# Revit family: QMXVP_with_1X3
name_source: partatom
category: Mechanical Equipment
units: mm (PartAtom-declared; Revit-internal decimal feet)

## family parameters
Always vertical = Yes
Cut with Voids When Loaded = No
Part Type = Normal
Room Calculation Point = No
Round Connector Dimension = Use Diameter
Shared = No
Work Plane-Based = No

## types (224) — shared parameters
0 = 0' - 0"
1" = 0' - 1"
1.5 = 0' - 1 1/2"
1/4 = 0' - 0 1/4"
135 = 135.00°
2" = 0' - 2"
2' = 2' - 0"
3" = 0' - 3"
3.125" = 0' - 3 1/8"
4" = 0' - 4"
5" = 0' - 5"
6" = 0' - 6"
Manufacturer = Loren Cook Company
ONE EIGTH = 0' - 0 1/8"
URL = www.lorencook.com

## per-type parameters (varying)
- 90_QMXVP-9L-1X3_Mixing_Box: (A/2)+.25"=1' - 2 1/4"; (A/2)-2"=1' - 0"; (NOZZLE_HEIGHT-(NOZZLE_HEIGHT/8*2))/2=0' - 10 1/2"; (NOZZLE_WB_OD-NOZZLE_TOP_OD)/2=0' - 2 3/8"; -A=-2' - 4"; A=2' - 4"; A+.5=2' - 4 1/2"; A/2=1' - 2"; B=5' - 5"; B/2=2' - 8 1/2"; C=2' - 6"; C/2=1' - 3"; DUAL_F=5' - 4 1/4"; DUAL_F+1"=5' - 5 1/4"; DUAL_G=5' - 3 5/16"; E=2' - 3 3/16"; GA=0' - 0 3/32"; LONG_RO=7' - 9 1/4"; MB_A=2' - 10"; MB_HT=2' - 5 3/16"; MB_HT+.25"=2' - 5 7/16"; MB_HT-2.75"=2' - 2 7/16"; MB_HT/2=1' - 2 19/32"; Model=QMXVP-1X3_Mixing Box; NOZZLE_BOTTOM_ID=1' - 0 13/16"; NOZZLE_BOTTOM_RAD=0' - 6 13/32"; NOZZLE_HEIGHT=2' - 4"; NOZZLE_HEIGHT/7*2=0' - 7"; NOZZLE_SIZE=9' - 0"; NOZZLE_TOP_OD=1' - 1 1/2"; NOZZLE_TOP_RAD=0' - 6 3/4"; NOZZLE_WB/4=0' - 4 19/32"; NOZZLE_WB_OD=1' - 11"; NOZZLE_WB_RAD=0' - 11 1/2"; NOZZLE_WB_RAD-2"=0' - 9 1/2"; RO=1' - 9"; RO/2=0' - 10 1/2"; RO2/2=0' - 10 1/2"; TRANSITION_TOP=3' - 1 1/16"; TRIPLE_F+1"=8' - 5"; TRIP_F=8' - 4"; TRIP_G=8' - 3 1/2"; TYPE=0' - 0"; Type Comments=Vari-Plume Laboratory Exhaust Mixed-Flow Inline Belt Drive With 1X3 Mixing Box; UNIT_HEIGHT=1' - 7 7/8"; UNIT_HEIGHT*.75=1' - 2 29/32"; UNIT_OD=1' - 0 13/16"; UNIT_RAD+((A/2)+.25")=1' - 8 21/32"; UNIT_RAD+((A/2)+.25")+4"=2' - 0 21/32"; UNIT_RADIUS=0' - 6 13/32"; UNIT_RADIUS*.6=0' - 5 25/32"; UNIT_RADIUS+4"=0' - 10 13/32"
- 490_QMXVP-49H-1X3_Mixing_Box: (A/2)+.25"=3' - 4 1/4"; (A/2)-2"=3' - 2"; (NOZZLE_HEIGHT-(NOZZLE_HEIGHT/8*2))/2=3' - 5 1/4"; (NOZZLE_WB_OD-NOZZLE_TOP_OD)/2=0' - 6 1/4"; -A=-6' - 8"; A=6' - 8"; A+.5=6' - 8 1/2"; A/2=3' - 4"; B=18' - 3"; B/2=9' - 1 1/2"; C=8' - 7"; C/2=4' - 3 1/2"; DUAL_F=16' - 0 3/4"; DUAL_F+1"=16' - 1 3/4"; DUAL_G=15' - 11"; E=6' - 6 1/2"; GA=0' - 0 1/8"; LONG_RO=24' - 9 1/4"; MB_A=9' - 5"; MB_HT=7' - 2 15/16"; MB_HT+.25"=7' - 3 3/16"; MB_HT-2.75"=7' - 0 3/16"; MB_HT/2=3' - 7 15/32"; Model=QMXVP-1X3_Mixing Box; NOZZLE_BOTTOM_ID=5' - 9 3/8"; NOZZLE_BOTTOM_RAD=2' - 10 11/16"; NOZZLE_HEIGHT=9' - 2"; NOZZLE_HEIGHT/7*2=2' - 3 1/2"; NOZZLE_SIZE=49' - 0"; NOZZLE_TOP_OD=6' - 4"; NOZZLE_TOP_RAD=3' - 2"; NOZZLE_WB/4=1' - 8 3/16"; NOZZLE_WB_OD=8' - 5"; NOZZLE_WB_RAD=4' - 2 1/2"; NOZZLE_WB_RAD-2"=4' - 0 1/2"; RO=6' - 0 1/4"; RO/2=3' - 0 1/8"; RO2/2=3' - 0 1/8"; TRANSITION_TOP=8' - 0 3/4"; TRIPLE_F+1"=25' - 6"; TRIP_F=25' - 5"; TRIP_G=25' - 3 1/2"; TYPE=0' - 0"; Type Comments=Vari-Plume Laboratory Exhaust Mixed-Flow Inline Belt Drive With 1X3 Mixing Box; UNIT_HEIGHT=6' - 8 1/2"; UNIT_HEIGHT*.75=5' - 0 3/8"; UNIT_OD=5' - 9 3/8"; UNIT_RAD+((A/2)+.25")=6' - 2 15/16"; UNIT_RAD+((A/2)+.25")+4"=6' - 6 15/16"; UNIT_RADIUS=2' - 10 11/16"; UNIT_RADIUS*.6=2' - 7 7/32"; UNIT_RADIUS+4"=3' - 2 11/16"
- 90_QMXVP-9H-1X3_Mixing_Box: (A/2)+.25"=1' - 2 1/4"; (A/2)-2"=1' - 0"; (NOZZLE_HEIGHT-(NOZZLE_HEIGHT/8*2))/2=0' - 10 1/2"; (NOZZLE_WB_OD-NOZZLE_TOP_OD)/2=0' - 2 3/8"; -A=-2' - 4"; A=2' - 4"; A+.5=2' - 4 1/2"; A/2=1' - 2"; B=5' - 5"; B/2=2' - 8 1/2"; C=2' - 6"; C/2=1' - 3"; DUAL_F=5' - 4 1/4"; DUAL_F+1"=5' - 5 1/4"; DUAL_G=5' - 3 5/16"; E=2' - 3 3/16"; GA=0' - 0 3/32"; LONG_RO=7' - 9 1/4"; MB_A=2' - 10"; MB_HT=2' - 5 3/16"; MB_HT+.25"=2' - 5 7/16"; MB_HT-2.75"=2' - 2 7/16"; MB_HT/2=1' - 2 19/32"; Model=QMXVP-1X3_Mixing Box; NOZZLE_BOTTOM_ID=1' - 0 13/16"; NOZZLE_BOTTOM_RAD=0' - 6 13/32"; NOZZLE_HEIGHT=2' - 4"; NOZZLE_HEIGHT/7*2=0' - 7"; NOZZLE_SIZE=9' - 0"; NOZZLE_TOP_OD=1' - 1 1/2"; NOZZLE_TOP_RAD=0' - 6 3/4"; NOZZLE_WB/4=0' - 4 19/32"; NOZZLE_WB_OD=1' - 11"; NOZZLE_WB_RAD=0' - 11 1/2"; NOZZLE_WB_RAD-2"=0' - 9 1/2"; RO=1' - 9"; RO/2=0' - 10 1/2"; RO2/2=0' - 10 1/2"; TRANSITION_TOP=3' - 1 1/16"; TRIPLE_F+1"=8' - 5"; TRIP_F=8' - 4"; TRIP_G=8' - 3 1/2"; TYPE=0' - 0"; Type Comments=Vari-Plume Laboratory Exhaust Mixed-Flow Inline Belt Drive With 1X3 Mixing Box; UNIT_HEIGHT=1' - 7 7/8"; UNIT_HEIGHT*.75=1' - 2 29/32"; UNIT_OD=1' - 0 13/16"; UNIT_RAD+((A/2)+.25")=1' - 8 21/32"; UNIT_RAD+((A/2)+.25")+4"=2' - 0 21/32"; UNIT_RADIUS=0' - 6 13/32"; UNIT_RADIUS*.6=0' - 5 25/32"; UNIT_RADIUS+4"=0' - 10 13/32"
- 120_QMXVP-9L-1X3_Mixing_Box: (A/2)+.25"=1' - 2 1/4"; (A/2)-2"=1' - 0"; (NOZZLE_HEIGHT-(NOZZLE_HEIGHT/8*2))/2=0' - 10 1/2"; (NOZZLE_WB_OD-NOZZLE_TOP_OD)/2=0' - 2 3/8"; -A=-2' - 4"; A=2' - 4"; A+.5=2' - 4 1/2"; A/2=1' - 2"; B=5' - 11"; B/2=2' - 11 1/2"; C=3' - 1"; C/2=1' - 6 1/2"; DUAL_F=5' - 4 1/4"; DUAL_F+1"=5' - 5 1/4"; DUAL_G=5' - 3 5/16"; E=2' - 3 3/16"; GA=0' - 0 3/32"; LONG_RO=7' - 9 1/4"; MB_A=2' - 11"; MB_HT=2' - 7 7/16"; MB_HT+.25"=2' - 7 11/16"; MB_HT-2.75"=2' - 4 11/16"; MB_HT/2=1' - 3 23/32"; Model=QMXVP-1X3_Mixing Box; NOZZLE_BOTTOM_ID=1' - 0 13/16"; NOZZLE_BOTTOM_RAD=0' - 6 13/32"; NOZZLE_HEIGHT=2' - 4"; NOZZLE_HEIGHT/7*2=0' - 7"; NOZZLE_SIZE=9' - 0"; NOZZLE_TOP_OD=1' - 1 1/2"; NOZZLE_TOP_RAD=0' - 6 3/4"; NOZZLE_WB/4=0' - 4 19/32"; NOZZLE_WB_OD=1' - 11"; NOZZLE_WB_RAD=0' - 11 1/2"; NOZZLE_WB_RAD-2"=0' - 9 1/2"; RO=1' - 9"; RO/2=0' - 10 1/2"; RO2/2=0' - 10 1/2"; TRANSITION_TOP=3' - 7 3/16"; TRIPLE_F+1"=8' - 5"; TRIP_F=8' - 4"; TRIP_G=8' - 3 1/2"; TYPE=0' - 0"; Type Comments=Vari-Plume Laboratory Exhaust Mixed-Flow Inline Belt Drive With 1X3 Mixing Box; UNIT_HEIGHT=1' - 7 7/8"; UNIT_HEIGHT*.75=1' - 2 29/32"; UNIT_OD=1' - 5 1/16"; UNIT_RAD+((A/2)+.25")=1' - 10 25/32"; UNIT_RAD+((A/2)+.25")+4"=2' - 2 25/32"; UNIT_RADIUS=0' - 8 17/32"; UNIT_RADIUS*.6=0' - 7 11/16"; UNIT_RADIUS+4"=1' - 0 17/32"
- 120_QMXVP-9H-1X3_Mixing_Box: (A/2)+.25"=1' - 2 1/4"; (A/2)-2"=1' - 0"; (NOZZLE_HEIGHT-(NOZZLE_HEIGHT/8*2))/2=0' - 10 1/2"; (NOZZLE_WB_OD-NOZZLE_TOP_OD)/2=0' - 2 3/8"; -A=-2' - 4"; A=2' - 4"; A+.5=2' - 4 1/2"; A/2=1' - 2"; B=5' - 11"; B/2=2' - 11 1/2"; C=3' - 1"; C/2=1' - 6 1/2"; DUAL_F=5' - 4 1/4"; DUAL_F+1"=5' - 5 1/4"; DUAL_G=5' - 3 5/16"; E=2' - 3 3/16"; GA=0' - 0 3/32"; LONG_RO=7' - 9 1/4"; MB_A=2' - 11"; MB_HT=2' - 7 7/16"; MB_HT+.25"=2' - 7 11/16"; MB_HT-2.75"=2' - 4 11/16"; MB_HT/2=1' - 3 23/32"; Model=QMXVP-1X3_Mixing Box; NOZZLE_BOTTOM_ID=1' - 0 13/16"; NOZZLE_BOTTOM_RAD=0' - 6 13/32"; NOZZLE_HEIGHT=2' - 4"; NOZZLE_HEIGHT/7*2=0' - 7"; NOZZLE_SIZE=9' - 0"; NOZZLE_TOP_OD=1' - 1 1/2"; NOZZLE_TOP_RAD=0' - 6 3/4"; NOZZLE_WB/4=0' - 4 19/32"; NOZZLE_WB_OD=1' - 11"; NOZZLE_WB_RAD=0' - 11 1/2"; NOZZLE_WB_RAD-2"=0' - 9 1/2"; RO=1' - 9"; RO/2=0' - 10 1/2"; RO2/2=0' - 10 1/2"; TRANSITION_TOP=3' - 7 3/16"; TRIPLE_F+1"=8' - 5"; TRIP_F=8' - 4"; TRIP_G=8' - 3 1/2"; TYPE=0' - 0"; Type Comments=Vari-Plume Laboratory Exhaust Mixed-Flow Inline Belt Drive With 1X3 Mixing Box; UNIT_HEIGHT=1' - 7 7/8"; UNIT_HEIGHT*.75=1' - 2 29/32"; UNIT_OD=1' - 5 1/16"; UNIT_RAD+((A/2)+.25")=1' - 10 25/32"; UNIT_RAD+((A/2)+.25")+4"=2' - 2 25/32"; UNIT_RADIUS=0' - 8 17/32"; UNIT_RADIUS*.6=0' - 7 11/16"; UNIT_RADIUS+4"=1' - 0 17/32"
- 120_QMXVP-12L-1X3_Mixing_Box: (A/2)+.25"=1' - 2 1/4"; (A/2)-2"=1' - 0"; (NOZZLE_HEIGHT-(NOZZLE_HEIGHT/8*2))/2=1' - 0"; (NOZZLE_WB_OD-NOZZLE_TOP_OD)/2=0' - 2 1/8"; -A=-2' - 4"; A=2' - 4"; A+.5=2' - 4 1/2"; A/2=1' - 2"; B=5' - 11"; B/2=2' - 11 1/2"; C=3' - 1"; C/2=1' - 6 1/2"; DUAL_F=5' - 4 1/4"; DUAL_F+1"=5' - 5 1/4"; DUAL_G=5' - 3 5/16"; E=2' - 3 3/16"; GA=0' - 0 3/32"; LONG_RO=7' - 9 1/4"; MB_A=2' - 11"; MB_HT=2' - 7 7/16"; MB_HT+.25"=2' - 7 11/16"; MB_HT-2.75"=2' - 4 11/16"; MB_HT/2=1' - 3 23/32"; Model=QMXVP-1X3_Mixing Box; NOZZLE_BOTTOM_ID=1' - 5 1/16"; NOZZLE_BOTTOM_RAD=0' - 8 17/32"; NOZZLE_HEIGHT=2' - 8"; NOZZLE_HEIGHT/7*2=0' - 8"; NOZZLE_SIZE=12' - 0"; NOZZLE_TOP_OD=1' - 7 1/2"; NOZZLE_TOP_RAD=0' - 9 3/4"; NOZZLE_WB/4=0' - 5 19/32"; NOZZLE_WB_OD=2' - 4"; NOZZLE_WB_RAD=1' - 2"; NOZZLE_WB_RAD-2"=1' - 0"; RO=1' - 9"; RO/2=0' - 10 1/2"; RO2/2=0' - 10 1/2"; TRANSITION_TOP=3' - 3 7/16"; TRIPLE_F+1"=8' - 5"; TRIP_F=8' - 4"; TRIP_G=8' - 3 1/2"; TYPE=0' - 0"; Type Comments=Vari-Plume Laboratory Exhaust Mixed-Flow Inline Belt Drive With 1X3 Mixing Box; UNIT_HEIGHT=1' - 7 7/8"; UNIT_HEIGHT*.75=1' - 2 29/32"; UNIT_OD=1' - 5 1/16"; UNIT_RAD+((A/2)+.25")=1' - 10 25/32"; UNIT_RAD+((A/2)+.25")+4"=2' - 2 25/32"; UNIT_RADIUS=0' - 8 17/32"; UNIT_RADIUS*.6=0' - 7 11/16"; UNIT_RADIUS+4"=1' - 0 17/32"
- 120_QMXVP-12H-1X3_Mixing_Box: (A/2)+.25"=1' - 2 1/4"; (A/2)-2"=1' - 0"; (NOZZLE_HEIGHT-(NOZZLE_HEIGHT/8*2))/2=1' - 0"; (NOZZLE_WB_OD-NOZZLE_TOP_OD)/2=0' - 2 1/8"; -A=-2' - 4"; A=2' - 4"; A+.5=2' - 4 1/2"; A/2=1' - 2"; B=5' - 11"; B/2=2' - 11 1/2"; C=3' - 1"; C/2=1' - 6 1/2"; DUAL_F=5' - 4 1/4"; DUAL_F+1"=5' - 5 1/4"; DUAL_G=5' - 3 5/16"; E=2' - 3 3/16"; GA=0' - 0 3/32"; LONG_RO=7' - 9 1/4"; MB_A=2' - 11"; MB_HT=2' - 7 7/16"; MB_HT+.25"=2' - 7 11/16"; MB_HT-2.75"=2' - 4 11/16"; MB_HT/2=1' - 3 23/32"; Model=QMXVP-1X3_Mixing Box; NOZZLE_BOTTOM_ID=1' - 5 1/16"; NOZZLE_BOTTOM_RAD=0' - 8 17/32"; NOZZLE_HEIGHT=2' - 8"; NOZZLE_HEIGHT/7*2=0' - 8"; NOZZLE_SIZE=12' - 0"; NOZZLE_TOP_OD=1' - 7 1/2"; NOZZLE_TOP_RAD=0' - 9 3/4"; NOZZLE_WB/4=0' - 5 19/32"; NOZZLE_WB_OD=2' - 4"; NOZZLE_WB_RAD=1' - 2"; NOZZLE_WB_RAD-2"=1' - 0"; RO=1' - 9"; RO/2=0' - 10 1/2"; RO2/2=0' - 10 1/2"; TRANSITION_TOP=3' - 3 7/16"; TRIPLE_F+1"=8' - 5"; TRIP_F=8' - 4"; TRIP_G=8' - 3 1/2"; TYPE=0' - 0"; Type Comments=Vari-Plume Laboratory Exhaust Mixed-Flow Inline Belt Drive With 1X3 Mixing Box; UNIT_HEIGHT=1' - 7 7/8"; UNIT_HEIGHT*.75=1' - 2 29/32"; UNIT_OD=1' - 5 1/16"; UNIT_RAD+((A/2)+.25")=1' - 10 25/32"; UNIT_RAD+((A/2)+.25")+4"=2' - 2 25/32"; UNIT_RADIUS=0' - 8 17/32"; UNIT_RADIUS*.6=0' - 7 11/16"; UNIT_RADIUS+4"=1' - 0 17/32"
- 135_QMXVP-9L-1X3_Mixing_Box: (A/2)+.25"=1' - 2 1/4"; (A/2)-2"=1' - 0"; (NOZZLE_HEIGHT-(NOZZLE_HEIGHT/8*2))/2=0' - 10 1/2"; (NOZZLE_WB_OD-NOZZLE_TOP_OD)/2=0' - 2 3/8"; -A=-2' - 4"; A=2' - 4"; A+.5=2' - 4 1/2"; A/2=1' - 2"; B=6' - 5"; B/2=3' - 2 1/2"; C=3' - 3"; C/2=1' - 7 1/2"; DUAL_F=5' - 4 1/4"; DUAL_F+1"=5' - 5 1/4"; DUAL_G=5' - 3 5/16"; E=2' - 3 1/8"; GA=0' - 0 3/32"; LONG_RO=7' - 9 1/4"; MB_A=3' - 0"; MB_HT=2' - 9 7/16"; MB_HT+.25"=2' - 9 11/16"; MB_HT-2.75"=2' - 6 11/16"; MB_HT/2=1' - 4 23/32"; Model=QMXVP-1X3_Mixing Box; NOZZLE_BOTTOM_ID=1' - 0 13/16"; NOZZLE_BOTTOM_RAD=0' - 6 13/32"; NOZZLE_HEIGHT=2' - 4"; NOZZLE_HEIGHT/7*2=0' - 7"; NOZZLE_SIZE=9' - 0"; NOZZLE_TOP_OD=1' - 1 1/2"; NOZZLE_TOP_RAD=0' - 6 3/4"; NOZZLE_WB/4=0' - 4 19/32"; NOZZLE_WB_OD=1' - 11"; NOZZLE_WB_RAD=0' - 11 1/2"; NOZZLE_WB_RAD-2"=0' - 9 1/2"; RO=1' - 8 15/16"; RO/2=0' - 10 15/32"; RO2/2=0' - 10 15/32"; TRANSITION_TOP=4' - 0 11/16"; TRIPLE_F+1"=8' - 5"; TRIP_F=8' - 4"; TRIP_G=8' - 3 1/2"; TYPE=0' - 0"; Type Comments=Vari-Plume Laboratory Exhaust Mixed-Flow Inline Belt Drive With 1X3 Mixing Box; UNIT_HEIGHT=2' - 3"; UNIT_HEIGHT*.75=1' - 8 1/4"; UNIT_OD=1' - 7 1/4"; UNIT_RAD+((A/2)+.25")=1' - 11 7/8"; UNIT_RAD+((A/2)+.25")+4"=2' - 3 7/8"; UNIT_RADIUS=0' - 9 5/8"; UNIT_RADIUS*.6=0' - 8 21/32"; UNIT_RADIUS+4"=1' - 1 5/8"
- 135_QMXVP-9H-1X3_Mixing_Box: (A/2)+.25"=1' - 2 1/4"; (A/2)-2"=1' - 0"; (NOZZLE_HEIGHT-(NOZZLE_HEIGHT/8*2))/2=0' - 10 1/2"; (NOZZLE_WB_OD-NOZZLE_TOP_OD)/2=0' - 2 3/8"; -A=-2' - 4"; A=2' - 4"; A+.5=2' - 4 1/2"; A/2=1' - 2"; B=6' - 5"; B/2=3' - 2 1/2"; C=3' - 3"; C/2=1' - 7 1/2"; DUAL_F=5' - 4 1/4"; DUAL_F+1"=5' - 5 1/4"; DUAL_G=5' - 3 5/16"; E=2' - 3 1/8"; GA=0' - 0 3/32"; LONG_RO=7' - 9 1/4"; MB_A=3' - 0"; MB_HT=2' - 9 7/16"; MB_HT+.25"=2' - 9 11/16"; MB_HT-2.75"=2' - 6 11/16"; MB_HT/2=1' - 4 23/32"; Model=QMXVP-1X3_Mixing Box; NOZZLE_BOTTOM_ID=1' - 0 13/16"; NOZZLE_BOTTOM_RAD=0' - 6 13/32"; NOZZLE_HEIGHT=2' - 4"; NOZZLE_HEIGHT/7*2=0' - 7"; NOZZLE_SIZE=9' - 0"; NOZZLE_TOP_OD=1' - 1 1/2"; NOZZLE_TOP_RAD=0' - 6 3/4"; NOZZLE_WB/4=0' - 4 19/32"; NOZZLE_WB_OD=1' - 11"; NOZZLE_WB_RAD=0' - 11 1/2"; NOZZLE_WB_RAD-2"=0' - 9 1/2"; RO=1' - 8 15/16"; RO/2=0' - 10 15/32"; RO2/2=0' - 10 15/32"; TRANSITION_TOP=4' - 0 11/16"; TRIPLE_F+1"=8' - 5"; TRIP_F=8' - 4"; TRIP_G=8' - 3 1/2"; TYPE=0' - 0"; Type Comments=Vari-Plume Laboratory Exhaust Mixed-Flow Inline Belt Drive With 1X3 Mixing Box; UNIT_HEIGHT=2' - 3"; UNIT_HEIGHT*.75=1' - 8 1/4"; UNIT_OD=1' - 7 1/4"; UNIT_RAD+((A/2)+.25")=1' - 11 7/8"; UNIT_RAD+((A/2)+.25")+4"=2' - 3 7/8"; UNIT_RADIUS=0' - 9 5/8"; UNIT_RADIUS*.6=0' - 8 21/32"; UNIT_RADIUS+4"=1' - 1 5/8"
- 150_QMXVP-9L-1X3_Mixing_Box: (A/2)+.25"=1' - 3 1/4"; (A/2)-2"=1' - 1"; (NOZZLE_HEIGHT-(NOZZLE_HEIGHT/8*2))/2=0' - 10 1/2"; (NOZZLE_WB_OD-NOZZLE_TOP_OD)/2=0' - 2 3/8"; -A=-2' - 6"; A=2' - 6"; A+.5=2' - 6 1/2"; A/2=1' - 3"; B=7' - 3"; B/2=3' - 7 1/2"; C=3' - 6"; C/2=1' - 9"; DUAL_F=5' - 8 1/4"; DUAL_F+1"=5' - 9 1/4"; DUAL_G=5' - 7 5/16"; E=2' - 5 1/8"; GA=0' - 0 3/32"; LONG_RO=8' - 3 1/4"; MB_A=3' - 2"; MB_HT=2' - 11 3/16"; MB_HT+.25"=2' - 11 7/16"; MB_HT-2.75"=2' - 8 7/16"; MB_HT/2=1' - 5 19/32"; Model=QMXVP-1X3_Mixing Box; NOZZLE_BOTTOM_ID=1' - 0 13/16"; NOZZLE_BOTTOM_RAD=0' - 6 13/32"; NOZZLE_HEIGHT=2' - 4"; NOZZLE_HEIGHT/7*2=0' - 7"; NOZZLE_SIZE=9' - 0"; NOZZLE_TOP_OD=1' - 1 1/2"; NOZZLE_TOP_RAD=0' - 6 3/4"; NOZZLE_WB/4=0' - 4 19/32"; NOZZLE_WB_OD=1' - 11"; NOZZLE_WB_RAD=0' - 11 1/2"; NOZZLE_WB_RAD-2"=0' - 9 1/2"; RO=1' - 10 15/16"; RO/2=0' - 11 15/32"; RO2/2=0' - 11 15/32"; TRANSITION_TOP=4' - 6 1/4"; TRIPLE_F+1"=8' - 11"; TRIP_F=8' - 10"; TRIP_G=8' - 9 1/2"; TYPE=0' - 0"; Type Comments=Vari-Plume Laboratory Exhaust Mixed-Flow Inline Belt Drive With 1X3 Mixing Box; UNIT_HEIGHT=2' - 6"; UNIT_HEIGHT*.75=1' - 10 1/2"; UNIT_OD=1' - 9 3/8"; UNIT_RAD+((A/2)+.25")=2' - 1 15/16"; UNIT_RAD+((A/2)+.25")+4"=2' - 5 15/16"; UNIT_RADIUS=0' - 10 11/16"; UNIT_RADIUS*.6=0' - 9 5/8"; UNIT_RADIUS+4"=1' - 2 11/16"
- 135_QMXVP-12L-1X3_Mixing_Box: (A/2)+.25"=1' - 2 1/4"; (A/2)-2"=1' - 0"; (NOZZLE_HEIGHT-(NOZZLE_HEIGHT/8*2))/2=1' - 0"; (NOZZLE_WB_OD-NOZZLE_TOP_OD)/2=0' - 2 1/8"; -A=-2' - 4"; A=2' - 4"; A+.5=2' - 4 1/2"; A/2=1' - 2"; B=6' - 5"; B/2=3' - 2 1/2"; C=3' - 3"; C/2=1' - 7 1/2"; DUAL_F=5' - 4 1/4"; DUAL_F+1"=5' - 5 1/4"; DUAL_G=5' - 3 5/16"; E=2' - 3 1/8"; GA=0' - 0 3/32"; LONG_RO=7' - 9 1/4"; MB_A=3' - 0"; MB_HT=2' - 9 7/16"; MB_HT+.25"=2' - 9 11/16"; MB_HT-2.75"=2' - 6 11/16"; MB_HT/2=1' - 4 23/32"; Model=QMXVP-1X3_Mixing Box; NOZZLE_BOTTOM_ID=1' - 5 1/16"; NOZZLE_BOTTOM_RAD=0' - 8 17/32"; NOZZLE_HEIGHT=2' - 8"; NOZZLE_HEIGHT/7*2=0' - 8"; NOZZLE_SIZE=12' - 0"; NOZZLE_TOP_OD=1' - 7 1/2"; NOZZLE_TOP_RAD=0' - 9 3/4"; NOZZLE_WB/4=0' - 5 19/32"; NOZZLE_WB_OD=2' - 4"; NOZZLE_WB_RAD=1' - 2"; NOZZLE_WB_RAD-2"=1' - 0"; RO=1' - 8 15/16"; RO/2=0' - 10 15/32"; RO2/2=0' - 10 15/32"; TRANSITION_TOP=3' - 4 11/16"; TRIPLE_F+1"=8' - 5"; TRIP_F=8' - 4"; TRIP_G=8' - 3 1/2"; TYPE=0' - 0"; Type Comments=Vari-Plume Laboratory Exhaust Mixed-Flow Inline Belt Drive With 1X3 Mixing Box; UNIT_HEIGHT=2' - 3"; UNIT_HEIGHT*.75=1' - 8 1/4"; UNIT_OD=1' - 7 1/4"; UNIT_RAD+((A/2)+.25")=1' - 11 7/8"; UNIT_RAD+((A/2)+.25")+4"=2' - 3 7/8"; UNIT_RADIUS=0' - 9 5/8"; UNIT_RADIUS*.6=0' - 8 21/32"; UNIT_RADIUS+4"=1' - 1 5/8"
- 135_QMXVP-12H-1X3_Mixing_Box: (A/2)+.25"=1' - 2 1/4"; (A/2)-2"=1' - 0"; (NOZZLE_HEIGHT-(NOZZLE_HEIGHT/8*2))/2=1' - 0"; (NOZZLE_WB_OD-NOZZLE_TOP_OD)/2=0' - 2 1/8"; -A=-2' - 4"; A=2' - 4"; A+.5=2' - 4 1/2"; A/2=1' - 2"; B=6' - 5"; B/2=3' - 2 1/2"; C=3' - 3"; C/2=1' - 7 1/2"; DUAL_F=5' - 4 1/4"; DUAL_F+1"=5' - 5 1/4"; DUAL_G=5' - 3 5/16"; E=2' - 3 1/8"; GA=0' - 0 3/32"; LONG_RO=7' - 9 1/4"; MB_A=3' - 0"; MB_HT=2' - 9 7/16"; MB_HT+.25"=2' - 9 11/16"; MB_HT-2.75"=2' - 6 11/16"; MB_HT/2=1' - 4 23/32"; Model=QMXVP-1X3_Mixing Box; NOZZLE_BOTTOM_ID=1' - 5 1/16"; NOZZLE_BOTTOM_RAD=0' - 8 17/32"; NOZZLE_HEIGHT=2' - 8"; NOZZLE_HEIGHT/7*2=0' - 8"; NOZZLE_SIZE=12' - 0"; NOZZLE_TOP_OD=1' - 7 1/2"; NOZZLE_TOP_RAD=0' - 9 3/4"; NOZZLE_WB/4=0' - 5 19/32"; NOZZLE_WB_OD=2' - 4"; NOZZLE_WB_RAD=1' - 2"; NOZZLE_WB_RAD-2"=1' - 0"; RO=1' - 8 15/16"; RO/2=0' - 10 15/32"; RO2/2=0' - 10 15/32"; TRANSITION_TOP=3' - 4 11/16"; TRIPLE_F+1"=8' - 5"; TRIP_F=8' - 4"; TRIP_G=8' - 3 1/2"; TYPE=0' - 0"; Type Comments=Vari-Plume Laboratory Exhaust Mixed-Flow Inline Belt Drive With 1X3 Mixing Box; UNIT_HEIGHT=2' - 3"; UNIT_HEIGHT*.75=1' - 8 1/4"; UNIT_OD=1' - 7 1/4"; UNIT_RAD+((A/2)+.25")=1' - 11 7/8"; UNIT_RAD+((A/2)+.25")+4"=2' - 3 7/8"; UNIT_RADIUS=0' - 9 5/8"; UNIT_RADIUS*.6=0' - 8 21/32"; UNIT_RADIUS+4"=1' - 1 5/8"
- 150_QMXVP-9H-1X3_Mixing_Box: (A/2)+.25"=1' - 3 1/4"; (A/2)-2"=1' - 1"; (NOZZLE_HEIGHT-(NOZZLE_HEIGHT/8*2))/2=0' - 10 1/2"; (NOZZLE_WB_OD-NOZZLE_TOP_OD)/2=0' - 2 3/8"; -A=-2' - 6"; A=2' - 6"; A+.5=2' - 6 1/2"; A/2=1' - 3"; B=7' - 3"; B/2=3' - 7 1/2"; C=3' - 6"; C/2=1' - 9"; DUAL_F=5' - 8 1/4"; DUAL_F+1"=5' - 9 1/4"; DUAL_G=5' - 7 5/16"; E=2' - 5 1/8"; GA=0' - 0 3/32"; LONG_RO=8' - 3 1/4"; MB_A=3' - 2"; MB_HT=2' - 11 3/16"; MB_HT+.25"=2' - 11 7/16"; MB_HT-2.75"=2' - 8 7/16"; MB_HT/2=1' - 5 19/32"; Model=QMXVP-1X3_Mixing Box; NOZZLE_BOTTOM_ID=1' - 0 13/16"; NOZZLE_BOTTOM_RAD=0' - 6 13/32"; NOZZLE_HEIGHT=2' - 4"; NOZZLE_HEIGHT/7*2=0' - 7"; NOZZLE_SIZE=9' - 0"; NOZZLE_TOP_OD=1' - 1 1/2"; NOZZLE_TOP_RAD=0' - 6 3/4"; NOZZLE_WB/4=0' - 4 19/32"; NOZZLE_WB_OD=1' - 11"; NOZZLE_WB_RAD=0' - 11 1/2"; NOZZLE_WB_RAD-2"=0' - 9 1/2"; RO=1' - 10 15/16"; RO/2=0' - 11 15/32"; RO2/2=0' - 11 15/32"; TRANSITION_TOP=4' - 6 1/4"; TRIPLE_F+1"=8' - 11"; TRIP_F=8' - 10"; TRIP_G=8' - 9 1/2"; TYPE=0' - 0"; Type Comments=Vari-Plume Laboratory Exhaust Mixed-Flow Inline Belt Drive With 1X3 Mixing Box; UNIT_HEIGHT=2' - 6"; UNIT_HEIGHT*.75=1' - 10 1/2"; UNIT_OD=1' - 9 3/8"; UNIT_RAD+((A/2)+.25")=2' - 1 15/16"; UNIT_RAD+((A/2)+.25")+4"=2' - 5 15/16"; UNIT_RADIUS=0' - 10 11/16"; UNIT_RADIUS*.6=0' - 9 5/8"; UNIT_RADIUS+4"=1' - 2 11/16"
- 150_QMXVP-12L-1X3_Mixing_Box: (A/2)+.25"=1' - 3 1/4"; (A/2)-2"=1' - 1"; (NOZZLE_HEIGHT-(NOZZLE_HEIGHT/8*2))/2=1' - 0"; (NOZZLE_WB_OD-NOZZLE_TOP_OD)/2=0' - 2 1/8"; -A=-2' - 6"; A=2' - 6"; A+.5=2' - 6 1/2"; A/2=1' - 3"; B=7' - 3"; B/2=3' - 7 1/2"; C=3' - 6"; C/2=1' - 9"; DUAL_F=5' - 8 1/4"; DUAL_F+1"=5' - 9 1/4"; DUAL_G=5' - 7 5/16"; E=2' - 5 1/8"; GA=0' - 0 3/32"; LONG_RO=8' - 3 1/4"; MB_A=3' - 2"; MB_HT=2' - 11 3/16"; MB_HT+.25"=2' - 11 7/16"; MB_HT-2.75"=2' - 8 7/16"; MB_HT/2=1' - 5 19/32"; Model=QMXVP-1X3_Mixing Box; NOZZLE_BOTTOM_ID=1' - 5 1/16"; NOZZLE_BOTTOM_RAD=0' - 8 17/32"; NOZZLE_HEIGHT=2' - 8"; NOZZLE_HEIGHT/7*2=0' - 8"; NOZZLE_SIZE=12' - 0"; NOZZLE_TOP_OD=1' - 7 1/2"; NOZZLE_TOP_RAD=0' - 9 3/4"; NOZZLE_WB/4=0' - 5 19/32"; NOZZLE_WB_OD=2' - 4"; NOZZLE_WB_RAD=1' - 2"; NOZZLE_WB_RAD-2"=1' - 0"; RO=1' - 10 15/16"; RO/2=0' - 11 15/32"; RO2/2=0' - 11 15/32"; TRANSITION_TOP=3' - 10 1/4"; TRIPLE_F+1"=8' - 11"; TRIP_F=8' - 10"; TRIP_G=8' - 9 1/2"; TYPE=0' - 0"; Type Comments=Vari-Plume Laboratory Exhaust Mixed-Flow Inline Belt Drive With 1X3 Mixing Box; UNIT_HEIGHT=2' - 6"; UNIT_HEIGHT*.75=1' - 10 1/2"; UNIT_OD=1' - 9 3/8"; UNIT_RAD+((A/2)+.25")=2' - 1 15/16"; UNIT_RAD+((A/2)+.25")+4"=2' - 5 15/16"; UNIT_RADIUS=0' - 10 11/16"; UNIT_RADIUS*.6=0' - 9 5/8"; UNIT_RADIUS+4"=1' - 2 11/16"
- 150_QMXVP-12H-1X3_Mixing_Box: (A/2)+.25"=1' - 3 1/4"; (A/2)-2"=1' - 1"; (NOZZLE_HEIGHT-(NOZZLE_HEIGHT/8*2))/2=1' - 0"; (NOZZLE_WB_OD-NOZZLE_TOP_OD)/2=0' - 2 1/8"; -A=-2' - 6"; A=2' - 6"; A+.5=2' - 6 1/2"; A/2=1' - 3"; B=7' - 3"; B/2=3' - 7 1/2"; C=3' - 6"; C/2=1' - 9"; DUAL_F=5' - 8 1/4"; DUAL_F+1"=5' - 9 1/4"; DUAL_G=5' - 7 5/16"; E=2' - 5 1/8"; GA=0' - 0 3/32"; LONG_RO=8' - 3 1/4"; MB_A=3' - 2"; MB_HT=2' - 11 3/16"; MB_HT+.25"=2' - 11 7/16"; MB_HT-2.75"=2' - 8 7/16"; MB_HT/2=1' - 5 19/32"; Model=QMXVP-1X3_Mixing Box; NOZZLE_BOTTOM_ID=1' - 5 1/16"; NOZZLE_BOTTOM_RAD=0' - 8 17/32"; NOZZLE_HEIGHT=2' - 8"; NOZZLE_HEIGHT/7*2=0' - 8"; NOZZLE_SIZE=12' - 0"; NOZZLE_TOP_OD=1' - 7 1/2"; NOZZLE_TOP_RAD=0' - 9 3/4"; NOZZLE_WB/4=0' - 5 19/32"; NOZZLE_WB_OD=2' - 4"; NOZZLE_WB_RAD=1' - 2"; NOZZLE_WB_RAD-2"=1' - 0"; RO=1' - 10 15/16"; RO/2=0' - 11 15/32"; RO2/2=0' - 11 15/32"; TRANSITION_TOP=3' - 10 1/4"; TRIPLE_F+1"=8' - 11"; TRIP_F=8' - 10"; TRIP_G=8' - 9 1/2"; TYPE=0' - 0"; Type Comments=Vari-Plume Laboratory Exhaust Mixed-Flow Inline Belt Drive With 1X3 Mixing Box; UNIT_HEIGHT=2' - 6"; UNIT_HEIGHT*.75=1' - 10 1/2"; UNIT_OD=1' - 9 3/8"; UNIT_RAD+((A/2)+.25")=2' - 1 15/16"; UNIT_RAD+((A/2)+.25")+4"=2' - 5 15/16"; UNIT_RADIUS=0' - 10 11/16"; UNIT_RADIUS*.6=0' - 9 5/8"; UNIT_RADIUS+4"=1' - 2 11/16"
- 150_QMXVP-15L-1X3_Mixing_Box: (A/2)+.25"=1' - 3 1/4"; (A/2)-2"=1' - 1"; (NOZZLE_HEIGHT-(NOZZLE_HEIGHT/8*2))/2=1' - 4 1/8"; (NOZZLE_WB_OD-NOZZLE_TOP_OD)/2=0' - 3 1/4"; -A=-2' - 6"; A=2' - 6"; A+.5=2' - 6 1/2"; A/2=1' - 3"; B=7' - 3"; B/2=3' - 7 1/2"; C=3' - 6"; C/2=1' - 9"; DUAL_F=5' - 8 1/4"; DUAL_F+1"=5' - 9 1/4"; DUAL_G=5' - 7 5/16"; E=2' - 5 1/8"; GA=0' - 0 3/32"; LONG_RO=8' - 3 1/4"; MB_A=3' - 2"; MB_HT=2' - 11 3/16"; MB_HT+.25"=2' - 11 7/16"; MB_HT-2.75"=2' - 8 7/16"; MB_HT/2=1' - 5 19/32"; Model=QMXVP-1X3_Mixing Box; NOZZLE_BOTTOM_ID=1' - 9 3/8"; NOZZLE_BOTTOM_RAD=0' - 10 11/16"; NOZZLE_HEIGHT=3' - 7"; NOZZLE_HEIGHT/7*2=0' - 10 3/4"; NOZZLE_SIZE=15' - 0"; NOZZLE_TOP_OD=1' - 11"; NOZZLE_TOP_RAD=0' - 11 1/2"; NOZZLE_WB/4=0' - 7 3/16"; NOZZLE_WB_OD=3' - 0"; NOZZLE_WB_RAD=1' - 6"; NOZZLE_WB_RAD-2"=1' - 4"; RO=1' - 10 15/16"; RO/2=0' - 11 15/32"; RO2/2=0' - 11 15/32"; TRANSITION_TOP=3' - 7 5/16"; TRIPLE_F+1"=8' - 11"; TRIP_F=8' - 10"; TRIP_G=8' - 9 1/2"; TYPE=0' - 0"; Type Comments=Vari-Plume Laboratory Exhaust Mixed-Flow Inline Belt Drive With 1X3 Mixing Box; UNIT_HEIGHT=2' - 6"; UNIT_HEIGHT*.75=1' - 10 1/2"; UNIT_OD=1' - 9 3/8"; UNIT_RAD+((A/2)+.25")=2' - 1 15/16"; UNIT_RAD+((A/2)+.25")+4"=2' - 5 15/16"; UNIT_RADIUS=0' - 10 11/16"; UNIT_RADIUS*.6=0' - 9 5/8"; UNIT_RADIUS+4"=1' - 2 11/16"
- 150_QMXVP-15H-1X3_Mixing_Box: (A/2)+.25"=1' - 3 1/4"; (A/2)-2"=1' - 1"; (NOZZLE_HEIGHT-(NOZZLE_HEIGHT/8*2))/2=1' - 4 1/8"; (NOZZLE_WB_OD-NOZZLE_TOP_OD)/2=0' - 3 1/4"; -A=-2' - 6"; A=2' - 6"; A+.5=2' - 6 1/2"; A/2=1' - 3"; B=7' - 3"; B/2=3' - 7 1/2"; C=3' - 6"; C/2=1' - 9"; DUAL_F=5' - 8 1/4"; DUAL_F+1"=5' - 9 1/4"; DUAL_G=5' - 7 5/16"; E=2' - 5 1/8"; GA=0' - 0 3/32"; LONG_RO=8' - 3 1/4"; MB_A=3' - 2"; MB_HT=2' - 11 3/16"; MB_HT+.25"=2' - 11 7/16"; MB_HT-2.75"=2' - 8 7/16"; MB_HT/2=1' - 5 19/32"; Model=QMXVP-1X3_Mixing Box; NOZZLE_BOTTOM_ID=1' - 9 3/8"; NOZZLE_BOTTOM_RAD=0' - 10 11/16"; NOZZLE_HEIGHT=3' - 7"; NOZZLE_HEIGHT/7*2=0' - 10 3/4"; NOZZLE_SIZE=15' - 0"; NOZZLE_TOP_OD=1' - 11"; NOZZLE_TOP_RAD=0' - 11 1/2"; NOZZLE_WB/4=0' - 7 3/16"; NOZZLE_WB_OD=3' - 0"; NOZZLE_WB_RAD=1' - 6"; NOZZLE_WB_RAD-2"=1' - 4"; RO=1' - 10 15/16"; RO/2=0' - 11 15/32"; RO2/2=0' - 11 15/32"; TRANSITION_TOP=3' - 7 5/16"; TRIPLE_F+1"=8' - 11"; TRIP_F=8' - 10"; TRIP_G=8' - 9 1/2"; TYPE=0' - 0"; Type Comments=Vari-Plume Laboratory Exhaust Mixed-Flow Inline Belt Drive With 1X3 Mixing Box; UNIT_HEIGHT=2' - 6"; UNIT_HEIGHT*.75=1' - 10 1/2"; UNIT_OD=1' - 9 3/8"; UNIT_RAD+((A/2)+.25")=2' - 1 15/16"; UNIT_RAD+((A/2)+.25")+4"=2' - 5 15/16"; UNIT_RADIUS=0' - 10 11/16"; UNIT_RADIUS*.6=0' - 9 5/8"; UNIT_RADIUS+4"=1' - 2 11/16"
- 165_QMXVP-9L-1X3_Mixing_Box: (A/2)+.25"=1' - 4 1/4"; (A/2)-2"=1' - 2"; (NOZZLE_HEIGHT-(NOZZLE_HEIGHT/8*2))/2=0' - 10 1/2"; (NOZZLE_WB_OD-NOZZLE_TOP_OD)/2=0' - 2 3/8"; -A=-2' - 8"; A=2' - 8"; A+.5=2' - 8 1/2"; A/2=1' - 4"; B=7' - 5"; B/2=3' - 8 1/2"; C=3' - 8"; C/2=1' - 10"; DUAL_F=6' - 0 1/4"; DUAL_F+1"=6' - 1 1/4"; DUAL_G=5' - 11 5/16"; E=2' - 7 1/8"; GA=0' - 0 3/32"; LONG_RO=8' - 9 1/4"; MB_A=3' - 5"; MB_HT=3' - 0 15/16"; MB_HT+.25"=3' - 1 3/16"; MB_HT-2.75"=2' - 10 3/16"; MB_HT/2=1' - 6 15/32"; Model=QMXVP-1X3_Mixing Box; NOZZLE_BOTTOM_ID=1' - 0 13/16"; NOZZLE_BOTTOM_RAD=0' - 6 13/32"; NOZZLE_HEIGHT=2' - 4"; NOZZLE_HEIGHT/7*2=0' - 7"; NOZZLE_SIZE=9' - 0"; NOZZLE_TOP_OD=1' - 1 1/2"; NOZZLE_TOP_RAD=0' - 6 3/4"; NOZZLE_WB/4=0' - 4 19/32"; NOZZLE_WB_OD=1' - 11"; NOZZLE_WB_RAD=0' - 11 1/2"; NOZZLE_WB_RAD-2"=0' - 9 1/2"; RO=2' - 0 15/16"; RO/2=1' - 0 15/32"; RO2/2=1' - 0 15/32"; TRANSITION_TOP=5' - 1 1/4"; TRIPLE_F+1"=9' - 5"; TRIP_F=9' - 4"; TRIP_G=9' - 3 1/2"; TYPE=0' - 0"; Type Comments=Vari-Plume Laboratory Exhaust Mixed-Flow Inline Belt Drive With 1X3 Mixing Box; UNIT_HEIGHT=2' - 9"; UNIT_HEIGHT*.75=2' - 0 3/4"; UNIT_OD=1' - 11 1/2"; UNIT_RAD+((A/2)+.25")=2' - 4"; UNIT_RAD+((A/2)+.25")+4"=2' - 8"; UNIT_RADIUS=0' - 11 3/4"; UNIT_RADIUS*.6=0' - 10 9/16"; UNIT_RADIUS+4"=1' - 3 3/4"
- 165_QMXVP-9H-1X3_Mixing_Box: (A/2)+.25"=1' - 4 1/4"; (A/2)-2"=1' - 2"; (NOZZLE_HEIGHT-(NOZZLE_HEIGHT/8*2))/2=0' - 10 1/2"; (NOZZLE_WB_OD-NOZZLE_TOP_OD)/2=0' - 2 3/8"; -A=-2' - 8"; A=2' - 8"; A+.5=2' - 8 1/2"; A/2=1' - 4"; B=7' - 5"; B/2=3' - 8 1/2"; C=3' - 8"; C/2=1' - 10"; DUAL_F=6' - 0 1/4"; DUAL_F+1"=6' - 1 1/4"; DUAL_G=5' - 11 5/16"; E=2' - 7 1/8"; GA=0' - 0 3/32"; LONG_RO=8' - 9 1/4"; MB_A=3' - 5"; MB_HT=3' - 0 15/16"; MB_HT+.25"=3' - 1 3/16"; MB_HT-2.75"=2' - 10 3/16"; MB_HT/2=1' - 6 15/32"; Model=QMXVP-1X3_Mixing Box; NOZZLE_BOTTOM_ID=1' - 0 13/16"; NOZZLE_BOTTOM_RAD=0' - 6 13/32"; NOZZLE_HEIGHT=2' - 4"; NOZZLE_HEIGHT/7*2=0' - 7"; NOZZLE_SIZE=9' - 0"; NOZZLE_TOP_OD=1' - 1 1/2"; NOZZLE_TOP_RAD=0' - 6 3/4"; NOZZLE_WB/4=0' - 4 19/32"; NOZZLE_WB_OD=1' - 11"; NOZZLE_WB_RAD=0' - 11 1/2"; NOZZLE_WB_RAD-2"=0' - 9 1/2"; RO=2' - 0 15/16"; RO/2=1' - 0 15/32"; RO2/2=1' - 0 15/32"; TRANSITION_TOP=5' - 1 1/4"; TRIPLE_F+1"=9' - 5"; TRIP_F=9' - 4"; TRIP_G=9' - 3 1/2"; TYPE=0' - 0"; Type Comments=Vari-Plume Laboratory Exhaust Mixed-Flow Inline Belt Drive With 1X3 Mixing Box; UNIT_HEIGHT=2' - 9"; UNIT_HEIGHT*.75=2' - 0 3/4"; UNIT_OD=1' - 11 1/2"; UNIT_RAD+((A/2)+.25")=2' - 4"; UNIT_RAD+((A/2)+.25")+4"=2' - 8"; UNIT_RADIUS=0' - 11 3/4"; UNIT_RADIUS*.6=0' - 10 9/16"; UNIT_RADIUS+4"=1' - 3 3/4"
- 165_QMXVP-12L-1X3_Mixing_Box: (A/2)+.25"=1' - 4 1/4"; (A/2)-2"=1' - 2"; (NOZZLE_HEIGHT-(NOZZLE_HEIGHT/8*2))/2=1' - 0"; (NOZZLE_WB_OD-NOZZLE_TOP_OD)/2=0' - 2 1/8"; -A=-2' - 8"; A=2' - 8"; A+.5=2' - 8 1/2"; A/2=1' - 4"; B=7' - 5"; B/2=3' - 8 1/2"; C=3' - 8"; C/2=1' - 10"; DUAL_F=6' - 0 1/4"; DUAL_F+1"=6' - 1 1/4"; DUAL_G=5' - 11 5/16"; E=2' - 7 1/8"; GA=0' - 0 3/32"; LONG_RO=8' - 9 1/4"; MB_A=3' - 5"; MB_HT=3' - 0 15/16"; MB_HT+.25"=3' - 1 3/16"; MB_HT-2.75"=2' - 10 3/16"; MB_HT/2=1' - 6 15/32"; Model=QMXVP-1X3_Mixing Box; NOZZLE_BOTTOM_ID=1' - 5 1/16"; NOZZLE_BOTTOM_RAD=0' - 8 17/32"; NOZZLE_HEIGHT=2' - 8"; NOZZLE_HEIGHT/7*2=0' - 8"; NOZZLE_SIZE=12' - 0"; NOZZLE_TOP_OD=1' - 7 1/2"; NOZZLE_TOP_RAD=0' - 9 3/4"; NOZZLE_WB/4=0' - 5 19/32"; NOZZLE_WB_OD=2' - 4"; NOZZLE_WB_RAD=1' - 2"; NOZZLE_WB_RAD-2"=1' - 0"; RO=2' - 0 15/16"; RO/2=1' - 0 15/32"; RO2/2=1' - 0 15/32"; TRANSITION_TOP=4' - 5 1/4"; TRIPLE_F+1"=9' - 5"; TRIP_F=9' - 4"; TRIP_G=9' - 3 1/2"; TYPE=0' - 0"; Type Comments=Vari-Plume Laboratory Exhaust Mixed-Flow Inline Belt Drive With 1X3 Mixing Box; UNIT_HEIGHT=2' - 9"; UNIT_HEIGHT*.75=2' - 0 3/4"; UNIT_OD=1' - 11 1/2"; UNIT_RAD+((A/2)+.25")=2' - 4"; UNIT_RAD+((A/2)+.25")+4"=2' - 8"; UNIT_RADIUS=0' - 11 3/4"; UNIT_RADIUS*.6=0' - 10 9/16"; UNIT_RADIUS+4"=1' - 3 3/4"
- 165_QMXVP-12H-1X3_Mixing_Box: (A/2)+.25"=1' - 4 1/4"; (A/2)-2"=1' - 2"; (NOZZLE_HEIGHT-(NOZZLE_HEIGHT/8*2))/2=1' - 0"; (NOZZLE_WB_OD-NOZZLE_TOP_OD)/2=0' - 2 1/8"; -A=-2' - 8"; A=2' - 8"; A+.5=2' - 8 1/2"; A/2=1' - 4"; B=7' - 5"; B/2=3' - 8 1/2"; C=3' - 8"; C/2=1' - 10"; DUAL_F=6' - 0 1/4"; DUAL_F+1"=6' - 1 1/4"; DUAL_G=5' - 11 5/16"; E=2' - 7 1/8"; GA=0' - 0 3/32"; LONG_RO=8' - 9 1/4"; MB_A=3' - 5"; MB_HT=3' - 0 15/16"; MB_HT+.25"=3' - 1 3/16"; MB_HT-2.75"=2' - 10 3/16"; MB_HT/2=1' - 6 15/32"; Model=QMXVP-1X3_Mixing Box; NOZZLE_BOTTOM_ID=1' - 5 1/16"; NOZZLE_BOTTOM_RAD=0' - 8 17/32"; NOZZLE_HEIGHT=2' - 8"; NOZZLE_HEIGHT/7*2=0' - 8"; NOZZLE_SIZE=12' - 0"; NOZZLE_TOP_OD=1' - 7 1/2"; NOZZLE_TOP_RAD=0' - 9 3/4"; NOZZLE_WB/4=0' - 5 19/32"; NOZZLE_WB_OD=2' - 4"; NOZZLE_WB_RAD=1' - 2"; NOZZLE_WB_RAD-2"=1' - 0"; RO=2' - 0 15/16"; RO/2=1' - 0 15/32"; RO2/2=1' - 0 15/32"; TRANSITION_TOP=4' - 5 1/4"; TRIPLE_F+1"=9' - 5"; TRIP_F=9' - 4"; TRIP_G=9' - 3 1/2"; TYPE=0' - 0"; Type Comments=Vari-Plume Laboratory Exhaust Mixed-Flow Inline Belt Drive With 1X3 Mixing Box; UNIT_HEIGHT=2' - 9"; UNIT_HEIGHT*.75=2' - 0 3/4"; UNIT_OD=1' - 11 1/2"; UNIT_RAD+((A/2)+.25")=2' - 4"; UNIT_RAD+((A/2)+.25")+4"=2' - 8"; UNIT_RADIUS=0' - 11 3/4"; UNIT_RADIUS*.6=0' - 10 9/16"; UNIT_RADIUS+4"=1' - 3 3/4"
- 165_QMXVP-15L-1X3_Mixing_Box: (A/2)+.25"=1' - 4 1/4"; (A/2)-2"=1' - 2"; (NOZZLE_HEIGHT-(NOZZLE_HEIGHT/8*2))/2=1' - 4 1/8"; (NOZZLE_WB_OD-NOZZLE_TOP_OD)/2=0' - 3 1/4"; -A=-2' - 8"; A=2' - 8"; A+.5=2' - 8 1/2"; A/2=1' - 4"; B=7' - 5"; B/2=3' - 8 1/2"; C=3' - 8"; C/2=1' - 10"; DUAL_F=6' - 0 1/4"; DUAL_F+1"=6' - 1 1/4"; DUAL_G=5' - 11 5/16"; E=2' - 7 1/8"; GA=0' - 0 3/32"; LONG_RO=8' - 9 1/4"; MB_A=3' - 5"; MB_HT=3' - 0 15/16"; MB_HT+.25"=3' - 1 3/16"; MB_HT-2.75"=2' - 10 3/16"; MB_HT/2=1' - 6 15/32"; Model=QMXVP-1X3_Mixing Box; NOZZLE_BOTTOM_ID=1' - 9 3/8"; NOZZLE_BOTTOM_RAD=0' - 10 11/16"; NOZZLE_HEIGHT=3' - 7"; NOZZLE_HEIGHT/7*2=0' - 10 3/4"; NOZZLE_SIZE=15' - 0"; NOZZLE_TOP_OD=1' - 11"; NOZZLE_TOP_RAD=0' - 11 1/2"; NOZZLE_WB/4=0' - 7 3/16"; NOZZLE_WB_OD=3' - 0"; NOZZLE_WB_RAD=1' - 6"; NOZZLE_WB_RAD-2"=1' - 4"; RO=2' - 0 15/16"; RO/2=1' - 0 15/32"; RO2/2=1' - 0 15/32"; TRANSITION_TOP=3' - 9 5/16"; TRIPLE_F+1"=9' - 5"; TRIP_F=9' - 4"; TRIP_G=9' - 3 1/2"; TYPE=0' - 0"; Type Comments=Vari-Plume Laboratory Exhaust Mixed-Flow Inline Belt Drive With 1X3 Mixing Box; UNIT_HEIGHT=2' - 9"; UNIT_HEIGHT*.75=2' - 0 3/4"; UNIT_OD=1' - 11 1/2"; UNIT_RAD+((A/2)+.25")=2' - 4"; UNIT_RAD+((A/2)+.25")+4"=2' - 8"; UNIT_RADIUS=0' - 11 3/4"; UNIT_RADIUS*.6=0' - 10 9/16"; UNIT_RADIUS+4"=1' - 3 3/4"
- 165_QMXVP-15H-1X3_Mixing_Box: (A/2)+.25"=1' - 4 1/4"; (A/2)-2"=1' - 2"; (NOZZLE_HEIGHT-(NOZZLE_HEIGHT/8*2))/2=1' - 4 1/8"; (NOZZLE_WB_OD-NOZZLE_TOP_OD)/2=0' - 3 1/4"; -A=-2' - 8"; A=2' - 8"; A+.5=2' - 8 1/2"; A/2=1' - 4"; B=7' - 5"; B/2=3' - 8 1/2"; C=3' - 8"; C/2=1' - 10"; DUAL_F=6' - 0 1/4"; DUAL_F+1"=6' - 1 1/4"; DUAL_G=5' - 11 5/16"; E=2' - 7 1/8"; GA=0' - 0 3/32"; LONG_RO=8' - 9 1/4"; MB_A=3' - 5"; MB_HT=3' - 0 15/16"; MB_HT+.25"=3' - 1 3/16"; MB_HT-2.75"=2' - 10 3/16"; MB_HT/2=1' - 6 15/32"; Model=QMXVP-1X3_Mixing Box; NOZZLE_BOTTOM_ID=1' - 9 3/8"; NOZZLE_BOTTOM_RAD=0' - 10 11/16"; NOZZLE_HEIGHT=3' - 7"; NOZZLE_HEIGHT/7*2=0' - 10 3/4"; NOZZLE_SIZE=15' - 0"; NOZZLE_TOP_OD=1' - 11"; NOZZLE_TOP_RAD=0' - 11 1/2"; NOZZLE_WB/4=0' - 7 3/16"; NOZZLE_WB_OD=3' - 0"; NOZZLE_WB_RAD=1' - 6"; NOZZLE_WB_RAD-2"=1' - 4"; RO=2' - 0 15/16"; RO/2=1' - 0 15/32"; RO2/2=1' - 0 15/32"; TRANSITION_TOP=3' - 9 5/16"; TRIPLE_F+1"=9' - 5"; TRIP_F=9' - 4"; TRIP_G=9' - 3 1/2"; TYPE=0' - 0"; Type Comments=Vari-Plume Laboratory Exhaust Mixed-Flow Inline Belt Drive With 1X3 Mixing Box; UNIT_HEIGHT=2' - 9"; UNIT_HEIGHT*.75=2' - 0 3/4"; UNIT_OD=1' - 11 1/2"; UNIT_RAD+((A/2)+.25")=2' - 4"; UNIT_RAD+((A/2)+.25")+4"=2' - 8"; UNIT_RADIUS=0' - 11 3/4"; UNIT_RADIUS*.6=0' - 10 9/16"; UNIT_RADIUS+4"=1' - 3 3/4"
- 180_QMXVP-12L-1X3_Mixing_Box: (A/2)+.25"=1' - 5 1/4"; (A/2)-2"=1' - 3"; (NOZZLE_HEIGHT-(NOZZLE_HEIGHT/8*2))/2=1' - 0"; (NOZZLE_WB_OD-NOZZLE_TOP_OD)/2=0' - 2 1/8"; -A=-2' - 10"; A=2' - 10"; A+.5=2' - 10 1/2"; A/2=1' - 5"; B=8' - 2"; B/2=4' - 1"; C=3' - 10"; C/2=1' - 11"; DUAL_F=7' - 0 1/4"; DUAL_F+1"=7' - 1 1/4"; DUAL_G=6' - 11 5/16"; E=2' - 9 1/8"; GA=0' - 0 3/32"; LONG_RO=10' - 7 1/4"; MB_A=3' - 8"; MB_HT=3' - 1 11/16"; MB_HT+.25"=3' - 1 15/16"; MB_HT-2.75"=2' - 10 15/16"; MB_HT/2=1' - 6 27/32"; Model=QMXVP-1X3_Mixing Box; NOZZLE_BOTTOM_ID=1' - 5 1/16"; NOZZLE_BOTTOM_RAD=0' - 8 17/32"; NOZZLE_HEIGHT=2' - 8"; NOZZLE_HEIGHT/7*2=0' - 8"; NOZZLE_SIZE=12' - 0"; NOZZLE_TOP_OD=1' - 7 1/2"; NOZZLE_TOP_RAD=0' - 9 3/4"; NOZZLE_WB/4=0' - 5 19/32"; NOZZLE_WB_OD=2' - 4"; NOZZLE_WB_RAD=1' - 2"; NOZZLE_WB_RAD-2"=1' - 0"; RO=2' - 2 15/16"; RO/2=1' - 1 15/32"; RO2/2=1' - 1 15/32"; TRANSITION_TOP=4' - 11 1/16"; TRIPLE_F+1"=11' - 3"; TRIP_F=11' - 2"; TRIP_G=11' - 1 1/2"; TYPE=0' - 0"; Type Comments=Vari-Plume Laboratory Exhaust Mixed-Flow Inline Belt Drive With 1X3 Mixing Box; UNIT_HEIGHT=2' - 11"; UNIT_HEIGHT*.75=2' - 2 1/4"; UNIT_OD=2' - 1 5/8"; UNIT_RAD+((A/2)+.25")=2' - 6 1/16"; UNIT_RAD+((A/2)+.25")+4"=2' - 10 1/16"; UNIT_RADIUS=1' - 0 13/16"; UNIT_RADIUS*.6=0' - 11 17/32"; UNIT_RADIUS+4"=1' - 4 13/16"
- 180_QMXVP-12H-1X3_Mixing_Box: (A/2)+.25"=1' - 5 1/4"; (A/2)-2"=1' - 3"; (NOZZLE_HEIGHT-(NOZZLE_HEIGHT/8*2))/2=1' - 0"; (NOZZLE_WB_OD-NOZZLE_TOP_OD)/2=0' - 2 1/8"; -A=-2' - 10"; A=2' - 10"; A+.5=2' - 10 1/2"; A/2=1' - 5"; B=8' - 2"; B/2=4' - 1"; C=3' - 10"; C/2=1' - 11"; DUAL_F=7' - 0 1/4"; DUAL_F+1"=7' - 1 1/4"; DUAL_G=6' - 11 5/16"; E=2' - 9 1/8"; GA=0' - 0 3/32"; LONG_RO=10' - 7 1/4"; MB_A=3' - 8"; MB_HT=3' - 1 11/16"; MB_HT+.25"=3' - 1 15/16"; MB_HT-2.75"=2' - 10 15/16"; MB_HT/2=1' - 6 27/32"; Model=QMXVP-1X3_Mixing Box; NOZZLE_BOTTOM_ID=1' - 5 1/16"; NOZZLE_BOTTOM_RAD=0' - 8 17/32"; NOZZLE_HEIGHT=2' - 8"; NOZZLE_HEIGHT/7*2=0' - 8"; NOZZLE_SIZE=12' - 0"; NOZZLE_TOP_OD=1' - 7 1/2"; NOZZLE_TOP_RAD=0' - 9 3/4"; NOZZLE_WB/4=0' - 5 19/32"; NOZZLE_WB_OD=2' - 4"; NOZZLE_WB_RAD=1' - 2"; NOZZLE_WB_RAD-2"=1' - 0"; RO=2' - 2 15/16"; RO/2=1' - 1 15/32"; RO2/2=1' - 1 15/32"; TRANSITION_TOP=4' - 11 1/16"; TRIPLE_F+1"=11' - 3"; TRIP_F=11' - 2"; TRIP_G=11' - 1 1/2"; TYPE=0' - 0"; Type Comments=Vari-Plume Laboratory Exhaust Mixed-Flow Inline Belt Drive With 1X3 Mixing Box; UNIT_HEIGHT=2' - 11"; UNIT_HEIGHT*.75=2' - 2 1/4"; UNIT_OD=2' - 1 5/8"; UNIT_RAD+((A/2)+.25")=2' - 6 1/16"; UNIT_RAD+((A/2)+.25")+4"=2' - 10 1/16"; UNIT_RADIUS=1' - 0 13/16"; UNIT_RADIUS*.6=0' - 11 17/32"; UNIT_RADIUS+4"=1' - 4 13/16"
- 180_QMXVP-15L-1X3_Mixing_Box: (A/2)+.25"=1' - 5 1/4"; (A/2)-2"=1' - 3"; (NOZZLE_HEIGHT-(NOZZLE_HEIGHT/8*2))/2=1' - 4 1/8"; (NOZZLE_WB_OD-NOZZLE_TOP_OD)/2=0' - 3 1/4"; -A=-2' - 10"; A=2' - 10"; A+.5=2' - 10 1/2"; A/2=1' - 5"; B=8' - 2"; B/2=4' - 1"; C=3' - 10"; C/2=1' - 11"; DUAL_F=7' - 0 1/4"; DUAL_F+1"=7' - 1 1/4"; DUAL_G=6' - 11 5/16"; E=2' - 9 1/8"; GA=0' - 0 3/32"; LONG_RO=10' - 7 1/4"; MB_A=3' - 8"; MB_HT=3' - 1 11/16"; MB_HT+.25"=3' - 1 15/16"; MB_HT-2.75"=2' - 10 15/16"; MB_HT/2=1' - 6 27/32"; Model=QMXVP-1X3_Mixing Box; NOZZLE_BOTTOM_ID=1' - 9 3/8"; NOZZLE_BOTTOM_RAD=0' - 10 11/16"; NOZZLE_HEIGHT=3' - 7"; NOZZLE_HEIGHT/7*2=0' - 10 3/4"; NOZZLE_SIZE=15' - 0"; NOZZLE_TOP_OD=1' - 11"; NOZZLE_TOP_RAD=0' - 11 1/2"; NOZZLE_WB/4=0' - 7 3/16"; NOZZLE_WB_OD=3' - 0"; NOZZLE_WB_RAD=1' - 6"; NOZZLE_WB_RAD-2"=1' - 4"; RO=2' - 2 15/16"; RO/2=1' - 1 15/32"; RO2/2=1' - 1 15/32"; TRANSITION_TOP=4' - 3 1/8"; TRIPLE_F+1"=11' - 3"; TRIP_F=11' - 2"; TRIP_G=11' - 1 1/2"; TYPE=0' - 0"; Type Comments=Vari-Plume Laboratory Exhaust Mixed-Flow Inline Belt Drive With 1X3 Mixing Box; UNIT_HEIGHT=2' - 11"; UNIT_HEIGHT*.75=2' - 2 1/4"; UNIT_OD=2' - 1 5/8"; UNIT_RAD+((A/2)+.25")=2' - 6 1/16"; UNIT_RAD+((A/2)+.25")+4"=2' - 10 1/16"; UNIT_RADIUS=1' - 0 13/16"; UNIT_RADIUS*.6=0' - 11 17/32"; UNIT_RADIUS+4"=1' - 4 13/16"
- 180_QMXVP-15H-1X3_Mixing_Box: (A/2)+.25"=1' - 5 1/4"; (A/2)-2"=1' - 3"; (NOZZLE_HEIGHT-(NOZZLE_HEIGHT/8*2))/2=1' - 4 1/8"; (NOZZLE_WB_OD-NOZZLE_TOP_OD)/2=0' - 3 1/4"; -A=-2' - 10"; A=2' - 10"; A+.5=2' - 10 1/2"; A/2=1' - 5"; B=8' - 2"; B/2=4' - 1"; C=3' - 10"; C/2=1' - 11"; DUAL_F=7' - 0 1/4"; DUAL_F+1"=7' - 1 1/4"; DUAL_G=6' - 11 5/16"; E=2' - 9 1/8"; GA=0' - 0 3/32"; LONG_RO=10' - 7 1/4"; MB_A=3' - 8"; MB_HT=3' - 1 11/16"; MB_HT+.25"=3' - 1 15/16"; MB_HT-2.75"=2' - 10 15/16"; MB_HT/2=1' - 6 27/32"; Model=QMXVP-1X3_Mixing Box; NOZZLE_BOTTOM_ID=1' - 9 3/8"; NOZZLE_BOTTOM_RAD=0' - 10 11/16"; NOZZLE_HEIGHT=3' - 7"; NOZZLE_HEIGHT/7*2=0' - 10 3/4"; NOZZLE_SIZE=15' - 0"; NOZZLE_TOP_OD=1' - 11"; NOZZLE_TOP_RAD=0' - 11 1/2"; NOZZLE_WB/4=0' - 7 3/16"; NOZZLE_WB_OD=3' - 0"; NOZZLE_WB_RAD=1' - 6"; NOZZLE_WB_RAD-2"=1' - 4"; RO=2' - 2 15/16"; RO/2=1' - 1 15/32"; RO2/2=1' - 1 15/32"; TRANSITION_TOP=4' - 3 1/8"; TRIPLE_F+1"=11' - 3"; TRIP_F=11' - 2"; TRIP_G=11' - 1 1/2"; TYPE=0' - 0"; Type Comments=Vari-Plume Laboratory Exhaust Mixed-Flow Inline Belt Drive With 1X3 Mixing Box; UNIT_HEIGHT=2' - 11"; UNIT_HEIGHT*.75=2' - 2 1/4"; UNIT_OD=2' - 1 5/8"; UNIT_RAD+((A/2)+.25")=2' - 6 1/16"; UNIT_RAD+((A/2)+.25")+4"=2' - 10 1/16"; UNIT_RADIUS=1' - 0 13/16"; UNIT_RADIUS*.6=0' - 11 17/32"; UNIT_RADIUS+4"=1' - 4 13/16"
- 180_QMXVP-18L-1X3_Mixing_Box: (A/2)+.25"=1' - 5 1/4"; (A/2)-2"=1' - 3"; (NOZZLE_HEIGHT-(NOZZLE_HEIGHT/8*2))/2=1' - 6"; (NOZZLE_WB_OD-NOZZLE_TOP_OD)/2=0' - 3 7/8"; -A=-2' - 10"; A=2' - 10"; A+.5=2' - 10 1/2"; A/2=1' - 5"; B=8' - 2"; B/2=4' - 1"; C=3' - 10"; C/2=1' - 11"; DUAL_F=7' - 0 1/4"; DUAL_F+1"=7' - 1 1/4"; DUAL_G=6' - 11 5/16"; E=2' - 9 1/8"; GA=0' - 0 3/32"; LONG_RO=10' - 7 1/4"; MB_A=3' - 8"; MB_HT=3' - 1 11/16"; MB_HT+.25"=3' - 1 15/16"; MB_HT-2.75"=2' - 10 15/16"; MB_HT/2=1' - 6 27/32"; Model=QMXVP-1X3_Mixing Box; NOZZLE_BOTTOM_ID=2' - 1 5/8"; NOZZLE_BOTTOM_RAD=1' - 0 13/16"; NOZZLE_HEIGHT=4' - 0"; NOZZLE_HEIGHT/7*2=1' - 0"; NOZZLE_SIZE=18' - 0"; NOZZLE_TOP_OD=2' - 3 1/2"; NOZZLE_TOP_RAD=1' - 1 3/4"; NOZZLE_WB/4=0' - 8 19/32"; NOZZLE_WB_OD=3' - 7"; NOZZLE_WB_RAD=1' - 9 1/2"; NOZZLE_WB_RAD-2"=1' - 7 1/2"; RO=2' - 2 15/16"; RO/2=1' - 1 15/32"; RO2/2=1' - 1 15/32"; TRANSITION_TOP=4' - 0 1/2"; TRIPLE_F+1"=11' - 3"; TRIP_F=11' - 2"; TRIP_G=11' - 1 1/2"; TYPE=0' - 0"; Type Comments=Vari-Plume Laboratory Exhaust Mixed-Flow Inline Belt Drive With 1X3 Mixing Box; UNIT_HEIGHT=2' - 11"; UNIT_HEIGHT*.75=2' - 2 1/4"; UNIT_OD=2' - 1 5/8"; UNIT_RAD+((A/2)+.25")=2' - 6 1/16"; UNIT_RAD+((A/2)+.25")+4"=2' - 10 1/16"; UNIT_RADIUS=1' - 0 13/16"; UNIT_RADIUS*.6=0' - 11 17/32"; UNIT_RADIUS+4"=1' - 4 13/16"
- 180_QMXVP-18H-1X3_Mixing_Box: (A/2)+.25"=1' - 5 1/4"; (A/2)-2"=1' - 3"; (NOZZLE_HEIGHT-(NOZZLE_HEIGHT/8*2))/2=1' - 6"; (NOZZLE_WB_OD-NOZZLE_TOP_OD)/2=0' - 3 7/8"; -A=-2' - 10"; A=2' - 10"; A+.5=2' - 10 1/2"; A/2=1' - 5"; B=8' - 2"; B/2=4' - 1"; C=3' - 10"; C/2=1' - 11"; DUAL_F=7' - 0 1/4"; DUAL_F+1"=7' - 1 1/4"; DUAL_G=6' - 11 5/16"; E=2' - 9 1/8"; GA=0' - 0 3/32"; LONG_RO=10' - 7 1/4"; MB_A=3' - 8"; MB_HT=3' - 1 11/16"; MB_HT+.25"=3' - 1 15/16"; MB_HT-2.75"=2' - 10 15/16"; MB_HT/2=1' - 6 27/32"; Model=QMXVP-1X3_Mixing Box; NOZZLE_BOTTOM_ID=2' - 1 5/8"; NOZZLE_BOTTOM_RAD=1' - 0 13/16"; NOZZLE_HEIGHT=4' - 0"; NOZZLE_HEIGHT/7*2=1' - 0"; NOZZLE_SIZE=18' - 0"; NOZZLE_TOP_OD=2' - 3 1/2"; NOZZLE_TOP_RAD=1' - 1 3/4"; NOZZLE_WB/4=0' - 8 19/32"; NOZZLE_WB_OD=3' - 7"; NOZZLE_WB_RAD=1' - 9 1/2"; NOZZLE_WB_RAD-2"=1' - 7 1/2"; RO=2' - 2 15/16"; RO/2=1' - 1 15/32"; RO2/2=1' - 1 15/32"; TRANSITION_TOP=4' - 0 1/2"; TRIPLE_F+1"=11' - 3"; TRIP_F=11' - 2"; TRIP_G=11' - 1 1/2"; TYPE=0' - 0"; Type Comments=Vari-Plume Laboratory Exhaust Mixed-Flow Inline Belt Drive With 1X3 Mixing Box; UNIT_HEIGHT=2' - 11"; UNIT_HEIGHT*.75=2' - 2 1/4"; UNIT_OD=2' - 1 5/8"; UNIT_RAD+((A/2)+.25")=2' - 6 1/16"; UNIT_RAD+((A/2)+.25")+4"=2' - 10 1/16"; UNIT_RADIUS=1' - 0 13/16"; UNIT_RADIUS*.6=0' - 11 17/32"; UNIT_RADIUS+4"=1' - 4 13/16"
- 202_QMXVP-12L-1X3_Mixing_Box: (A/2)+.25"=1' - 7 1/4"; (A/2)-2"=1' - 5"; (NOZZLE_HEIGHT-(NOZZLE_HEIGHT/8*2))/2=1' - 0"; (NOZZLE_WB_OD-NOZZLE_TOP_OD)/2=0' - 2 1/8"; -A=-3' - 2"; A=3' - 2"; A+.5=3' - 2 1/2"; A/2=1' - 7"; B=8' - 8"; B/2=4' - 4"; C=4' - 2"; C/2=2' - 1"; DUAL_F=7' - 6 1/4"; DUAL_F+1"=7' - 7 1/4"; DUAL_G=7' - 5 1/8"; E=3' - 0 15/16"; GA=0' - 0 3/32"; LONG_RO=11' - 3"; MB_A=4' - 1"; MB_HT=3' - 5 3/16"; MB_HT+.25"=3' - 5 7/16"; MB_HT-2.75"=3' - 2 7/16"; MB_HT/2=1' - 8 19/32"; Model=QMXVP-1X3_Mixing Box; NOZZLE_BOTTOM_ID=1' - 5 1/16"; NOZZLE_BOTTOM_RAD=0' - 8 17/32"; NOZZLE_HEIGHT=2' - 8"; NOZZLE_HEIGHT/7*2=0' - 8"; NOZZLE_SIZE=12' - 0"; NOZZLE_TOP_OD=1' - 7 1/2"; NOZZLE_TOP_RAD=0' - 9 3/4"; NOZZLE_WB/4=0' - 5 19/32"; NOZZLE_WB_OD=2' - 4"; NOZZLE_WB_RAD=1' - 2"; NOZZLE_WB_RAD-2"=1' - 0"; RO=2' - 6 3/4"; RO/2=1' - 3 3/8"; RO2/2=1' - 3 3/8"; TRANSITION_TOP=5' - 7 9/16"; TRIPLE_F+1"=11' - 11"; TRIP_F=11' - 10"; TRIP_G=11' - 9 1/4"; TYPE=0' - 0"; Type Comments=Vari-Plume Laboratory Exhaust Mixed-Flow Inline Belt Drive With 1X3 Mixing Box; UNIT_HEIGHT=3' - 1 1/2"; UNIT_HEIGHT*.75=2' - 4 1/8"; UNIT_OD=2' - 4 3/4"; UNIT_RAD+((A/2)+.25")=2' - 9 5/8"; UNIT_RAD+((A/2)+.25")+4"=3' - 1 5/8"; UNIT_RADIUS=1' - 2 3/8"; UNIT_RADIUS*.6=1' - 0 15/16"; UNIT_RADIUS+4"=1' - 6 3/8"
- 202_QMXVP-12H-1X3_Mixing_Box: (A/2)+.25"=1' - 7 1/4"; (A/2)-2"=1' - 5"; (NOZZLE_HEIGHT-(NOZZLE_HEIGHT/8*2))/2=1' - 0"; (NOZZLE_WB_OD-NOZZLE_TOP_OD)/2=0' - 2 1/8"; -A=-3' - 2"; A=3' - 2"; A+.5=3' - 2 1/2"; A/2=1' - 7"; B=8' - 8"; B/2=4' - 4"; C=4' - 2"; C/2=2' - 1"; DUAL_F=7' - 6 1/4"; DUAL_F+1"=7' - 7 1/4"; DUAL_G=7' - 5 1/8"; E=3' - 0 15/16"; GA=0' - 0 3/32"; LONG_RO=11' - 3"; MB_A=4' - 1"; MB_HT=3' - 5 3/16"; MB_HT+.25"=3' - 5 7/16"; MB_HT-2.75"=3' - 2 7/16"; MB_HT/2=1' - 8 19/32"; Model=QMXVP-1X3_Mixing Box; NOZZLE_BOTTOM_ID=1' - 5 1/16"; NOZZLE_BOTTOM_RAD=0' - 8 17/32"; NOZZLE_HEIGHT=2' - 8"; NOZZLE_HEIGHT/7*2=0' - 8"; NOZZLE_SIZE=12' - 0"; NOZZLE_TOP_OD=1' - 7 1/2"; NOZZLE_TOP_RAD=0' - 9 3/4"; NOZZLE_WB/4=0' - 5 19/32"; NOZZLE_WB_OD=2' - 4"; NOZZLE_WB_RAD=1' - 2"; NOZZLE_WB_RAD-2"=1' - 0"; RO=2' - 6 3/4"; RO/2=1' - 3 3/8"; RO2/2=1' - 3 3/8"; TRANSITION_TOP=5' - 7 9/16"; TRIPLE_F+1"=11' - 11"; TRIP_F=11' - 10"; TRIP_G=11' - 9 1/4"; TYPE=0' - 0"; Type Comments=Vari-Plume Laboratory Exhaust Mixed-Flow Inline Belt Drive With 1X3 Mixing Box; UNIT_HEIGHT=3' - 1 1/2"; UNIT_HEIGHT*.75=2' - 4 1/8"; UNIT_OD=2' - 4 3/4"; UNIT_RAD+((A/2)+.25")=2' - 9 5/8"; UNIT_RAD+((A/2)+.25")+4"=3' - 1 5/8"; UNIT_RADIUS=1' - 2 3/8"; UNIT_RADIUS*.6=1' - 0 15/16"; UNIT_RADIUS+4"=1' - 6 3/8"
- 202_QMXVP-15L-1X3_Mixing_Box: (A/2)+.25"=1' - 7 1/4"; (A/2)-2"=1' - 5"; (NOZZLE_HEIGHT-(NOZZLE_HEIGHT/8*2))/2=1' - 4 1/8"; (NOZZLE_WB_OD-NOZZLE_TOP_OD)/2=0' - 3 1/4"; -A=-3' - 2"; A=3' - 2"; A+.5=3' - 2 1/2"; A/2=1' - 7"; B=8' - 8"; B/2=4' - 4"; C=4' - 2"; C/2=2' - 1"; DUAL_F=7' - 6 1/4"; DUAL_F+1"=7' - 7 1/4"; DUAL_G=7' - 5 1/8"; E=3' - 0 15/16"; GA=0' - 0 3/32"; LONG_RO=11' - 3"; MB_A=4' - 1"; MB_HT=3' - 5 3/16"; MB_HT+.25"=3' - 5 7/16"; MB_HT-2.75"=3' - 2 7/16"; MB_HT/2=1' - 8 19/32"; Model=QMXVP-1X3_Mixing Box; NOZZLE_BOTTOM_ID=1' - 9 3/8"; NOZZLE_BOTTOM_RAD=0' - 10 11/16"; NOZZLE_HEIGHT=3' - 7"; NOZZLE_HEIGHT/7*2=0' - 10 3/4"; NOZZLE_SIZE=15' - 0"; NOZZLE_TOP_OD=1' - 11"; NOZZLE_TOP_RAD=0' - 11 1/2"; NOZZLE_WB/4=0' - 7 3/16"; NOZZLE_WB_OD=3' - 0"; NOZZLE_WB_RAD=1' - 6"; NOZZLE_WB_RAD-2"=1' - 4"; RO=2' - 6 3/4"; RO/2=1' - 3 3/8"; RO2/2=1' - 3 3/8"; TRANSITION_TOP=4' - 11 5/8"; TRIPLE_F+1"=11' - 11"; TRIP_F=11' - 10"; TRIP_G=11' - 9 1/4"; TYPE=0' - 0"; Type Comments=Vari-Plume Laboratory Exhaust Mixed-Flow Inline Belt Drive With 1X3 Mixing Box; UNIT_HEIGHT=3' - 1 1/2"; UNIT_HEIGHT*.75=2' - 4 1/8"; UNIT_OD=2' - 4 3/4"; UNIT_RAD+((A/2)+.25")=2' - 9 5/8"; UNIT_RAD+((A/2)+.25")+4"=3' - 1 5/8"; UNIT_RADIUS=1' - 2 3/8"; UNIT_RADIUS*.6=1' - 0 15/16"; UNIT_RADIUS+4"=1' - 6 3/8"
- 202_QMXVP-15H-1X3_Mixing_Box: (A/2)+.25"=1' - 7 1/4"; (A/2)-2"=1' - 5"; (NOZZLE_HEIGHT-(NOZZLE_HEIGHT/8*2))/2=1' - 4 1/8"; (NOZZLE_WB_OD-NOZZLE_TOP_OD)/2=0' - 3 1/4"; -A=-3' - 2"; A=3' - 2"; A+.5=3' - 2 1/2"; A/2=1' - 7"; B=8' - 8"; B/2=4' - 4"; C=4' - 2"; C/2=2' - 1"; DUAL_F=7' - 6 1/4"; DUAL_F+1"=7' - 7 1/4"; DUAL_G=7' - 5 1/8"; E=3' - 0 15/16"; GA=0' - 0 3/32"; LONG_RO=11' - 3"; MB_A=4' - 1"; MB_HT=3' - 5 3/16"; MB_HT+.25"=3' - 5 7/16"; MB_HT-2.75"=3' - 2 7/16"; MB_HT/2=1' - 8 19/32"; Model=QMXVP-1X3_Mixing Box; NOZZLE_BOTTOM_ID=1' - 9 3/8"; NOZZLE_BOTTOM_RAD=0' - 10 11/16"; NOZZLE_HEIGHT=3' - 7"; NOZZLE_HEIGHT/7*2=0' - 10 3/4"; NOZZLE_SIZE=15' - 0"; NOZZLE_TOP_OD=1' - 11"; NOZZLE_TOP_RAD=0' - 11 1/2"; NOZZLE_WB/4=0' - 7 3/16"; NOZZLE_WB_OD=3' - 0"; NOZZLE_WB_RAD=1' - 6"; NOZZLE_WB_RAD-2"=1' - 4"; RO=2' - 6 3/4"; RO/2=1' - 3 3/8"; RO2/2=1' - 3 3/8"; TRANSITION_TOP=4' - 11 5/8"; TRIPLE_F+1"=11' - 11"; TRIP_F=11' - 10"; TRIP_G=11' - 9 1/4"; TYPE=0' - 0"; Type Comments=Vari-Plume Laboratory Exhaust Mixed-Flow Inline Belt Drive With 1X3 Mixing Box; UNIT_HEIGHT=3' - 1 1/2"; UNIT_HEIGHT*.75=2' - 4 1/8"; UNIT_OD=2' - 4 3/4"; UNIT_RAD+((A/2)+.25")=2' - 9 5/8"; UNIT_RAD+((A/2)+.25")+4"=3' - 1 5/8"; UNIT_RADIUS=1' - 2 3/8"; UNIT_RADIUS*.6=1' - 0 15/16"; UNIT_RADIUS+4"=1' - 6 3/8"
- 202_QMXVP-18L-1X3_Mixing_Box: (A/2)+.25"=1' - 7 1/4"; (A/2)-2"=1' - 5"; (NOZZLE_HEIGHT-(NOZZLE_HEIGHT/8*2))/2=1' - 6"; (NOZZLE_WB_OD-NOZZLE_TOP_OD)/2=0' - 3 7/8"; -A=-3' - 2"; A=3' - 2"; A+.5=3' - 2 1/2"; A/2=1' - 7"; B=8' - 8"; B/2=4' - 4"; C=4' - 2"; C/2=2' - 1"; DUAL_F=7' - 6 1/4"; DUAL_F+1"=7' - 7 1/4"; DUAL_G=7' - 5 1/8"; E=3' - 0 15/16"; GA=0' - 0 3/32"; LONG_RO=11' - 3"; MB_A=4' - 1"; MB_HT=3' - 5 3/16"; MB_HT+.25"=3' - 5 7/16"; MB_HT-2.75"=3' - 2 7/16"; MB_HT/2=1' - 8 19/32"; Model=QMXVP-1X3_Mixing Box; NOZZLE_BOTTOM_ID=2' - 1 5/8"; NOZZLE_BOTTOM_RAD=1' - 0 13/16"; NOZZLE_HEIGHT=4' - 0"; NOZZLE_HEIGHT/7*2=1' - 0"; NOZZLE_SIZE=18' - 0"; NOZZLE_TOP_OD=2' - 3 1/2"; NOZZLE_TOP_RAD=1' - 1 3/4"; NOZZLE_WB/4=0' - 8 19/32"; NOZZLE_WB_OD=3' - 7"; NOZZLE_WB_RAD=1' - 9 1/2"; NOZZLE_WB_RAD-2"=1' - 7 1/2"; RO=2' - 6 3/4"; RO/2=1' - 3 3/8"; RO2/2=1' - 3 3/8"; TRANSITION_TOP=4' - 3 5/8"; TRIPLE_F+1"=11' - 11"; TRIP_F=11' - 10"; TRIP_G=11' - 9 1/4"; TYPE=0' - 0"; Type Comments=Vari-Plume Laboratory Exhaust Mixed-Flow Inline Belt Drive With 1X3 Mixing Box; UNIT_HEIGHT=3' - 1 1/2"; UNIT_HEIGHT*.75=2' - 4 1/8"; UNIT_OD=2' - 4 3/4"; UNIT_RAD+((A/2)+.25")=2' - 9 5/8"; UNIT_RAD+((A/2)+.25")+4"=3' - 1 5/8"; UNIT_RADIUS=1' - 2 3/8"; UNIT_RADIUS*.6=1' - 0 15/16"; UNIT_RADIUS+4"=1' - 6 3/8"
- 202_QMXVP-18H-1X3_Mixing_Box: (A/2)+.25"=1' - 7 1/4"; (A/2)-2"=1' - 5"; (NOZZLE_HEIGHT-(NOZZLE_HEIGHT/8*2))/2=1' - 6"; (NOZZLE_WB_OD-NOZZLE_TOP_OD)/2=0' - 3 7/8"; -A=-3' - 2"; A=3' - 2"; A+.5=3' - 2 1/2"; A/2=1' - 7"; B=8' - 8"; B/2=4' - 4"; C=4' - 2"; C/2=2' - 1"; DUAL_F=7' - 6 1/4"; DUAL_F+1"=7' - 7 1/4"; DUAL_G=7' - 5 1/8"; E=3' - 0 15/16"; GA=0' - 0 3/32"; LONG_RO=11' - 3"; MB_A=4' - 1"; MB_HT=3' - 5 3/16"; MB_HT+.25"=3' - 5 7/16"; MB_HT-2.75"=3' - 2 7/16"; MB_HT/2=1' - 8 19/32"; Model=QMXVP-1X3_Mixing Box; NOZZLE_BOTTOM_ID=2' - 1 5/8"; NOZZLE_BOTTOM_RAD=1' - 0 13/16"; NOZZLE_HEIGHT=4' - 0"; NOZZLE_HEIGHT/7*2=1' - 0"; NOZZLE_SIZE=18' - 0"; NOZZLE_TOP_OD=2' - 3 1/2"; NOZZLE_TOP_RAD=1' - 1 3/4"; NOZZLE_WB/4=0' - 8 19/32"; NOZZLE_WB_OD=3' - 7"; NOZZLE_WB_RAD=1' - 9 1/2"; NOZZLE_WB_RAD-2"=1' - 7 1/2"; RO=2' - 6 3/4"; RO/2=1' - 3 3/8"; RO2/2=1' - 3 3/8"; TRANSITION_TOP=4' - 3 5/8"; TRIPLE_F+1"=11' - 11"; TRIP_F=11' - 10"; TRIP_G=11' - 9 1/4"; TYPE=0' - 0"; Type Comments=Vari-Plume Laboratory Exhaust Mixed-Flow Inline Belt Drive With 1X3 Mixing Box; UNIT_HEIGHT=3' - 1 1/2"; UNIT_HEIGHT*.75=2' - 4 1/8"; UNIT_OD=2' - 4 3/4"; UNIT_RAD+((A/2)+.25")=2' - 9 5/8"; UNIT_RAD+((A/2)+.25")+4"=3' - 1 5/8"; UNIT_RADIUS=1' - 2 3/8"; UNIT_RADIUS*.6=1' - 0 15/16"; UNIT_RADIUS+4"=1' - 6 3/8"
- 225_QMXVP-12L-1X3_Mixing_Box: (A/2)+.25"=1' - 9 1/4"; (A/2)-2"=1' - 7"; (NOZZLE_HEIGHT-(NOZZLE_HEIGHT/8*2))/2=1' - 0"; (NOZZLE_WB_OD-NOZZLE_TOP_OD)/2=0' - 2 1/8"; -A=-3' - 6"; A=3' - 6"; A+.5=3' - 6 1/2"; A/2=1' - 9"; B=9' - 5"; B/2=4' - 8 1/2"; C=4' - 8"; C/2=2' - 4"; DUAL_F=7' - 9 1/4"; DUAL_F+1"=7' - 10 1/4"; DUAL_G=7' - 8 1/8"; E=3' - 4 15/16"; GA=0' - 0 3/32"; LONG_RO=11' - 5"; MB_A=4' - 6"; MB_HT=3' - 7 3/16"; MB_HT+.25"=3' - 7 7/16"; MB_HT-2.75"=3' - 4 7/16"; MB_HT/2=1' - 9 19/32"; Model=QMXVP-1X3_Mixing Box; NOZZLE_BOTTOM_ID=1' - 5 1/16"; NOZZLE_BOTTOM_RAD=0' - 8 17/32"; NOZZLE_HEIGHT=2' - 8"; NOZZLE_HEIGHT/7*2=0' - 8"; NOZZLE_SIZE=12' - 0"; NOZZLE_TOP_OD=1' - 7 1/2"; NOZZLE_TOP_RAD=0' - 9 3/4"; NOZZLE_WB/4=0' - 5 19/32"; NOZZLE_WB_OD=2' - 4"; NOZZLE_WB_RAD=1' - 2"; NOZZLE_WB_RAD-2"=1' - 0"; RO=2' - 10 3/4"; RO/2=1' - 5 3/8"; RO2/2=1' - 5 3/8"; TRANSITION_TOP=6' - 5 1/16"; TRIPLE_F+1"=12' - 1"; TRIP_F=12' - 0"; TRIP_G=11' - 11 1/4"; TYPE=0' - 0"; Type Comments=Vari-Plume Laboratory Exhaust Mixed-Flow Inline Belt Drive With 1X3 Mixing Box; UNIT_HEIGHT=3' - 5"; UNIT_HEIGHT*.75=2' - 6 3/4"; UNIT_OD=2' - 7 15/16"; UNIT_RAD+((A/2)+.25")=3' - 1 7/32"; UNIT_RAD+((A/2)+.25")+4"=3' - 5 7/32"; UNIT_RADIUS=1' - 3 31/32"; UNIT_RADIUS*.6=1' - 2 3/8"; UNIT_RADIUS+4"=1' - 7 31/32"
- 225_QMXVP-12H-1X3_Mixing_Box: (A/2)+.25"=1' - 9 1/4"; (A/2)-2"=1' - 7"; (NOZZLE_HEIGHT-(NOZZLE_HEIGHT/8*2))/2=1' - 0"; (NOZZLE_WB_OD-NOZZLE_TOP_OD)/2=0' - 2 1/8"; -A=-3' - 6"; A=3' - 6"; A+.5=3' - 6 1/2"; A/2=1' - 9"; B=9' - 5"; B/2=4' - 8 1/2"; C=4' - 8"; C/2=2' - 4"; DUAL_F=7' - 9 1/4"; DUAL_F+1"=7' - 10 1/4"; DUAL_G=7' - 8 1/8"; E=3' - 4 15/16"; GA=0' - 0 3/32"; LONG_RO=11' - 5"; MB_A=4' - 6"; MB_HT=3' - 7 3/16"; MB_HT+.25"=3' - 7 7/16"; MB_HT-2.75"=3' - 4 7/16"; MB_HT/2=1' - 9 19/32"; Model=QMXVP-1X3_Mixing Box; NOZZLE_BOTTOM_ID=1' - 5 1/16"; NOZZLE_BOTTOM_RAD=0' - 8 17/32"; NOZZLE_HEIGHT=2' - 8"; NOZZLE_HEIGHT/7*2=0' - 8"; NOZZLE_SIZE=12' - 0"; NOZZLE_TOP_OD=1' - 7 1/2"; NOZZLE_TOP_RAD=0' - 9 3/4"; NOZZLE_WB/4=0' - 5 19/32"; NOZZLE_WB_OD=2' - 4"; NOZZLE_WB_RAD=1' - 2"; NOZZLE_WB_RAD-2"=1' - 0"; RO=2' - 10 3/4"; RO/2=1' - 5 3/8"; RO2/2=1' - 5 3/8"; TRANSITION_TOP=6' - 5 1/16"; TRIPLE_F+1"=12' - 1"; TRIP_F=12' - 0"; TRIP_G=11' - 11 1/4"; TYPE=0' - 0"; Type Comments=Vari-Plume Laboratory Exhaust Mixed-Flow Inline Belt Drive With 1X3 Mixing Box; UNIT_HEIGHT=3' - 5"; UNIT_HEIGHT*.75=2' - 6 3/4"; UNIT_OD=2' - 7 15/16"; UNIT_RAD+((A/2)+.25")=3' - 1 7/32"; UNIT_RAD+((A/2)+.25")+4"=3' - 5 7/32"; UNIT_RADIUS=1' - 3 31/32"; UNIT_RADIUS*.6=1' - 2 3/8"; UNIT_RADIUS+4"=1' - 7 31/32"
- 225_QMXVP-15L-1X3_Mixing_Box: (A/2)+.25"=1' - 9 1/4"; (A/2)-2"=1' - 7"; (NOZZLE_HEIGHT-(NOZZLE_HEIGHT/8*2))/2=1' - 4 1/8"; (NOZZLE_WB_OD-NOZZLE_TOP_OD)/2=0' - 3 1/4"; -A=-3' - 6"; A=3' - 6"; A+.5=3' - 6 1/2"; A/2=1' - 9"; B=9' - 5"; B/2=4' - 8 1/2"; C=4' - 8"; C/2=2' - 4"; DUAL_F=7' - 9 1/4"; DUAL_F+1"=7' - 10 1/4"; DUAL_G=7' - 8 1/8"; E=3' - 4 15/16"; GA=0' - 0 3/32"; LONG_RO=11' - 5"; MB_A=4' - 6"; MB_HT=3' - 7 3/16"; MB_HT+.25"=3' - 7 7/16"; MB_HT-2.75"=3' - 4 7/16"; MB_HT/2=1' - 9 19/32"; Model=QMXVP-1X3_Mixing Box; NOZZLE_BOTTOM_ID=1' - 9 3/8"; NOZZLE_BOTTOM_RAD=0' - 10 11/16"; NOZZLE_HEIGHT=3' - 7"; NOZZLE_HEIGHT/7*2=0' - 10 3/4"; NOZZLE_SIZE=15' - 0"; NOZZLE_TOP_OD=1' - 11"; NOZZLE_TOP_RAD=0' - 11 1/2"; NOZZLE_WB/4=0' - 7 3/16"; NOZZLE_WB_OD=3' - 0"; NOZZLE_WB_RAD=1' - 6"; NOZZLE_WB_RAD-2"=1' - 4"; RO=2' - 10 3/4"; RO/2=1' - 5 3/8"; RO2/2=1' - 5 3/8"; TRANSITION_TOP=5' - 9 1/8"; TRIPLE_F+1"=12' - 1"; TRIP_F=12' - 0"; TRIP_G=11' - 11 1/4"; TYPE=0' - 0"; Type Comments=Vari-Plume Laboratory Exhaust Mixed-Flow Inline Belt Drive With 1X3 Mixing Box; UNIT_HEIGHT=3' - 5"; UNIT_HEIGHT*.75=2' - 6 3/4"; UNIT_OD=2' - 7 15/16"; UNIT_RAD+((A/2)+.25")=3' - 1 7/32"; UNIT_RAD+((A/2)+.25")+4"=3' - 5 7/32"; UNIT_RADIUS=1' - 3 31/32"; UNIT_RADIUS*.6=1' - 2 3/8"; UNIT_RADIUS+4"=1' - 7 31/32"
- 225_QMXVP-15H-1X3_Mixing_Box: (A/2)+.25"=1' - 9 1/4"; (A/2)-2"=1' - 7"; (NOZZLE_HEIGHT-(NOZZLE_HEIGHT/8*2))/2=1' - 4 1/8"; (NOZZLE_WB_OD-NOZZLE_TOP_OD)/2=0' - 3 1/4"; -A=-3' - 6"; A=3' - 6"; A+.5=3' - 6 1/2"; A/2=1' - 9"; B=9' - 5"; B/2=4' - 8 1/2"; C=4' - 8"; C/2=2' - 4"; DUAL_F=7' - 9 1/4"; DUAL_F+1"=7' - 10 1/4"; DUAL_G=7' - 8 1/8"; E=3' - 4 15/16"; GA=0' - 0 3/32"; LONG_RO=11' - 5"; MB_A=4' - 6"; MB_HT=3' - 7 3/16"; MB_HT+.25"=3' - 7 7/16"; MB_HT-2.75"=3' - 4 7/16"; MB_HT/2=1' - 9 19/32"; Model=QMXVP-1X3_Mixing Box; NOZZLE_BOTTOM_ID=1' - 9 3/8"; NOZZLE_BOTTOM_RAD=0' - 10 11/16"; NOZZLE_HEIGHT=3' - 7"; NOZZLE_HEIGHT/7*2=0' - 10 3/4"; NOZZLE_SIZE=15' - 0"; NOZZLE_TOP_OD=1' - 11"; NOZZLE_TOP_RAD=0' - 11 1/2"; NOZZLE_WB/4=0' - 7 3/16"; NOZZLE_WB_OD=3' - 0"; NOZZLE_WB_RAD=1' - 6"; NOZZLE_WB_RAD-2"=1' - 4"; RO=2' - 10 3/4"; RO/2=1' - 5 3/8"; RO2/2=1' - 5 3/8"; TRANSITION_TOP=5' - 9 1/8"; TRIPLE_F+1"=12' - 1"; TRIP_F=12' - 0"; TRIP_G=11' - 11 1/4"; TYPE=0' - 0"; Type Comments=Vari-Plume Laboratory Exhaust Mixed-Flow Inline Belt Drive With 1X3 Mixing Box; UNIT_HEIGHT=3' - 5"; UNIT_HEIGHT*.75=2' - 6 3/4"; UNIT_OD=2' - 7 15/16"; UNIT_RAD+((A/2)+.25")=3' - 1 7/32"; UNIT_RAD+((A/2)+.25")+4"=3' - 5 7/32"; UNIT_RADIUS=1' - 3 31/32"; UNIT_RADIUS*.6=1' - 2 3/8"; UNIT_RADIUS+4"=1' - 7 31/32"
- 225_QMXVP-18L-1X3_Mixing_Box: (A/2)+.25"=1' - 9 1/4"; (A/2)-2"=1' - 7"; (NOZZLE_HEIGHT-(NOZZLE_HEIGHT/8*2))/2=1' - 6"; (NOZZLE_WB_OD-NOZZLE_TOP_OD)/2=0' - 3 7/8"; -A=-3' - 6"; A=3' - 6"; A+.5=3' - 6 1/2"; A/2=1' - 9"; B=9' - 5"; B/2=4' - 8 1/2"; C=4' - 8"; C/2=2' - 4"; DUAL_F=7' - 9 1/4"; DUAL_F+1"=7' - 10 1/4"; DUAL_G=7' - 8 1/8"; E=3' - 4 15/16"; GA=0' - 0 3/32"; LONG_RO=11' - 5"; MB_A=4' - 6"; MB_HT=3' - 7 3/16"; MB_HT+.25"=3' - 7 7/16"; MB_HT-2.75"=3' - 4 7/16"; MB_HT/2=1' - 9 19/32"; Model=QMXVP-1X3_Mixing Box; NOZZLE_BOTTOM_ID=2' - 1 5/8"; NOZZLE_BOTTOM_RAD=1' - 0 13/16"; NOZZLE_HEIGHT=4' - 0"; NOZZLE_HEIGHT/7*2=1' - 0"; NOZZLE_SIZE=18' - 0"; NOZZLE_TOP_OD=2' - 3 1/2"; NOZZLE_TOP_RAD=1' - 1 3/4"; NOZZLE_WB/4=0' - 8 19/32"; NOZZLE_WB_OD=3' - 7"; NOZZLE_WB_RAD=1' - 9 1/2"; NOZZLE_WB_RAD-2"=1' - 7 1/2"; RO=2' - 10 3/4"; RO/2=1' - 5 3/8"; RO2/2=1' - 5 3/8"; TRANSITION_TOP=5' - 1 1/8"; TRIPLE_F+1"=12' - 1"; TRIP_F=12' - 0"; TRIP_G=11' - 11 1/4"; TYPE=0' - 0"; Type Comments=Vari-Plume Laboratory Exhaust Mixed-Flow Inline Belt Drive With 1X3 Mixing Box; UNIT_HEIGHT=3' - 5"; UNIT_HEIGHT*.75=2' - 6 3/4"; UNIT_OD=2' - 7 15/16"; UNIT_RAD+((A/2)+.25")=3' - 1 7/32"; UNIT_RAD+((A/2)+.25")+4"=3' - 5 7/32"; UNIT_RADIUS=1' - 3 31/32"; UNIT_RADIUS*.6=1' - 2 3/8"; UNIT_RADIUS+4"=1' - 7 31/32"
- 245_QMXVP-15L-1X3_Mixing_Box: (A/2)+.25"=1' - 10 1/4"; (A/2)-2"=1' - 8"; (NOZZLE_HEIGHT-(NOZZLE_HEIGHT/8*2))/2=1' - 4 1/8"; (NOZZLE_WB_OD-NOZZLE_TOP_OD)/2=0' - 3 1/4"; -A=-3' - 8"; A=3' - 8"; A+.5=3' - 8 1/2"; A/2=1' - 10"; B=10' - 1"; B/2=5' - 0 1/2"; C=4' - 11"; C/2=2' - 5 1/2"; DUAL_F=9' - 0 1/4"; DUAL_F+1"=9' - 1 1/4"; DUAL_G=8' - 11 1/8"; E=3' - 6 15/16"; GA=0' - 0 3/32"; LONG_RO=13' - 9 1/16"; MB_A=4' - 9"; MB_HT=3' - 9 7/16"; MB_HT+.25"=3' - 9 11/16"; MB_HT-2.75"=3' - 6 11/16"; MB_HT/2=1' - 10 23/32"; Model=QMXVP-1X3_Mixing Box; NOZZLE_BOTTOM_ID=1' - 9 3/8"; NOZZLE_BOTTOM_RAD=0' - 10 11/16"; NOZZLE_HEIGHT=3' - 7"; NOZZLE_HEIGHT/7*2=0' - 10 3/4"; NOZZLE_SIZE=15' - 0"; NOZZLE_TOP_OD=1' - 11"; NOZZLE_TOP_RAD=0' - 11 1/2"; NOZZLE_WB/4=0' - 7 3/16"; NOZZLE_WB_OD=3' - 0"; NOZZLE_WB_RAD=1' - 6"; NOZZLE_WB_RAD-2"=1' - 4"; RO=3' - 0 3/4"; RO/2=1' - 6 3/8"; RO2/2=1' - 6 3/8"; TRANSITION_TOP=6' - 5 11/16"; TRIPLE_F+1"=14' - 5"; TRIP_F=14' - 4"; TRIP_G=14' - 3 5/16"; TYPE=0' - 0"; Type Comments=Vari-Plume Laboratory Exhaust Mixed-Flow Inline Belt Drive With 1X3 Mixing Box; UNIT_HEIGHT=3' - 8 1/2"; UNIT_HEIGHT*.75=2' - 9 3/8"; UNIT_OD=2' - 10 3/4"; UNIT_RAD+((A/2)+.25")=3' - 3 5/8"; UNIT_RAD+((A/2)+.25")+4"=3' - 7 5/8"; UNIT_RADIUS=1' - 5 3/8"; UNIT_RADIUS*.6=1' - 3 5/8"; UNIT_RADIUS+4"=1' - 9 3/8"
- 245_QMXVP-15H-1X3_Mixing_Box: (A/2)+.25"=1' - 10 1/4"; (A/2)-2"=1' - 8"; (NOZZLE_HEIGHT-(NOZZLE_HEIGHT/8*2))/2=1' - 4 1/8"; (NOZZLE_WB_OD-NOZZLE_TOP_OD)/2=0' - 3 1/4"; -A=-3' - 8"; A=3' - 8"; A+.5=3' - 8 1/2"; A/2=1' - 10"; B=10' - 1"; B/2=5' - 0 1/2"; C=4' - 11"; C/2=2' - 5 1/2"; DUAL_F=9' - 0 1/4"; DUAL_F+1"=9' - 1 1/4"; DUAL_G=8' - 11 1/8"; E=3' - 6 15/16"; GA=0' - 0 3/32"; LONG_RO=13' - 9 1/16"; MB_A=4' - 9"; MB_HT=3' - 9 7/16"; MB_HT+.25"=3' - 9 11/16"; MB_HT-2.75"=3' - 6 11/16"; MB_HT/2=1' - 10 23/32"; Model=QMXVP-1X3_Mixing Box; NOZZLE_BOTTOM_ID=1' - 9 3/8"; NOZZLE_BOTTOM_RAD=0' - 10 11/16"; NOZZLE_HEIGHT=3' - 7"; NOZZLE_HEIGHT/7*2=0' - 10 3/4"; NOZZLE_SIZE=15' - 0"; NOZZLE_TOP_OD=1' - 11"; NOZZLE_TOP_RAD=0' - 11 1/2"; NOZZLE_WB/4=0' - 7 3/16"; NOZZLE_WB_OD=3' - 0"; NOZZLE_WB_RAD=1' - 6"; NOZZLE_WB_RAD-2"=1' - 4"; RO=3' - 0 3/4"; RO/2=1' - 6 3/8"; RO2/2=1' - 6 3/8"; TRANSITION_TOP=6' - 5 11/16"; TRIPLE_F+1"=14' - 5"; TRIP_F=14' - 4"; TRIP_G=14' - 3 5/16"; TYPE=0' - 0"; Type Comments=Vari-Plume Laboratory Exhaust Mixed-Flow Inline Belt Drive With 1X3 Mixing Box; UNIT_HEIGHT=3' - 8 1/2"; UNIT_HEIGHT*.75=2' - 9 3/8"; UNIT_OD=2' - 10 3/4"; UNIT_RAD+((A/2)+.25")=3' - 3 5/8"; UNIT_RAD+((A/2)+.25")+4"=3' - 7 5/8"; UNIT_RADIUS=1' - 5 3/8"; UNIT_RADIUS*.6=1' - 3 5/8"; UNIT_RADIUS+4"=1' - 9 3/8"
- 245_QMXVP-18L-1X3_Mixing_Box: (A/2)+.25"=1' - 10 1/4"; (A/2)-2"=1' - 8"; (NOZZLE_HEIGHT-(NOZZLE_HEIGHT/8*2))/2=1' - 6"; (NOZZLE_WB_OD-NOZZLE_TOP_OD)/2=0' - 3 7/8"; -A=-3' - 8"; A=3' - 8"; A+.5=3' - 8 1/2"; A/2=1' - 10"; B=10' - 1"; B/2=5' - 0 1/2"; C=4' - 11"; C/2=2' - 5 1/2"; DUAL_F=9' - 0 1/4"; DUAL_F+1"=9' - 1 1/4"; DUAL_G=8' - 11 1/8"; E=3' - 6 15/16"; GA=0' - 0 3/32"; LONG_RO=13' - 9 1/16"; MB_A=4' - 9"; MB_HT=3' - 9 7/16"; MB_HT+.25"=3' - 9 11/16"; MB_HT-2.75"=3' - 6 11/16"; MB_HT/2=1' - 10 23/32"; Model=QMXVP-1X3_Mixing Box; NOZZLE_BOTTOM_ID=2' - 1 5/8"; NOZZLE_BOTTOM_RAD=1' - 0 13/16"; NOZZLE_HEIGHT=4' - 0"; NOZZLE_HEIGHT/7*2=1' - 0"; NOZZLE_SIZE=18' - 0"; NOZZLE_TOP_OD=2' - 3 1/2"; NOZZLE_TOP_RAD=1' - 1 3/4"; NOZZLE_WB/4=0' - 8 19/32"; NOZZLE_WB_OD=3' - 7"; NOZZLE_WB_RAD=1' - 9 1/2"; NOZZLE_WB_RAD-2"=1' - 7 1/2"; RO=3' - 0 3/4"; RO/2=1' - 6 3/8"; RO2/2=1' - 6 3/8"; TRANSITION_TOP=5' - 9 11/16"; TRIPLE_F+1"=14' - 5"; TRIP_F=14' - 4"; TRIP_G=14' - 3 5/16"; TYPE=0' - 0"; Type Comments=Vari-Plume Laboratory Exhaust Mixed-Flow Inline Belt Drive With 1X3 Mixing Box; UNIT_HEIGHT=3' - 8 1/2"; UNIT_HEIGHT*.75=2' - 9 3/8"; UNIT_OD=2' - 10 3/4"; UNIT_RAD+((A/2)+.25")=3' - 3 5/8"; UNIT_RAD+((A/2)+.25")+4"=3' - 7 5/8"; UNIT_RADIUS=1' - 5 3/8"; UNIT_RADIUS*.6=1' - 3 5/8"; UNIT_RADIUS+4"=1' - 9 3/8"
- 245_QMXVP-18H-1X3_Mixing_Box: (A/2)+.25"=1' - 10 1/4"; (A/2)-2"=1' - 8"; (NOZZLE_HEIGHT-(NOZZLE_HEIGHT/8*2))/2=1' - 6"; (NOZZLE_WB_OD-NOZZLE_TOP_OD)/2=0' - 3 7/8"; -A=-3' - 8"; A=3' - 8"; A+.5=3' - 8 1/2"; A/2=1' - 10"; B=10' - 1"; B/2=5' - 0 1/2"; C=4' - 11"; C/2=2' - 5 1/2"; DUAL_F=9' - 0 1/4"; DUAL_F+1"=9' - 1 1/4"; DUAL_G=8' - 11 1/8"; E=3' - 6 15/16"; GA=0' - 0 3/32"; LONG_RO=13' - 9 1/16"; MB_A=4' - 9"; MB_HT=3' - 9 7/16"; MB_HT+.25"=3' - 9 11/16"; MB_HT-2.75"=3' - 6 11/16"; MB_HT/2=1' - 10 23/32"; Model=QMXVP-1X3_Mixing Box; NOZZLE_BOTTOM_ID=2' - 1 5/8"; NOZZLE_BOTTOM_RAD=1' - 0 13/16"; NOZZLE_HEIGHT=4' - 0"; NOZZLE_HEIGHT/7*2=1' - 0"; NOZZLE_SIZE=18' - 0"; NOZZLE_TOP_OD=2' - 3 1/2"; NOZZLE_TOP_RAD=1' - 1 3/4"; NOZZLE_WB/4=0' - 8 19/32"; NOZZLE_WB_OD=3' - 7"; NOZZLE_WB_RAD=1' - 9 1/2"; NOZZLE_WB_RAD-2"=1' - 7 1/2"; RO=3' - 0 3/4"; RO/2=1' - 6 3/8"; RO2/2=1' - 6 3/8"; TRANSITION_TOP=5' - 9 11/16"; TRIPLE_F+1"=14' - 5"; TRIP_F=14' - 4"; TRIP_G=14' - 3 5/16"; TYPE=0' - 0"; Type Comments=Vari-Plume Laboratory Exhaust Mixed-Flow Inline Belt Drive With 1X3 Mixing Box; UNIT_HEIGHT=3' - 8 1/2"; UNIT_HEIGHT*.75=2' - 9 3/8"; UNIT_OD=2' - 10 3/4"; UNIT_RAD+((A/2)+.25")=3' - 3 5/8"; UNIT_RAD+((A/2)+.25")+4"=3' - 7 5/8"; UNIT_RADIUS=1' - 5 3/8"; UNIT_RADIUS*.6=1' - 3 5/8"; UNIT_RADIUS+4"=1' - 9 3/8"
- 245_QMXVP-24L-1X3_Mixing_Box: (A/2)+.25"=1' - 10 1/4"; (A/2)-2"=1' - 8"; (NOZZLE_HEIGHT-(NOZZLE_HEIGHT/8*2))/2=1' - 11 1/4"; (NOZZLE_WB_OD-NOZZLE_TOP_OD)/2=0' - 6 1/8"; -A=-3' - 8"; A=3' - 8"; A+.5=3' - 8 1/2"; A/2=1' - 10"; B=10' - 1"; B/2=5' - 0 1/2"; C=4' - 11"; C/2=2' - 5 1/2"; DUAL_F=9' - 0 1/4"; DUAL_F+1"=9' - 1 1/4"; DUAL_G=8' - 11 1/8"; E=3' - 6 15/16"; GA=0' - 0 3/32"; LONG_RO=13' - 9 1/16"; MB_A=4' - 9"; MB_HT=3' - 9 7/16"; MB_HT+.25"=3' - 9 11/16"; MB_HT-2.75"=3' - 6 11/16"; MB_HT/2=1' - 10 23/32"; Model=QMXVP-1X3_Mixing Box; NOZZLE_BOTTOM_ID=2' - 10 3/4"; NOZZLE_BOTTOM_RAD=1' - 5 3/8"; NOZZLE_HEIGHT=5' - 2"; NOZZLE_HEIGHT/7*2=1' - 3 1/2"; NOZZLE_SIZE=24' - 0"; NOZZLE_TOP_OD=3' - 0 1/2"; NOZZLE_TOP_RAD=1' - 6 1/4"; NOZZLE_WB/4=1' - 0 3/16"; NOZZLE_WB_OD=5' - 1"; NOZZLE_WB_RAD=2' - 6 1/2"; NOZZLE_WB_RAD-2"=2' - 4 1/2"; RO=3' - 0 3/4"; RO/2=1' - 6 3/8"; RO2/2=1' - 6 3/8"; TRANSITION_TOP=4' - 9 3/4"; TRIPLE_F+1"=14' - 5"; TRIP_F=14' - 4"; TRIP_G=14' - 3 5/16"; TYPE=0' - 0"; Type Comments=Vari-Plume Laboratory Exhaust Mixed-Flow Inline Belt Drive With 1X3 Mixing Box; UNIT_HEIGHT=3' - 8 1/2"; UNIT_HEIGHT*.75=2' - 9 3/8"; UNIT_OD=2' - 10 3/4"; UNIT_RAD+((A/2)+.25")=3' - 3 5/8"; UNIT_RAD+((A/2)+.25")+4"=3' - 7 5/8"; UNIT_RADIUS=1' - 5 3/8"; UNIT_RADIUS*.6=1' - 3 5/8"; UNIT_RADIUS+4"=1' - 9 3/8"
- 245_QMXVP-24H-1X3_Mixing_Box: (A/2)+.25"=1' - 10 1/4"; (A/2)-2"=1' - 8"; (NOZZLE_HEIGHT-(NOZZLE_HEIGHT/8*2))/2=1' - 11 1/4"; (NOZZLE_WB_OD-NOZZLE_TOP_OD)/2=0' - 6 1/8"; -A=-3' - 8"; A=3' - 8"; A+.5=3' - 8 1/2"; A/2=1' - 10"; B=10' - 1"; B/2=5' - 0 1/2"; C=4' - 11"; C/2=2' - 5 1/2"; DUAL_F=9' - 0 1/4"; DUAL_F+1"=9' - 1 1/4"; DUAL_G=8' - 11 1/8"; E=3' - 6 15/16"; GA=0' - 0 3/32"; LONG_RO=13' - 9 1/16"; MB_A=4' - 9"; MB_HT=3' - 9 7/16"; MB_HT+.25"=3' - 9 11/16"; MB_HT-2.75"=3' - 6 11/16"; MB_HT/2=1' - 10 23/32"; Model=QMXVP-1X3_Mixing Box; NOZZLE_BOTTOM_ID=2' - 10 3/4"; NOZZLE_BOTTOM_RAD=1' - 5 3/8"; NOZZLE_HEIGHT=5' - 2"; NOZZLE_HEIGHT/7*2=1' - 3 1/2"; NOZZLE_SIZE=24' - 0"; NOZZLE_TOP_OD=3' - 0 1/2"; NOZZLE_TOP_RAD=1' - 6 1/4"; NOZZLE_WB/4=1' - 0 3/16"; NOZZLE_WB_OD=5' - 1"; NOZZLE_WB_RAD=2' - 6 1/2"; NOZZLE_WB_RAD-2"=2' - 4 1/2"; RO=3' - 0 3/4"; RO/2=1' - 6 3/8"; RO2/2=1' - 6 3/8"; TRANSITION_TOP=4' - 9 3/4"; TRIPLE_F+1"=14' - 5"; TRIP_F=14' - 4"; TRIP_G=14' - 3 5/16"; TYPE=0' - 0"; Type Comments=Vari-Plume Laboratory Exhaust Mixed-Flow Inline Belt Drive With 1X3 Mixing Box; UNIT_HEIGHT=3' - 8 1/2"; UNIT_HEIGHT*.75=2' - 9 3/8"; UNIT_OD=2' - 10 3/4"; UNIT_RAD+((A/2)+.25")=3' - 3 5/8"; UNIT_RAD+((A/2)+.25")+4"=3' - 7 5/8"; UNIT_RADIUS=1' - 5 3/8"; UNIT_RADIUS*.6=1' - 3 5/8"; UNIT_RADIUS+4"=1' - 9 3/8"
- 270_QMXVP-15L-1X3_Mixing_Box: (A/2)+.25"=2' - 0 1/4"; (A/2)-2"=1' - 10"; (NOZZLE_HEIGHT-(NOZZLE_HEIGHT/8*2))/2=1' - 4 1/8"; (NOZZLE_WB_OD-NOZZLE_TOP_OD)/2=0' - 3 1/4"; -A=-4' - 0"; A=4' - 0"; A+.5=4' - 0 1/2"; A/2=2' - 0"; B=10' - 8"; B/2=5' - 4"; C=5' - 3"; C/2=2' - 7 1/2"; DUAL_F=9' - 4 1/4"; DUAL_F+1"=9' - 5 1/4"; DUAL_G=9' - 3 1/8"; E=3' - 10 15/16"; GA=0' - 0 3/32"; LONG_RO=14' - 1 1/16"; MB_A=5' - 2"; MB_HT=3' - 11 3/16"; MB_HT+.25"=3' - 11 7/16"; MB_HT-2.75"=3' - 8 7/16"; MB_HT/2=1' - 11 19/32"; Model=QMXVP-1X3_Mixing Box; NOZZLE_BOTTOM_ID=1' - 9 3/8"; NOZZLE_BOTTOM_RAD=0' - 10 11/16"; NOZZLE_HEIGHT=3' - 7"; NOZZLE_HEIGHT/7*2=0' - 10 3/4"; NOZZLE_SIZE=15' - 0"; NOZZLE_TOP_OD=1' - 11"; NOZZLE_TOP_RAD=0' - 11 1/2"; NOZZLE_WB/4=0' - 7 3/16"; NOZZLE_WB_OD=3' - 0"; NOZZLE_WB_RAD=1' - 6"; NOZZLE_WB_RAD-2"=1' - 4"; RO=3' - 4 3/4"; RO/2=1' - 8 3/8"; RO2/2=1' - 8 3/8"; TRANSITION_TOP=7' - 2 3/16"; TRIPLE_F+1"=14' - 9"; TRIP_F=14' - 8"; TRIP_G=14' - 7 5/16"; TYPE=0' - 0"; Type Comments=Vari-Plume Laboratory Exhaust Mixed-Flow Inline Belt Drive With 1X3 Mixing Box; UNIT_HEIGHT=3' - 11"; UNIT_HEIGHT*.75=2' - 11 1/4"; UNIT_OD=3' - 2 5/16"; UNIT_RAD+((A/2)+.25")=3' - 7 13/32"; UNIT_RAD+((A/2)+.25")+4"=3' - 11 13/32"; UNIT_RADIUS=1' - 7 5/32"; UNIT_RADIUS*.6=1' - 5 1/4"; UNIT_RADIUS+4"=1' - 11 5/32"
- 270_QMXVP-15H-1X3_Mixing_Box: (A/2)+.25"=2' - 0 1/4"; (A/2)-2"=1' - 10"; (NOZZLE_HEIGHT-(NOZZLE_HEIGHT/8*2))/2=1' - 4 1/8"; (NOZZLE_WB_OD-NOZZLE_TOP_OD)/2=0' - 3 1/4"; -A=-4' - 0"; A=4' - 0"; A+.5=4' - 0 1/2"; A/2=2' - 0"; B=10' - 8"; B/2=5' - 4"; C=5' - 3"; C/2=2' - 7 1/2"; DUAL_F=9' - 4 1/4"; DUAL_F+1"=9' - 5 1/4"; DUAL_G=9' - 3 1/8"; E=3' - 10 15/16"; GA=0' - 0 3/32"; LONG_RO=14' - 1 1/16"; MB_A=5' - 2"; MB_HT=3' - 11 3/16"; MB_HT+.25"=3' - 11 7/16"; MB_HT-2.75"=3' - 8 7/16"; MB_HT/2=1' - 11 19/32"; Model=QMXVP-1X3_Mixing Box; NOZZLE_BOTTOM_ID=1' - 9 3/8"; NOZZLE_BOTTOM_RAD=0' - 10 11/16"; NOZZLE_HEIGHT=3' - 7"; NOZZLE_HEIGHT/7*2=0' - 10 3/4"; NOZZLE_SIZE=15' - 0"; NOZZLE_TOP_OD=1' - 11"; NOZZLE_TOP_RAD=0' - 11 1/2"; NOZZLE_WB/4=0' - 7 3/16"; NOZZLE_WB_OD=3' - 0"; NOZZLE_WB_RAD=1' - 6"; NOZZLE_WB_RAD-2"=1' - 4"; RO=3' - 4 3/4"; RO/2=1' - 8 3/8"; RO2/2=1' - 8 3/8"; TRANSITION_TOP=7' - 2 3/16"; TRIPLE_F+1"=14' - 9"; TRIP_F=14' - 8"; TRIP_G=14' - 7 5/16"; TYPE=0' - 0"; Type Comments=Vari-Plume Laboratory Exhaust Mixed-Flow Inline Belt Drive With 1X3 Mixing Box; UNIT_HEIGHT=3' - 11"; UNIT_HEIGHT*.75=2' - 11 1/4"; UNIT_OD=3' - 2 5/16"; UNIT_RAD+((A/2)+.25")=3' - 7 13/32"; UNIT_RAD+((A/2)+.25")+4"=3' - 11 13/32"; UNIT_RADIUS=1' - 7 5/32"; UNIT_RADIUS*.6=1' - 5 1/4"; UNIT_RADIUS+4"=1' - 11 5/32"
- 270_QMXVP-18L-1X3_Mixing_Box: (A/2)+.25"=2' - 0 1/4"; (A/2)-2"=1' - 10"; (NOZZLE_HEIGHT-(NOZZLE_HEIGHT/8*2))/2=1' - 6"; (NOZZLE_WB_OD-NOZZLE_TOP_OD)/2=0' - 3 7/8"; -A=-4' - 0"; A=4' - 0"; A+.5=4' - 0 1/2"; A/2=2' - 0"; B=10' - 8"; B/2=5' - 4"; C=5' - 3"; C/2=2' - 7 1/2"; DUAL_F=9' - 4 1/4"; DUAL_F+1"=9' - 5 1/4"; DUAL_G=9' - 3 1/8"; E=3' - 10 15/16"; GA=0' - 0 3/32"; LONG_RO=14' - 1 1/16"; MB_A=5' - 2"; MB_HT=3' - 11 3/16"; MB_HT+.25"=3' - 11 7/16"; MB_HT-2.75"=3' - 8 7/16"; MB_HT/2=1' - 11 19/32"; Model=QMXVP-1X3_Mixing Box; NOZZLE_BOTTOM_ID=2' - 1 5/8"; NOZZLE_BOTTOM_RAD=1' - 0 13/16"; NOZZLE_HEIGHT=4' - 0"; NOZZLE_HEIGHT/7*2=1' - 0"; NOZZLE_SIZE=18' - 0"; NOZZLE_TOP_OD=2' - 3 1/2"; NOZZLE_TOP_RAD=1' - 1 3/4"; NOZZLE_WB/4=0' - 8 19/32"; NOZZLE_WB_OD=3' - 7"; NOZZLE_WB_RAD=1' - 9 1/2"; NOZZLE_WB_RAD-2"=1' - 7 1/2"; RO=3' - 4 3/4"; RO/2=1' - 8 3/8"; RO2/2=1' - 8 3/8"; TRANSITION_TOP=6' - 7 3/16"; TRIPLE_F+1"=14' - 9"; TRIP_F=14' - 8"; TRIP_G=14' - 7 5/16"; TYPE=0' - 0"; Type Comments=Vari-Plume Laboratory Exhaust Mixed-Flow Inline Belt Drive With 1X3 Mixing Box; UNIT_HEIGHT=3' - 11"; UNIT_HEIGHT*.75=2' - 11 1/4"; UNIT_OD=3' - 2 5/16"; UNIT_RAD+((A/2)+.25")=3' - 7 13/32"; UNIT_RAD+((A/2)+.25")+4"=3' - 11 13/32"; UNIT_RADIUS=1' - 7 5/32"; UNIT_RADIUS*.6=1' - 5 1/4"; UNIT_RADIUS+4"=1' - 11 5/32"
- 270_QMXVP-18H-1X3_Mixing_Box: (A/2)+.25"=2' - 0 1/4"; (A/2)-2"=1' - 10"; (NOZZLE_HEIGHT-(NOZZLE_HEIGHT/8*2))/2=1' - 6"; (NOZZLE_WB_OD-NOZZLE_TOP_OD)/2=0' - 3 7/8"; -A=-4' - 0"; A=4' - 0"; A+.5=4' - 0 1/2"; A/2=2' - 0"; B=10' - 8"; B/2=5' - 4"; C=5' - 3"; C/2=2' - 7 1/2"; DUAL_F=9' - 4 1/4"; DUAL_F+1"=9' - 5 1/4"; DUAL_G=9' - 3 1/8"; E=3' - 10 15/16"; GA=0' - 0 3/32"; LONG_RO=14' - 1 1/16"; MB_A=5' - 2"; MB_HT=3' - 11 3/16"; MB_HT+.25"=3' - 11 7/16"; MB_HT-2.75"=3' - 8 7/16"; MB_HT/2=1' - 11 19/32"; Model=QMXVP-1X3_Mixing Box; NOZZLE_BOTTOM_ID=2' - 1 5/8"; NOZZLE_BOTTOM_RAD=1' - 0 13/16"; NOZZLE_HEIGHT=4' - 0"; NOZZLE_HEIGHT/7*2=1' - 0"; NOZZLE_SIZE=18' - 0"; NOZZLE_TOP_OD=2' - 3 1/2"; NOZZLE_TOP_RAD=1' - 1 3/4"; NOZZLE_WB/4=0' - 8 19/32"; NOZZLE_WB_OD=3' - 7"; NOZZLE_WB_RAD=1' - 9 1/2"; NOZZLE_WB_RAD-2"=1' - 7 1/2"; RO=3' - 4 3/4"; RO/2=1' - 8 3/8"; RO2/2=1' - 8 3/8"; TRANSITION_TOP=6' - 7 3/16"; TRIPLE_F+1"=14' - 9"; TRIP_F=14' - 8"; TRIP_G=14' - 7 5/16"; TYPE=0' - 0"; Type Comments=Vari-Plume Laboratory Exhaust Mixed-Flow Inline Belt Drive With 1X3 Mixing Box; UNIT_HEIGHT=3' - 11"; UNIT_HEIGHT*.75=2' - 11 1/4"; UNIT_OD=3' - 2 5/16"; UNIT_RAD+((A/2)+.25")=3' - 7 13/32"; UNIT_RAD+((A/2)+.25")+4"=3' - 11 13/32"; UNIT_RADIUS=1' - 7 5/32"; UNIT_RADIUS*.6=1' - 5 1/4"; UNIT_RADIUS+4"=1' - 11 5/32"
- 270_QMXVP-24L-1X3_Mixing_Box: (A/2)+.25"=2' - 0 1/4"; (A/2)-2"=1' - 10"; (NOZZLE_HEIGHT-(NOZZLE_HEIGHT/8*2))/2=1' - 11 1/4"; (NOZZLE_WB_OD-NOZZLE_TOP_OD)/2=0' - 6 1/8"; -A=-4' - 0"; A=4' - 0"; A+.5=4' - 0 1/2"; A/2=2' - 0"; B=10' - 8"; B/2=5' - 4"; C=5' - 3"; C/2=2' - 7 1/2"; DUAL_F=9' - 4 1/4"; DUAL_F+1"=9' - 5 1/4"; DUAL_G=9' - 3 1/8"; E=3' - 10 15/16"; GA=0' - 0 3/32"; LONG_RO=14' - 1 1/16"; MB_A=5' - 2"; MB_HT=3' - 11 3/16"; MB_HT+.25"=3' - 11 7/16"; MB_HT-2.75"=3' - 8 7/16"; MB_HT/2=1' - 11 19/32"; Model=QMXVP-1X3_Mixing Box; NOZZLE_BOTTOM_ID=2' - 10 3/4"; NOZZLE_BOTTOM_RAD=1' - 5 3/8"; NOZZLE_HEIGHT=5' - 2"; NOZZLE_HEIGHT/7*2=1' - 3 1/2"; NOZZLE_SIZE=24' - 0"; NOZZLE_TOP_OD=3' - 0 1/2"; NOZZLE_TOP_RAD=1' - 6 1/4"; NOZZLE_WB/4=1' - 0 3/16"; NOZZLE_WB_OD=5' - 1"; NOZZLE_WB_RAD=2' - 6 1/2"; NOZZLE_WB_RAD-2"=2' - 4 1/2"; RO=3' - 4 3/4"; RO/2=1' - 8 3/8"; RO2/2=1' - 8 3/8"; TRANSITION_TOP=5' - 2 1/4"; TRIPLE_F+1"=14' - 9"; TRIP_F=14' - 8"; TRIP_G=14' - 7 5/16"; TYPE=0' - 0"; Type Comments=Vari-Plume Laboratory Exhaust Mixed-Flow Inline Belt Drive With 1X3 Mixing Box; UNIT_HEIGHT=3' - 11"; UNIT_HEIGHT*.75=2' - 11 1/4"; UNIT_OD=3' - 2 5/16"; UNIT_RAD+((A/2)+.25")=3' - 7 13/32"; UNIT_RAD+((A/2)+.25")+4"=3' - 11 13/32"; UNIT_RADIUS=1' - 7 5/32"; UNIT_RADIUS*.6=1' - 5 1/4"; UNIT_RADIUS+4"=1' - 11 5/32"
- 270_QMXVP-24H-1X3_Mixing_Box: (A/2)+.25"=2' - 0 1/4"; (A/2)-2"=1' - 10"; (NOZZLE_HEIGHT-(NOZZLE_HEIGHT/8*2))/2=1' - 11 1/4"; (NOZZLE_WB_OD-NOZZLE_TOP_OD)/2=0' - 6 1/8"; -A=-4' - 0"; A=4' - 0"; A+.5=4' - 0 1/2"; A/2=2' - 0"; B=10' - 8"; B/2=5' - 4"; C=5' - 3"; C/2=2' - 7 1/2"; DUAL_F=9' - 4 1/4"; DUAL_F+1"=9' - 5 1/4"; DUAL_G=9' - 3 1/8"; E=3' - 10 15/16"; GA=0' - 0 3/32"; LONG_RO=14' - 1 1/16"; MB_A=5' - 2"; MB_HT=3' - 11 3/16"; MB_HT+.25"=3' - 11 7/16"; MB_HT-2.75"=3' - 8 7/16"; MB_HT/2=1' - 11 19/32"; Model=QMXVP-1X3_Mixing Box; NOZZLE_BOTTOM_ID=2' - 10 3/4"; NOZZLE_BOTTOM_RAD=1' - 5 3/8"; NOZZLE_HEIGHT=5' - 2"; NOZZLE_HEIGHT/7*2=1' - 3 1/2"; NOZZLE_SIZE=24' - 0"; NOZZLE_TOP_OD=3' - 0 1/2"; NOZZLE_TOP_RAD=1' - 6 1/4"; NOZZLE_WB/4=1' - 0 3/16"; NOZZLE_WB_OD=5' - 1"; NOZZLE_WB_RAD=2' - 6 1/2"; NOZZLE_WB_RAD-2"=2' - 4 1/2"; RO=3' - 4 3/4"; RO/2=1' - 8 3/8"; RO2/2=1' - 8 3/8"; TRANSITION_TOP=5' - 2 1/4"; TRIPLE_F+1"=14' - 9"; TRIP_F=14' - 8"; TRIP_G=14' - 7 5/16"; TYPE=0' - 0"; Type Comments=Vari-Plume Laboratory Exhaust Mixed-Flow Inline Belt Drive With 1X3 Mixing Box; UNIT_HEIGHT=3' - 11"; UNIT_HEIGHT*.75=2' - 11 1/4"; UNIT_OD=3' - 2 5/16"; UNIT_RAD+((A/2)+.25")=3' - 7 13/32"; UNIT_RAD+((A/2)+.25")+4"=3' - 11 13/32"; UNIT_RADIUS=1' - 7 5/32"; UNIT_RADIUS*.6=1' - 5 1/4"; UNIT_RADIUS+4"=1' - 11 5/32"
- 300_QMXVP-18L-1X3_Mixing_Box: (A/2)+.25"=2' - 2 1/4"; (A/2)-2"=2' - 0"; (NOZZLE_HEIGHT-(NOZZLE_HEIGHT/8*2))/2=1' - 6"; (NOZZLE_WB_OD-NOZZLE_TOP_OD)/2=0' - 3 7/8"; -A=-4' - 4"; A=4' - 4"; A+.5=4' - 4 1/2"; A/2=2' - 2"; B=12' - 4"; B/2=6' - 2"; C=5' - 7"; C/2=2' - 9 1/2"; DUAL_F=11' - 0 1/4"; DUAL_F+1"=11' - 1 1/4"; DUAL_G=10' - 11 1/8"; E=4' - 2 15/16"; GA=0' - 0 3/32"; LONG_RO=17' - 1 1/16"; MB_A=5' - 8"; MB_HT=4' - 2 7/16"; MB_HT+.25"=4' - 2 11/16"; MB_HT-2.75"=3' - 11 11/16"; MB_HT/2=2' - 1 7/32"; Model=QMXVP-1X3_Mixing Box; NOZZLE_BOTTOM_ID=2' - 1 5/8"; NOZZLE_BOTTOM_RAD=1' - 0 13/16"; NOZZLE_HEIGHT=4' - 0"; NOZZLE_HEIGHT/7*2=1' - 0"; NOZZLE_SIZE=18' - 0"; NOZZLE_TOP_OD=2' - 3 1/2"; NOZZLE_TOP_RAD=1' - 1 3/4"; NOZZLE_WB/4=0' - 8 19/32"; NOZZLE_WB_OD=3' - 7"; NOZZLE_WB_RAD=1' - 9 1/2"; NOZZLE_WB_RAD-2"=1' - 7 1/2"; RO=3' - 8 3/4"; RO/2=1' - 10 3/8"; RO2/2=1' - 10 3/8"; TRANSITION_TOP=7' - 10 3/16"; TRIPLE_F+1"=17' - 9"; TRIP_F=17' - 8"; TRIP_G=17' - 7 5/16"; TYPE=0' - 0"; Type Comments=Vari-Plume Laboratory Exhaust Mixed-Flow Inline Belt Drive With 1X3 Mixing Box; UNIT_HEIGHT=4' - 6"; UNIT_HEIGHT*.75=3' - 4 1/2"; UNIT_OD=3' - 6 1/2"; UNIT_RAD+((A/2)+.25")=3' - 11 1/2"; UNIT_RAD+((A/2)+.25")+4"=4' - 3 1/2"; UNIT_RADIUS=1' - 9 1/4"; UNIT_RADIUS*.6=1' - 7 1/8"; UNIT_RADIUS+4"=2' - 1 1/4"
- 300_QMXVP-18H-1X3_Mixing_Box: (A/2)+.25"=2' - 2 1/4"; (A/2)-2"=2' - 0"; (NOZZLE_HEIGHT-(NOZZLE_HEIGHT/8*2))/2=1' - 6"; (NOZZLE_WB_OD-NOZZLE_TOP_OD)/2=0' - 3 7/8"; -A=-4' - 4"; A=4' - 4"; A+.5=4' - 4 1/2"; A/2=2' - 2"; B=12' - 4"; B/2=6' - 2"; C=5' - 7"; C/2=2' - 9 1/2"; DUAL_F=11' - 0 1/4"; DUAL_F+1"=11' - 1 1/4"; DUAL_G=10' - 11 1/8"; E=4' - 2 15/16"; GA=0' - 0 3/32"; LONG_RO=17' - 1 1/16"; MB_A=5' - 8"; MB_HT=4' - 2 7/16"; MB_HT+.25"=4' - 2 11/16"; MB_HT-2.75"=3' - 11 11/16"; MB_HT/2=2' - 1 7/32"; Model=QMXVP-1X3_Mixing Box; NOZZLE_BOTTOM_ID=2' - 1 5/8"; NOZZLE_BOTTOM_RAD=1' - 0 13/16"; NOZZLE_HEIGHT=4' - 0"; NOZZLE_HEIGHT/7*2=1' - 0"; NOZZLE_SIZE=18' - 0"; NOZZLE_TOP_OD=2' - 3 1/2"; NOZZLE_TOP_RAD=1' - 1 3/4"; NOZZLE_WB/4=0' - 8 19/32"; NOZZLE_WB_OD=3' - 7"; NOZZLE_WB_RAD=1' - 9 1/2"; NOZZLE_WB_RAD-2"=1' - 7 1/2"; RO=3' - 8 3/4"; RO/2=1' - 10 3/8"; RO2/2=1' - 10 3/8"; TRANSITION_TOP=7' - 10 3/16"; TRIPLE_F+1"=17' - 9"; TRIP_F=17' - 8"; TRIP_G=17' - 7 5/16"; TYPE=0' - 0"; Type Comments=Vari-Plume Laboratory Exhaust Mixed-Flow Inline Belt Drive With 1X3 Mixing Box; UNIT_HEIGHT=4' - 6"; UNIT_HEIGHT*.75=3' - 4 1/2"; UNIT_OD=3' - 6 1/2"; UNIT_RAD+((A/2)+.25")=3' - 11 1/2"; UNIT_RAD+((A/2)+.25")+4"=4' - 3 1/2"; UNIT_RADIUS=1' - 9 1/4"; UNIT_RADIUS*.6=1' - 7 1/8"; UNIT_RADIUS+4"=2' - 1 1/4"
- 300_QMXVP-24L-1X3_Mixing_Box: (A/2)+.25"=2' - 2 1/4"; (A/2)-2"=2' - 0"; (NOZZLE_HEIGHT-(NOZZLE_HEIGHT/8*2))/2=1' - 11 1/4"; (NOZZLE_WB_OD-NOZZLE_TOP_OD)/2=0' - 6 1/8"; -A=-4' - 4"; A=4' - 4"; A+.5=4' - 4 1/2"; A/2=2' - 2"; B=12' - 4"; B/2=6' - 2"; C=5' - 7"; C/2=2' - 9 1/2"; DUAL_F=11' - 0 1/4"; DUAL_F+1"=11' - 1 1/4"; DUAL_G=10' - 11 1/8"; E=4' - 2 15/16"; GA=0' - 0 3/32"; LONG_RO=17' - 1 1/16"; MB_A=5' - 8"; MB_HT=4' - 2 7/16"; MB_HT+.25"=4' - 2 11/16"; MB_HT-2.75"=3' - 11 11/16"; MB_HT/2=2' - 1 7/32"; Model=QMXVP-1X3_Mixing Box; NOZZLE_BOTTOM_ID=2' - 10 3/4"; NOZZLE_BOTTOM_RAD=1' - 5 3/8"; NOZZLE_HEIGHT=5' - 2"; NOZZLE_HEIGHT/7*2=1' - 3 1/2"; NOZZLE_SIZE=24' - 0"; NOZZLE_TOP_OD=3' - 0 1/2"; NOZZLE_TOP_RAD=1' - 6 1/4"; NOZZLE_WB/4=1' - 0 3/16"; NOZZLE_WB_OD=5' - 1"; NOZZLE_WB_RAD=2' - 6 1/2"; NOZZLE_WB_RAD-2"=2' - 4 1/2"; RO=3' - 8 3/4"; RO/2=1' - 10 3/8"; RO2/2=1' - 10 3/8"; TRANSITION_TOP=6' - 5 1/4"; TRIPLE_F+1"=17' - 9"; TRIP_F=17' - 8"; TRIP_G=17' - 7 5/16"; TYPE=0' - 0"; Type Comments=Vari-Plume Laboratory Exhaust Mixed-Flow Inline Belt Drive With 1X3 Mixing Box; UNIT_HEIGHT=4' - 6"; UNIT_HEIGHT*.75=3' - 4 1/2"; UNIT_OD=3' - 6 1/2"; UNIT_RAD+((A/2)+.25")=3' - 11 1/2"; UNIT_RAD+((A/2)+.25")+4"=4' - 3 1/2"; UNIT_RADIUS=1' - 9 1/4"; UNIT_RADIUS*.6=1' - 7 1/8"; UNIT_RADIUS+4"=2' - 1 1/4"
- 300_QMXVP-24H-1X3_Mixing_Box: (A/2)+.25"=2' - 2 1/4"; (A/2)-2"=2' - 0"; (NOZZLE_HEIGHT-(NOZZLE_HEIGHT/8*2))/2=1' - 11 1/4"; (NOZZLE_WB_OD-NOZZLE_TOP_OD)/2=0' - 6 1/8"; -A=-4' - 4"; A=4' - 4"; A+.5=4' - 4 1/2"; A/2=2' - 2"; B=12' - 4"; B/2=6' - 2"; C=5' - 7"; C/2=2' - 9 1/2"; DUAL_F=11' - 0 1/4"; DUAL_F+1"=11' - 1 1/4"; DUAL_G=10' - 11 1/8"; E=4' - 2 15/16"; GA=0' - 0 3/32"; LONG_RO=17' - 1 1/16"; MB_A=5' - 8"; MB_HT=4' - 2 7/16"; MB_HT+.25"=4' - 2 11/16"; MB_HT-2.75"=3' - 11 11/16"; MB_HT/2=2' - 1 7/32"; Model=QMXVP-1X3_Mixing Box; NOZZLE_BOTTOM_ID=2' - 10 3/4"; NOZZLE_BOTTOM_RAD=1' - 5 3/8"; NOZZLE_HEIGHT=5' - 2"; NOZZLE_HEIGHT/7*2=1' - 3 1/2"; NOZZLE_SIZE=24' - 0"; NOZZLE_TOP_OD=3' - 0 1/2"; NOZZLE_TOP_RAD=1' - 6 1/4"; NOZZLE_WB/4=1' - 0 3/16"; NOZZLE_WB_OD=5' - 1"; NOZZLE_WB_RAD=2' - 6 1/2"; NOZZLE_WB_RAD-2"=2' - 4 1/2"; RO=3' - 8 3/4"; RO/2=1' - 10 3/8"; RO2/2=1' - 10 3/8"; TRANSITION_TOP=6' - 5 1/4"; TRIPLE_F+1"=17' - 9"; TRIP_F=17' - 8"; TRIP_G=17' - 7 5/16"; TYPE=0' - 0"; Type Comments=Vari-Plume Laboratory Exhaust Mixed-Flow Inline Belt Drive With 1X3 Mixing Box; UNIT_HEIGHT=4' - 6"; UNIT_HEIGHT*.75=3' - 4 1/2"; UNIT_OD=3' - 6 1/2"; UNIT_RAD+((A/2)+.25")=3' - 11 1/2"; UNIT_RAD+((A/2)+.25")+4"=4' - 3 1/2"; UNIT_RADIUS=1' - 9 1/4"; UNIT_RADIUS*.6=1' - 7 1/8"; UNIT_RADIUS+4"=2' - 1 1/4"
- 300_QMXVP-30L-1X3_Mixing_Box: (A/2)+.25"=2' - 2 1/4"; (A/2)-2"=2' - 0"; (NOZZLE_HEIGHT-(NOZZLE_HEIGHT/8*2))/2=2' - 5 1/4"; (NOZZLE_WB_OD-NOZZLE_TOP_OD)/2=0' - 7 1/8"; -A=-4' - 4"; A=4' - 4"; A+.5=4' - 4 1/2"; A/2=2' - 2"; B=12' - 4"; B/2=6' - 2"; C=5' - 7"; C/2=2' - 9 1/2"; DUAL_F=11' - 0 1/4"; DUAL_F+1"=11' - 1 1/4"; DUAL_G=10' - 11 1/8"; E=4' - 2 15/16"; GA=0' - 0 3/32"; LONG_RO=17' - 1 1/16"; MB_A=5' - 8"; MB_HT=4' - 2 7/16"; MB_HT+.25"=4' - 2 11/16"; MB_HT-2.75"=3' - 11 11/16"; MB_HT/2=2' - 1 7/32"; Model=QMXVP-1X3_Mixing Box; NOZZLE_BOTTOM_ID=3' - 6 1/2"; NOZZLE_BOTTOM_RAD=1' - 9 1/4"; NOZZLE_HEIGHT=6' - 6"; NOZZLE_HEIGHT/7*2=1' - 7 1/2"; NOZZLE_SIZE=30' - 0"; NOZZLE_TOP_OD=3' - 9 1/2"; NOZZLE_TOP_RAD=1' - 10 3/4"; NOZZLE_WB/4=1' - 2 13/16"; NOZZLE_WB_OD=6' - 2"; NOZZLE_WB_RAD=3' - 1"; NOZZLE_WB_RAD-2"=2' - 11"; RO=3' - 8 3/4"; RO/2=1' - 10 3/8"; RO2/2=1' - 10 3/8"; TRANSITION_TOP=5' - 8 1/4"; TRIPLE_F+1"=17' - 9"; TRIP_F=17' - 8"; TRIP_G=17' - 7 5/16"; TYPE=0' - 0"; Type Comments=Vari-Plume Laboratory Exhaust Mixed-Flow Inline Belt Drive With 1X3 Mixing Box; UNIT_HEIGHT=4' - 6"; UNIT_HEIGHT*.75=3' - 4 1/2"; UNIT_OD=3' - 6 1/2"; UNIT_RAD+((A/2)+.25")=3' - 11 1/2"; UNIT_RAD+((A/2)+.25")+4"=4' - 3 1/2"; UNIT_RADIUS=1' - 9 1/4"; UNIT_RADIUS*.6=1' - 7 1/8"; UNIT_RADIUS+4"=2' - 1 1/4"
- 300_QMXVP-30H-1X3_Mixing_Box: (A/2)+.25"=2' - 2 1/4"; (A/2)-2"=2' - 0"; (NOZZLE_HEIGHT-(NOZZLE_HEIGHT/8*2))/2=2' - 5 1/4"; (NOZZLE_WB_OD-NOZZLE_TOP_OD)/2=0' - 7 1/8"; -A=-4' - 4"; A=4' - 4"; A+.5=4' - 4 1/2"; A/2=2' - 2"; B=12' - 4"; B/2=6' - 2"; C=5' - 7"; C/2=2' - 9 1/2"; DUAL_F=11' - 0 1/4"; DUAL_F+1"=11' - 1 1/4"; DUAL_G=10' - 11 1/8"; E=4' - 2 15/16"; GA=0' - 0 3/32"; LONG_RO=17' - 1 1/16"; MB_A=5' - 8"; MB_HT=4' - 2 7/16"; MB_HT+.25"=4' - 2 11/16"; MB_HT-2.75"=3' - 11 11/16"; MB_HT/2=2' - 1 7/32"; Model=QMXVP-1X3_Mixing Box; NOZZLE_BOTTOM_ID=3' - 6 1/2"; NOZZLE_BOTTOM_RAD=1' - 9 1/4"; NOZZLE_HEIGHT=6' - 6"; NOZZLE_HEIGHT/7*2=1' - 7 1/2"; NOZZLE_SIZE=30' - 0"; NOZZLE_TOP_OD=3' - 9 1/2"; NOZZLE_TOP_RAD=1' - 10 3/4"; NOZZLE_WB/4=1' - 2 13/16"; NOZZLE_WB_OD=6' - 2"; NOZZLE_WB_RAD=3' - 1"; NOZZLE_WB_RAD-2"=2' - 11"; RO=3' - 8 3/4"; RO/2=1' - 10 3/8"; RO2/2=1' - 10 3/8"; TRANSITION_TOP=5' - 8 1/4"; TRIPLE_F+1"=17' - 9"; TRIP_F=17' - 8"; TRIP_G=17' - 7 5/16"; TYPE=0' - 0"; Type Comments=Vari-Plume Laboratory Exhaust Mixed-Flow Inline Belt Drive With 1X3 Mixing Box; UNIT_HEIGHT=4' - 6"; UNIT_HEIGHT*.75=3' - 4 1/2"; UNIT_OD=3' - 6 1/2"; UNIT_RAD+((A/2)+.25")=3' - 11 1/2"; UNIT_RAD+((A/2)+.25")+4"=4' - 3 1/2"; UNIT_RADIUS=1' - 9 1/4"; UNIT_RADIUS*.6=1' - 7 1/8"; UNIT_RADIUS+4"=2' - 1 1/4"
- 330_QMXVP-24L-1X3_Mixing_Box: (A/2)+.25"=2' - 4 1/4"; (A/2)-2"=2' - 2"; (NOZZLE_HEIGHT-(NOZZLE_HEIGHT/8*2))/2=1' - 11 1/4"; (NOZZLE_WB_OD-NOZZLE_TOP_OD)/2=0' - 6 1/8"; -A=-4' - 8"; A=4' - 8"; A+.5=4' - 8 1/2"; A/2=2' - 4"; B=12' - 10"; B/2=6' - 5"; C=6' - 1"; C/2=3' - 0 1/2"; DUAL_F=11' - 4 1/4"; DUAL_F+1"=11' - 5 1/4"; DUAL_G=11' - 3 1/8"; E=4' - 6 13/16"; GA=0' - 0 3/32"; LONG_RO=17' - 5 1/16"; MB_A=6' - 1"; MB_HT=4' - 5 11/16"; MB_HT+.25"=4' - 5 15/16"; MB_HT-2.75"=4' - 2 15/16"; MB_HT/2=2' - 2 27/32"; Model=QMXVP-1X3_Mixing Box; NOZZLE_BOTTOM_ID=2' - 10 3/4"; NOZZLE_BOTTOM_RAD=1' - 5 3/8"; NOZZLE_HEIGHT=5' - 2"; NOZZLE_HEIGHT/7*2=1' - 3 1/2"; NOZZLE_SIZE=24' - 0"; NOZZLE_TOP_OD=3' - 0 1/2"; NOZZLE_TOP_RAD=1' - 6 1/4"; NOZZLE_WB/4=1' - 0 3/16"; NOZZLE_WB_OD=5' - 1"; NOZZLE_WB_RAD=2' - 6 1/2"; NOZZLE_WB_RAD-2"=2' - 4 1/2"; RO=4' - 0 5/8"; RO/2=2' - 0 5/16"; RO2/2=2' - 0 5/16"; TRANSITION_TOP=7' - 5 3/4"; TRIPLE_F+1"=18' - 1"; TRIP_F=18' - 0"; TRIP_G=17' - 11 5/16"; TYPE=0' - 0"; Type Comments=Vari-Plume Laboratory Exhaust Mixed-Flow Inline Belt Drive With 1X3 Mixing Box; UNIT_HEIGHT=4' - 10 1/2"; UNIT_HEIGHT*.75=3' - 7 7/8"; UNIT_OD=3' - 10 3/4"; UNIT_RAD+((A/2)+.25")=4' - 3 5/8"; UNIT_RAD+((A/2)+.25")+4"=4' - 7 5/8"; UNIT_RADIUS=1' - 11 3/8"; UNIT_RADIUS*.6=1' - 9 1/32"; UNIT_RADIUS+4"=2' - 3 3/8"
- 330_QMXVP-24H-1X3_Mixing_Box: (A/2)+.25"=2' - 4 1/4"; (A/2)-2"=2' - 2"; (NOZZLE_HEIGHT-(NOZZLE_HEIGHT/8*2))/2=1' - 11 1/4"; (NOZZLE_WB_OD-NOZZLE_TOP_OD)/2=0' - 6 1/8"; -A=-4' - 8"; A=4' - 8"; A+.5=4' - 8 1/2"; A/2=2' - 4"; B=12' - 10"; B/2=6' - 5"; C=6' - 1"; C/2=3' - 0 1/2"; DUAL_F=11' - 4 1/4"; DUAL_F+1"=11' - 5 1/4"; DUAL_G=11' - 3 1/8"; E=4' - 6 13/16"; GA=0' - 0 3/32"; LONG_RO=17' - 5 1/16"; MB_A=6' - 1"; MB_HT=4' - 5 11/16"; MB_HT+.25"=4' - 5 15/16"; MB_HT-2.75"=4' - 2 15/16"; MB_HT/2=2' - 2 27/32"; Model=QMXVP-1X3_Mixing Box; NOZZLE_BOTTOM_ID=2' - 10 3/4"; NOZZLE_BOTTOM_RAD=1' - 5 3/8"; NOZZLE_HEIGHT=5' - 2"; NOZZLE_HEIGHT/7*2=1' - 3 1/2"; NOZZLE_SIZE=24' - 0"; NOZZLE_TOP_OD=3' - 0 1/2"; NOZZLE_TOP_RAD=1' - 6 1/4"; NOZZLE_WB/4=1' - 0 3/16"; NOZZLE_WB_OD=5' - 1"; NOZZLE_WB_RAD=2' - 6 1/2"; NOZZLE_WB_RAD-2"=2' - 4 1/2"; RO=4' - 0 5/8"; RO/2=2' - 0 5/16"; RO2/2=2' - 0 5/16"; TRANSITION_TOP=7' - 5 3/4"; TRIPLE_F+1"=18' - 1"; TRIP_F=18' - 0"; TRIP_G=17' - 11 5/16"; TYPE=0' - 0"; Type Comments=Vari-Plume Laboratory Exhaust Mixed-Flow Inline Belt Drive With 1X3 Mixing Box; UNIT_HEIGHT=4' - 10 1/2"; UNIT_HEIGHT*.75=3' - 7 7/8"; UNIT_OD=3' - 10 3/4"; UNIT_RAD+((A/2)+.25")=4' - 3 5/8"; UNIT_RAD+((A/2)+.25")+4"=4' - 7 5/8"; UNIT_RADIUS=1' - 11 3/8"; UNIT_RADIUS*.6=1' - 9 1/32"; UNIT_RADIUS+4"=2' - 3 3/8"
- 330_QMXVP-30L-1X3_Mixing_Box: (A/2)+.25"=2' - 4 1/4"; (A/2)-2"=2' - 2"; (NOZZLE_HEIGHT-(NOZZLE_HEIGHT/8*2))/2=2' - 5 1/4"; (NOZZLE_WB_OD-NOZZLE_TOP_OD)/2=0' - 7 1/8"; -A=-4' - 8"; A=4' - 8"; A+.5=4' - 8 1/2"; A/2=2' - 4"; B=12' - 10"; B/2=6' - 5"; C=6' - 1"; C/2=3' - 0 1/2"; DUAL_F=11' - 4 1/4"; DUAL_F+1"=11' - 5 1/4"; DUAL_G=11' - 3 1/8"; E=4' - 6 13/16"; GA=0' - 0 3/32"; LONG_RO=17' - 5 1/16"; MB_A=6' - 1"; MB_HT=4' - 5 11/16"; MB_HT+.25"=4' - 5 15/16"; MB_HT-2.75"=4' - 2 15/16"; MB_HT/2=2' - 2 27/32"; Model=QMXVP-1X3_Mixing Box; NOZZLE_BOTTOM_ID=3' - 6 1/2"; NOZZLE_BOTTOM_RAD=1' - 9 1/4"; NOZZLE_HEIGHT=6' - 6"; NOZZLE_HEIGHT/7*2=1' - 7 1/2"; NOZZLE_SIZE=30' - 0"; NOZZLE_TOP_OD=3' - 9 1/2"; NOZZLE_TOP_RAD=1' - 10 3/4"; NOZZLE_WB/4=1' - 2 13/16"; NOZZLE_WB_OD=6' - 2"; NOZZLE_WB_RAD=3' - 1"; NOZZLE_WB_RAD-2"=2' - 11"; RO=4' - 0 5/8"; RO/2=2' - 0 5/16"; RO2/2=2' - 0 5/16"; TRANSITION_TOP=6' - 2 3/4"; TRIPLE_F+1"=18' - 1"; TRIP_F=18' - 0"; TRIP_G=17' - 11 5/16"; TYPE=0' - 0"; Type Comments=Vari-Plume Laboratory Exhaust Mixed-Flow Inline Belt Drive With 1X3 Mixing Box; UNIT_HEIGHT=4' - 10 1/2"; UNIT_HEIGHT*.75=3' - 7 7/8"; UNIT_OD=3' - 10 3/4"; UNIT_RAD+((A/2)+.25")=4' - 3 5/8"; UNIT_RAD+((A/2)+.25")+4"=4' - 7 5/8"; UNIT_RADIUS=1' - 11 3/8"; UNIT_RADIUS*.6=1' - 9 1/32"; UNIT_RADIUS+4"=2' - 3 3/8"
- 330_QMXVP-30H-1X3_Mixing_Box: (A/2)+.25"=2' - 4 1/4"; (A/2)-2"=2' - 2"; (NOZZLE_HEIGHT-(NOZZLE_HEIGHT/8*2))/2=2' - 5 1/4"; (NOZZLE_WB_OD-NOZZLE_TOP_OD)/2=0' - 7 1/8"; -A=-4' - 8"; A=4' - 8"; A+.5=4' - 8 1/2"; A/2=2' - 4"; B=12' - 10"; B/2=6' - 5"; C=6' - 1"; C/2=3' - 0 1/2"; DUAL_F=11' - 4 1/4"; DUAL_F+1"=11' - 5 1/4"; DUAL_G=11' - 3 1/8"; E=4' - 6 13/16"; GA=0' - 0 3/32"; LONG_RO=17' - 5 1/16"; MB_A=6' - 1"; MB_HT=4' - 5 11/16"; MB_HT+.25"=4' - 5 15/16"; MB_HT-2.75"=4' - 2 15/16"; MB_HT/2=2' - 2 27/32"; Model=QMXVP-1X3_Mixing Box; NOZZLE_BOTTOM_ID=3' - 6 1/2"; NOZZLE_BOTTOM_RAD=1' - 9 1/4"; NOZZLE_HEIGHT=6' - 6"; NOZZLE_HEIGHT/7*2=1' - 7 1/2"; NOZZLE_SIZE=30' - 0"; NOZZLE_TOP_OD=3' - 9 1/2"; NOZZLE_TOP_RAD=1' - 10 3/4"; NOZZLE_WB/4=1' - 2 13/16"; NOZZLE_WB_OD=6' - 2"; NOZZLE_WB_RAD=3' - 1"; NOZZLE_WB_RAD-2"=2' - 11"; RO=4' - 0 5/8"; RO/2=2' - 0 5/16"; RO2/2=2' - 0 5/16"; TRANSITION_TOP=6' - 2 3/4"; TRIPLE_F+1"=18' - 1"; TRIP_F=18' - 0"; TRIP_G=17' - 11 5/16"; TYPE=0' - 0"; Type Comments=Vari-Plume Laboratory Exhaust Mixed-Flow Inline Belt Drive With 1X3 Mixing Box; UNIT_HEIGHT=4' - 10 1/2"; UNIT_HEIGHT*.75=3' - 7 7/8"; UNIT_OD=3' - 10 3/4"; UNIT_RAD+((A/2)+.25")=4' - 3 5/8"; UNIT_RAD+((A/2)+.25")+4"=4' - 7 5/8"; UNIT_RADIUS=1' - 11 3/8"; UNIT_RADIUS*.6=1' - 9 1/32"; UNIT_RADIUS+4"=2' - 3 3/8"
- 365_QMXVP-24L-1X3_Mixing_Box: (A/2)+.25"=2' - 7 1/4"; (A/2)-2"=2' - 5"; (NOZZLE_HEIGHT-(NOZZLE_HEIGHT/8*2))/2=1' - 11 1/4"; (NOZZLE_WB_OD-NOZZLE_TOP_OD)/2=0' - 6 1/8"; -A=-5' - 2"; A=5' - 2"; A+.5=5' - 2 1/2"; A/2=2' - 7"; B=14' - 7"; B/2=7' - 3 1/2"; C=6' - 7"; C/2=3' - 3 1/2"; DUAL_F=13' - 3 3/4"; DUAL_F+1"=13' - 4 3/4"; DUAL_G=13' - 2"; E=5' - 0 3/4"; GA=0' - 0 3/32"; LONG_RO=20' - 9"; MB_A=6' - 10"; MB_HT=4' - 11 11/16"; MB_HT+.25"=4' - 11 15/16"; MB_HT-2.75"=4' - 8 15/16"; MB_HT/2=2' - 5 27/32"; Model=QMXVP-1X3_Mixing Box; NOZZLE_BOTTOM_ID=2' - 10 3/4"; NOZZLE_BOTTOM_RAD=1' - 5 3/8"; NOZZLE_HEIGHT=5' - 2"; NOZZLE_HEIGHT/7*2=1' - 3 1/2"; NOZZLE_SIZE=24' - 0"; NOZZLE_TOP_OD=3' - 0 1/2"; NOZZLE_TOP_RAD=1' - 6 1/4"; NOZZLE_WB/4=1' - 0 3/16"; NOZZLE_WB_OD=5' - 1"; NOZZLE_WB_RAD=2' - 6 1/2"; NOZZLE_WB_RAD-2"=2' - 4 1/2"; RO=4' - 6 1/2"; RO/2=2' - 3 1/4"; RO2/2=2' - 3 1/4"; TRANSITION_TOP=8' - 8 1/4"; TRIPLE_F+1"=21' - 6"; TRIP_F=21' - 5"; TRIP_G=21' - 3 1/4"; TYPE=0' - 0"; Type Comments=Vari-Plume Laboratory Exhaust Mixed-Flow Inline Belt Drive With 1X3 Mixing Box; UNIT_HEIGHT=5' - 4"; UNIT_HEIGHT*.75=4' - 0"; UNIT_OD=4' - 3 3/4"; UNIT_RAD+((A/2)+.25")=4' - 9 1/8"; UNIT_RAD+((A/2)+.25")+4"=5' - 1 1/8"; UNIT_RADIUS=2' - 1 7/8"; UNIT_RADIUS*.6=1' - 11 9/32"; UNIT_RADIUS+4"=2' - 5 7/8"
- 365_QMXVP-24H-1X3_Mixing_Box: (A/2)+.25"=2' - 7 1/4"; (A/2)-2"=2' - 5"; (NOZZLE_HEIGHT-(NOZZLE_HEIGHT/8*2))/2=1' - 11 1/4"; (NOZZLE_WB_OD-NOZZLE_TOP_OD)/2=0' - 6 1/8"; -A=-5' - 2"; A=5' - 2"; A+.5=5' - 2 1/2"; A/2=2' - 7"; B=14' - 7"; B/2=7' - 3 1/2"; C=6' - 7"; C/2=3' - 3 1/2"; DUAL_F=13' - 3 3/4"; DUAL_F+1"=13' - 4 3/4"; DUAL_G=13' - 2"; E=5' - 0 3/4"; GA=0' - 0 3/32"; LONG_RO=20' - 9"; MB_A=6' - 10"; MB_HT=4' - 11 11/16"; MB_HT+.25"=4' - 11 15/16"; MB_HT-2.75"=4' - 8 15/16"; MB_HT/2=2' - 5 27/32"; Model=QMXVP-1X3_Mixing Box; NOZZLE_BOTTOM_ID=2' - 10 3/4"; NOZZLE_BOTTOM_RAD=1' - 5 3/8"; NOZZLE_HEIGHT=5' - 2"; NOZZLE_HEIGHT/7*2=1' - 3 1/2"; NOZZLE_SIZE=24' - 0"; NOZZLE_TOP_OD=3' - 0 1/2"; NOZZLE_TOP_RAD=1' - 6 1/4"; NOZZLE_WB/4=1' - 0 3/16"; NOZZLE_WB_OD=5' - 1"; NOZZLE_WB_RAD=2' - 6 1/2"; NOZZLE_WB_RAD-2"=2' - 4 1/2"; RO=4' - 6 1/2"; RO/2=2' - 3 1/4"; RO2/2=2' - 3 1/4"; TRANSITION_TOP=8' - 8 1/4"; TRIPLE_F+1"=21' - 6"; TRIP_F=21' - 5"; TRIP_G=21' - 3 1/4"; TYPE=0' - 0"; Type Comments=Vari-Plume Laboratory Exhaust Mixed-Flow Inline Belt Drive With 1X3 Mixing Box; UNIT_HEIGHT=5' - 4"; UNIT_HEIGHT*.75=4' - 0"; UNIT_OD=4' - 3 3/4"; UNIT_RAD+((A/2)+.25")=4' - 9 1/8"; UNIT_RAD+((A/2)+.25")+4"=5' - 1 1/8"; UNIT_RADIUS=2' - 1 7/8"; UNIT_RADIUS*.6=1' - 11 9/32"; UNIT_RADIUS+4"=2' - 5 7/8"
- 365_QMXVP-30L-1X3_Mixing_Box: (A/2)+.25"=2' - 7 1/4"; (A/2)-2"=2' - 5"; (NOZZLE_HEIGHT-(NOZZLE_HEIGHT/8*2))/2=2' - 5 1/4"; (NOZZLE_WB_OD-NOZZLE_TOP_OD)/2=0' - 7 1/8"; -A=-5' - 2"; A=5' - 2"; A+.5=5' - 2 1/2"; A/2=2' - 7"; B=14' - 7"; B/2=7' - 3 1/2"; C=6' - 7"; C/2=3' - 3 1/2"; DUAL_F=13' - 3 3/4"; DUAL_F+1"=13' - 4 3/4"; DUAL_G=13' - 2"; E=5' - 0 3/4"; GA=0' - 0 3/32"; LONG_RO=20' - 9"; MB_A=6' - 10"; MB_HT=4' - 11 11/16"; MB_HT+.25"=4' - 11 15/16"; MB_HT-2.75"=4' - 8 15/16"; MB_HT/2=2' - 5 27/32"; Model=QMXVP-1X3_Mixing Box; NOZZLE_BOTTOM_ID=3' - 6 1/2"; NOZZLE_BOTTOM_RAD=1' - 9 1/4"; NOZZLE_HEIGHT=6' - 6"; NOZZLE_HEIGHT/7*2=1' - 7 1/2"; NOZZLE_SIZE=30' - 0"; NOZZLE_TOP_OD=3' - 9 1/2"; NOZZLE_TOP_RAD=1' - 10 3/4"; NOZZLE_WB/4=1' - 2 13/16"; NOZZLE_WB_OD=6' - 2"; NOZZLE_WB_RAD=3' - 1"; NOZZLE_WB_RAD-2"=2' - 11"; RO=4' - 6 1/2"; RO/2=2' - 3 1/4"; RO2/2=2' - 3 1/4"; TRANSITION_TOP=7' - 5 1/2"; TRIPLE_F+1"=21' - 6"; TRIP_F=21' - 5"; TRIP_G=21' - 3 1/4"; TYPE=0' - 0"; Type Comments=Vari-Plume Laboratory Exhaust Mixed-Flow Inline Belt Drive With 1X3 Mixing Box; UNIT_HEIGHT=5' - 4"; UNIT_HEIGHT*.75=4' - 0"; UNIT_OD=4' - 3 3/4"; UNIT_RAD+((A/2)+.25")=4' - 9 1/8"; UNIT_RAD+((A/2)+.25")+4"=5' - 1 1/8"; UNIT_RADIUS=2' - 1 7/8"; UNIT_RADIUS*.6=1' - 11 9/32"; UNIT_RADIUS+4"=2' - 5 7/8"
- 365_QMXVP-30H-1X3_Mixing_Box: (A/2)+.25"=2' - 7 1/4"; (A/2)-2"=2' - 5"; (NOZZLE_HEIGHT-(NOZZLE_HEIGHT/8*2))/2=2' - 5 1/4"; (NOZZLE_WB_OD-NOZZLE_TOP_OD)/2=0' - 7 1/8"; -A=-5' - 2"; A=5' - 2"; A+.5=5' - 2 1/2"; A/2=2' - 7"; B=14' - 7"; B/2=7' - 3 1/2"; C=6' - 7"; C/2=3' - 3 1/2"; DUAL_F=13' - 3 3/4"; DUAL_F+1"=13' - 4 3/4"; DUAL_G=13' - 2"; E=5' - 0 3/4"; GA=0' - 0 3/32"; LONG_RO=20' - 9"; MB_A=6' - 10"; MB_HT=4' - 11 11/16"; MB_HT+.25"=4' - 11 15/16"; MB_HT-2.75"=4' - 8 15/16"; MB_HT/2=2' - 5 27/32"; Model=QMXVP-1X3_Mixing Box; NOZZLE_BOTTOM_ID=3' - 6 1/2"; NOZZLE_BOTTOM_RAD=1' - 9 1/4"; NOZZLE_HEIGHT=6' - 6"; NOZZLE_HEIGHT/7*2=1' - 7 1/2"; NOZZLE_SIZE=30' - 0"; NOZZLE_TOP_OD=3' - 9 1/2"; NOZZLE_TOP_RAD=1' - 10 3/4"; NOZZLE_WB/4=1' - 2 13/16"; NOZZLE_WB_OD=6' - 2"; NOZZLE_WB_RAD=3' - 1"; NOZZLE_WB_RAD-2"=2' - 11"; RO=4' - 6 1/2"; RO/2=2' - 3 1/4"; RO2/2=2' - 3 1/4"; TRANSITION_TOP=7' - 5 1/2"; TRIPLE_F+1"=21' - 6"; TRIP_F=21' - 5"; TRIP_G=21' - 3 1/4"; TYPE=0' - 0"; Type Comments=Vari-Plume Laboratory Exhaust Mixed-Flow Inline Belt Drive With 1X3 Mixing Box; UNIT_HEIGHT=5' - 4"; UNIT_HEIGHT*.75=4' - 0"; UNIT_OD=4' - 3 3/4"; UNIT_RAD+((A/2)+.25")=4' - 9 1/8"; UNIT_RAD+((A/2)+.25")+4"=5' - 1 1/8"; UNIT_RADIUS=2' - 1 7/8"; UNIT_RADIUS*.6=1' - 11 9/32"; UNIT_RADIUS+4"=2' - 5 7/8"
- 365_QMXVP-36L-1X3_Mixing_Box: (A/2)+.25"=2' - 7 1/4"; (A/2)-2"=2' - 5"; (NOZZLE_HEIGHT-(NOZZLE_HEIGHT/8*2))/2=2' - 11 5/8"; (NOZZLE_WB_OD-NOZZLE_TOP_OD)/2=0' - 8"; -A=-5' - 2"; A=5' - 2"; A+.5=5' - 2 1/2"; A/2=2' - 7"; B=14' - 7"; B/2=7' - 3 1/2"; C=6' - 7"; C/2=3' - 3 1/2"; DUAL_F=13' - 3 3/4"; DUAL_F+1"=13' - 4 3/4"; DUAL_G=13' - 2"; E=5' - 0 3/4"; GA=0' - 0 3/32"; LONG_RO=20' - 9"; MB_A=6' - 10"; MB_HT=4' - 11 11/16"; MB_HT+.25"=4' - 11 15/16"; MB_HT-2.75"=4' - 8 15/16"; MB_HT/2=2' - 5 27/32"; Model=QMXVP-1X3_Mixing Box; NOZZLE_BOTTOM_ID=4' - 3 3/4"; NOZZLE_BOTTOM_RAD=2' - 1 7/8"; NOZZLE_HEIGHT=7' - 11"; NOZZLE_HEIGHT/7*2=1' - 11 3/4"; NOZZLE_SIZE=36' - 0"; NOZZLE_TOP_OD=4' - 10"; NOZZLE_TOP_RAD=2' - 5"; NOZZLE_WB/4=1' - 6"; NOZZLE_WB_OD=7' - 6"; NOZZLE_WB_RAD=3' - 9"; NOZZLE_WB_RAD-2"=3' - 7"; RO=4' - 6 1/2"; RO/2=2' - 3 1/4"; RO2/2=2' - 3 1/4"; TRANSITION_TOP=6' - 6 1/4"; TRIPLE_F+1"=21' - 6"; TRIP_F=21' - 5"; TRIP_G=21' - 3 1/4"; TYPE=0' - 0"; Type Comments=Vari-Plume Laboratory Exhaust Mixed-Flow Inline Belt Drive With 1X3 Mixing Box; UNIT_HEIGHT=5' - 4"; UNIT_HEIGHT*.75=4' - 0"; UNIT_OD=4' - 3 3/4"; UNIT_RAD+((A/2)+.25")=4' - 9 1/8"; UNIT_RAD+((A/2)+.25")+4"=5' - 1 1/8"; UNIT_RADIUS=2' - 1 7/8"; UNIT_RADIUS*.6=1' - 11 9/32"; UNIT_RADIUS+4"=2' - 5 7/8"
- 402_QMXVP-24L-1X3_Mixing_Box: (A/2)+.25"=2' - 9 3/4"; (A/2)-2"=2' - 7 1/2"; (NOZZLE_HEIGHT-(NOZZLE_HEIGHT/8*2))/2=1' - 11 1/4"; (NOZZLE_WB_OD-NOZZLE_TOP_OD)/2=0' - 6 1/8"; -A=-5' - 7"; A=5' - 7"; A+.5=5' - 7 1/2"; A/2=2' - 9 1/2"; B=15' - 3"; B/2=7' - 7 1/2"; C=7' - 4"; C/2=3' - 8"; DUAL_F=13' - 8 3/4"; DUAL_F+1"=13' - 9 3/4"; DUAL_G=13' - 7"; E=5' - 5 3/4"; GA=0' - 0 3/32"; LONG_RO=21' - 2 1/8"; MB_A=7' - 6"; MB_HT=5' - 5 15/16"; MB_HT+.25"=5' - 6 3/16"; MB_HT-2.75"=5' - 3 3/16"; MB_HT/2=2' - 8 31/32"; Model=QMXVP-1X3_Mixing Box; NOZZLE_BOTTOM_ID=2' - 10 3/4"; NOZZLE_BOTTOM_RAD=1' - 5 3/8"; NOZZLE_HEIGHT=5' - 2"; NOZZLE_HEIGHT/7*2=1' - 3 1/2"; NOZZLE_SIZE=24' - 0"; NOZZLE_TOP_OD=3' - 0 1/2"; NOZZLE_TOP_RAD=1' - 6 1/4"; NOZZLE_WB/4=1' - 0 3/16"; NOZZLE_WB_OD=5' - 1"; NOZZLE_WB_RAD=2' - 6 1/2"; NOZZLE_WB_RAD-2"=2' - 4 1/2"; RO=4' - 11 7/16"; RO/2=2' - 5 23/32"; RO2/2=2' - 5 23/32"; TRANSITION_TOP=9' - 10 3/4"; TRIPLE_F+1"=21' - 11"; TRIP_F=21' - 10"; TRIP_G=21' - 8 3/8"; TYPE=0' - 0"; Type Comments=Vari-Plume Laboratory Exhaust Mixed-Flow Inline Belt Drive With 1X3 Mixing Box; UNIT_HEIGHT=5' - 8 1/2"; UNIT_HEIGHT*.75=4' - 3 3/8"; UNIT_OD=4' - 8 15/16"; UNIT_RAD+((A/2)+.25")=5' - 2 7/32"; UNIT_RAD+((A/2)+.25")+4"=5' - 6 7/32"; UNIT_RADIUS=2' - 4 15/32"; UNIT_RADIUS*.6=2' - 1 5/8"; UNIT_RADIUS+4"=2' - 8 15/32"
- 402_QMXVP-24H-1X3_Mixing_Box: (A/2)+.25"=2' - 9 3/4"; (A/2)-2"=2' - 7 1/2"; (NOZZLE_HEIGHT-(NOZZLE_HEIGHT/8*2))/2=1' - 11 1/4"; (NOZZLE_WB_OD-NOZZLE_TOP_OD)/2=0' - 6 1/8"; -A=-5' - 7"; A=5' - 7"; A+.5=5' - 7 1/2"; A/2=2' - 9 1/2"; B=15' - 3"; B/2=7' - 7 1/2"; C=7' - 4"; C/2=3' - 8"; DUAL_F=13' - 8 3/4"; DUAL_F+1"=13' - 9 3/4"; DUAL_G=13' - 7"; E=5' - 5 3/4"; GA=0' - 0 3/32"; LONG_RO=21' - 2 1/8"; MB_A=7' - 6"; MB_HT=5' - 5 15/16"; MB_HT+.25"=5' - 6 3/16"; MB_HT-2.75"=5' - 3 3/16"; MB_HT/2=2' - 8 31/32"; Model=QMXVP-1X3_Mixing Box; NOZZLE_BOTTOM_ID=2' - 10 3/4"; NOZZLE_BOTTOM_RAD=1' - 5 3/8"; NOZZLE_HEIGHT=5' - 2"; NOZZLE_HEIGHT/7*2=1' - 3 1/2"; NOZZLE_SIZE=24' - 0"; NOZZLE_TOP_OD=3' - 0 1/2"; NOZZLE_TOP_RAD=1' - 6 1/4"; NOZZLE_WB/4=1' - 0 3/16"; NOZZLE_WB_OD=5' - 1"; NOZZLE_WB_RAD=2' - 6 1/2"; NOZZLE_WB_RAD-2"=2' - 4 1/2"; RO=4' - 11 7/16"; RO/2=2' - 5 23/32"; RO2/2=2' - 5 23/32"; TRANSITION_TOP=9' - 10 3/4"; TRIPLE_F+1"=21' - 11"; TRIP_F=21' - 10"; TRIP_G=21' - 8 3/8"; TYPE=0' - 0"; Type Comments=Vari-Plume Laboratory Exhaust Mixed-Flow Inline Belt Drive With 1X3 Mixing Box; UNIT_HEIGHT=5' - 8 1/2"; UNIT_HEIGHT*.75=4' - 3 3/8"; UNIT_OD=4' - 8 15/16"; UNIT_RAD+((A/2)+.25")=5' - 2 7/32"; UNIT_RAD+((A/2)+.25")+4"=5' - 6 7/32"; UNIT_RADIUS=2' - 4 15/32"; UNIT_RADIUS*.6=2' - 1 5/8"; UNIT_RADIUS+4"=2' - 8 15/32"
- 402_QMXVP-30L-1X3_Mixing_Box: (A/2)+.25"=2' - 9 3/4"; (A/2)-2"=2' - 7 1/2"; (NOZZLE_HEIGHT-(NOZZLE_HEIGHT/8*2))/2=2' - 5 1/4"; (NOZZLE_WB_OD-NOZZLE_TOP_OD)/2=0' - 7 1/8"; -A=-5' - 7"; A=5' - 7"; A+.5=5' - 7 1/2"; A/2=2' - 9 1/2"; B=15' - 3"; B/2=7' - 7 1/2"; C=7' - 4"; C/2=3' - 8"; DUAL_F=13' - 8 3/4"; DUAL_F+1"=13' - 9 3/4"; DUAL_G=13' - 7"; E=5' - 5 3/4"; GA=0' - 0 3/32"; LONG_RO=21' - 2 1/8"; MB_A=7' - 6"; MB_HT=5' - 5 15/16"; MB_HT+.25"=5' - 6 3/16"; MB_HT-2.75"=5' - 3 3/16"; MB_HT/2=2' - 8 31/32"; Model=QMXVP-1X3_Mixing Box; NOZZLE_BOTTOM_ID=3' - 6 1/2"; NOZZLE_BOTTOM_RAD=1' - 9 1/4"; NOZZLE_HEIGHT=6' - 6"; NOZZLE_HEIGHT/7*2=1' - 7 1/2"; NOZZLE_SIZE=30' - 0"; NOZZLE_TOP_OD=3' - 9 1/2"; NOZZLE_TOP_RAD=1' - 10 3/4"; NOZZLE_WB/4=1' - 2 13/16"; NOZZLE_WB_OD=6' - 2"; NOZZLE_WB_RAD=3' - 1"; NOZZLE_WB_RAD-2"=2' - 11"; RO=4' - 11 7/16"; RO/2=2' - 5 23/32"; RO2/2=2' - 5 23/32"; TRANSITION_TOP=8' - 7 3/4"; TRIPLE_F+1"=21' - 11"; TRIP_F=21' - 10"; TRIP_G=21' - 8 3/8"; TYPE=0' - 0"; Type Comments=Vari-Plume Laboratory Exhaust Mixed-Flow Inline Belt Drive With 1X3 Mixing Box; UNIT_HEIGHT=5' - 8 1/2"; UNIT_HEIGHT*.75=4' - 3 3/8"; UNIT_OD=4' - 8 15/16"; UNIT_RAD+((A/2)+.25")=5' - 2 7/32"; UNIT_RAD+((A/2)+.25")+4"=5' - 6 7/32"; UNIT_RADIUS=2' - 4 15/32"; UNIT_RADIUS*.6=2' - 1 5/8"; UNIT_RADIUS+4"=2' - 8 15/32"
- 402_QMXVP-30H-1X3_Mixing_Box: (A/2)+.25"=2' - 9 3/4"; (A/2)-2"=2' - 7 1/2"; (NOZZLE_HEIGHT-(NOZZLE_HEIGHT/8*2))/2=2' - 5 1/4"; (NOZZLE_WB_OD-NOZZLE_TOP_OD)/2=0' - 7 1/8"; -A=-5' - 7"; A=5' - 7"; A+.5=5' - 7 1/2"; A/2=2' - 9 1/2"; B=15' - 3"; B/2=7' - 7 1/2"; C=7' - 4"; C/2=3' - 8"; DUAL_F=13' - 8 3/4"; DUAL_F+1"=13' - 9 3/4"; DUAL_G=13' - 7"; E=5' - 5 3/4"; GA=0' - 0 3/32"; LONG_RO=21' - 2 1/8"; MB_A=7' - 6"; MB_HT=5' - 5 15/16"; MB_HT+.25"=5' - 6 3/16"; MB_HT-2.75"=5' - 3 3/16"; MB_HT/2=2' - 8 31/32"; Model=QMXVP-1X3_Mixing Box; NOZZLE_BOTTOM_ID=3' - 6 1/2"; NOZZLE_BOTTOM_RAD=1' - 9 1/4"; NOZZLE_HEIGHT=6' - 6"; NOZZLE_HEIGHT/7*2=1' - 7 1/2"; NOZZLE_SIZE=30' - 0"; NOZZLE_TOP_OD=3' - 9 1/2"; NOZZLE_TOP_RAD=1' - 10 3/4"; NOZZLE_WB/4=1' - 2 13/16"; NOZZLE_WB_OD=6' - 2"; NOZZLE_WB_RAD=3' - 1"; NOZZLE_WB_RAD-2"=2' - 11"; RO=4' - 11 7/16"; RO/2=2' - 5 23/32"; RO2/2=2' - 5 23/32"; TRANSITION_TOP=8' - 7 3/4"; TRIPLE_F+1"=21' - 11"; TRIP_F=21' - 10"; TRIP_G=21' - 8 3/8"; TYPE=0' - 0"; Type Comments=Vari-Plume Laboratory Exhaust Mixed-Flow Inline Belt Drive With 1X3 Mixing Box; UNIT_HEIGHT=5' - 8 1/2"; UNIT_HEIGHT*.75=4' - 3 3/8"; UNIT_OD=4' - 8 15/16"; UNIT_RAD+((A/2)+.25")=5' - 2 7/32"; UNIT_RAD+((A/2)+.25")+4"=5' - 6 7/32"; UNIT_RADIUS=2' - 4 15/32"; UNIT_RADIUS*.6=2' - 1 5/8"; UNIT_RADIUS+4"=2' - 8 15/32"
- 402_QMXVP-36L-1X3_Mixing_Box: (A/2)+.25"=2' - 9 3/4"; (A/2)-2"=2' - 7 1/2"; (NOZZLE_HEIGHT-(NOZZLE_HEIGHT/8*2))/2=2' - 11 5/8"; (NOZZLE_WB_OD-NOZZLE_TOP_OD)/2=0' - 8"; -A=-5' - 7"; A=5' - 7"; A+.5=5' - 7 1/2"; A/2=2' - 9 1/2"; B=15' - 3"; B/2=7' - 7 1/2"; C=7' - 4"; C/2=3' - 8"; DUAL_F=13' - 8 3/4"; DUAL_F+1"=13' - 9 3/4"; DUAL_G=13' - 7"; E=5' - 5 3/4"; GA=0' - 0 3/32"; LONG_RO=21' - 2 1/8"; MB_A=7' - 6"; MB_HT=5' - 5 15/16"; MB_HT+.25"=5' - 6 3/16"; MB_HT-2.75"=5' - 3 3/16"; MB_HT/2=2' - 8 31/32"; Model=QMXVP-1X3_Mixing Box; NOZZLE_BOTTOM_ID=4' - 3 3/4"; NOZZLE_BOTTOM_RAD=2' - 1 7/8"; NOZZLE_HEIGHT=7' - 11"; NOZZLE_HEIGHT/7*2=1' - 11 3/4"; NOZZLE_SIZE=36' - 0"; NOZZLE_TOP_OD=4' - 10"; NOZZLE_TOP_RAD=2' - 5"; NOZZLE_WB/4=1' - 6"; NOZZLE_WB_OD=7' - 6"; NOZZLE_WB_RAD=3' - 9"; NOZZLE_WB_RAD-2"=3' - 7"; RO=4' - 11 7/16"; RO/2=2' - 5 23/32"; RO2/2=2' - 5 23/32"; TRANSITION_TOP=7' - 2 3/4"; TRIPLE_F+1"=21' - 11"; TRIP_F=21' - 10"; TRIP_G=21' - 8 3/8"; TYPE=0' - 0"; Type Comments=Vari-Plume Laboratory Exhaust Mixed-Flow Inline Belt Drive With 1X3 Mixing Box; UNIT_HEIGHT=5' - 8 1/2"; UNIT_HEIGHT*.75=4' - 3 3/8"; UNIT_OD=4' - 8 15/16"; UNIT_RAD+((A/2)+.25")=5' - 2 7/32"; UNIT_RAD+((A/2)+.25")+4"=5' - 6 7/32"; UNIT_RADIUS=2' - 4 15/32"; UNIT_RADIUS*.6=2' - 1 5/8"; UNIT_RADIUS+4"=2' - 8 15/32"
- 402_QMXVP-36H-1X3_Mixing_Box: (A/2)+.25"=2' - 9 3/4"; (A/2)-2"=2' - 7 1/2"; (NOZZLE_HEIGHT-(NOZZLE_HEIGHT/8*2))/2=2' - 11 5/8"; (NOZZLE_WB_OD-NOZZLE_TOP_OD)/2=0' - 8"; -A=-5' - 7"; A=5' - 7"; A+.5=5' - 7 1/2"; A/2=2' - 9 1/2"; B=15' - 3"; B/2=7' - 7 1/2"; C=7' - 4"; C/2=3' - 8"; DUAL_F=13' - 8 3/4"; DUAL_F+1"=13' - 9 3/4"; DUAL_G=13' - 7"; E=5' - 5 3/4"; GA=0' - 0 3/32"; LONG_RO=21' - 2 1/8"; MB_A=7' - 6"; MB_HT=5' - 5 15/16"; MB_HT+.25"=5' - 6 3/16"; MB_HT-2.75"=5' - 3 3/16"; MB_HT/2=2' - 8 31/32"; Model=QMXVP-1X3_Mixing Box; NOZZLE_BOTTOM_ID=4' - 3 3/4"; NOZZLE_BOTTOM_RAD=2' - 1 7/8"; NOZZLE_HEIGHT=7' - 11"; NOZZLE_HEIGHT/7*2=1' - 11 3/4"; NOZZLE_SIZE=36' - 0"; NOZZLE_TOP_OD=4' - 10"; NOZZLE_TOP_RAD=2' - 5"; NOZZLE_WB/4=1' - 6"; NOZZLE_WB_OD=7' - 6"; NOZZLE_WB_RAD=3' - 9"; NOZZLE_WB_RAD-2"=3' - 7"; RO=4' - 11 7/16"; RO/2=2' - 5 23/32"; RO2/2=2' - 5 23/32"; TRANSITION_TOP=7' - 2 3/4"; TRIPLE_F+1"=21' - 11"; TRIP_F=21' - 10"; TRIP_G=21' - 8 3/8"; TYPE=0' - 0"; Type Comments=Vari-Plume Laboratory Exhaust Mixed-Flow Inline Belt Drive With 1X3 Mixing Box; UNIT_HEIGHT=5' - 8 1/2"; UNIT_HEIGHT*.75=4' - 3 3/8"; UNIT_OD=4' - 8 15/16"; UNIT_RAD+((A/2)+.25")=5' - 2 7/32"; UNIT_RAD+((A/2)+.25")+4"=5' - 6 7/32"; UNIT_RADIUS=2' - 4 15/32"; UNIT_RADIUS*.6=2' - 1 5/8"; UNIT_RADIUS+4"=2' - 8 15/32"
- 445_QMXVP-30L-1X3_Mixing_Box: (A/2)+.25"=3' - 1 1/4"; (A/2)-2"=2' - 11"; (NOZZLE_HEIGHT-(NOZZLE_HEIGHT/8*2))/2=2' - 5 1/4"; (NOZZLE_WB_OD-NOZZLE_TOP_OD)/2=0' - 7 1/8"; -A=-6' - 2"; A=6' - 2"; A+.5=6' - 2 1/2"; A/2=3' - 1"; B=16' - 9"; B/2=8' - 4 1/2"; C=7' - 11"; C/2=3' - 11 1/2"; DUAL_F=14' - 3 3/4"; DUAL_F+1"=14' - 4 3/4"; DUAL_G=14' - 2"; E=6' - 0 5/8"; GA=0' - 0 3/32"; LONG_RO=21' - 9 1/8"; MB_A=8' - 6"; MB_HT=6' - 3 11/16"; MB_HT+.25"=6' - 3 15/16"; MB_HT-2.75"=6' - 0 15/16"; MB_HT/2=3' - 1 27/32"; Model=QMXVP-1X3_Mixing Box; NOZZLE_BOTTOM_ID=3' - 6 1/2"; NOZZLE_BOTTOM_RAD=1' - 9 1/4"; NOZZLE_HEIGHT=6' - 6"; NOZZLE_HEIGHT/7*2=1' - 7 1/2"; NOZZLE_SIZE=30' - 0"; NOZZLE_TOP_OD=3' - 9 1/2"; NOZZLE_TOP_RAD=1' - 10 3/4"; NOZZLE_WB/4=1' - 2 13/16"; NOZZLE_WB_OD=6' - 2"; NOZZLE_WB_RAD=3' - 1"; NOZZLE_WB_RAD-2"=2' - 11"; RO=5' - 6 7/16"; RO/2=2' - 9 7/32"; RO2/2=2' - 9 7/32"; TRANSITION_TOP=10' - 1 1/4"; TRIPLE_F+1"=22' - 6"; TRIP_F=22' - 5"; TRIP_G=22' - 3 3/8"; TYPE=0' - 0"; Type Comments=Vari-Plume Laboratory Exhaust Mixed-Flow Inline Belt Drive With 1X3 Mixing Box; UNIT_HEIGHT=6' - 2"; UNIT_HEIGHT*.75=4' - 7 1/2"; UNIT_OD=5' - 3 1/16"; UNIT_RAD+((A/2)+.25")=5' - 8 25/32"; UNIT_RAD+((A/2)+.25")+4"=6' - 0 25/32"; UNIT_RADIUS=2' - 7 17/32"; UNIT_RADIUS*.6=2' - 4 3/8"; UNIT_RADIUS+4"=2' - 11 17/32"
- 445_QMXVP-30H-1X3_Mixing_Box: (A/2)+.25"=3' - 1 1/4"; (A/2)-2"=2' - 11"; (NOZZLE_HEIGHT-(NOZZLE_HEIGHT/8*2))/2=2' - 5 1/4"; (NOZZLE_WB_OD-NOZZLE_TOP_OD)/2=0' - 7 1/8"; -A=-6' - 2"; A=6' - 2"; A+.5=6' - 2 1/2"; A/2=3' - 1"; B=16' - 9"; B/2=8' - 4 1/2"; C=7' - 11"; C/2=3' - 11 1/2"; DUAL_F=14' - 3 3/4"; DUAL_F+1"=14' - 4 3/4"; DUAL_G=14' - 2"; E=6' - 0 5/8"; GA=0' - 0 3/32"; LONG_RO=21' - 9 1/8"; MB_A=8' - 6"; MB_HT=6' - 3 11/16"; MB_HT+.25"=6' - 3 15/16"; MB_HT-2.75"=6' - 0 15/16"; MB_HT/2=3' - 1 27/32"; Model=QMXVP-1X3_Mixing Box; NOZZLE_BOTTOM_ID=3' - 6 1/2"; NOZZLE_BOTTOM_RAD=1' - 9 1/4"; NOZZLE_HEIGHT=6' - 6"; NOZZLE_HEIGHT/7*2=1' - 7 1/2"; NOZZLE_SIZE=30' - 0"; NOZZLE_TOP_OD=3' - 9 1/2"; NOZZLE_TOP_RAD=1' - 10 3/4"; NOZZLE_WB/4=1' - 2 13/16"; NOZZLE_WB_OD=6' - 2"; NOZZLE_WB_RAD=3' - 1"; NOZZLE_WB_RAD-2"=2' - 11"; RO=5' - 6 7/16"; RO/2=2' - 9 7/32"; RO2/2=2' - 9 7/32"; TRANSITION_TOP=10' - 1 1/4"; TRIPLE_F+1"=22' - 6"; TRIP_F=22' - 5"; TRIP_G=22' - 3 3/8"; TYPE=0' - 0"; Type Comments=Vari-Plume Laboratory Exhaust Mixed-Flow Inline Belt Drive With 1X3 Mixing Box; UNIT_HEIGHT=6' - 2"; UNIT_HEIGHT*.75=4' - 7 1/2"; UNIT_OD=5' - 3 1/16"; UNIT_RAD+((A/2)+.25")=5' - 8 25/32"; UNIT_RAD+((A/2)+.25")+4"=6' - 0 25/32"; UNIT_RADIUS=2' - 7 17/32"; UNIT_RADIUS*.6=2' - 4 3/8"; UNIT_RADIUS+4"=2' - 11 17/32"
- 445_QMXVP-36L-1X3_Mixing_Box: (A/2)+.25"=3' - 1 1/4"; (A/2)-2"=2' - 11"; (NOZZLE_HEIGHT-(NOZZLE_HEIGHT/8*2))/2=2' - 11 5/8"; (NOZZLE_WB_OD-NOZZLE_TOP_OD)/2=0' - 8"; -A=-6' - 2"; A=6' - 2"; A+.5=6' - 2 1/2"; A/2=3' - 1"; B=16' - 9"; B/2=8' - 4 1/2"; C=7' - 11"; C/2=3' - 11 1/2"; DUAL_F=14' - 3 3/4"; DUAL_F+1"=14' - 4 3/4"; DUAL_G=14' - 2"; E=6' - 0 5/8"; GA=0' - 0 3/32"; LONG_RO=21' - 9 1/8"; MB_A=8' - 6"; MB_HT=6' - 3 11/16"; MB_HT+.25"=6' - 3 15/16"; MB_HT-2.75"=6' - 0 15/16"; MB_HT/2=3' - 1 27/32"; Model=QMXVP-1X3_Mixing Box; NOZZLE_BOTTOM_ID=4' - 3 3/4"; NOZZLE_BOTTOM_RAD=2' - 1 7/8"; NOZZLE_HEIGHT=7' - 11"; NOZZLE_HEIGHT/7*2=1' - 11 3/4"; NOZZLE_SIZE=36' - 0"; NOZZLE_TOP_OD=4' - 10"; NOZZLE_TOP_RAD=2' - 5"; NOZZLE_WB/4=1' - 6"; NOZZLE_WB_OD=7' - 6"; NOZZLE_WB_RAD=3' - 9"; NOZZLE_WB_RAD-2"=3' - 7"; RO=5' - 6 7/16"; RO/2=2' - 9 7/32"; RO2/2=2' - 9 7/32"; TRANSITION_TOP=8' - 7 1/4"; TRIPLE_F+1"=22' - 6"; TRIP_F=22' - 5"; TRIP_G=22' - 3 3/8"; TYPE=0' - 0"; Type Comments=Vari-Plume Laboratory Exhaust Mixed-Flow Inline Belt Drive With 1X3 Mixing Box; UNIT_HEIGHT=6' - 2"; UNIT_HEIGHT*.75=4' - 7 1/2"; UNIT_OD=5' - 3 1/16"; UNIT_RAD+((A/2)+.25")=5' - 8 25/32"; UNIT_RAD+((A/2)+.25")+4"=6' - 0 25/32"; UNIT_RADIUS=2' - 7 17/32"; UNIT_RADIUS*.6=2' - 4 3/8"; UNIT_RADIUS+4"=2' - 11 17/32"
- 445_QMXVP-36H-1X3_Mixing_Box: (A/2)+.25"=3' - 1 1/4"; (A/2)-2"=2' - 11"; (NOZZLE_HEIGHT-(NOZZLE_HEIGHT/8*2))/2=2' - 11 5/8"; (NOZZLE_WB_OD-NOZZLE_TOP_OD)/2=0' - 8"; -A=-6' - 2"; A=6' - 2"; A+.5=6' - 2 1/2"; A/2=3' - 1"; B=16' - 9"; B/2=8' - 4 1/2"; C=7' - 11"; C/2=3' - 11 1/2"; DUAL_F=14' - 3 3/4"; DUAL_F+1"=14' - 4 3/4"; DUAL_G=14' - 2"; E=6' - 0 5/8"; GA=0' - 0 3/32"; LONG_RO=21' - 9 1/8"; MB_A=8' - 6"; MB_HT=6' - 3 11/16"; MB_HT+.25"=6' - 3 15/16"; MB_HT-2.75"=6' - 0 15/16"; MB_HT/2=3' - 1 27/32"; Model=QMXVP-1X3_Mixing Box; NOZZLE_BOTTOM_ID=4' - 3 3/4"; NOZZLE_BOTTOM_RAD=2' - 1 7/8"; NOZZLE_HEIGHT=7' - 11"; NOZZLE_HEIGHT/7*2=1' - 11 3/4"; NOZZLE_SIZE=36' - 0"; NOZZLE_TOP_OD=4' - 10"; NOZZLE_TOP_RAD=2' - 5"; NOZZLE_WB/4=1' - 6"; NOZZLE_WB_OD=7' - 6"; NOZZLE_WB_RAD=3' - 9"; NOZZLE_WB_RAD-2"=3' - 7"; RO=5' - 6 7/16"; RO/2=2' - 9 7/32"; RO2/2=2' - 9 7/32"; TRANSITION_TOP=8' - 7 1/4"; TRIPLE_F+1"=22' - 6"; TRIP_F=22' - 5"; TRIP_G=22' - 3 3/8"; TYPE=0' - 0"; Type Comments=Vari-Plume Laboratory Exhaust Mixed-Flow Inline Belt Drive With 1X3 Mixing Box; UNIT_HEIGHT=6' - 2"; UNIT_HEIGHT*.75=4' - 7 1/2"; UNIT_OD=5' - 3 1/16"; UNIT_RAD+((A/2)+.25")=5' - 8 25/32"; UNIT_RAD+((A/2)+.25")+4"=6' - 0 25/32"; UNIT_RADIUS=2' - 7 17/32"; UNIT_RADIUS*.6=2' - 4 3/8"; UNIT_RADIUS+4"=2' - 11 17/32"
- 490_QMXVP-30L-1X3_Mixing_Box: (A/2)+.25"=3' - 4 1/4"; (A/2)-2"=3' - 2"; (NOZZLE_HEIGHT-(NOZZLE_HEIGHT/8*2))/2=2' - 5 1/4"; (NOZZLE_WB_OD-NOZZLE_TOP_OD)/2=0' - 7 1/8"; -A=-6' - 8"; A=6' - 8"; A+.5=6' - 8 1/2"; A/2=3' - 4"; B=18' - 3"; B/2=9' - 1 1/2"; C=8' - 7"; C/2=4' - 3 1/2"; DUAL_F=16' - 0 3/4"; DUAL_F+1"=16' - 1 3/4"; DUAL_G=15' - 11"; E=6' - 6 1/2"; GA=0' - 0 1/8"; LONG_RO=24' - 9 1/4"; MB_A=9' - 5"; MB_HT=7' - 2 15/16"; MB_HT+.25"=7' - 3 3/16"; MB_HT-2.75"=7' - 0 3/16"; MB_HT/2=3' - 7 15/32"; Model=QMXVP-1X3_Mixing Box; NOZZLE_BOTTOM_ID=3' - 6 1/2"; NOZZLE_BOTTOM_RAD=1' - 9 1/4"; NOZZLE_HEIGHT=6' - 6"; NOZZLE_HEIGHT/7*2=1' - 7 1/2"; NOZZLE_SIZE=30' - 0"; NOZZLE_TOP_OD=3' - 9 1/2"; NOZZLE_TOP_RAD=1' - 10 3/4"; NOZZLE_WB/4=1' - 2 13/16"; NOZZLE_WB_OD=6' - 2"; NOZZLE_WB_RAD=3' - 1"; NOZZLE_WB_RAD-2"=2' - 11"; RO=6' - 0 1/4"; RO/2=3' - 0 1/8"; RO2/2=3' - 0 1/8"; TRANSITION_TOP=11' - 7 3/4"; TRIPLE_F+1"=25' - 6"; TRIP_F=25' - 5"; TRIP_G=25' - 3 1/2"; TYPE=0' - 0"; Type Comments=Vari-Plume Laboratory Exhaust Mixed-Flow Inline Belt Drive With 1X3 Mixing Box; UNIT_HEIGHT=6' - 8 1/2"; UNIT_HEIGHT*.75=5' - 0 3/8"; UNIT_OD=5' - 9 3/8"; UNIT_RAD+((A/2)+.25")=6' - 2 15/16"; UNIT_RAD+((A/2)+.25")+4"=6' - 6 15/16"; UNIT_RADIUS=2' - 10 11/16"; UNIT_RADIUS*.6=2' - 7 7/32"; UNIT_RADIUS+4"=3' - 2 11/16"
- 490_QMXVP-30H-1X3_Mixing_Box: (A/2)+.25"=3' - 4 1/4"; (A/2)-2"=3' - 2"; (NOZZLE_HEIGHT-(NOZZLE_HEIGHT/8*2))/2=2' - 5 1/4"; (NOZZLE_WB_OD-NOZZLE_TOP_OD)/2=0' - 7 1/8"; -A=-6' - 8"; A=6' - 8"; A+.5=6' - 8 1/2"; A/2=3' - 4"; B=18' - 3"; B/2=9' - 1 1/2"; C=8' - 7"; C/2=4' - 3 1/2"; DUAL_F=16' - 0 3/4"; DUAL_F+1"=16' - 1 3/4"; DUAL_G=15' - 11"; E=6' - 6 1/2"; GA=0' - 0 1/8"; LONG_RO=24' - 9 1/4"; MB_A=9' - 5"; MB_HT=7' - 2 15/16"; MB_HT+.25"=7' - 3 3/16"; MB_HT-2.75"=7' - 0 3/16"; MB_HT/2=3' - 7 15/32"; Model=QMXVP-1X3_Mixing Box; NOZZLE_BOTTOM_ID=3' - 6 1/2"; NOZZLE_BOTTOM_RAD=1' - 9 1/4"; NOZZLE_HEIGHT=6' - 6"; NOZZLE_HEIGHT/7*2=1' - 7 1/2"; NOZZLE_SIZE=30' - 0"; NOZZLE_TOP_OD=3' - 9 1/2"; NOZZLE_TOP_RAD=1' - 10 3/4"; NOZZLE_WB/4=1' - 2 13/16"; NOZZLE_WB_OD=6' - 2"; NOZZLE_WB_RAD=3' - 1"; NOZZLE_WB_RAD-2"=2' - 11"; RO=6' - 0 1/4"; RO/2=3' - 0 1/8"; RO2/2=3' - 0 1/8"; TRANSITION_TOP=11' - 7 3/4"; TRIPLE_F+1"=25' - 6"; TRIP_F=25' - 5"; TRIP_G=25' - 3 1/2"; TYPE=0' - 0"; Type Comments=Vari-Plume Laboratory Exhaust Mixed-Flow Inline Belt Drive With 1X3 Mixing Box; UNIT_HEIGHT=6' - 8 1/2"; UNIT_HEIGHT*.75=5' - 0 3/8"; UNIT_OD=5' - 9 3/8"; UNIT_RAD+((A/2)+.25")=6' - 2 15/16"; UNIT_RAD+((A/2)+.25")+4"=6' - 6 15/16"; UNIT_RADIUS=2' - 10 11/16"; UNIT_RADIUS*.6=2' - 7 7/32"; UNIT_RADIUS+4"=3' - 2 11/16"
- 490_QMXVP-36L-1X3_Mixing_Box: (A/2)+.25"=3' - 4 1/4"; (A/2)-2"=3' - 2"; (NOZZLE_HEIGHT-(NOZZLE_HEIGHT/8*2))/2=2' - 11 5/8"; (NOZZLE_WB_OD-NOZZLE_TOP_OD)/2=0' - 8"; -A=-6' - 8"; A=6' - 8"; A+.5=6' - 8 1/2"; A/2=3' - 4"; B=18' - 3"; B/2=9' - 1 1/2"; C=8' - 7"; C/2=4' - 3 1/2"; DUAL_F=16' - 0 3/4"; DUAL_F+1"=16' - 1 3/4"; DUAL_G=15' - 11"; E=6' - 6 1/2"; GA=0' - 0 1/8"; LONG_RO=24' - 9 1/4"; MB_A=9' - 5"; MB_HT=7' - 2 15/16"; MB_HT+.25"=7' - 3 3/16"; MB_HT-2.75"=7' - 0 3/16"; MB_HT/2=3' - 7 15/32"; Model=QMXVP-1X3_Mixing Box; NOZZLE_BOTTOM_ID=4' - 3 3/4"; NOZZLE_BOTTOM_RAD=2' - 1 7/8"; NOZZLE_HEIGHT=7' - 11"; NOZZLE_HEIGHT/7*2=1' - 11 3/4"; NOZZLE_SIZE=36' - 0"; NOZZLE_TOP_OD=4' - 10"; NOZZLE_TOP_RAD=2' - 5"; NOZZLE_WB/4=1' - 6"; NOZZLE_WB_OD=7' - 6"; NOZZLE_WB_RAD=3' - 9"; NOZZLE_WB_RAD-2"=3' - 7"; RO=6' - 0 1/4"; RO/2=3' - 0 1/8"; RO2/2=3' - 0 1/8"; TRANSITION_TOP=10' - 2 3/4"; TRIPLE_F+1"=25' - 6"; TRIP_F=25' - 5"; TRIP_G=25' - 3 1/2"; TYPE=0' - 0"; Type Comments=Vari-Plume Laboratory Exhaust Mixed-Flow Inline Belt Drive With 1X3 Mixing Box; UNIT_HEIGHT=6' - 8 1/2"; UNIT_HEIGHT*.75=5' - 0 3/8"; UNIT_OD=5' - 9 3/8"; UNIT_RAD+((A/2)+.25")=6' - 2 15/16"; UNIT_RAD+((A/2)+.25")+4"=6' - 6 15/16"; UNIT_RADIUS=2' - 10 11/16"; UNIT_RADIUS*.6=2' - 7 7/32"; UNIT_RADIUS+4"=3' - 2 11/16"
- 490_QMXVP-36H-1X3_Mixing_Box: (A/2)+.25"=3' - 4 1/4"; (A/2)-2"=3' - 2"; (NOZZLE_HEIGHT-(NOZZLE_HEIGHT/8*2))/2=2' - 11 5/8"; (NOZZLE_WB_OD-NOZZLE_TOP_OD)/2=0' - 8"; -A=-6' - 8"; A=6' - 8"; A+.5=6' - 8 1/2"; A/2=3' - 4"; B=18' - 3"; B/2=9' - 1 1/2"; C=8' - 7"; C/2=4' - 3 1/2"; DUAL_F=16' - 0 3/4"; DUAL_F+1"=16' - 1 3/4"; DUAL_G=15' - 11"; E=6' - 6 1/2"; GA=0' - 0 1/8"; LONG_RO=24' - 9 1/4"; MB_A=9' - 5"; MB_HT=7' - 2 15/16"; MB_HT+.25"=7' - 3 3/16"; MB_HT-2.75"=7' - 0 3/16"; MB_HT/2=3' - 7 15/32"; Model=QMXVP-1X3_Mixing Box; NOZZLE_BOTTOM_ID=4' - 3 3/4"; NOZZLE_BOTTOM_RAD=2' - 1 7/8"; NOZZLE_HEIGHT=7' - 11"; NOZZLE_HEIGHT/7*2=1' - 11 3/4"; NOZZLE_SIZE=36' - 0"; NOZZLE_TOP_OD=4' - 10"; NOZZLE_TOP_RAD=2' - 5"; NOZZLE_WB/4=1' - 6"; NOZZLE_WB_OD=7' - 6"; NOZZLE_WB_RAD=3' - 9"; NOZZLE_WB_RAD-2"=3' - 7"; RO=6' - 0 1/4"; RO/2=3' - 0 1/8"; RO2/2=3' - 0 1/8"; TRANSITION_TOP=10' - 2 3/4"; TRIPLE_F+1"=25' - 6"; TRIP_F=25' - 5"; TRIP_G=25' - 3 1/2"; TYPE=0' - 0"; Type Comments=Vari-Plume Laboratory Exhaust Mixed-Flow Inline Belt Drive With 1X3 Mixing Box; UNIT_HEIGHT=6' - 8 1/2"; UNIT_HEIGHT*.75=5' - 0 3/8"; UNIT_OD=5' - 9 3/8"; UNIT_RAD+((A/2)+.25")=6' - 2 15/16"; UNIT_RAD+((A/2)+.25")+4"=6' - 6 15/16"; UNIT_RADIUS=2' - 10 11/16"; UNIT_RADIUS*.6=2' - 7 7/32"; UNIT_RADIUS+4"=3' - 2 11/16"
- 540_QMXVP-36L-1X3_Mixing_Box: (A/2)+.25"=3' - 9 1/4"; (A/2)-2"=3' - 7"; (NOZZLE_HEIGHT-(NOZZLE_HEIGHT/8*2))/2=2' - 11 5/8"; (NOZZLE_WB_OD-NOZZLE_TOP_OD)/2=0' - 8"; -A=-7' - 6"; A=7' - 6"; A+.5=7' - 6 1/2"; A/2=3' - 9"; B=19' - 11"; B/2=9' - 11 1/2"; C=9' - 3"; C/2=4' - 7 1/2"; DUAL_F=17' - 0 1/4"; DUAL_F+1"=17' - 1 1/4"; DUAL_G=16' - 8 7/8"; E=7' - 1 3/8"; GA=0' - 0 1/8"; LONG_RO=25' - 10 1/8"; MB_A=10' - 6"; MB_HT=8' - 3 11/16"; MB_HT+.25"=8' - 3 15/16"; MB_HT-2.75"=8' - 0 15/16"; MB_HT/2=4' - 1 27/32"; Model=QMXVP-1X3_Mixing Box; NOZZLE_BOTTOM_ID=4' - 3 3/4"; NOZZLE_BOTTOM_RAD=2' - 1 7/8"; NOZZLE_HEIGHT=7' - 11"; NOZZLE_HEIGHT/7*2=1' - 11 3/4"; NOZZLE_SIZE=36' - 0"; NOZZLE_TOP_OD=4' - 10"; NOZZLE_TOP_RAD=2' - 5"; NOZZLE_WB/4=1' - 6"; NOZZLE_WB_OD=7' - 6"; NOZZLE_WB_RAD=3' - 9"; NOZZLE_WB_RAD-2"=3' - 7"; RO=6' - 7 1/8"; RO/2=3' - 3 9/16"; RO2/2=3' - 4 9/16"; TRANSITION_TOP=11' - 10 1/4"; TRIPLE_F+1"=26' - 7"; TRIP_F=26' - 6"; TRIP_G=26' - 4 3/8"; TYPE=0' - 0"; Type Comments=Vari-Plume Laboratory Exhaust Mixed-Flow Inline Belt Drive With 1X3 Mixing Box; UNIT_HEIGHT=7' - 3"; UNIT_HEIGHT*.75=5' - 5 1/4"; UNIT_OD=6' - 4 7/16"; UNIT_RAD+((A/2)+.25")=6' - 11 15/32"; UNIT_RAD+((A/2)+.25")+4"=7' - 3 15/32"; UNIT_RADIUS=3' - 2 7/32"; UNIT_RADIUS*.6=2' - 10 13/32"; UNIT_RADIUS+4"=3' - 6 7/32"
- 540_QMXVP-36H-1X3_Mixing_Box: (A/2)+.25"=3' - 9 1/4"; (A/2)-2"=3' - 7"; (NOZZLE_HEIGHT-(NOZZLE_HEIGHT/8*2))/2=2' - 11 5/8"; (NOZZLE_WB_OD-NOZZLE_TOP_OD)/2=0' - 8"; -A=-7' - 6"; A=7' - 6"; A+.5=7' - 6 1/2"; A/2=3' - 9"; B=19' - 11"; B/2=9' - 11 1/2"; C=9' - 3"; C/2=4' - 7 1/2"; DUAL_F=17' - 0 1/4"; DUAL_F+1"=17' - 1 1/4"; DUAL_G=16' - 8 7/8"; E=7' - 1 3/8"; GA=0' - 0 1/8"; LONG_RO=25' - 10 1/8"; MB_A=10' - 6"; MB_HT=8' - 3 11/16"; MB_HT+.25"=8' - 3 15/16"; MB_HT-2.75"=8' - 0 15/16"; MB_HT/2=4' - 1 27/32"; Model=QMXVP-1X3_Mixing Box; NOZZLE_BOTTOM_ID=4' - 3 3/4"; NOZZLE_BOTTOM_RAD=2' - 1 7/8"; NOZZLE_HEIGHT=7' - 11"; NOZZLE_HEIGHT/7*2=1' - 11 3/4"; NOZZLE_SIZE=36' - 0"; NOZZLE_TOP_OD=4' - 10"; NOZZLE_TOP_RAD=2' - 5"; NOZZLE_WB/4=1' - 6"; NOZZLE_WB_OD=7' - 6"; NOZZLE_WB_RAD=3' - 9"; NOZZLE_WB_RAD-2"=3' - 7"; RO=6' - 7 1/8"; RO/2=3' - 3 9/16"; RO2/2=3' - 4 9/16"; TRANSITION_TOP=11' - 10 1/4"; TRIPLE_F+1"=26' - 7"; TRIP_F=26' - 6"; TRIP_G=26' - 4 3/8"; TYPE=0' - 0"; Type Comments=Vari-Plume Laboratory Exhaust Mixed-Flow Inline Belt Drive With 1X3 Mixing Box; UNIT_HEIGHT=7' - 3"; UNIT_HEIGHT*.75=5' - 5 1/4"; UNIT_OD=6' - 4 7/16"; UNIT_RAD+((A/2)+.25")=6' - 11 15/32"; UNIT_RAD+((A/2)+.25")+4"=7' - 3 15/32"; UNIT_RADIUS=3' - 2 7/32"; UNIT_RADIUS*.6=2' - 10 13/32"; UNIT_RADIUS+4"=3' - 6 7/32"
- 540_QMXVP-49L-1X3_Mixing_Box: (A/2)+.25"=3' - 9 1/4"; (A/2)-2"=3' - 7"; (NOZZLE_HEIGHT-(NOZZLE_HEIGHT/8*2))/2=3' - 5 1/4"; (NOZZLE_WB_OD-NOZZLE_TOP_OD)/2=0' - 6 1/4"; -A=-7' - 6"; A=7' - 6"; A+.5=7' - 6 1/2"; A/2=3' - 9"; B=19' - 11"; B/2=9' - 11 1/2"; C=9' - 3"; C/2=4' - 7 1/2"; DUAL_F=17' - 0 1/4"; DUAL_F+1"=17' - 1 1/4"; DUAL_G=16' - 8 7/8"; E=7' - 1 3/8"; GA=0' - 0 1/8"; LONG_RO=25' - 10 1/8"; MB_A=10' - 6"; MB_HT=8' - 3 11/16"; MB_HT+.25"=8' - 3 15/16"; MB_HT-2.75"=8' - 0 15/16"; MB_HT/2=4' - 1 27/32"; Model=QMXVP-1X3_Mixing Box; NOZZLE_BOTTOM_ID=5' - 9 3/8"; NOZZLE_BOTTOM_RAD=2' - 10 11/16"; NOZZLE_HEIGHT=9' - 2"; NOZZLE_HEIGHT/7*2=2' - 3 1/2"; NOZZLE_SIZE=49' - 0"; NOZZLE_TOP_OD=6' - 4"; NOZZLE_TOP_RAD=3' - 2"; NOZZLE_WB/4=1' - 8 3/16"; NOZZLE_WB_OD=8' - 5"; NOZZLE_WB_RAD=4' - 2 1/2"; NOZZLE_WB_RAD-2"=4' - 0 1/2"; RO=6' - 7 1/8"; RO/2=3' - 3 9/16"; RO2/2=3' - 4 9/16"; TRANSITION_TOP=10' - 1 1/4"; TRIPLE_F+1"=26' - 7"; TRIP_F=26' - 6"; TRIP_G=26' - 4 3/8"; TYPE=0' - 0"; Type Comments=Vari-Plume Laboratory Exhaust Mixed-Flow Inline Belt Drive With 1X3 Mixing Box; UNIT_HEIGHT=7' - 3"; UNIT_HEIGHT*.75=5' - 5 1/4"; UNIT_OD=6' - 4 7/16"; UNIT_RAD+((A/2)+.25")=6' - 11 15/32"; UNIT_RAD+((A/2)+.25")+4"=7' - 3 15/32"; UNIT_RADIUS=3' - 2 7/32"; UNIT_RADIUS*.6=2' - 10 13/32"; UNIT_RADIUS+4"=3' - 6 7/32"
- 540_QMXVP-49H-1X3_Mixing_Box: (A/2)+.25"=3' - 9 1/4"; (A/2)-2"=3' - 7"; (NOZZLE_HEIGHT-(NOZZLE_HEIGHT/8*2))/2=3' - 5 1/4"; (NOZZLE_WB_OD-NOZZLE_TOP_OD)/2=0' - 6 1/4"; -A=-7' - 6"; A=7' - 6"; A+.5=7' - 6 1/2"; A/2=3' - 9"; B=19' - 11"; B/2=9' - 11 1/2"; C=9' - 3"; C/2=4' - 7 1/2"; DUAL_F=17' - 0 1/4"; DUAL_F+1"=17' - 1 1/4"; DUAL_G=16' - 8 7/8"; E=7' - 1 3/8"; GA=0' - 0 1/8"; LONG_RO=25' - 10 1/8"; MB_A=10' - 6"; MB_HT=8' - 3 11/16"; MB_HT+.25"=8' - 3 15/16"; MB_HT-2.75"=8' - 0 15/16"; MB_HT/2=4' - 1 27/32"; Model=QMXVP-1X3_Mixing Box; NOZZLE_BOTTOM_ID=5' - 9 3/8"; NOZZLE_BOTTOM_RAD=2' - 10 11/16"; NOZZLE_HEIGHT=9' - 2"; NOZZLE_HEIGHT/7*2=2' - 3 1/2"; NOZZLE_SIZE=49' - 0"; NOZZLE_TOP_OD=6' - 4"; NOZZLE_TOP_RAD=3' - 2"; NOZZLE_WB/4=1' - 8 3/16"; NOZZLE_WB_OD=8' - 5"; NOZZLE_WB_RAD=4' - 2 1/2"; NOZZLE_WB_RAD-2"=4' - 0 1/2"; RO=6' - 7 1/8"; RO/2=3' - 3 9/16"; RO2/2=3' - 4 9/16"; TRANSITION_TOP=10' - 1 1/4"; TRIPLE_F+1"=26' - 7"; TRIP_F=26' - 6"; TRIP_G=26' - 4 3/8"; TYPE=0' - 0"; Type Comments=Vari-Plume Laboratory Exhaust Mixed-Flow Inline Belt Drive With 1X3 Mixing Box; UNIT_HEIGHT=7' - 3"; UNIT_HEIGHT*.75=5' - 5 1/4"; UNIT_OD=6' - 4 7/16"; UNIT_RAD+((A/2)+.25")=6' - 11 15/32"; UNIT_RAD+((A/2)+.25")+4"=7' - 3 15/32"; UNIT_RADIUS=3' - 2 7/32"; UNIT_RADIUS*.6=2' - 10 13/32"; UNIT_RADIUS+4"=3' - 6 7/32"
- 600_QMXVP-36L-1X3_Mixing_Box: (A/2)+.25"=4' - 2 3/4"; (A/2)-2"=4' - 0 1/2"; (NOZZLE_HEIGHT-(NOZZLE_HEIGHT/8*2))/2=2' - 11 5/8"; (NOZZLE_WB_OD-NOZZLE_TOP_OD)/2=0' - 8"; -A=-8' - 5"; A=8' - 5"; A+.5=8' - 5 1/2"; A/2=4' - 2 1/2"; B=21' - 11"; B/2=10' - 11 1/2"; C=10' - 2"; C/2=5' - 1"; DUAL_F=18' - 0 1/4"; DUAL_F+1"=18' - 1 1/4"; DUAL_G=17' - 7 7/8"; E=7' - 10 3/8"; GA=0' - 0 3/16"; LONG_RO=26' - 11 1/8"; MB_A=12' - 0"; MB_HT=9' - 9 3/16"; MB_HT+.25"=9' - 9 7/16"; MB_HT-2.75"=9' - 6 7/16"; MB_HT/2=4' - 10 19/32"; Model=QMXVP-1X3_Mixing Box; NOZZLE_BOTTOM_ID=4' - 3 3/4"; NOZZLE_BOTTOM_RAD=2' - 1 7/8"; NOZZLE_HEIGHT=7' - 11"; NOZZLE_HEIGHT/7*2=1' - 11 3/4"; NOZZLE_SIZE=36' - 0"; NOZZLE_TOP_OD=4' - 10"; NOZZLE_TOP_RAD=2' - 5"; NOZZLE_WB/4=1' - 6"; NOZZLE_WB_OD=7' - 6"; NOZZLE_WB_RAD=3' - 9"; NOZZLE_WB_RAD-2"=3' - 7"; RO=7' - 4 1/16"; RO/2=3' - 8 1/32"; RO2/2=3' - 10 1/2"; TRANSITION_TOP=14' - 2 3/4"; TRIPLE_F+1"=27' - 8"; TRIP_F=27' - 7"; TRIP_G=27' - 5 3/8"; TYPE=0' - 0"; Type Comments=Vari-Plume Laboratory Exhaust Mixed-Flow Inline Belt Drive With 1X3 Mixing Box; UNIT_HEIGHT=7' - 11 1/2"; UNIT_HEIGHT*.75=5' - 11 5/8"; UNIT_OD=7' - 0 7/8"; UNIT_RAD+((A/2)+.25")=7' - 9 3/16"; UNIT_RAD+((A/2)+.25")+4"=8' - 1 3/16"; UNIT_RADIUS=3' - 6 7/16"; UNIT_RADIUS*.6=3' - 2 3/16"; UNIT_RADIUS+4"=3' - 10 7/16"
- 600_QMXVP-36H-1X3_Mixing_Box: (A/2)+.25"=4' - 2 3/4"; (A/2)-2"=4' - 0 1/2"; (NOZZLE_HEIGHT-(NOZZLE_HEIGHT/8*2))/2=2' - 11 5/8"; (NOZZLE_WB_OD-NOZZLE_TOP_OD)/2=0' - 8"; -A=-8' - 5"; A=8' - 5"; A+.5=8' - 5 1/2"; A/2=4' - 2 1/2"; B=21' - 11"; B/2=10' - 11 1/2"; C=10' - 2"; C/2=5' - 1"; DUAL_F=18' - 0 1/4"; DUAL_F+1"=18' - 1 1/4"; DUAL_G=17' - 7 7/8"; E=7' - 10 3/8"; GA=0' - 0 3/16"; LONG_RO=26' - 11 1/8"; MB_A=12' - 0"; MB_HT=9' - 9 3/16"; MB_HT+.25"=9' - 9 7/16"; MB_HT-2.75"=9' - 6 7/16"; MB_HT/2=4' - 10 19/32"; Model=QMXVP-1X3_Mixing Box; NOZZLE_BOTTOM_ID=4' - 3 3/4"; NOZZLE_BOTTOM_RAD=2' - 1 7/8"; NOZZLE_HEIGHT=7' - 11"; NOZZLE_HEIGHT/7*2=1' - 11 3/4"; NOZZLE_SIZE=36' - 0"; NOZZLE_TOP_OD=4' - 10"; NOZZLE_TOP_RAD=2' - 5"; NOZZLE_WB/4=1' - 6"; NOZZLE_WB_OD=7' - 6"; NOZZLE_WB_RAD=3' - 9"; NOZZLE_WB_RAD-2"=3' - 7"; RO=7' - 4 1/16"; RO/2=3' - 8 1/32"; RO2/2=3' - 10 1/2"; TRANSITION_TOP=14' - 2 3/4"; TRIPLE_F+1"=27' - 8"; TRIP_F=27' - 7"; TRIP_G=27' - 5 3/8"; TYPE=0' - 0"; Type Comments=Vari-Plume Laboratory Exhaust Mixed-Flow Inline Belt Drive With 1X3 Mixing Box; UNIT_HEIGHT=7' - 11 1/2"; UNIT_HEIGHT*.75=5' - 11 5/8"; UNIT_OD=7' - 0 7/8"; UNIT_RAD+((A/2)+.25")=7' - 9 3/16"; UNIT_RAD+((A/2)+.25")+4"=8' - 1 3/16"; UNIT_RADIUS=3' - 6 7/16"; UNIT_RADIUS*.6=3' - 2 3/16"; UNIT_RADIUS+4"=3' - 10 7/16"
- 600_QMXVP-49L-1X3_Mixing_Box: (A/2)+.25"=4' - 2 3/4"; (A/2)-2"=4' - 0 1/2"; (NOZZLE_HEIGHT-(NOZZLE_HEIGHT/8*2))/2=3' - 5 1/4"; (NOZZLE_WB_OD-NOZZLE_TOP_OD)/2=0' - 6 1/4"; -A=-8' - 5"; A=8' - 5"; A+.5=8' - 5 1/2"; A/2=4' - 2 1/2"; B=21' - 11"; B/2=10' - 11 1/2"; C=10' - 2"; C/2=5' - 1"; DUAL_F=18' - 0 1/4"; DUAL_F+1"=18' - 1 1/4"; DUAL_G=17' - 7 7/8"; E=7' - 10 3/8"; GA=0' - 0 3/16"; LONG_RO=26' - 11 1/8"; MB_A=12' - 0"; MB_HT=9' - 9 3/16"; MB_HT+.25"=9' - 9 7/16"; MB_HT-2.75"=9' - 6 7/16"; MB_HT/2=4' - 10 19/32"; Model=QMXVP-1X3_Mixing Box; NOZZLE_BOTTOM_ID=5' - 9 3/8"; NOZZLE_BOTTOM_RAD=2' - 10 11/16"; NOZZLE_HEIGHT=9' - 2"; NOZZLE_HEIGHT/7*2=2' - 3 1/2"; NOZZLE_SIZE=49' - 0"; NOZZLE_TOP_OD=6' - 4"; NOZZLE_TOP_RAD=3' - 2"; NOZZLE_WB/4=1' - 8 3/16"; NOZZLE_WB_OD=8' - 5"; NOZZLE_WB_RAD=4' - 2 1/2"; NOZZLE_WB_RAD-2"=4' - 0 1/2"; RO=7' - 4 1/16"; RO/2=3' - 8 1/32"; RO2/2=3' - 10 1/2"; TRANSITION_TOP=12' - 4 3/4"; TRIPLE_F+1"=27' - 8"; TRIP_F=27' - 7"; TRIP_G=27' - 5 3/8"; TYPE=0' - 0"; Type Comments=Vari-Plume Laboratory Exhaust Mixed-Flow Inline Belt Drive With 1X3 Mixing Box; UNIT_HEIGHT=7' - 11 1/2"; UNIT_HEIGHT*.75=5' - 11 5/8"; UNIT_OD=7' - 0 7/8"; UNIT_RAD+((A/2)+.25")=7' - 9 3/16"; UNIT_RAD+((A/2)+.25")+4"=8' - 1 3/16"; UNIT_RADIUS=3' - 6 7/16"; UNIT_RADIUS*.6=3' - 2 3/16"; UNIT_RADIUS+4"=3' - 10 7/16"
- 600_QMXVP-49H-1X3_Mixing_Box: (A/2)+.25"=4' - 2 3/4"; (A/2)-2"=4' - 0 1/2"; (NOZZLE_HEIGHT-(NOZZLE_HEIGHT/8*2))/2=3' - 5 1/4"; (NOZZLE_WB_OD-NOZZLE_TOP_OD)/2=0' - 6 1/4"; -A=-8' - 5"; A=8' - 5"; A+.5=8' - 5 1/2"; A/2=4' - 2 1/2"; B=21' - 11"; B/2=10' - 11 1/2"; C=10' - 2"; C/2=5' - 1"; DUAL_F=18' - 0 1/4"; DUAL_F+1"=18' - 1 1/4"; DUAL_G=17' - 7 7/8"; E=7' - 10 3/8"; GA=0' - 0 3/16"; LONG_RO=26' - 11 1/8"; MB_A=12' - 0"; MB_HT=9' - 9 3/16"; MB_HT+.25"=9' - 9 7/16"; MB_HT-2.75"=9' - 6 7/16"; MB_HT/2=4' - 10 19/32"; Model=QMXVP-1X3_Mixing Box; NOZZLE_BOTTOM_ID=5' - 9 3/8"; NOZZLE_BOTTOM_RAD=2' - 10 11/16"; NOZZLE_HEIGHT=9' - 2"; NOZZLE_HEIGHT/7*2=2' - 3 1/2"; NOZZLE_SIZE=49' - 0"; NOZZLE_TOP_OD=6' - 4"; NOZZLE_TOP_RAD=3' - 2"; NOZZLE_WB/4=1' - 8 3/16"; NOZZLE_WB_OD=8' - 5"; NOZZLE_WB_RAD=4' - 2 1/2"; NOZZLE_WB_RAD-2"=4' - 0 1/2"; RO=7' - 4 1/16"; RO/2=3' - 8 1/32"; RO2/2=3' - 10 1/2"; TRANSITION_TOP=12' - 4 3/4"; TRIPLE_F+1"=27' - 8"; TRIP_F=27' - 7"; TRIP_G=27' - 5 3/8"; TYPE=0' - 0"; Type Comments=Vari-Plume Laboratory Exhaust Mixed-Flow Inline Belt Drive With 1X3 Mixing Box; UNIT_HEIGHT=7' - 11 1/2"; UNIT_HEIGHT*.75=5' - 11 5/8"; UNIT_OD=7' - 0 7/8"; UNIT_RAD+((A/2)+.25")=7' - 9 3/16"; UNIT_RAD+((A/2)+.25")+4"=8' - 1 3/16"; UNIT_RADIUS=3' - 6 7/16"; UNIT_RADIUS*.6=3' - 2 3/16"; UNIT_RADIUS+4"=3' - 10 7/16"
- 120_QMXHPVP-12H-1X3_Mixing_Box: (A/2)+.25"=1' - 2 1/4"; (A/2)-2"=1' - 0"; (NOZZLE_HEIGHT-(NOZZLE_HEIGHT/8*2))/2=1' - 0"; (NOZZLE_WB_OD-NOZZLE_TOP_OD)/2=0' - 2 1/8"; -A=-2' - 4"; A=2' - 4"; A+.5=2' - 4 1/2"; A/2=1' - 2"; B=5' - 11"; B/2=2' - 11 1/2"; C=3' - 1"; C/2=1' - 6 1/2"; DUAL_F=5' - 4 1/4"; DUAL_F+1"=5' - 5 1/4"; DUAL_G=5' - 3 5/16"; E=2' - 3 3/16"; GA=0' - 0 3/32"; LONG_RO=7' - 9 1/4"; MB_A=2' - 11"; MB_HT=2' - 7 7/16"; MB_HT+.25"=2' - 7 11/16"; MB_HT-2.75"=2' - 4 11/16"; MB_HT/2=1' - 3 23/32"; Model=QMXHPVP-1X3_Mixing Box; NOZZLE_BOTTOM_ID=1' - 5 1/16"; NOZZLE_BOTTOM_RAD=0' - 8 17/32"; NOZZLE_HEIGHT=2' - 8"; NOZZLE_HEIGHT/7*2=0' - 8"; NOZZLE_SIZE=12' - 0"; NOZZLE_TOP_OD=1' - 7 1/2"; NOZZLE_TOP_RAD=0' - 9 3/4"; NOZZLE_WB/4=0' - 5 19/32"; NOZZLE_WB_OD=2' - 4"; NOZZLE_WB_RAD=1' - 2"; NOZZLE_WB_RAD-2"=1' - 0"; RO=1' - 9"; RO/2=0' - 10 1/2"; RO2/2=0' - 10 1/2"; TRANSITION_TOP=3' - 3 7/16"; TRIPLE_F+1"=8' - 5"; TRIP_F=8' - 4"; TRIP_G=8' - 3 1/2"; TYPE=1' - 0"; Type Comments=Vari-Plume Laboratory Exhaust Mixed-Flow High Pressure Inline Belt Drive With 1X3 Mixing Box; UNIT_HEIGHT=1' - 7 7/8"; UNIT_HEIGHT*.75=1' - 2 29/32"; UNIT_OD=1' - 5 1/16"; UNIT_RAD+((A/2)+.25")=1' - 10 25/32"; UNIT_RAD+((A/2)+.25")+4"=2' - 2 25/32"; UNIT_RADIUS=0' - 8 17/32"; UNIT_RADIUS*.6=0' - 7 11/16"; UNIT_RADIUS+4"=1' - 0 17/32"
- 120_QMXHPVP-12L-1X3_Mixing_Box: (A/2)+.25"=1' - 2 1/4"; (A/2)-2"=1' - 0"; (NOZZLE_HEIGHT-(NOZZLE_HEIGHT/8*2))/2=1' - 0"; (NOZZLE_WB_OD-NOZZLE_TOP_OD)/2=0' - 2 1/8"; -A=-2' - 4"; A=2' - 4"; A+.5=2' - 4 1/2"; A/2=1' - 2"; B=5' - 11"; B/2=2' - 11 1/2"; C=3' - 1"; C/2=1' - 6 1/2"; DUAL_F=5' - 4 1/4"; DUAL_F+1"=5' - 5 1/4"; DUAL_G=5' - 3 5/16"; E=2' - 3 3/16"; GA=0' - 0 3/32"; LONG_RO=7' - 9 1/4"; MB_A=2' - 11"; MB_HT=2' - 7 7/16"; MB_HT+.25"=2' - 7 11/16"; MB_HT-2.75"=2' - 4 11/16"; MB_HT/2=1' - 3 23/32"; Model=QMXHPVP-1X3_Mixing Box; NOZZLE_BOTTOM_ID=1' - 5 1/16"; NOZZLE_BOTTOM_RAD=0' - 8 17/32"; NOZZLE_HEIGHT=2' - 8"; NOZZLE_HEIGHT/7*2=0' - 8"; NOZZLE_SIZE=12' - 0"; NOZZLE_TOP_OD=1' - 7 1/2"; NOZZLE_TOP_RAD=0' - 9 3/4"; NOZZLE_WB/4=0' - 5 19/32"; NOZZLE_WB_OD=2' - 4"; NOZZLE_WB_RAD=1' - 2"; NOZZLE_WB_RAD-2"=1' - 0"; RO=1' - 9"; RO/2=0' - 10 1/2"; RO2/2=0' - 10 1/2"; TRANSITION_TOP=3' - 3 7/16"; TRIPLE_F+1"=8' - 5"; TRIP_F=8' - 4"; TRIP_G=8' - 3 1/2"; TYPE=1' - 0"; Type Comments=Vari-Plume Laboratory Exhaust Mixed-Flow High Pressure Inline Belt Drive With 1X3 Mixing Box; UNIT_HEIGHT=1' - 7 7/8"; UNIT_HEIGHT*.75=1' - 2 29/32"; UNIT_OD=1' - 5 1/16"; UNIT_RAD+((A/2)+.25")=1' - 10 25/32"; UNIT_RAD+((A/2)+.25")+4"=2' - 2 25/32"; UNIT_RADIUS=0' - 8 17/32"; UNIT_RADIUS*.6=0' - 7 11/16"; UNIT_RADIUS+4"=1' - 0 17/32"
- 120_QMXHPVP-9H-1X3_Mixing_Box: (A/2)+.25"=1' - 2 1/4"; (A/2)-2"=1' - 0"; (NOZZLE_HEIGHT-(NOZZLE_HEIGHT/8*2))/2=0' - 10 1/2"; (NOZZLE_WB_OD-NOZZLE_TOP_OD)/2=0' - 2 3/8"; -A=-2' - 4"; A=2' - 4"; A+.5=2' - 4 1/2"; A/2=1' - 2"; B=5' - 11"; B/2=2' - 11 1/2"; C=3' - 1"; C/2=1' - 6 1/2"; DUAL_F=5' - 4 1/4"; DUAL_F+1"=5' - 5 1/4"; DUAL_G=5' - 3 5/16"; E=2' - 3 3/16"; GA=0' - 0 3/32"; LONG_RO=7' - 9 1/4"; MB_A=2' - 11"; MB_HT=2' - 7 7/16"; MB_HT+.25"=2' - 7 11/16"; MB_HT-2.75"=2' - 4 11/16"; MB_HT/2=1' - 3 23/32"; Model=QMXHPVP-1X3_Mixing Box; NOZZLE_BOTTOM_ID=1' - 0 13/16"; NOZZLE_BOTTOM_RAD=0' - 6 13/32"; NOZZLE_HEIGHT=2' - 4"; NOZZLE_HEIGHT/7*2=0' - 7"; NOZZLE_SIZE=9' - 0"; NOZZLE_TOP_OD=1' - 1 1/2"; NOZZLE_TOP_RAD=0' - 6 3/4"; NOZZLE_WB/4=0' - 4 19/32"; NOZZLE_WB_OD=1' - 11"; NOZZLE_WB_RAD=0' - 11 1/2"; NOZZLE_WB_RAD-2"=0' - 9 1/2"; RO=1' - 9"; RO/2=0' - 10 1/2"; RO2/2=0' - 10 1/2"; TRANSITION_TOP=3' - 7 3/16"; TRIPLE_F+1"=8' - 5"; TRIP_F=8' - 4"; TRIP_G=8' - 3 1/2"; TYPE=1' - 0"; Type Comments=Vari-Plume Laboratory Exhaust Mixed-Flow High Pressure Inline Belt Drive With 1X3 Mixing Box; UNIT_HEIGHT=1' - 7 7/8"; UNIT_HEIGHT*.75=1' - 2 29/32"; UNIT_OD=1' - 5 1/16"; UNIT_RAD+((A/2)+.25")=1' - 10 25/32"; UNIT_RAD+((A/2)+.25")+4"=2' - 2 25/32"; UNIT_RADIUS=0' - 8 17/32"; UNIT_RADIUS*.6=0' - 7 11/16"; UNIT_RADIUS+4"=1' - 0 17/32"
- 120_QMXHPVP-9L-1X3_Mixing_Box: (A/2)+.25"=1' - 2 1/4"; (A/2)-2"=1' - 0"; (NOZZLE_HEIGHT-(NOZZLE_HEIGHT/8*2))/2=0' - 10 1/2"; (NOZZLE_WB_OD-NOZZLE_TOP_OD)/2=0' - 2 3/8"; -A=-2' - 4"; A=2' - 4"; A+.5=2' - 4 1/2"; A/2=1' - 2"; B=5' - 11"; B/2=2' - 11 1/2"; C=3' - 1"; C/2=1' - 6 1/2"; DUAL_F=5' - 4 1/4"; DUAL_F+1"=5' - 5 1/4"; DUAL_G=5' - 3 5/16"; E=2' - 3 3/16"; GA=0' - 0 3/32"; LONG_RO=7' - 9 1/4"; MB_A=2' - 11"; MB_HT=2' - 7 7/16"; MB_HT+.25"=2' - 7 11/16"; MB_HT-2.75"=2' - 4 11/16"; MB_HT/2=1' - 3 23/32"; Model=QMXHPVP-1X3_Mixing Box; NOZZLE_BOTTOM_ID=1' - 0 13/16"; NOZZLE_BOTTOM_RAD=0' - 6 13/32"; NOZZLE_HEIGHT=2' - 4"; NOZZLE_HEIGHT/7*2=0' - 7"; NOZZLE_SIZE=9' - 0"; NOZZLE_TOP_OD=1' - 1 1/2"; NOZZLE_TOP_RAD=0' - 6 3/4"; NOZZLE_WB/4=0' - 4 19/32"; NOZZLE_WB_OD=1' - 11"; NOZZLE_WB_RAD=0' - 11 1/2"; NOZZLE_WB_RAD-2"=0' - 9 1/2"; RO=1' - 9"; RO/2=0' - 10 1/2"; RO2/2=0' - 10 1/2"; TRANSITION_TOP=3' - 7 3/16"; TRIPLE_F+1"=8' - 5"; TRIP_F=8' - 4"; TRIP_G=8' - 3 1/2"; TYPE=1' - 0"; Type Comments=Vari-Plume Laboratory Exhaust Mixed-Flow High Pressure Inline Belt Drive With 1X3 Mixing Box; UNIT_HEIGHT=1' - 7 7/8"; UNIT_HEIGHT*.75=1' - 2 29/32"; UNIT_OD=1' - 5 1/16"; UNIT_RAD+((A/2)+.25")=1' - 10 25/32"; UNIT_RAD+((A/2)+.25")+4"=2' - 2 25/32"; UNIT_RADIUS=0' - 8 17/32"; UNIT_RADIUS*.6=0' - 7 11/16"; UNIT_RADIUS+4"=1' - 0 17/32"
- 135_QMXHPVP-12H-1X3_Mixing_Box: (A/2)+.25"=1' - 2 1/4"; (A/2)-2"=1' - 0"; (NOZZLE_HEIGHT-(NOZZLE_HEIGHT/8*2))/2=1' - 0"; (NOZZLE_WB_OD-NOZZLE_TOP_OD)/2=0' - 2 1/8"; -A=-2' - 4"; A=2' - 4"; A+.5=2' - 4 1/2"; A/2=1' - 2"; B=6' - 5"; B/2=3' - 2 1/2"; C=3' - 3"; C/2=1' - 7 1/2"; DUAL_F=5' - 4 1/4"; DUAL_F+1"=5' - 5 1/4"; DUAL_G=5' - 3 5/16"; E=2' - 3 1/8"; GA=0' - 0 3/32"; LONG_RO=7' - 9 1/4"; MB_A=3' - 0"; MB_HT=2' - 9 7/16"; MB_HT+.25"=2' - 9 11/16"; MB_HT-2.75"=2' - 6 11/16"; MB_HT/2=1' - 4 23/32"; Model=QMXHPVP-1X3_Mixing Box; NOZZLE_BOTTOM_ID=1' - 5 1/16"; NOZZLE_BOTTOM_RAD=0' - 8 17/32"; NOZZLE_HEIGHT=2' - 8"; NOZZLE_HEIGHT/7*2=0' - 8"; NOZZLE_SIZE=12' - 0"; NOZZLE_TOP_OD=1' - 7 1/2"; NOZZLE_TOP_RAD=0' - 9 3/4"; NOZZLE_WB/4=0' - 5 19/32"; NOZZLE_WB_OD=2' - 4"; NOZZLE_WB_RAD=1' - 2"; NOZZLE_WB_RAD-2"=1' - 0"; RO=1' - 8 15/16"; RO/2=0' - 10 15/32"; RO2/2=0' - 10 15/32"; TRANSITION_TOP=3' - 4 11/16"; TRIPLE_F+1"=8' - 5"; TRIP_F=8' - 4"; TRIP_G=8' - 3 1/2"; TYPE=1' - 0"; Type Comments=Vari-Plume Laboratory Exhaust Mixed-Flow High Pressure Inline Belt Drive With 1X3 Mixing Box; UNIT_HEIGHT=2' - 3"; UNIT_HEIGHT*.75=1' - 8 1/4"; UNIT_OD=1' - 7 1/4"; UNIT_RAD+((A/2)+.25")=1' - 11 7/8"; UNIT_RAD+((A/2)+.25")+4"=2' - 3 7/8"; UNIT_RADIUS=0' - 9 5/8"; UNIT_RADIUS*.6=0' - 8 21/32"; UNIT_RADIUS+4"=1' - 1 5/8"
- 135_QMXHPVP-12L-1X3_Mixing_Box: (A/2)+.25"=1' - 2 1/4"; (A/2)-2"=1' - 0"; (NOZZLE_HEIGHT-(NOZZLE_HEIGHT/8*2))/2=1' - 0"; (NOZZLE_WB_OD-NOZZLE_TOP_OD)/2=0' - 2 1/8"; -A=-2' - 4"; A=2' - 4"; A+.5=2' - 4 1/2"; A/2=1' - 2"; B=6' - 5"; B/2=3' - 2 1/2"; C=3' - 3"; C/2=1' - 7 1/2"; DUAL_F=5' - 4 1/4"; DUAL_F+1"=5' - 5 1/4"; DUAL_G=5' - 3 5/16"; E=2' - 3 1/8"; GA=0' - 0 3/32"; LONG_RO=7' - 9 1/4"; MB_A=3' - 0"; MB_HT=2' - 9 7/16"; MB_HT+.25"=2' - 9 11/16"; MB_HT-2.75"=2' - 6 11/16"; MB_HT/2=1' - 4 23/32"; Model=QMXHPVP-1X3_Mixing Box; NOZZLE_BOTTOM_ID=1' - 5 1/16"; NOZZLE_BOTTOM_RAD=0' - 8 17/32"; NOZZLE_HEIGHT=2' - 8"; NOZZLE_HEIGHT/7*2=0' - 8"; NOZZLE_SIZE=12' - 0"; NOZZLE_TOP_OD=1' - 7 1/2"; NOZZLE_TOP_RAD=0' - 9 3/4"; NOZZLE_WB/4=0' - 5 19/32"; NOZZLE_WB_OD=2' - 4"; NOZZLE_WB_RAD=1' - 2"; NOZZLE_WB_RAD-2"=1' - 0"; RO=1' - 8 15/16"; RO/2=0' - 10 15/32"; RO2/2=0' - 10 15/32"; TRANSITION_TOP=3' - 4 11/16"; TRIPLE_F+1"=8' - 5"; TRIP_F=8' - 4"; TRIP_G=8' - 3 1/2"; TYPE=1' - 0"; Type Comments=Vari-Plume Laboratory Exhaust Mixed-Flow High Pressure Inline Belt Drive With 1X3 Mixing Box; UNIT_HEIGHT=2' - 3"; UNIT_HEIGHT*.75=1' - 8 1/4"; UNIT_OD=1' - 7 1/4"; UNIT_RAD+((A/2)+.25")=1' - 11 7/8"; UNIT_RAD+((A/2)+.25")+4"=2' - 3 7/8"; UNIT_RADIUS=0' - 9 5/8"; UNIT_RADIUS*.6=0' - 8 21/32"; UNIT_RADIUS+4"=1' - 1 5/8"
- 135_QMXHPVP-9H-1X3_Mixing_Box: (A/2)+.25"=1' - 2 1/4"; (A/2)-2"=1' - 0"; (NOZZLE_HEIGHT-(NOZZLE_HEIGHT/8*2))/2=0' - 10 1/2"; (NOZZLE_WB_OD-NOZZLE_TOP_OD)/2=0' - 2 3/8"; -A=-2' - 4"; A=2' - 4"; A+.5=2' - 4 1/2"; A/2=1' - 2"; B=6' - 5"; B/2=3' - 2 1/2"; C=3' - 3"; C/2=1' - 7 1/2"; DUAL_F=5' - 4 1/4"; DUAL_F+1"=5' - 5 1/4"; DUAL_G=5' - 3 5/16"; E=2' - 3 1/8"; GA=0' - 0 3/32"; LONG_RO=7' - 9 1/4"; MB_A=3' - 0"; MB_HT=2' - 9 7/16"; MB_HT+.25"=2' - 9 11/16"; MB_HT-2.75"=2' - 6 11/16"; MB_HT/2=1' - 4 23/32"; Model=QMXHPVP-1X3_Mixing Box; NOZZLE_BOTTOM_ID=1' - 0 13/16"; NOZZLE_BOTTOM_RAD=0' - 6 13/32"; NOZZLE_HEIGHT=2' - 4"; NOZZLE_HEIGHT/7*2=0' - 7"; NOZZLE_SIZE=9' - 0"; NOZZLE_TOP_OD=1' - 1 1/2"; NOZZLE_TOP_RAD=0' - 6 3/4"; NOZZLE_WB/4=0' - 4 19/32"; NOZZLE_WB_OD=1' - 11"; NOZZLE_WB_RAD=0' - 11 1/2"; NOZZLE_WB_RAD-2"=0' - 9 1/2"; RO=1' - 8 15/16"; RO/2=0' - 10 15/32"; RO2/2=0' - 10 15/32"; TRANSITION_TOP=4' - 0 11/16"; TRIPLE_F+1"=8' - 5"; TRIP_F=8' - 4"; TRIP_G=8' - 3 1/2"; TYPE=1' - 0"; Type Comments=Vari-Plume Laboratory Exhaust Mixed-Flow High Pressure Inline Belt Drive With 1X3 Mixing Box; UNIT_HEIGHT=2' - 3"; UNIT_HEIGHT*.75=1' - 8 1/4"; UNIT_OD=1' - 7 1/4"; UNIT_RAD+((A/2)+.25")=1' - 11 7/8"; UNIT_RAD+((A/2)+.25")+4"=2' - 3 7/8"; UNIT_RADIUS=0' - 9 5/8"; UNIT_RADIUS*.6=0' - 8 21/32"; UNIT_RADIUS+4"=1' - 1 5/8"
- 135_QMXHPVP-9L-1X3_Mixing_Box: (A/2)+.25"=1' - 2 1/4"; (A/2)-2"=1' - 0"; (NOZZLE_HEIGHT-(NOZZLE_HEIGHT/8*2))/2=0' - 10 1/2"; (NOZZLE_WB_OD-NOZZLE_TOP_OD)/2=0' - 2 3/8"; -A=-2' - 4"; A=2' - 4"; A+.5=2' - 4 1/2"; A/2=1' - 2"; B=6' - 5"; B/2=3' - 2 1/2"; C=3' - 3"; C/2=1' - 7 1/2"; DUAL_F=5' - 4 1/4"; DUAL_F+1"=5' - 5 1/4"; DUAL_G=5' - 3 5/16"; E=2' - 3 1/8"; GA=0' - 0 3/32"; LONG_RO=7' - 9 1/4"; MB_A=3' - 0"; MB_HT=2' - 9 7/16"; MB_HT+.25"=2' - 9 11/16"; MB_HT-2.75"=2' - 6 11/16"; MB_HT/2=1' - 4 23/32"; Model=QMXHPVP-1X3_Mixing Box; NOZZLE_BOTTOM_ID=1' - 0 13/16"; NOZZLE_BOTTOM_RAD=0' - 6 13/32"; NOZZLE_HEIGHT=2' - 4"; NOZZLE_HEIGHT/7*2=0' - 7"; NOZZLE_SIZE=9' - 0"; NOZZLE_TOP_OD=1' - 1 1/2"; NOZZLE_TOP_RAD=0' - 6 3/4"; NOZZLE_WB/4=0' - 4 19/32"; NOZZLE_WB_OD=1' - 11"; NOZZLE_WB_RAD=0' - 11 1/2"; NOZZLE_WB_RAD-2"=0' - 9 1/2"; RO=1' - 8 15/16"; RO/2=0' - 10 15/32"; RO2/2=0' - 10 15/32"; TRANSITION_TOP=4' - 0 11/16"; TRIPLE_F+1"=8' - 5"; TRIP_F=8' - 4"; TRIP_G=8' - 3 1/2"; TYPE=1' - 0"; Type Comments=Vari-Plume Laboratory Exhaust Mixed-Flow High Pressure Inline Belt Drive With 1X3 Mixing Box; UNIT_HEIGHT=2' - 3"; UNIT_HEIGHT*.75=1' - 8 1/4"; UNIT_OD=1' - 7 1/4"; UNIT_RAD+((A/2)+.25")=1' - 11 7/8"; UNIT_RAD+((A/2)+.25")+4"=2' - 3 7/8"; UNIT_RADIUS=0' - 9 5/8"; UNIT_RADIUS*.6=0' - 8 21/32"; UNIT_RADIUS+4"=1' - 1 5/8"
- 150_QMXHPVP-12H-1X3_Mixing_Box: (A/2)+.25"=1' - 3 1/4"; (A/2)-2"=1' - 1"; (NOZZLE_HEIGHT-(NOZZLE_HEIGHT/8*2))/2=1' - 0"; (NOZZLE_WB_OD-NOZZLE_TOP_OD)/2=0' - 2 1/8"; -A=-2' - 6"; A=2' - 6"; A+.5=2' - 6 1/2"; A/2=1' - 3"; B=7' - 3"; B/2=3' - 7 1/2"; C=3' - 6"; C/2=1' - 9"; DUAL_F=5' - 8 1/4"; DUAL_F+1"=5' - 9 1/4"; DUAL_G=5' - 7 5/16"; E=2' - 5 1/8"; GA=0' - 0 3/32"; LONG_RO=8' - 3 1/4"; MB_A=3' - 2"; MB_HT=2' - 11 3/16"; MB_HT+.25"=2' - 11 7/16"; MB_HT-2.75"=2' - 8 7/16"; MB_HT/2=1' - 5 19/32"; Model=QMXHPVP-1X3_Mixing Box; NOZZLE_BOTTOM_ID=1' - 5 1/16"; NOZZLE_BOTTOM_RAD=0' - 8 17/32"; NOZZLE_HEIGHT=2' - 8"; NOZZLE_HEIGHT/7*2=0' - 8"; NOZZLE_SIZE=12' - 0"; NOZZLE_TOP_OD=1' - 7 1/2"; NOZZLE_TOP_RAD=0' - 9 3/4"; NOZZLE_WB/4=0' - 5 19/32"; NOZZLE_WB_OD=2' - 4"; NOZZLE_WB_RAD=1' - 2"; NOZZLE_WB_RAD-2"=1' - 0"; RO=1' - 10 15/16"; RO/2=0' - 11 15/32"; RO2/2=0' - 11 15/32"; TRANSITION_TOP=3' - 10 1/4"; TRIPLE_F+1"=8' - 11"; TRIP_F=8' - 10"; TRIP_G=8' - 9 1/2"; TYPE=1' - 0"; Type Comments=Vari-Plume Laboratory Exhaust Mixed-Flow High Pressure Inline Belt Drive With 1X3 Mixing Box; UNIT_HEIGHT=2' - 6"; UNIT_HEIGHT*.75=1' - 10 1/2"; UNIT_OD=1' - 9 3/8"; UNIT_RAD+((A/2)+.25")=2' - 1 15/16"; UNIT_RAD+((A/2)+.25")+4"=2' - 5 15/16"; UNIT_RADIUS=0' - 10 11/16"; UNIT_RADIUS*.6=0' - 9 5/8"; UNIT_RADIUS+4"=1' - 2 11/16"
- 150_QMXHPVP-12L-1X3_Mixing_Box: (A/2)+.25"=1' - 3 1/4"; (A/2)-2"=1' - 1"; (NOZZLE_HEIGHT-(NOZZLE_HEIGHT/8*2))/2=1' - 0"; (NOZZLE_WB_OD-NOZZLE_TOP_OD)/2=0' - 2 1/8"; -A=-2' - 6"; A=2' - 6"; A+.5=2' - 6 1/2"; A/2=1' - 3"; B=7' - 3"; B/2=3' - 7 1/2"; C=3' - 6"; C/2=1' - 9"; DUAL_F=5' - 8 1/4"; DUAL_F+1"=5' - 9 1/4"; DUAL_G=5' - 7 5/16"; E=2' - 5 1/8"; GA=0' - 0 3/32"; LONG_RO=8' - 3 1/4"; MB_A=3' - 2"; MB_HT=2' - 11 3/16"; MB_HT+.25"=2' - 11 7/16"; MB_HT-2.75"=2' - 8 7/16"; MB_HT/2=1' - 5 19/32"; Model=QMXHPVP-1X3_Mixing Box; NOZZLE_BOTTOM_ID=1' - 5 1/16"; NOZZLE_BOTTOM_RAD=0' - 8 17/32"; NOZZLE_HEIGHT=2' - 8"; NOZZLE_HEIGHT/7*2=0' - 8"; NOZZLE_SIZE=12' - 0"; NOZZLE_TOP_OD=1' - 7 1/2"; NOZZLE_TOP_RAD=0' - 9 3/4"; NOZZLE_WB/4=0' - 5 19/32"; NOZZLE_WB_OD=2' - 4"; NOZZLE_WB_RAD=1' - 2"; NOZZLE_WB_RAD-2"=1' - 0"; RO=1' - 10 15/16"; RO/2=0' - 11 15/32"; RO2/2=0' - 11 15/32"; TRANSITION_TOP=3' - 10 1/4"; TRIPLE_F+1"=8' - 11"; TRIP_F=8' - 10"; TRIP_G=8' - 9 1/2"; TYPE=1' - 0"; Type Comments=Vari-Plume Laboratory Exhaust Mixed-Flow High Pressure Inline Belt Drive With 1X3 Mixing Box; UNIT_HEIGHT=2' - 6"; UNIT_HEIGHT*.75=1' - 10 1/2"; UNIT_OD=1' - 9 3/8"; UNIT_RAD+((A/2)+.25")=2' - 1 15/16"; UNIT_RAD+((A/2)+.25")+4"=2' - 5 15/16"; UNIT_RADIUS=0' - 10 11/16"; UNIT_RADIUS*.6=0' - 9 5/8"; UNIT_RADIUS+4"=1' - 2 11/16"
- 150_QMXHPVP-15H-1X3_Mixing_Box: (A/2)+.25"=1' - 3 1/4"; (A/2)-2"=1' - 1"; (NOZZLE_HEIGHT-(NOZZLE_HEIGHT/8*2))/2=1' - 4 1/8"; (NOZZLE_WB_OD-NOZZLE_TOP_OD)/2=0' - 3 1/4"; -A=-2' - 6"; A=2' - 6"; A+.5=2' - 6 1/2"; A/2=1' - 3"; B=7' - 3"; B/2=3' - 7 1/2"; C=3' - 6"; C/2=1' - 9"; DUAL_F=5' - 8 1/4"; DUAL_F+1"=5' - 9 1/4"; DUAL_G=5' - 7 5/16"; E=2' - 5 1/8"; GA=0' - 0 3/32"; LONG_RO=8' - 3 1/4"; MB_A=3' - 2"; MB_HT=2' - 11 3/16"; MB_HT+.25"=2' - 11 7/16"; MB_HT-2.75"=2' - 8 7/16"; MB_HT/2=1' - 5 19/32"; Model=QMXHPVP-1X3_Mixing Box; NOZZLE_BOTTOM_ID=1' - 9 3/8"; NOZZLE_BOTTOM_RAD=0' - 10 11/16"; NOZZLE_HEIGHT=3' - 7"; NOZZLE_HEIGHT/7*2=0' - 10 3/4"; NOZZLE_SIZE=15' - 0"; NOZZLE_TOP_OD=1' - 11"; NOZZLE_TOP_RAD=0' - 11 1/2"; NOZZLE_WB/4=0' - 7 3/16"; NOZZLE_WB_OD=3' - 0"; NOZZLE_WB_RAD=1' - 6"; NOZZLE_WB_RAD-2"=1' - 4"; RO=1' - 10 15/16"; RO/2=0' - 11 15/32"; RO2/2=0' - 11 15/32"; TRANSITION_TOP=3' - 7 5/16"; TRIPLE_F+1"=8' - 11"; TRIP_F=8' - 10"; TRIP_G=8' - 9 1/2"; TYPE=1' - 0"; Type Comments=Vari-Plume Laboratory Exhaust Mixed-Flow High Pressure Inline Belt Drive With 1X3 Mixing Box; UNIT_HEIGHT=2' - 6"; UNIT_HEIGHT*.75=1' - 10 1/2"; UNIT_OD=1' - 9 3/8"; UNIT_RAD+((A/2)+.25")=2' - 1 15/16"; UNIT_RAD+((A/2)+.25")+4"=2' - 5 15/16"; UNIT_RADIUS=0' - 10 11/16"; UNIT_RADIUS*.6=0' - 9 5/8"; UNIT_RADIUS+4"=1' - 2 11/16"
- 150_QMXHPVP-15L-1X3_Mixing_Box: (A/2)+.25"=1' - 3 1/4"; (A/2)-2"=1' - 1"; (NOZZLE_HEIGHT-(NOZZLE_HEIGHT/8*2))/2=1' - 4 1/8"; (NOZZLE_WB_OD-NOZZLE_TOP_OD)/2=0' - 3 1/4"; -A=-2' - 6"; A=2' - 6"; A+.5=2' - 6 1/2"; A/2=1' - 3"; B=7' - 3"; B/2=3' - 7 1/2"; C=3' - 6"; C/2=1' - 9"; DUAL_F=5' - 8 1/4"; DUAL_F+1"=5' - 9 1/4"; DUAL_G=5' - 7 5/16"; E=2' - 5 1/8"; GA=0' - 0 3/32"; LONG_RO=99' - 3"; MB_A=3' - 2"; MB_HT=2' - 11 3/16"; MB_HT+.25"=2' - 11 7/16"; MB_HT-2.75"=2' - 8 7/16"; MB_HT/2=1' - 5 19/32"; Model=QMXHPVP-1X3_Mixing Box; NOZZLE_BOTTOM_ID=1' - 9 3/8"; NOZZLE_BOTTOM_RAD=0' - 10 11/16"; NOZZLE_HEIGHT=3' - 7"; NOZZLE_HEIGHT/7*2=0' - 10 3/4"; NOZZLE_SIZE=15' - 0"; NOZZLE_TOP_OD=1' - 11"; NOZZLE_TOP_RAD=0' - 11 1/2"; NOZZLE_WB/4=0' - 7 3/16"; NOZZLE_WB_OD=3' - 0"; NOZZLE_WB_RAD=1' - 6"; NOZZLE_WB_RAD-2"=1' - 4"; RO=1' - 10 15/16"; RO/2=0' - 11 15/32"; RO2/2=0' - 11 15/32"; TRANSITION_TOP=3' - 7 5/16"; TRIPLE_F+1"=8' - 11"; TRIP_F=8' - 10"; TRIP_G=8' - 9 1/2"; TYPE=1' - 0"; Type Comments=Vari-Plume Laboratory Exhaust Mixed-Flow High Pressure Inline Belt Drive With 1X3 Mixing Box; UNIT_HEIGHT=2' - 6"; UNIT_HEIGHT*.75=1' - 10 1/2"; UNIT_OD=1' - 9 3/8"; UNIT_RAD+((A/2)+.25")=2' - 1 15/16"; UNIT_RAD+((A/2)+.25")+4"=2' - 5 15/16"; UNIT_RADIUS=0' - 10 11/16"; UNIT_RADIUS*.6=0' - 9 5/8"; UNIT_RADIUS+4"=1' - 2 11/16"
- 150_QMXHPVP-9H-1X3_Mixing_Box: (A/2)+.25"=1' - 3 1/4"; (A/2)-2"=1' - 1"; (NOZZLE_HEIGHT-(NOZZLE_HEIGHT/8*2))/2=0' - 10 1/2"; (NOZZLE_WB_OD-NOZZLE_TOP_OD)/2=0' - 2 3/8"; -A=-2' - 6"; A=2' - 6"; A+.5=2' - 6 1/2"; A/2=1' - 3"; B=7' - 3"; B/2=3' - 7 1/2"; C=3' - 6"; C/2=1' - 9"; DUAL_F=5' - 8 1/4"; DUAL_F+1"=5' - 9 1/4"; DUAL_G=5' - 7 5/16"; E=2' - 5 1/8"; GA=0' - 0 3/32"; LONG_RO=8' - 3 1/4"; MB_A=3' - 2"; MB_HT=2' - 11 3/16"; MB_HT+.25"=2' - 11 7/16"; MB_HT-2.75"=2' - 8 7/16"; MB_HT/2=1' - 5 19/32"; Model=QMXHPVP-1X3_Mixing Box; NOZZLE_BOTTOM_ID=1' - 0 13/16"; NOZZLE_BOTTOM_RAD=0' - 6 13/32"; NOZZLE_HEIGHT=2' - 4"; NOZZLE_HEIGHT/7*2=0' - 7"; NOZZLE_SIZE=9' - 0"; NOZZLE_TOP_OD=1' - 1 1/2"; NOZZLE_TOP_RAD=0' - 6 3/4"; NOZZLE_WB/4=0' - 4 19/32"; NOZZLE_WB_OD=1' - 11"; NOZZLE_WB_RAD=0' - 11 1/2"; NOZZLE_WB_RAD-2"=0' - 9 1/2"; RO=1' - 10 15/16"; RO/2=0' - 11 15/32"; RO2/2=0' - 11 15/32"; TRANSITION_TOP=4' - 6 1/4"; TRIPLE_F+1"=8' - 11"; TRIP_F=8' - 10"; TRIP_G=8' - 9 1/2"; TYPE=1' - 0"; Type Comments=Vari-Plume Laboratory Exhaust Mixed-Flow High Pressure Inline Belt Drive With 1X3 Mixing Box; UNIT_HEIGHT=2' - 6"; UNIT_HEIGHT*.75=1' - 10 1/2"; UNIT_OD=1' - 9 3/8"; UNIT_RAD+((A/2)+.25")=2' - 1 15/16"; UNIT_RAD+((A/2)+.25")+4"=2' - 5 15/16"; UNIT_RADIUS=0' - 10 11/16"; UNIT_RADIUS*.6=0' - 9 5/8"; UNIT_RADIUS+4"=1' - 2 11/16"
- 150_QMXHPVP-9L-1X3_Mixing_Box: (A/2)+.25"=1' - 3 1/4"; (A/2)-2"=1' - 1"; (NOZZLE_HEIGHT-(NOZZLE_HEIGHT/8*2))/2=0' - 10 1/2"; (NOZZLE_WB_OD-NOZZLE_TOP_OD)/2=0' - 2 3/8"; -A=-2' - 6"; A=2' - 6"; A+.5=2' - 6 1/2"; A/2=1' - 3"; B=7' - 3"; B/2=3' - 7 1/2"; C=3' - 6"; C/2=1' - 9"; DUAL_F=5' - 8 1/4"; DUAL_F+1"=5' - 9 1/4"; DUAL_G=5' - 7 5/16"; E=2' - 5 1/8"; GA=0' - 0 3/32"; LONG_RO=8' - 3 1/4"; MB_A=3' - 2"; MB_HT=2' - 11 3/16"; MB_HT+.25"=2' - 11 7/16"; MB_HT-2.75"=2' - 8 7/16"; MB_HT/2=1' - 5 19/32"; Model=QMXHPVP-1X3_Mixing Box; NOZZLE_BOTTOM_ID=1' - 0 13/16"; NOZZLE_BOTTOM_RAD=0' - 6 13/32"; NOZZLE_HEIGHT=2' - 4"; NOZZLE_HEIGHT/7*2=0' - 7"; NOZZLE_SIZE=9' - 0"; NOZZLE_TOP_OD=1' - 1 1/2"; NOZZLE_TOP_RAD=0' - 6 3/4"; NOZZLE_WB/4=0' - 4 19/32"; NOZZLE_WB_OD=1' - 11"; NOZZLE_WB_RAD=0' - 11 1/2"; NOZZLE_WB_RAD-2"=0' - 9 1/2"; RO=1' - 10 15/16"; RO/2=0' - 11 15/32"; RO2/2=0' - 11 15/32"; TRANSITION_TOP=4' - 6 1/4"; TRIPLE_F+1"=8' - 11"; TRIP_F=8' - 10"; TRIP_G=8' - 9 1/2"; TYPE=1' - 0"; Type Comments=Vari-Plume Laboratory Exhaust Mixed-Flow High Pressure Inline Belt Drive With 1X3 Mixing Box; UNIT_HEIGHT=2' - 6"; UNIT_HEIGHT*.75=1' - 10 1/2"; UNIT_OD=1' - 9 3/8"; UNIT_RAD+((A/2)+.25")=2' - 1 15/16"; UNIT_RAD+((A/2)+.25")+4"=2' - 5 15/16"; UNIT_RADIUS=0' - 10 11/16"; UNIT_RADIUS*.6=0' - 9 5/8"; UNIT_RADIUS+4"=1' - 2 11/16"
- 165_QMXHPVP-12H-1X3_Mixing_Box: (A/2)+.25"=1' - 4 1/4"; (A/2)-2"=1' - 2"; (NOZZLE_HEIGHT-(NOZZLE_HEIGHT/8*2))/2=1' - 0"; (NOZZLE_WB_OD-NOZZLE_TOP_OD)/2=0' - 2 1/8"; -A=-2' - 8"; A=2' - 8"; A+.5=2' - 8 1/2"; A/2=1' - 4"; B=7' - 5"; B/2=3' - 8 1/2"; C=3' - 8"; C/2=1' - 10"; DUAL_F=6' - 0 1/4"; DUAL_F+1"=6' - 1 1/4"; DUAL_G=5' - 11 5/16"; E=2' - 7 1/8"; GA=0' - 0 3/32"; LONG_RO=8' - 9 1/4"; MB_A=3' - 5"; MB_HT=3' - 0 15/16"; MB_HT+.25"=3' - 1 3/16"; MB_HT-2.75"=2' - 10 3/16"; MB_HT/2=1' - 6 15/32"; Model=QMXHPVP-1X3_Mixing Box; NOZZLE_BOTTOM_ID=1' - 5 1/16"; NOZZLE_BOTTOM_RAD=0' - 8 17/32"; NOZZLE_HEIGHT=2' - 8"; NOZZLE_HEIGHT/7*2=0' - 8"; NOZZLE_SIZE=12' - 0"; NOZZLE_TOP_OD=1' - 7 1/2"; NOZZLE_TOP_RAD=0' - 9 3/4"; NOZZLE_WB/4=0' - 5 19/32"; NOZZLE_WB_OD=2' - 4"; NOZZLE_WB_RAD=1' - 2"; NOZZLE_WB_RAD-2"=1' - 0"; RO=2' - 0 15/16"; RO/2=1' - 0 15/32"; RO2/2=1' - 0 15/32"; TRANSITION_TOP=4' - 5 1/4"; TRIPLE_F+1"=9' - 5"; TRIP_F=9' - 4"; TRIP_G=9' - 3 1/2"; TYPE=1' - 0"; Type Comments=Vari-Plume Laboratory Exhaust Mixed-Flow High Pressure Inline Belt Drive With 1X3 Mixing Box; UNIT_HEIGHT=2' - 9"; UNIT_HEIGHT*.75=2' - 0 3/4"; UNIT_OD=1' - 11 1/2"; UNIT_RAD+((A/2)+.25")=2' - 4"; UNIT_RAD+((A/2)+.25")+4"=2' - 8"; UNIT_RADIUS=0' - 11 3/4"; UNIT_RADIUS*.6=0' - 10 9/16"; UNIT_RADIUS+4"=1' - 3 3/4"
- 165_QMXHPVP-12L-1X3_Mixing_Box: (A/2)+.25"=1' - 4 1/4"; (A/2)-2"=1' - 2"; (NOZZLE_HEIGHT-(NOZZLE_HEIGHT/8*2))/2=1' - 0"; (NOZZLE_WB_OD-NOZZLE_TOP_OD)/2=0' - 2 1/8"; -A=-2' - 8"; A=2' - 8"; A+.5=2' - 8 1/2"; A/2=1' - 4"; B=7' - 5"; B/2=3' - 8 1/2"; C=3' - 8"; C/2=1' - 10"; DUAL_F=6' - 0 1/4"; DUAL_F+1"=6' - 1 1/4"; DUAL_G=5' - 11 5/16"; E=2' - 7 1/8"; GA=0' - 0 3/32"; LONG_RO=8' - 9 1/4"; MB_A=3' - 5"; MB_HT=3' - 0 15/16"; MB_HT+.25"=3' - 1 3/16"; MB_HT-2.75"=2' - 10 3/16"; MB_HT/2=1' - 6 15/32"; Model=QMXHPVP-1X3_Mixing Box; NOZZLE_BOTTOM_ID=1' - 5 1/16"; NOZZLE_BOTTOM_RAD=0' - 8 17/32"; NOZZLE_HEIGHT=2' - 8"; NOZZLE_HEIGHT/7*2=0' - 8"; NOZZLE_SIZE=12' - 0"; NOZZLE_TOP_OD=1' - 7 1/2"; NOZZLE_TOP_RAD=0' - 9 3/4"; NOZZLE_WB/4=0' - 5 19/32"; NOZZLE_WB_OD=2' - 4"; NOZZLE_WB_RAD=1' - 2"; NOZZLE_WB_RAD-2"=1' - 0"; RO=2' - 0 15/16"; RO/2=1' - 0 15/32"; RO2/2=1' - 0 15/32"; TRANSITION_TOP=4' - 5 1/4"; TRIPLE_F+1"=9' - 5"; TRIP_F=9' - 4"; TRIP_G=9' - 3 1/2"; TYPE=1' - 0"; Type Comments=Vari-Plume Laboratory Exhaust Mixed-Flow High Pressure Inline Belt Drive With 1X3 Mixing Box; UNIT_HEIGHT=2' - 9"; UNIT_HEIGHT*.75=2' - 0 3/4"; UNIT_OD=1' - 11 1/2"; UNIT_RAD+((A/2)+.25")=2' - 4"; UNIT_RAD+((A/2)+.25")+4"=2' - 8"; UNIT_RADIUS=0' - 11 3/4"; UNIT_RADIUS*.6=0' - 10 9/16"; UNIT_RADIUS+4"=1' - 3 3/4"
- 165_QMXHPVP-15H-1X3_Mixing_Box: (A/2)+.25"=1' - 4 1/4"; (A/2)-2"=1' - 2"; (NOZZLE_HEIGHT-(NOZZLE_HEIGHT/8*2))/2=1' - 4 1/8"; (NOZZLE_WB_OD-NOZZLE_TOP_OD)/2=0' - 3 1/4"; -A=-2' - 8"; A=2' - 8"; A+.5=2' - 8 1/2"; A/2=1' - 4"; B=7' - 5"; B/2=3' - 8 1/2"; C=3' - 8"; C/2=1' - 10"; DUAL_F=6' - 0 1/4"; DUAL_F+1"=6' - 1 1/4"; DUAL_G=5' - 11 5/16"; E=2' - 7 1/8"; GA=0' - 0 3/32"; LONG_RO=8' - 9 1/4"; MB_A=3' - 5"; MB_HT=3' - 0 15/16"; MB_HT+.25"=3' - 1 3/16"; MB_HT-2.75"=2' - 10 3/16"; MB_HT/2=1' - 6 15/32"; Model=QMXHPVP-1X3_Mixing Box; NOZZLE_BOTTOM_ID=1' - 9 3/8"; NOZZLE_BOTTOM_RAD=0' - 10 11/16"; NOZZLE_HEIGHT=3' - 7"; NOZZLE_HEIGHT/7*2=0' - 10 3/4"; NOZZLE_SIZE=15' - 0"; NOZZLE_TOP_OD=1' - 11"; NOZZLE_TOP_RAD=0' - 11 1/2"; NOZZLE_WB/4=0' - 7 3/16"; NOZZLE_WB_OD=3' - 0"; NOZZLE_WB_RAD=1' - 6"; NOZZLE_WB_RAD-2"=1' - 4"; RO=2' - 0 15/16"; RO/2=1' - 0 15/32"; RO2/2=1' - 0 15/32"; TRANSITION_TOP=3' - 9 5/16"; TRIPLE_F+1"=9' - 5"; TRIP_F=9' - 4"; TRIP_G=9' - 3 1/2"; TYPE=1' - 0"; Type Comments=Vari-Plume Laboratory Exhaust Mixed-Flow High Pressure Inline Belt Drive With 1X3 Mixing Box; UNIT_HEIGHT=2' - 9"; UNIT_HEIGHT*.75=2' - 0 3/4"; UNIT_OD=1' - 11 1/2"; UNIT_RAD+((A/2)+.25")=2' - 4"; UNIT_RAD+((A/2)+.25")+4"=2' - 8"; UNIT_RADIUS=0' - 11 3/4"; UNIT_RADIUS*.6=0' - 10 9/16"; UNIT_RADIUS+4"=1' - 3 3/4"
- 165_QMXHPVP-15L-1X3_Mixing_Box: (A/2)+.25"=1' - 4 1/4"; (A/2)-2"=1' - 2"; (NOZZLE_HEIGHT-(NOZZLE_HEIGHT/8*2))/2=1' - 4 1/8"; (NOZZLE_WB_OD-NOZZLE_TOP_OD)/2=0' - 3 1/4"; -A=-2' - 8"; A=2' - 8"; A+.5=2' - 8 1/2"; A/2=1' - 4"; B=7' - 5"; B/2=3' - 8 1/2"; C=3' - 8"; C/2=1' - 10"; DUAL_F=6' - 0 1/4"; DUAL_F+1"=6' - 1 1/4"; DUAL_G=5' - 11 5/16"; E=2' - 7 1/8"; GA=0' - 0 3/32"; LONG_RO=8' - 9 1/4"; MB_A=3' - 5"; MB_HT=3' - 0 15/16"; MB_HT+.25"=3' - 1 3/16"; MB_HT-2.75"=2' - 10 3/16"; MB_HT/2=1' - 6 15/32"; Model=QMXHPVP-1X3_Mixing Box; NOZZLE_BOTTOM_ID=1' - 9 3/8"; NOZZLE_BOTTOM_RAD=0' - 10 11/16"; NOZZLE_HEIGHT=3' - 7"; NOZZLE_HEIGHT/7*2=0' - 10 3/4"; NOZZLE_SIZE=15' - 0"; NOZZLE_TOP_OD=1' - 11"; NOZZLE_TOP_RAD=0' - 11 1/2"; NOZZLE_WB/4=0' - 7 3/16"; NOZZLE_WB_OD=3' - 0"; NOZZLE_WB_RAD=1' - 6"; NOZZLE_WB_RAD-2"=1' - 4"; RO=2' - 0 15/16"; RO/2=1' - 0 15/32"; RO2/2=1' - 0 15/32"; TRANSITION_TOP=3' - 9 5/16"; TRIPLE_F+1"=9' - 5"; TRIP_F=9' - 4"; TRIP_G=9' - 3 1/2"; TYPE=1' - 0"; Type Comments=Vari-Plume Laboratory Exhaust Mixed-Flow High Pressure Inline Belt Drive With 1X3 Mixing Box; UNIT_HEIGHT=2' - 9"; UNIT_HEIGHT*.75=2' - 0 3/4"; UNIT_OD=1' - 11 1/2"; UNIT_RAD+((A/2)+.25")=2' - 4"; UNIT_RAD+((A/2)+.25")+4"=2' - 8"; UNIT_RADIUS=0' - 11 3/4"; UNIT_RADIUS*.6=0' - 10 9/16"; UNIT_RADIUS+4"=1' - 3 3/4"
- 165_QMXHPVP-9H-1X3_Mixing_Box: (A/2)+.25"=1' - 4 1/4"; (A/2)-2"=1' - 2"; (NOZZLE_HEIGHT-(NOZZLE_HEIGHT/8*2))/2=0' - 10 1/2"; (NOZZLE_WB_OD-NOZZLE_TOP_OD)/2=0' - 2 3/8"; -A=-2' - 8"; A=2' - 8"; A+.5=2' - 8 1/2"; A/2=1' - 4"; B=7' - 5"; B/2=3' - 8 1/2"; C=3' - 8"; C/2=1' - 10"; DUAL_F=6' - 0 1/4"; DUAL_F+1"=6' - 1 1/4"; DUAL_G=5' - 11 5/16"; E=2' - 7 1/8"; GA=0' - 0 3/32"; LONG_RO=8' - 9 1/4"; MB_A=3' - 5"; MB_HT=3' - 0 15/16"; MB_HT+.25"=3' - 1 3/16"; MB_HT-2.75"=2' - 10 3/16"; MB_HT/2=1' - 6 15/32"; Model=QMXHPVP-1X3_Mixing Box; NOZZLE_BOTTOM_ID=1' - 0 13/16"; NOZZLE_BOTTOM_RAD=0' - 6 13/32"; NOZZLE_HEIGHT=2' - 4"; NOZZLE_HEIGHT/7*2=0' - 7"; NOZZLE_SIZE=9' - 0"; NOZZLE_TOP_OD=1' - 1 1/2"; NOZZLE_TOP_RAD=0' - 6 3/4"; NOZZLE_WB/4=0' - 4 19/32"; NOZZLE_WB_OD=1' - 11"; NOZZLE_WB_RAD=0' - 11 1/2"; NOZZLE_WB_RAD-2"=0' - 9 1/2"; RO=2' - 0 15/16"; RO/2=1' - 0 15/32"; RO2/2=1' - 0 15/32"; TRANSITION_TOP=5' - 1 1/4"; TRIPLE_F+1"=9' - 5"; TRIP_F=9' - 4"; TRIP_G=9' - 3 1/2"; TYPE=1' - 0"; Type Comments=Vari-Plume Laboratory Exhaust Mixed-Flow High Pressure Inline Belt Drive With 1X3 Mixing Box; UNIT_HEIGHT=2' - 9"; UNIT_HEIGHT*.75=2' - 0 3/4"; UNIT_OD=1' - 11 1/2"; UNIT_RAD+((A/2)+.25")=2' - 4"; UNIT_RAD+((A/2)+.25")+4"=2' - 8"; UNIT_RADIUS=0' - 11 3/4"; UNIT_RADIUS*.6=0' - 10 9/16"; UNIT_RADIUS+4"=1' - 3 3/4"
- 165_QMXHPVP-9L-1X3_Mixing_Box: (A/2)+.25"=1' - 4 1/4"; (A/2)-2"=1' - 2"; (NOZZLE_HEIGHT-(NOZZLE_HEIGHT/8*2))/2=0' - 10 1/2"; (NOZZLE_WB_OD-NOZZLE_TOP_OD)/2=0' - 2 3/8"; -A=-2' - 8"; A=2' - 8"; A+.5=2' - 8 1/2"; A/2=1' - 4"; B=7' - 5"; B/2=3' - 8 1/2"; C=3' - 8"; C/2=1' - 10"; DUAL_F=6' - 0 1/4"; DUAL_F+1"=6' - 1 1/4"; DUAL_G=5' - 11 5/16"; E=2' - 7 1/8"; GA=0' - 0 3/32"; LONG_RO=8' - 9 1/4"; MB_A=3' - 5"; MB_HT=3' - 0 15/16"; MB_HT+.25"=3' - 1 3/16"; MB_HT-2.75"=2' - 10 3/16"; MB_HT/2=1' - 6 15/32"; Model=QMXHPVP-1X3_Mixing Box; NOZZLE_BOTTOM_ID=1' - 0 13/16"; NOZZLE_BOTTOM_RAD=0' - 6 13/32"; NOZZLE_HEIGHT=2' - 4"; NOZZLE_HEIGHT/7*2=0' - 7"; NOZZLE_SIZE=9' - 0"; NOZZLE_TOP_OD=1' - 1 1/2"; NOZZLE_TOP_RAD=0' - 6 3/4"; NOZZLE_WB/4=0' - 4 19/32"; NOZZLE_WB_OD=1' - 11"; NOZZLE_WB_RAD=0' - 11 1/2"; NOZZLE_WB_RAD-2"=0' - 9 1/2"; RO=2' - 0 15/16"; RO/2=1' - 0 15/32"; RO2/2=1' - 0 15/32"; TRANSITION_TOP=5' - 1 1/4"; TRIPLE_F+1"=9' - 5"; TRIP_F=9' - 4"; TRIP_G=9' - 3 1/2"; TYPE=1' - 0"; Type Comments=Vari-Plume Laboratory Exhaust Mixed-Flow High Pressure Inline Belt Drive With 1X3 Mixing Box; UNIT_HEIGHT=2' - 9"; UNIT_HEIGHT*.75=2' - 0 3/4"; UNIT_OD=1' - 11 1/2"; UNIT_RAD+((A/2)+.25")=2' - 4"; UNIT_RAD+((A/2)+.25")+4"=2' - 8"; UNIT_RADIUS=0' - 11 3/4"; UNIT_RADIUS*.6=0' - 10 9/16"; UNIT_RADIUS+4"=1' - 3 3/4"
- 180_QMXHPVP-12H-1X3_Mixing_Box: (A/2)+.25"=1' - 5 1/4"; (A/2)-2"=1' - 3"; (NOZZLE_HEIGHT-(NOZZLE_HEIGHT/8*2))/2=1' - 0"; (NOZZLE_WB_OD-NOZZLE_TOP_OD)/2=0' - 2 1/8"; -A=-2' - 10"; A=2' - 10"; A+.5=2' - 10 1/2"; A/2=1' - 5"; B=8' - 2"; B/2=4' - 1"; C=3' - 10"; C/2=1' - 11"; DUAL_F=7' - 0 1/4"; DUAL_F+1"=7' - 1 1/4"; DUAL_G=6' - 11 5/16"; E=2' - 9 1/8"; GA=0' - 0 3/32"; LONG_RO=10' - 7 1/4"; MB_A=3' - 8"; MB_HT=3' - 1 11/16"; MB_HT+.25"=3' - 1 15/16"; MB_HT-2.75"=2' - 10 15/16"; MB_HT/2=1' - 6 27/32"; Model=QMXHPVP-1X3_Mixing Box; NOZZLE_BOTTOM_ID=1' - 5 1/16"; NOZZLE_BOTTOM_RAD=0' - 8 17/32"; NOZZLE_HEIGHT=2' - 8"; NOZZLE_HEIGHT/7*2=0' - 8"; NOZZLE_SIZE=12' - 0"; NOZZLE_TOP_OD=1' - 7 1/2"; NOZZLE_TOP_RAD=0' - 9 3/4"; NOZZLE_WB/4=0' - 5 19/32"; NOZZLE_WB_OD=2' - 4"; NOZZLE_WB_RAD=1' - 2"; NOZZLE_WB_RAD-2"=1' - 0"; RO=2' - 2 15/16"; RO/2=1' - 1 15/32"; RO2/2=1' - 1 15/32"; TRANSITION_TOP=4' - 11 1/16"; TRIPLE_F+1"=11' - 3"; TRIP_F=11' - 2"; TRIP_G=11' - 1 1/2"; TYPE=1' - 0"; Type Comments=Vari-Plume Laboratory Exhaust Mixed-Flow High Pressure Inline Belt Drive With 1X3 Mixing Box; UNIT_HEIGHT=2' - 11"; UNIT_HEIGHT*.75=2' - 2 1/4"; UNIT_OD=2' - 1 5/8"; UNIT_RAD+((A/2)+.25")=2' - 6 1/16"; UNIT_RAD+((A/2)+.25")+4"=2' - 10 1/16"; UNIT_RADIUS=1' - 0 13/16"; UNIT_RADIUS*.6=0' - 11 17/32"; UNIT_RADIUS+4"=1' - 4 13/16"
- 180_QMXHPVP-12L-1X3_Mixing_Box: (A/2)+.25"=1' - 5 1/4"; (A/2)-2"=1' - 3"; (NOZZLE_HEIGHT-(NOZZLE_HEIGHT/8*2))/2=1' - 0"; (NOZZLE_WB_OD-NOZZLE_TOP_OD)/2=0' - 2 1/8"; -A=-2' - 10"; A=2' - 10"; A+.5=2' - 10 1/2"; A/2=1' - 5"; B=8' - 2"; B/2=4' - 1"; C=3' - 10"; C/2=1' - 11"; DUAL_F=7' - 0 1/4"; DUAL_F+1"=7' - 1 1/4"; DUAL_G=6' - 11 5/16"; E=2' - 9 1/8"; GA=0' - 0 3/32"; LONG_RO=10' - 7 1/4"; MB_A=3' - 8"; MB_HT=3' - 1 11/16"; MB_HT+.25"=3' - 1 15/16"; MB_HT-2.75"=2' - 10 15/16"; MB_HT/2=1' - 6 27/32"; Model=QMXHPVP-1X3_Mixing Box; NOZZLE_BOTTOM_ID=1' - 5 1/16"; NOZZLE_BOTTOM_RAD=0' - 8 17/32"; NOZZLE_HEIGHT=2' - 8"; NOZZLE_HEIGHT/7*2=0' - 8"; NOZZLE_SIZE=12' - 0"; NOZZLE_TOP_OD=1' - 7 1/2"; NOZZLE_TOP_RAD=0' - 9 3/4"; NOZZLE_WB/4=0' - 5 19/32"; NOZZLE_WB_OD=2' - 4"; NOZZLE_WB_RAD=1' - 2"; NOZZLE_WB_RAD-2"=1' - 0"; RO=2' - 2 15/16"; RO/2=1' - 1 15/32"; RO2/2=1' - 1 15/32"; TRANSITION_TOP=4' - 11 1/16"; TRIPLE_F+1"=11' - 3"; TRIP_F=11' - 2"; TRIP_G=11' - 1 1/2"; TYPE=1' - 0"; Type Comments=Vari-Plume Laboratory Exhaust Mixed-Flow High Pressure Inline Belt Drive With 1X3 Mixing Box; UNIT_HEIGHT=2' - 11"; UNIT_HEIGHT*.75=2' - 2 1/4"; UNIT_OD=2' - 1 5/8"; UNIT_RAD+((A/2)+.25")=2' - 6 1/16"; UNIT_RAD+((A/2)+.25")+4"=2' - 10 1/16"; UNIT_RADIUS=1' - 0 13/16"; UNIT_RADIUS*.6=0' - 11 17/32"; UNIT_RADIUS+4"=1' - 4 13/16"
- 180_QMXHPVP-15H-1X3_Mixing_Box: (A/2)+.25"=1' - 5 1/4"; (A/2)-2"=1' - 3"; (NOZZLE_HEIGHT-(NOZZLE_HEIGHT/8*2))/2=1' - 4 1/8"; (NOZZLE_WB_OD-NOZZLE_TOP_OD)/2=0' - 3 1/4"; -A=-2' - 10"; A=2' - 10"; A+.5=2' - 10 1/2"; A/2=1' - 5"; B=8' - 2"; B/2=4' - 1"; C=3' - 10"; C/2=1' - 11"; DUAL_F=7' - 0 1/4"; DUAL_F+1"=7' - 1 1/4"; DUAL_G=6' - 11 5/16"; E=2' - 9 1/8"; GA=0' - 0 3/32"; LONG_RO=10' - 7 1/4"; MB_A=3' - 8"; MB_HT=3' - 1 11/16"; MB_HT+.25"=3' - 1 15/16"; MB_HT-2.75"=2' - 10 15/16"; MB_HT/2=1' - 6 27/32"; Model=QMXHPVP-1X3_Mixing Box; NOZZLE_BOTTOM_ID=1' - 9 3/8"; NOZZLE_BOTTOM_RAD=0' - 10 11/16"; NOZZLE_HEIGHT=3' - 7"; NOZZLE_HEIGHT/7*2=0' - 10 3/4"; NOZZLE_SIZE=15' - 0"; NOZZLE_TOP_OD=1' - 11"; NOZZLE_TOP_RAD=0' - 11 1/2"; NOZZLE_WB/4=0' - 7 3/16"; NOZZLE_WB_OD=3' - 0"; NOZZLE_WB_RAD=1' - 6"; NOZZLE_WB_RAD-2"=1' - 4"; RO=2' - 2 15/16"; RO/2=1' - 1 15/32"; RO2/2=1' - 1 15/32"; TRANSITION_TOP=4' - 3 1/8"; TRIPLE_F+1"=11' - 3"; TRIP_F=11' - 2"; TRIP_G=11' - 1 1/2"; TYPE=1' - 0"; Type Comments=Vari-Plume Laboratory Exhaust Mixed-Flow High Pressure Inline Belt Drive With 1X3 Mixing Box; UNIT_HEIGHT=2' - 11"; UNIT_HEIGHT*.75=2' - 2 1/4"; UNIT_OD=2' - 1 5/8"; UNIT_RAD+((A/2)+.25")=2' - 6 1/16"; UNIT_RAD+((A/2)+.25")+4"=2' - 10 1/16"; UNIT_RADIUS=1' - 0 13/16"; UNIT_RADIUS*.6=0' - 11 17/32"; UNIT_RADIUS+4"=1' - 4 13/16"
- 180_QMXHPVP-15L-1X3_Mixing_Box: (A/2)+.25"=1' - 5 1/4"; (A/2)-2"=1' - 3"; (NOZZLE_HEIGHT-(NOZZLE_HEIGHT/8*2))/2=1' - 4 1/8"; (NOZZLE_WB_OD-NOZZLE_TOP_OD)/2=0' - 3 1/4"; -A=-2' - 10"; A=2' - 10"; A+.5=2' - 10 1/2"; A/2=1' - 5"; B=8' - 2"; B/2=4' - 1"; C=3' - 10"; C/2=1' - 11"; DUAL_F=7' - 0 1/4"; DUAL_F+1"=7' - 1 1/4"; DUAL_G=6' - 11 5/16"; E=2' - 9 1/8"; GA=0' - 0 3/32"; LONG_RO=10' - 7 1/4"; MB_A=3' - 8"; MB_HT=3' - 1 11/16"; MB_HT+.25"=3' - 1 15/16"; MB_HT-2.75"=2' - 10 15/16"; MB_HT/2=1' - 6 27/32"; Model=QMXHPVP-1X3_Mixing Box; NOZZLE_BOTTOM_ID=1' - 9 3/8"; NOZZLE_BOTTOM_RAD=0' - 10 11/16"; NOZZLE_HEIGHT=3' - 7"; NOZZLE_HEIGHT/7*2=0' - 10 3/4"; NOZZLE_SIZE=15' - 0"; NOZZLE_TOP_OD=1' - 11"; NOZZLE_TOP_RAD=0' - 11 1/2"; NOZZLE_WB/4=0' - 7 3/16"; NOZZLE_WB_OD=3' - 0"; NOZZLE_WB_RAD=1' - 6"; NOZZLE_WB_RAD-2"=1' - 4"; RO=2' - 2 15/16"; RO/2=1' - 1 15/32"; RO2/2=1' - 1 15/32"; TRANSITION_TOP=4' - 3 1/8"; TRIPLE_F+1"=11' - 3"; TRIP_F=11' - 2"; TRIP_G=11' - 1 1/2"; TYPE=1' - 0"; Type Comments=Vari-Plume Laboratory Exhaust Mixed-Flow High Pressure Inline Belt Drive With 1X3 Mixing Box; UNIT_HEIGHT=2' - 11"; UNIT_HEIGHT*.75=2' - 2 1/4"; UNIT_OD=2' - 1 5/8"; UNIT_RAD+((A/2)+.25")=2' - 6 1/16"; UNIT_RAD+((A/2)+.25")+4"=2' - 10 1/16"; UNIT_RADIUS=1' - 0 13/16"; UNIT_RADIUS*.6=0' - 11 17/32"; UNIT_RADIUS+4"=1' - 4 13/16"
- 180_QMXHPVP-18H-1X3_Mixing_Box: (A/2)+.25"=1' - 5 1/4"; (A/2)-2"=1' - 3"; (NOZZLE_HEIGHT-(NOZZLE_HEIGHT/8*2))/2=1' - 6"; (NOZZLE_WB_OD-NOZZLE_TOP_OD)/2=0' - 3 7/8"; -A=-2' - 10"; A=2' - 10"; A+.5=2' - 10 1/2"; A/2=1' - 5"; B=8' - 2"; B/2=4' - 1"; C=3' - 10"; C/2=1' - 11"; DUAL_F=7' - 0 1/4"; DUAL_F+1"=7' - 1 1/4"; DUAL_G=6' - 11 5/16"; E=2' - 9 1/8"; GA=0' - 0 3/32"; LONG_RO=10' - 7 1/4"; MB_A=3' - 8"; MB_HT=3' - 1 11/16"; MB_HT+.25"=3' - 1 15/16"; MB_HT-2.75"=2' - 10 15/16"; MB_HT/2=1' - 6 27/32"; Model=QMXHPVP-1X3_Mixing Box; NOZZLE_BOTTOM_ID=2' - 1 5/8"; NOZZLE_BOTTOM_RAD=1' - 0 13/16"; NOZZLE_HEIGHT=4' - 0"; NOZZLE_HEIGHT/7*2=1' - 0"; NOZZLE_SIZE=18' - 0"; NOZZLE_TOP_OD=2' - 3 1/2"; NOZZLE_TOP_RAD=1' - 1 3/4"; NOZZLE_WB/4=0' - 8 19/32"; NOZZLE_WB_OD=3' - 7"; NOZZLE_WB_RAD=1' - 9 1/2"; NOZZLE_WB_RAD-2"=1' - 7 1/2"; RO=2' - 2 15/16"; RO/2=1' - 1 15/32"; RO2/2=1' - 1 15/32"; TRANSITION_TOP=4' - 0 1/2"; TRIPLE_F+1"=11' - 3"; TRIP_F=11' - 2"; TRIP_G=11' - 1 1/2"; TYPE=1' - 0"; Type Comments=Vari-Plume Laboratory Exhaust Mixed-Flow High Pressure Inline Belt Drive With 1X3 Mixing Box; UNIT_HEIGHT=2' - 11"; UNIT_HEIGHT*.75=2' - 2 1/4"; UNIT_OD=2' - 1 5/8"; UNIT_RAD+((A/2)+.25")=2' - 6 1/16"; UNIT_RAD+((A/2)+.25")+4"=2' - 10 1/16"; UNIT_RADIUS=1' - 0 13/16"; UNIT_RADIUS*.6=0' - 11 17/32"; UNIT_RADIUS+4"=1' - 4 13/16"
- 180_QMXHPVP-18L-1X3_Mixing_Box: (A/2)+.25"=1' - 5 1/4"; (A/2)-2"=1' - 3"; (NOZZLE_HEIGHT-(NOZZLE_HEIGHT/8*2))/2=1' - 6"; (NOZZLE_WB_OD-NOZZLE_TOP_OD)/2=0' - 3 7/8"; -A=-2' - 10"; A=2' - 10"; A+.5=2' - 10 1/2"; A/2=1' - 5"; B=8' - 2"; B/2=4' - 1"; C=3' - 10"; C/2=1' - 11"; DUAL_F=7' - 0 1/4"; DUAL_F+1"=7' - 1 1/4"; DUAL_G=6' - 11 5/16"; E=2' - 9 1/8"; GA=0' - 0 3/32"; LONG_RO=10' - 7 1/4"; MB_A=3' - 8"; MB_HT=3' - 1 11/16"; MB_HT+.25"=3' - 1 15/16"; MB_HT-2.75"=2' - 10 15/16"; MB_HT/2=1' - 6 27/32"; Model=QMXHPVP-1X3_Mixing Box; NOZZLE_BOTTOM_ID=2' - 1 5/8"; NOZZLE_BOTTOM_RAD=1' - 0 13/16"; NOZZLE_HEIGHT=4' - 0"; NOZZLE_HEIGHT/7*2=1' - 0"; NOZZLE_SIZE=18' - 0"; NOZZLE_TOP_OD=2' - 3 1/2"; NOZZLE_TOP_RAD=1' - 1 3/4"; NOZZLE_WB/4=0' - 8 19/32"; NOZZLE_WB_OD=3' - 7"; NOZZLE_WB_RAD=1' - 9 1/2"; NOZZLE_WB_RAD-2"=1' - 7 1/2"; RO=2' - 2 15/16"; RO/2=1' - 1 15/32"; RO2/2=1' - 1 15/32"; TRANSITION_TOP=4' - 0 1/2"; TRIPLE_F+1"=11' - 3"; TRIP_F=11' - 2"; TRIP_G=11' - 1 1/2"; TYPE=1' - 0"; Type Comments=Vari-Plume Laboratory Exhaust Mixed-Flow High Pressure Inline Belt Drive With 1X3 Mixing Box; UNIT_HEIGHT=2' - 11"; UNIT_HEIGHT*.75=2' - 2 1/4"; UNIT_OD=2' - 1 5/8"; UNIT_RAD+((A/2)+.25")=2' - 6 1/16"; UNIT_RAD+((A/2)+.25")+4"=2' - 10 1/16"; UNIT_RADIUS=1' - 0 13/16"; UNIT_RADIUS*.6=0' - 11 17/32"; UNIT_RADIUS+4"=1' - 4 13/16"
- 202_QMXHPVP-12H-1X3_Mixing_Box: (A/2)+.25"=1' - 7 1/4"; (A/2)-2"=1' - 5"; (NOZZLE_HEIGHT-(NOZZLE_HEIGHT/8*2))/2=1' - 0"; (NOZZLE_WB_OD-NOZZLE_TOP_OD)/2=0' - 2 1/8"; -A=-3' - 2"; A=3' - 2"; A+.5=3' - 2 1/2"; A/2=1' - 7"; B=8' - 8"; B/2=4' - 4"; C=4' - 2"; C/2=2' - 1"; DUAL_F=7' - 6 1/4"; DUAL_F+1"=7' - 7 1/4"; DUAL_G=7' - 5 1/8"; E=3' - 0 15/16"; GA=0' - 0 3/32"; LONG_RO=11' - 3"; MB_A=4' - 1"; MB_HT=3' - 5 3/16"; MB_HT+.25"=3' - 5 7/16"; MB_HT-2.75"=3' - 2 7/16"; MB_HT/2=1' - 8 19/32"; Model=QMXHPVP-1X3_Mixing Box; NOZZLE_BOTTOM_ID=1' - 5 1/16"; NOZZLE_BOTTOM_RAD=0' - 8 17/32"; NOZZLE_HEIGHT=2' - 8"; NOZZLE_HEIGHT/7*2=0' - 8"; NOZZLE_SIZE=12' - 0"; NOZZLE_TOP_OD=1' - 7 1/2"; NOZZLE_TOP_RAD=0' - 9 3/4"; NOZZLE_WB/4=0' - 5 19/32"; NOZZLE_WB_OD=2' - 4"; NOZZLE_WB_RAD=1' - 2"; NOZZLE_WB_RAD-2"=1' - 0"; RO=2' - 6 3/4"; RO/2=1' - 3 3/8"; RO2/2=1' - 3 3/8"; TRANSITION_TOP=5' - 7 9/16"; TRIPLE_F+1"=11' - 11"; TRIP_F=11' - 10"; TRIP_G=11' - 9 1/4"; TYPE=1' - 0"; Type Comments=Vari-Plume Laboratory Exhaust Mixed-Flow High Pressure Inline Belt Drive With 1X3 Mixing Box; UNIT_HEIGHT=3' - 1 1/2"; UNIT_HEIGHT*.75=2' - 4 1/8"; UNIT_OD=2' - 4 3/4"; UNIT_RAD+((A/2)+.25")=2' - 9 5/8"; UNIT_RAD+((A/2)+.25")+4"=3' - 1 5/8"; UNIT_RADIUS=1' - 2 3/8"; UNIT_RADIUS*.6=1' - 0 15/16"; UNIT_RADIUS+4"=1' - 6 3/8"
- 202_QMXHPVP-12L-1X3_Mixing_Box: (A/2)+.25"=1' - 7 1/4"; (A/2)-2"=1' - 5"; (NOZZLE_HEIGHT-(NOZZLE_HEIGHT/8*2))/2=1' - 0"; (NOZZLE_WB_OD-NOZZLE_TOP_OD)/2=0' - 2 1/8"; -A=-3' - 2"; A=3' - 2"; A+.5=3' - 2 1/2"; A/2=1' - 7"; B=8' - 8"; B/2=4' - 4"; C=4' - 2"; C/2=2' - 1"; DUAL_F=7' - 6 1/4"; DUAL_F+1"=7' - 7 1/4"; DUAL_G=7' - 5 1/8"; E=3' - 0 15/16"; GA=0' - 0 3/32"; LONG_RO=11' - 3"; MB_A=4' - 1"; MB_HT=3' - 5 3/16"; MB_HT+.25"=3' - 5 7/16"; MB_HT-2.75"=3' - 2 7/16"; MB_HT/2=1' - 8 19/32"; Model=QMXHPVP-1X3_Mixing Box; NOZZLE_BOTTOM_ID=1' - 5 1/16"; NOZZLE_BOTTOM_RAD=0' - 8 17/32"; NOZZLE_HEIGHT=2' - 8"; NOZZLE_HEIGHT/7*2=0' - 8"; NOZZLE_SIZE=12' - 0"; NOZZLE_TOP_OD=1' - 7 1/2"; NOZZLE_TOP_RAD=0' - 9 3/4"; NOZZLE_WB/4=0' - 5 19/32"; NOZZLE_WB_OD=2' - 4"; NOZZLE_WB_RAD=1' - 2"; NOZZLE_WB_RAD-2"=1' - 0"; RO=2' - 6 3/4"; RO/2=1' - 3 3/8"; RO2/2=1' - 3 3/8"; TRANSITION_TOP=5' - 7 9/16"; TRIPLE_F+1"=11' - 11"; TRIP_F=11' - 10"; TRIP_G=11' - 9 1/4"; TYPE=1' - 0"; Type Comments=Vari-Plume Laboratory Exhaust Mixed-Flow High Pressure Inline Belt Drive With 1X3 Mixing Box; UNIT_HEIGHT=3' - 1 1/2"; UNIT_HEIGHT*.75=2' - 4 1/8"; UNIT_OD=2' - 4 3/4"; UNIT_RAD+((A/2)+.25")=2' - 9 5/8"; UNIT_RAD+((A/2)+.25")+4"=3' - 1 5/8"; UNIT_RADIUS=1' - 2 3/8"; UNIT_RADIUS*.6=1' - 0 15/16"; UNIT_RADIUS+4"=1' - 6 3/8"
- 202_QMXHPVP-15H-1X3_Mixing_Box: (A/2)+.25"=1' - 7 1/4"; (A/2)-2"=1' - 5"; (NOZZLE_HEIGHT-(NOZZLE_HEIGHT/8*2))/2=1' - 4 1/8"; (NOZZLE_WB_OD-NOZZLE_TOP_OD)/2=0' - 3 1/4"; -A=-3' - 2"; A=3' - 2"; A+.5=3' - 2 1/2"; A/2=1' - 7"; B=8' - 8"; B/2=4' - 4"; C=4' - 2"; C/2=2' - 1"; DUAL_F=7' - 6 1/4"; DUAL_F+1"=7' - 7 1/4"; DUAL_G=7' - 5 1/8"; E=3' - 0 15/16"; GA=0' - 0 3/32"; LONG_RO=11' - 3"; MB_A=4' - 1"; MB_HT=3' - 5 3/16"; MB_HT+.25"=3' - 5 7/16"; MB_HT-2.75"=3' - 2 7/16"; MB_HT/2=1' - 8 19/32"; Model=QMXHPVP-1X3_Mixing Box; NOZZLE_BOTTOM_ID=1' - 9 3/8"; NOZZLE_BOTTOM_RAD=0' - 10 11/16"; NOZZLE_HEIGHT=3' - 7"; NOZZLE_HEIGHT/7*2=0' - 10 3/4"; NOZZLE_SIZE=15' - 0"; NOZZLE_TOP_OD=1' - 11"; NOZZLE_TOP_RAD=0' - 11 1/2"; NOZZLE_WB/4=0' - 7 3/16"; NOZZLE_WB_OD=3' - 0"; NOZZLE_WB_RAD=1' - 6"; NOZZLE_WB_RAD-2"=1' - 4"; RO=2' - 6 3/4"; RO/2=1' - 3 3/8"; RO2/2=1' - 3 3/8"; TRANSITION_TOP=4' - 11 5/8"; TRIPLE_F+1"=11' - 11"; TRIP_F=11' - 10"; TRIP_G=11' - 9 1/4"; TYPE=1' - 0"; Type Comments=Vari-Plume Laboratory Exhaust Mixed-Flow High Pressure Inline Belt Drive With 1X3 Mixing Box; UNIT_HEIGHT=3' - 1 1/2"; UNIT_HEIGHT*.75=2' - 4 1/8"; UNIT_OD=2' - 4 3/4"; UNIT_RAD+((A/2)+.25")=2' - 9 5/8"; UNIT_RAD+((A/2)+.25")+4"=3' - 1 5/8"; UNIT_RADIUS=1' - 2 3/8"; UNIT_RADIUS*.6=1' - 0 15/16"; UNIT_RADIUS+4"=1' - 6 3/8"
- 202_QMXHPVP-15L-1X3_Mixing_Box: (A/2)+.25"=1' - 7 1/4"; (A/2)-2"=1' - 5"; (NOZZLE_HEIGHT-(NOZZLE_HEIGHT/8*2))/2=1' - 4 1/8"; (NOZZLE_WB_OD-NOZZLE_TOP_OD)/2=0' - 3 1/4"; -A=-3' - 2"; A=3' - 2"; A+.5=3' - 2 1/2"; A/2=1' - 7"; B=8' - 8"; B/2=4' - 4"; C=4' - 2"; C/2=2' - 1"; DUAL_F=7' - 6 1/4"; DUAL_F+1"=7' - 7 1/4"; DUAL_G=7' - 5 1/8"; E=3' - 0 15/16"; GA=0' - 0 3/32"; LONG_RO=11' - 3"; MB_A=4' - 1"; MB_HT=3' - 5 3/16"; MB_HT+.25"=3' - 5 7/16"; MB_HT-2.75"=3' - 2 7/16"; MB_HT/2=1' - 8 19/32"; Model=QMXHPVP-1X3_Mixing Box; NOZZLE_BOTTOM_ID=1' - 9 3/8"; NOZZLE_BOTTOM_RAD=0' - 10 11/16"; NOZZLE_HEIGHT=3' - 7"; NOZZLE_HEIGHT/7*2=0' - 10 3/4"; NOZZLE_SIZE=15' - 0"; NOZZLE_TOP_OD=1' - 11"; NOZZLE_TOP_RAD=0' - 11 1/2"; NOZZLE_WB/4=0' - 7 3/16"; NOZZLE_WB_OD=3' - 0"; NOZZLE_WB_RAD=1' - 6"; NOZZLE_WB_RAD-2"=1' - 4"; RO=2' - 6 3/4"; RO/2=1' - 3 3/8"; RO2/2=1' - 3 3/8"; TRANSITION_TOP=4' - 11 5/8"; TRIPLE_F+1"=11' - 11"; TRIP_F=11' - 10"; TRIP_G=11' - 9 1/4"; TYPE=1' - 0"; Type Comments=Vari-Plume Laboratory Exhaust Mixed-Flow High Pressure Inline Belt Drive With 1X3 Mixing Box; UNIT_HEIGHT=3' - 1 1/2"; UNIT_HEIGHT*.75=2' - 4 1/8"; UNIT_OD=2' - 4 3/4"; UNIT_RAD+((A/2)+.25")=2' - 9 5/8"; UNIT_RAD+((A/2)+.25")+4"=3' - 1 5/8"; UNIT_RADIUS=1' - 2 3/8"; UNIT_RADIUS*.6=1' - 0 15/16"; UNIT_RADIUS+4"=1' - 6 3/8"
- 202_QMXHPVP-18H-1X3_Mixing_Box: (A/2)+.25"=1' - 7 1/4"; (A/2)-2"=1' - 5"; (NOZZLE_HEIGHT-(NOZZLE_HEIGHT/8*2))/2=1' - 6"; (NOZZLE_WB_OD-NOZZLE_TOP_OD)/2=0' - 3 7/8"; -A=-3' - 2"; A=3' - 2"; A+.5=3' - 2 1/2"; A/2=1' - 7"; B=8' - 8"; B/2=4' - 4"; C=4' - 2"; C/2=2' - 1"; DUAL_F=7' - 6 1/4"; DUAL_F+1"=7' - 7 1/4"; DUAL_G=7' - 5 1/8"; E=3' - 0 15/16"; GA=0' - 0 3/32"; LONG_RO=11' - 3"; MB_A=4' - 1"; MB_HT=3' - 5 3/16"; MB_HT+.25"=3' - 5 7/16"; MB_HT-2.75"=3' - 2 7/16"; MB_HT/2=1' - 8 19/32"; Model=QMXHPVP-1X3_Mixing Box; NOZZLE_BOTTOM_ID=2' - 1 5/8"; NOZZLE_BOTTOM_RAD=1' - 0 13/16"; NOZZLE_HEIGHT=4' - 0"; NOZZLE_HEIGHT/7*2=1' - 0"; NOZZLE_SIZE=18' - 0"; NOZZLE_TOP_OD=2' - 3 1/2"; NOZZLE_TOP_RAD=1' - 1 3/4"; NOZZLE_WB/4=0' - 8 19/32"; NOZZLE_WB_OD=3' - 7"; NOZZLE_WB_RAD=1' - 9 1/2"; NOZZLE_WB_RAD-2"=1' - 7 1/2"; RO=2' - 6 3/4"; RO/2=1' - 3 3/8"; RO2/2=1' - 3 3/8"; TRANSITION_TOP=4' - 3 5/8"; TRIPLE_F+1"=11' - 11"; TRIP_F=11' - 10"; TRIP_G=11' - 9 1/4"; TYPE=1' - 0"; Type Comments=Vari-Plume Laboratory Exhaust Mixed-Flow High Pressure Inline Belt Drive With 1X3 Mixing Box; UNIT_HEIGHT=3' - 1 1/2"; UNIT_HEIGHT*.75=2' - 4 1/8"; UNIT_OD=2' - 4 3/4"; UNIT_RAD+((A/2)+.25")=2' - 9 5/8"; UNIT_RAD+((A/2)+.25")+4"=3' - 1 5/8"; UNIT_RADIUS=1' - 2 3/8"; UNIT_RADIUS*.6=1' - 0 15/16"; UNIT_RADIUS+4"=1' - 6 3/8"
- 202_QMXHPVP-18L-1X3_Mixing_Box: (A/2)+.25"=1' - 7 1/4"; (A/2)-2"=1' - 5"; (NOZZLE_HEIGHT-(NOZZLE_HEIGHT/8*2))/2=1' - 6"; (NOZZLE_WB_OD-NOZZLE_TOP_OD)/2=0' - 3 7/8"; -A=-3' - 2"; A=3' - 2"; A+.5=3' - 2 1/2"; A/2=1' - 7"; B=8' - 8"; B/2=4' - 4"; C=4' - 2"; C/2=2' - 1"; DUAL_F=7' - 6 1/4"; DUAL_F+1"=7' - 7 1/4"; DUAL_G=7' - 5 1/8"; E=3' - 0 15/16"; GA=0' - 0 3/32"; LONG_RO=11' - 3"; MB_A=4' - 1"; MB_HT=3' - 5 3/16"; MB_HT+.25"=3' - 5 7/16"; MB_HT-2.75"=3' - 2 7/16"; MB_HT/2=1' - 8 19/32"; Model=QMXHPVP-1X3_Mixing Box; NOZZLE_BOTTOM_ID=2' - 1 5/8"; NOZZLE_BOTTOM_RAD=1' - 0 13/16"; NOZZLE_HEIGHT=4' - 0"; NOZZLE_HEIGHT/7*2=1' - 0"; NOZZLE_SIZE=18' - 0"; NOZZLE_TOP_OD=2' - 3 1/2"; NOZZLE_TOP_RAD=1' - 1 3/4"; NOZZLE_WB/4=0' - 8 19/32"; NOZZLE_WB_OD=3' - 7"; NOZZLE_WB_RAD=1' - 9 1/2"; NOZZLE_WB_RAD-2"=1' - 7 1/2"; RO=2' - 6 3/4"; RO/2=1' - 3 3/8"; RO2/2=1' - 3 3/8"; TRANSITION_TOP=4' - 3 5/8"; TRIPLE_F+1"=11' - 11"; TRIP_F=11' - 10"; TRIP_G=11' - 9 1/4"; TYPE=1' - 0"; Type Comments=Vari-Plume Laboratory Exhaust Mixed-Flow High Pressure Inline Belt Drive With 1X3 Mixing Box; UNIT_HEIGHT=3' - 1 1/2"; UNIT_HEIGHT*.75=2' - 4 1/8"; UNIT_OD=2' - 4 3/4"; UNIT_RAD+((A/2)+.25")=2' - 9 5/8"; UNIT_RAD+((A/2)+.25")+4"=3' - 1 5/8"; UNIT_RADIUS=1' - 2 3/8"; UNIT_RADIUS*.6=1' - 0 15/16"; UNIT_RADIUS+4"=1' - 6 3/8"
- 225_QMXHPVP-12H-1X3_Mixing_Box: (A/2)+.25"=1' - 9 1/4"; (A/2)-2"=1' - 7"; (NOZZLE_HEIGHT-(NOZZLE_HEIGHT/8*2))/2=1' - 0"; (NOZZLE_WB_OD-NOZZLE_TOP_OD)/2=0' - 2 1/8"; -A=-3' - 6"; A=3' - 6"; A+.5=3' - 6 1/2"; A/2=1' - 9"; B=9' - 5"; B/2=4' - 8 1/2"; C=4' - 8"; C/2=2' - 4"; DUAL_F=7' - 9 1/4"; DUAL_F+1"=7' - 10 1/4"; DUAL_G=7' - 8 1/8"; E=3' - 4 15/16"; GA=0' - 0 3/32"; LONG_RO=11' - 5"; MB_A=4' - 6"; MB_HT=3' - 7 3/16"; MB_HT+.25"=3' - 7 7/16"; MB_HT-2.75"=3' - 4 7/16"; MB_HT/2=1' - 9 19/32"; Model=QMXHPVP-1X3_Mixing Box; NOZZLE_BOTTOM_ID=1' - 5 1/16"; NOZZLE_BOTTOM_RAD=0' - 8 17/32"; NOZZLE_HEIGHT=2' - 8"; NOZZLE_HEIGHT/7*2=0' - 8"; NOZZLE_SIZE=12' - 0"; NOZZLE_TOP_OD=1' - 7 1/2"; NOZZLE_TOP_RAD=0' - 9 3/4"; NOZZLE_WB/4=0' - 5 19/32"; NOZZLE_WB_OD=2' - 4"; NOZZLE_WB_RAD=1' - 2"; NOZZLE_WB_RAD-2"=1' - 0"; RO=2' - 10 3/4"; RO/2=1' - 5 3/8"; RO2/2=1' - 5 3/8"; TRANSITION_TOP=6' - 5 1/16"; TRIPLE_F+1"=12' - 1"; TRIP_F=12' - 0"; TRIP_G=11' - 11 1/4"; TYPE=1' - 0"; Type Comments=Vari-Plume Laboratory Exhaust Mixed-Flow High Pressure Inline Belt Drive With 1X3 Mixing Box; UNIT_HEIGHT=3' - 5"; UNIT_HEIGHT*.75=2' - 6 3/4"; UNIT_OD=2' - 7 15/16"; UNIT_RAD+((A/2)+.25")=3' - 1 7/32"; UNIT_RAD+((A/2)+.25")+4"=3' - 5 7/32"; UNIT_RADIUS=1' - 3 31/32"; UNIT_RADIUS*.6=1' - 2 3/8"; UNIT_RADIUS+4"=1' - 7 31/32"
- 225_QMXHPVP-12L-1X3_Mixing_Box: (A/2)+.25"=1' - 9 1/4"; (A/2)-2"=1' - 7"; (NOZZLE_HEIGHT-(NOZZLE_HEIGHT/8*2))/2=1' - 0"; (NOZZLE_WB_OD-NOZZLE_TOP_OD)/2=0' - 2 1/8"; -A=-3' - 6"; A=3' - 6"; A+.5=3' - 6 1/2"; A/2=1' - 9"; B=9' - 5"; B/2=4' - 8 1/2"; C=4' - 8"; C/2=2' - 4"; DUAL_F=7' - 9 1/4"; DUAL_F+1"=7' - 10 1/4"; DUAL_G=7' - 8 1/8"; E=3' - 4 15/16"; GA=0' - 0 3/32"; LONG_RO=11' - 5"; MB_A=4' - 6"; MB_HT=3' - 7 3/16"; MB_HT+.25"=3' - 7 7/16"; MB_HT-2.75"=3' - 4 7/16"; MB_HT/2=1' - 9 19/32"; Model=QMXHPVP-1X3_Mixing Box; NOZZLE_BOTTOM_ID=1' - 5 1/16"; NOZZLE_BOTTOM_RAD=0' - 8 17/32"; NOZZLE_HEIGHT=2' - 8"; NOZZLE_HEIGHT/7*2=0' - 8"; NOZZLE_SIZE=12' - 0"; NOZZLE_TOP_OD=1' - 7 1/2"; NOZZLE_TOP_RAD=0' - 9 3/4"; NOZZLE_WB/4=0' - 5 19/32"; NOZZLE_WB_OD=2' - 4"; NOZZLE_WB_RAD=1' - 2"; NOZZLE_WB_RAD-2"=1' - 0"; RO=2' - 10 3/4"; RO/2=1' - 5 3/8"; RO2/2=1' - 5 3/8"; TRANSITION_TOP=6' - 5 1/16"; TRIPLE_F+1"=12' - 1"; TRIP_F=12' - 0"; TRIP_G=11' - 11 1/4"; TYPE=1' - 0"; Type Comments=Vari-Plume Laboratory Exhaust Mixed-Flow High Pressure Inline Belt Drive With 1X3 Mixing Box; UNIT_HEIGHT=3' - 5"; UNIT_HEIGHT*.75=2' - 6 3/4"; UNIT_OD=2' - 7 15/16"; UNIT_RAD+((A/2)+.25")=3' - 1 7/32"; UNIT_RAD+((A/2)+.25")+4"=3' - 5 7/32"; UNIT_RADIUS=1' - 3 31/32"; UNIT_RADIUS*.6=1' - 2 3/8"; UNIT_RADIUS+4"=1' - 7 31/32"
- 225_QMXHPVP-15H-1X3_Mixing_Box: (A/2)+.25"=1' - 9 1/4"; (A/2)-2"=1' - 7"; (NOZZLE_HEIGHT-(NOZZLE_HEIGHT/8*2))/2=1' - 4 1/8"; (NOZZLE_WB_OD-NOZZLE_TOP_OD)/2=0' - 3 1/4"; -A=-3' - 6"; A=3' - 6"; A+.5=3' - 6 1/2"; A/2=1' - 9"; B=9' - 5"; B/2=4' - 8 1/2"; C=4' - 8"; C/2=2' - 4"; DUAL_F=7' - 9 1/4"; DUAL_F+1"=7' - 10 1/4"; DUAL_G=7' - 8 1/8"; E=3' - 4 15/16"; GA=0' - 0 3/32"; LONG_RO=11' - 5"; MB_A=4' - 6"; MB_HT=3' - 7 3/16"; MB_HT+.25"=3' - 7 7/16"; MB_HT-2.75"=3' - 4 7/16"; MB_HT/2=1' - 9 19/32"; Model=QMXHPVP-1X3_Mixing Box; NOZZLE_BOTTOM_ID=1' - 9 3/8"; NOZZLE_BOTTOM_RAD=0' - 10 11/16"; NOZZLE_HEIGHT=3' - 7"; NOZZLE_HEIGHT/7*2=0' - 10 3/4"; NOZZLE_SIZE=15' - 0"; NOZZLE_TOP_OD=1' - 11"; NOZZLE_TOP_RAD=0' - 11 1/2"; NOZZLE_WB/4=0' - 7 3/16"; NOZZLE_WB_OD=3' - 0"; NOZZLE_WB_RAD=1' - 6"; NOZZLE_WB_RAD-2"=1' - 4"; RO=2' - 10 3/4"; RO/2=1' - 5 3/8"; RO2/2=1' - 5 3/8"; TRANSITION_TOP=5' - 9 1/8"; TRIPLE_F+1"=12' - 1"; TRIP_F=12' - 0"; TRIP_G=11' - 11 1/4"; TYPE=1' - 0"; Type Comments=Vari-Plume Laboratory Exhaust Mixed-Flow High Pressure Inline Belt Drive With 1X3 Mixing Box; UNIT_HEIGHT=3' - 5"; UNIT_HEIGHT*.75=2' - 6 3/4"; UNIT_OD=2' - 7 15/16"; UNIT_RAD+((A/2)+.25")=3' - 1 7/32"; UNIT_RAD+((A/2)+.25")+4"=3' - 5 7/32"; UNIT_RADIUS=1' - 3 31/32"; UNIT_RADIUS*.6=1' - 2 3/8"; UNIT_RADIUS+4"=1' - 7 31/32"
- 225_QMXHPVP-15L-1X3_Mixing_Box: (A/2)+.25"=1' - 9 1/4"; (A/2)-2"=1' - 7"; (NOZZLE_HEIGHT-(NOZZLE_HEIGHT/8*2))/2=1' - 4 1/8"; (NOZZLE_WB_OD-NOZZLE_TOP_OD)/2=0' - 3 1/4"; -A=-3' - 6"; A=3' - 6"; A+.5=3' - 6 1/2"; A/2=1' - 9"; B=9' - 5"; B/2=4' - 8 1/2"; C=4' - 8"; C/2=2' - 4"; DUAL_F=7' - 9 1/4"; DUAL_F+1"=7' - 10 1/4"; DUAL_G=7' - 8 1/8"; E=3' - 4 15/16"; GA=0' - 0 3/32"; LONG_RO=11' - 5"; MB_A=4' - 6"; MB_HT=3' - 7 3/16"; MB_HT+.25"=3' - 7 7/16"; MB_HT-2.75"=3' - 4 7/16"; MB_HT/2=1' - 9 19/32"; Model=QMXHPVP-1X3_Mixing Box; NOZZLE_BOTTOM_ID=1' - 9 3/8"; NOZZLE_BOTTOM_RAD=0' - 10 11/16"; NOZZLE_HEIGHT=3' - 7"; NOZZLE_HEIGHT/7*2=0' - 10 3/4"; NOZZLE_SIZE=15' - 0"; NOZZLE_TOP_OD=1' - 11"; NOZZLE_TOP_RAD=0' - 11 1/2"; NOZZLE_WB/4=0' - 7 3/16"; NOZZLE_WB_OD=3' - 0"; NOZZLE_WB_RAD=1' - 6"; NOZZLE_WB_RAD-2"=1' - 4"; RO=2' - 10 3/4"; RO/2=1' - 5 3/8"; RO2/2=1' - 5 3/8"; TRANSITION_TOP=5' - 9 1/8"; TRIPLE_F+1"=12' - 1"; TRIP_F=12' - 0"; TRIP_G=11' - 11 1/4"; TYPE=1' - 0"; Type Comments=Vari-Plume Laboratory Exhaust Mixed-Flow High Pressure Inline Belt Drive With 1X3 Mixing Box; UNIT_HEIGHT=3' - 5"; UNIT_HEIGHT*.75=2' - 6 3/4"; UNIT_OD=2' - 7 15/16"; UNIT_RAD+((A/2)+.25")=3' - 1 7/32"; UNIT_RAD+((A/2)+.25")+4"=3' - 5 7/32"; UNIT_RADIUS=1' - 3 31/32"; UNIT_RADIUS*.6=1' - 2 3/8"; UNIT_RADIUS+4"=1' - 7 31/32"
- 225_QMXVP-18H-1X3_Mixing_Box: (A/2)+.25"=1' - 9 1/4"; (A/2)-2"=1' - 7"; (NOZZLE_HEIGHT-(NOZZLE_HEIGHT/8*2))/2=1' - 6"; (NOZZLE_WB_OD-NOZZLE_TOP_OD)/2=0' - 3 7/8"; -A=-3' - 6"; A=3' - 6"; A+.5=3' - 6 1/2"; A/2=1' - 9"; B=9' - 5"; B/2=4' - 8 1/2"; C=4' - 8"; C/2=2' - 4"; DUAL_F=7' - 9 1/4"; DUAL_F+1"=7' - 10 1/4"; DUAL_G=7' - 8 1/8"; E=3' - 4 15/16"; GA=0' - 0 3/32"; LONG_RO=11' - 5"; MB_A=4' - 6"; MB_HT=3' - 7 3/16"; MB_HT+.25"=3' - 7 7/16"; MB_HT-2.75"=3' - 4 7/16"; MB_HT/2=1' - 9 19/32"; Model=QMXVP-1X3_Mixing Box; NOZZLE_BOTTOM_ID=2' - 1 5/8"; NOZZLE_BOTTOM_RAD=1' - 0 13/16"; NOZZLE_HEIGHT=4' - 0"; NOZZLE_HEIGHT/7*2=1' - 0"; NOZZLE_SIZE=18' - 0"; NOZZLE_TOP_OD=2' - 3 1/2"; NOZZLE_TOP_RAD=1' - 1 3/4"; NOZZLE_WB/4=0' - 8 19/32"; NOZZLE_WB_OD=3' - 7"; NOZZLE_WB_RAD=1' - 9 1/2"; NOZZLE_WB_RAD-2"=1' - 7 1/2"; RO=2' - 10 3/4"; RO/2=1' - 5 3/8"; RO2/2=1' - 5 3/8"; TRANSITION_TOP=5' - 1 1/8"; TRIPLE_F+1"=12' - 1"; TRIP_F=12' - 0"; TRIP_G=11' - 11 1/4"; TYPE=0' - 0"; Type Comments=Vari-Plume Laboratory Exhaust Mixed-Flow Inline Belt Drive With 1X3 Mixing Box; UNIT_HEIGHT=3' - 5"; UNIT_HEIGHT*.75=2' - 6 3/4"; UNIT_OD=2' - 7 15/16"; UNIT_RAD+((A/2)+.25")=3' - 1 7/32"; UNIT_RAD+((A/2)+.25")+4"=3' - 5 7/32"; UNIT_RADIUS=1' - 3 31/32"; UNIT_RADIUS*.6=1' - 2 3/8"; UNIT_RADIUS+4"=1' - 7 31/32"
- 225_QMXHPVP-18L-1X3_Mixing_Box: (A/2)+.25"=1' - 9 1/4"; (A/2)-2"=1' - 7"; (NOZZLE_HEIGHT-(NOZZLE_HEIGHT/8*2))/2=1' - 6"; (NOZZLE_WB_OD-NOZZLE_TOP_OD)/2=0' - 3 7/8"; -A=-3' - 6"; A=3' - 6"; A+.5=3' - 6 1/2"; A/2=1' - 9"; B=9' - 5"; B/2=4' - 8 1/2"; C=4' - 8"; C/2=2' - 4"; DUAL_F=7' - 9 1/4"; DUAL_F+1"=7' - 10 1/4"; DUAL_G=7' - 8 1/8"; E=3' - 4 15/16"; GA=0' - 0 3/32"; LONG_RO=11' - 5"; MB_A=4' - 6"; MB_HT=3' - 7 3/16"; MB_HT+.25"=3' - 7 7/16"; MB_HT-2.75"=3' - 4 7/16"; MB_HT/2=1' - 9 19/32"; Model=QMXHPVP-1X3_Mixing Box; NOZZLE_BOTTOM_ID=2' - 1 5/8"; NOZZLE_BOTTOM_RAD=1' - 0 13/16"; NOZZLE_HEIGHT=4' - 0"; NOZZLE_HEIGHT/7*2=1' - 0"; NOZZLE_SIZE=18' - 0"; NOZZLE_TOP_OD=2' - 3 1/2"; NOZZLE_TOP_RAD=1' - 1 3/4"; NOZZLE_WB/4=0' - 8 19/32"; NOZZLE_WB_OD=3' - 7"; NOZZLE_WB_RAD=1' - 9 1/2"; NOZZLE_WB_RAD-2"=1' - 7 1/2"; RO=2' - 10 3/4"; RO/2=1' - 5 3/8"; RO2/2=1' - 5 3/8"; TRANSITION_TOP=5' - 1 1/8"; TRIPLE_F+1"=12' - 1"; TRIP_F=12' - 0"; TRIP_G=11' - 11 1/4"; TYPE=1' - 0"; Type Comments=Vari-Plume Laboratory Exhaust Mixed-Flow High Pressure Inline Belt Drive With 1X3 Mixing Box; UNIT_HEIGHT=3' - 5"; UNIT_HEIGHT*.75=2' - 6 3/4"; UNIT_OD=2' - 7 15/16"; UNIT_RAD+((A/2)+.25")=3' - 1 7/32"; UNIT_RAD+((A/2)+.25")+4"=3' - 5 7/32"; UNIT_RADIUS=1' - 3 31/32"; UNIT_RADIUS*.6=1' - 2 3/8"; UNIT_RADIUS+4"=1' - 7 31/32"
- 225_QMXHPVP-18H-1X3_Mixing_Box: (A/2)+.25"=1' - 9 1/4"; (A/2)-2"=1' - 7"; (NOZZLE_HEIGHT-(NOZZLE_HEIGHT/8*2))/2=1' - 6"; (NOZZLE_WB_OD-NOZZLE_TOP_OD)/2=0' - 3 7/8"; -A=-3' - 6"; A=3' - 6"; A+.5=3' - 6 1/2"; A/2=1' - 9"; B=9' - 5"; B/2=4' - 8 1/2"; C=4' - 8"; C/2=2' - 4"; DUAL_F=7' - 9 1/4"; DUAL_F+1"=7' - 10 1/4"; DUAL_G=7' - 8 1/8"; E=3' - 4 15/16"; GA=0' - 0 3/32"; LONG_RO=11' - 5"; MB_A=4' - 6"; MB_HT=3' - 7 3/16"; MB_HT+.25"=3' - 7 7/16"; MB_HT-2.75"=3' - 4 7/16"; MB_HT/2=1' - 9 19/32"; Model=QMXHPVP-1X3_Mixing Box; NOZZLE_BOTTOM_ID=2' - 1 5/8"; NOZZLE_BOTTOM_RAD=1' - 0 13/16"; NOZZLE_HEIGHT=4' - 0"; NOZZLE_HEIGHT/7*2=1' - 0"; NOZZLE_SIZE=18' - 0"; NOZZLE_TOP_OD=2' - 3 1/2"; NOZZLE_TOP_RAD=1' - 1 3/4"; NOZZLE_WB/4=0' - 8 19/32"; NOZZLE_WB_OD=3' - 7"; NOZZLE_WB_RAD=1' - 9 1/2"; NOZZLE_WB_RAD-2"=1' - 7 1/2"; RO=2' - 10 3/4"; RO/2=1' - 5 3/8"; RO2/2=1' - 5 3/8"; TRANSITION_TOP=5' - 1 1/8"; TRIPLE_F+1"=12' - 1"; TRIP_F=12' - 0"; TRIP_G=11' - 11 1/4"; TYPE=1' - 0"; Type Comments=Vari-Plume Laboratory Exhaust Mixed-Flow High Pressure Inline Belt Drive With 1X3 Mixing Box; UNIT_HEIGHT=3' - 5"; UNIT_HEIGHT*.75=2' - 6 3/4"; UNIT_OD=2' - 7 15/16"; UNIT_RAD+((A/2)+.25")=3' - 1 7/32"; UNIT_RAD+((A/2)+.25")+4"=3' - 5 7/32"; UNIT_RADIUS=1' - 3 31/32"; UNIT_RADIUS*.6=1' - 2 3/8"; UNIT_RADIUS+4"=1' - 7 31/32"
- 245_QMXHPVP-15H-1X3_Mixing_Box: (A/2)+.25"=1' - 10 1/4"; (A/2)-2"=1' - 8"; (NOZZLE_HEIGHT-(NOZZLE_HEIGHT/8*2))/2=1' - 4 1/8"; (NOZZLE_WB_OD-NOZZLE_TOP_OD)/2=0' - 3 1/4"; -A=-3' - 8"; A=3' - 8"; A+.5=3' - 8 1/2"; A/2=1' - 10"; B=10' - 1"; B/2=5' - 0 1/2"; C=4' - 11"; C/2=2' - 5 1/2"; DUAL_F=9' - 0 1/4"; DUAL_F+1"=9' - 1 1/4"; DUAL_G=8' - 11 1/8"; E=3' - 6 15/16"; GA=0' - 0 3/32"; LONG_RO=13' - 9 1/16"; MB_A=4' - 9"; MB_HT=3' - 9 7/16"; MB_HT+.25"=3' - 9 11/16"; MB_HT-2.75"=3' - 6 11/16"; MB_HT/2=1' - 10 23/32"; Model=QMXHPVP-1X3_Mixing Box; NOZZLE_BOTTOM_ID=1' - 9 3/8"; NOZZLE_BOTTOM_RAD=0' - 10 11/16"; NOZZLE_HEIGHT=3' - 7"; NOZZLE_HEIGHT/7*2=0' - 10 3/4"; NOZZLE_SIZE=15' - 0"; NOZZLE_TOP_OD=1' - 11"; NOZZLE_TOP_RAD=0' - 11 1/2"; NOZZLE_WB/4=0' - 7 3/16"; NOZZLE_WB_OD=3' - 0"; NOZZLE_WB_RAD=1' - 6"; NOZZLE_WB_RAD-2"=1' - 4"; RO=3' - 0 3/4"; RO/2=1' - 6 3/8"; RO2/2=1' - 6 3/8"; TRANSITION_TOP=6' - 5 11/16"; TRIPLE_F+1"=14' - 5"; TRIP_F=14' - 4"; TRIP_G=14' - 3 5/16"; TYPE=1' - 0"; Type Comments=Vari-Plume Laboratory Exhaust Mixed-Flow High Pressure Inline Belt Drive With 1X3 Mixing Box; UNIT_HEIGHT=3' - 8 1/2"; UNIT_HEIGHT*.75=2' - 9 3/8"; UNIT_OD=2' - 10 3/4"; UNIT_RAD+((A/2)+.25")=3' - 3 5/8"; UNIT_RAD+((A/2)+.25")+4"=3' - 7 5/8"; UNIT_RADIUS=1' - 5 3/8"; UNIT_RADIUS*.6=1' - 3 5/8"; UNIT_RADIUS+4"=1' - 9 3/8"
- 245_QMXHPVP-15L-1X3_Mixing_Box: (A/2)+.25"=1' - 10 1/4"; (A/2)-2"=1' - 8"; (NOZZLE_HEIGHT-(NOZZLE_HEIGHT/8*2))/2=1' - 4 1/8"; (NOZZLE_WB_OD-NOZZLE_TOP_OD)/2=0' - 3 1/4"; -A=-3' - 8"; A=3' - 8"; A+.5=3' - 8 1/2"; A/2=1' - 10"; B=10' - 1"; B/2=5' - 0 1/2"; C=4' - 11"; C/2=2' - 5 1/2"; DUAL_F=9' - 0 1/4"; DUAL_F+1"=9' - 1 1/4"; DUAL_G=8' - 11 1/8"; E=3' - 6 15/16"; GA=0' - 0 3/32"; LONG_RO=13' - 9 1/16"; MB_A=4' - 9"; MB_HT=3' - 9 7/16"; MB_HT+.25"=3' - 9 11/16"; MB_HT-2.75"=3' - 6 11/16"; MB_HT/2=1' - 10 23/32"; Model=QMXHPVP-1X3_Mixing Box; NOZZLE_BOTTOM_ID=1' - 9 3/8"; NOZZLE_BOTTOM_RAD=0' - 10 11/16"; NOZZLE_HEIGHT=3' - 7"; NOZZLE_HEIGHT/7*2=0' - 10 3/4"; NOZZLE_SIZE=15' - 0"; NOZZLE_TOP_OD=1' - 11"; NOZZLE_TOP_RAD=0' - 11 1/2"; NOZZLE_WB/4=0' - 7 3/16"; NOZZLE_WB_OD=3' - 0"; NOZZLE_WB_RAD=1' - 6"; NOZZLE_WB_RAD-2"=1' - 4"; RO=3' - 0 3/4"; RO/2=1' - 6 3/8"; RO2/2=1' - 6 3/8"; TRANSITION_TOP=6' - 5 11/16"; TRIPLE_F+1"=14' - 5"; TRIP_F=14' - 4"; TRIP_G=14' - 3 5/16"; TYPE=1' - 0"; Type Comments=Vari-Plume Laboratory Exhaust Mixed-Flow High Pressure Inline Belt Drive With 1X3 Mixing Box; UNIT_HEIGHT=3' - 8 1/2"; UNIT_HEIGHT*.75=2' - 9 3/8"; UNIT_OD=2' - 10 3/4"; UNIT_RAD+((A/2)+.25")=3' - 3 5/8"; UNIT_RAD+((A/2)+.25")+4"=3' - 7 5/8"; UNIT_RADIUS=1' - 5 3/8"; UNIT_RADIUS*.6=1' - 3 5/8"; UNIT_RADIUS+4"=1' - 9 3/8"
- 245_QMXHPVP-18H-1X3_Mixing_Box: (A/2)+.25"=1' - 10 1/4"; (A/2)-2"=1' - 8"; (NOZZLE_HEIGHT-(NOZZLE_HEIGHT/8*2))/2=1' - 6"; (NOZZLE_WB_OD-NOZZLE_TOP_OD)/2=0' - 3 7/8"; -A=-3' - 8"; A=3' - 8"; A+.5=3' - 8 1/2"; A/2=1' - 10"; B=10' - 1"; B/2=5' - 0 1/2"; C=4' - 11"; C/2=2' - 5 1/2"; DUAL_F=9' - 0 1/4"; DUAL_F+1"=9' - 1 1/4"; DUAL_G=8' - 11 1/8"; E=3' - 6 15/16"; GA=0' - 0 3/32"; LONG_RO=13' - 9 1/16"; MB_A=4' - 9"; MB_HT=3' - 9 7/16"; MB_HT+.25"=3' - 9 11/16"; MB_HT-2.75"=3' - 6 11/16"; MB_HT/2=1' - 10 23/32"; Model=QMXHPVP-1X3_Mixing Box; NOZZLE_BOTTOM_ID=2' - 1 5/8"; NOZZLE_BOTTOM_RAD=1' - 0 13/16"; NOZZLE_HEIGHT=4' - 0"; NOZZLE_HEIGHT/7*2=1' - 0"; NOZZLE_SIZE=18' - 0"; NOZZLE_TOP_OD=2' - 3 1/2"; NOZZLE_TOP_RAD=1' - 1 3/4"; NOZZLE_WB/4=0' - 8 19/32"; NOZZLE_WB_OD=3' - 7"; NOZZLE_WB_RAD=1' - 9 1/2"; NOZZLE_WB_RAD-2"=1' - 7 1/2"; RO=3' - 0 3/4"; RO/2=1' - 6 3/8"; RO2/2=1' - 6 3/8"; TRANSITION_TOP=5' - 9 11/16"; TRIPLE_F+1"=14' - 5"; TRIP_F=14' - 4"; TRIP_G=14' - 3 5/16"; TYPE=1' - 0"; Type Comments=Vari-Plume Laboratory Exhaust Mixed-Flow High Pressure Inline Belt Drive With 1X3 Mixing Box; UNIT_HEIGHT=3' - 8 1/2"; UNIT_HEIGHT*.75=2' - 9 3/8"; UNIT_OD=2' - 10 3/4"; UNIT_RAD+((A/2)+.25")=3' - 3 5/8"; UNIT_RAD+((A/2)+.25")+4"=3' - 7 5/8"; UNIT_RADIUS=1' - 5 3/8"; UNIT_RADIUS*.6=1' - 3 5/8"; UNIT_RADIUS+4"=1' - 9 3/8"
- 245_QMXHPVP-18L-1X3_Mixing_Box: (A/2)+.25"=1' - 10 1/4"; (A/2)-2"=1' - 8"; (NOZZLE_HEIGHT-(NOZZLE_HEIGHT/8*2))/2=1' - 6"; (NOZZLE_WB_OD-NOZZLE_TOP_OD)/2=0' - 3 7/8"; -A=-3' - 8"; A=3' - 8"; A+.5=3' - 8 1/2"; A/2=1' - 10"; B=10' - 1"; B/2=5' - 0 1/2"; C=4' - 11"; C/2=2' - 5 1/2"; DUAL_F=9' - 0 1/4"; DUAL_F+1"=9' - 1 1/4"; DUAL_G=8' - 11 1/8"; E=3' - 6 15/16"; GA=0' - 0 3/32"; LONG_RO=13' - 9 1/16"; MB_A=4' - 9"; MB_HT=3' - 9 7/16"; MB_HT+.25"=3' - 9 11/16"; MB_HT-2.75"=3' - 6 11/16"; MB_HT/2=1' - 10 23/32"; Model=QMXHPVP-1X3_Mixing Box; NOZZLE_BOTTOM_ID=2' - 1 5/8"; NOZZLE_BOTTOM_RAD=1' - 0 13/16"; NOZZLE_HEIGHT=4' - 0"; NOZZLE_HEIGHT/7*2=1' - 0"; NOZZLE_SIZE=18' - 0"; NOZZLE_TOP_OD=2' - 3 1/2"; NOZZLE_TOP_RAD=1' - 1 3/4"; NOZZLE_WB/4=0' - 8 19/32"; NOZZLE_WB_OD=3' - 7"; NOZZLE_WB_RAD=1' - 9 1/2"; NOZZLE_WB_RAD-2"=1' - 7 1/2"; RO=3' - 0 3/4"; RO/2=1' - 6 3/8"; RO2/2=1' - 6 3/8"; TRANSITION_TOP=5' - 9 11/16"; TRIPLE_F+1"=14' - 5"; TRIP_F=14' - 4"; TRIP_G=14' - 3 5/16"; TYPE=1' - 0"; Type Comments=Vari-Plume Laboratory Exhaust Mixed-Flow High Pressure Inline Belt Drive With 1X3 Mixing Box; UNIT_HEIGHT=3' - 8 1/2"; UNIT_HEIGHT*.75=2' - 9 3/8"; UNIT_OD=2' - 10 3/4"; UNIT_RAD+((A/2)+.25")=3' - 3 5/8"; UNIT_RAD+((A/2)+.25")+4"=3' - 7 5/8"; UNIT_RADIUS=1' - 5 3/8"; UNIT_RADIUS*.6=1' - 3 5/8"; UNIT_RADIUS+4"=1' - 9 3/8"
- 245_QMXHPVP-24H-1X3_Mixing_Box: (A/2)+.25"=1' - 10 1/4"; (A/2)-2"=1' - 8"; (NOZZLE_HEIGHT-(NOZZLE_HEIGHT/8*2))/2=1' - 11 1/4"; (NOZZLE_WB_OD-NOZZLE_TOP_OD)/2=0' - 6 1/8"; -A=-3' - 8"; A=3' - 8"; A+.5=3' - 8 1/2"; A/2=1' - 10"; B=10' - 1"; B/2=5' - 0 1/2"; C=4' - 11"; C/2=2' - 5 1/2"; DUAL_F=9' - 0 1/4"; DUAL_F+1"=9' - 1 1/4"; DUAL_G=8' - 11 1/8"; E=3' - 6 15/16"; GA=0' - 0 3/32"; LONG_RO=13' - 9 1/16"; MB_A=4' - 9"; MB_HT=3' - 9 7/16"; MB_HT+.25"=3' - 9 11/16"; MB_HT-2.75"=3' - 6 11/16"; MB_HT/2=1' - 10 23/32"; Model=QMXHPVP-1X3_Mixing Box; NOZZLE_BOTTOM_ID=2' - 10 3/4"; NOZZLE_BOTTOM_RAD=1' - 5 3/8"; NOZZLE_HEIGHT=5' - 2"; NOZZLE_HEIGHT/7*2=1' - 3 1/2"; NOZZLE_SIZE=24' - 0"; NOZZLE_TOP_OD=3' - 0 1/2"; NOZZLE_TOP_RAD=1' - 6 1/4"; NOZZLE_WB/4=1' - 0 3/16"; NOZZLE_WB_OD=5' - 1"; NOZZLE_WB_RAD=2' - 6 1/2"; NOZZLE_WB_RAD-2"=2' - 4 1/2"; RO=3' - 0 3/4"; RO/2=1' - 6 3/8"; RO2/2=1' - 6 3/8"; TRANSITION_TOP=4' - 9 3/4"; TRIPLE_F+1"=14' - 5"; TRIP_F=14' - 4"; TRIP_G=14' - 3 5/16"; TYPE=1' - 0"; Type Comments=Vari-Plume Laboratory Exhaust Mixed-Flow High Pressure Inline Belt Drive With 1X3 Mixing Box; UNIT_HEIGHT=3' - 8 1/2"; UNIT_HEIGHT*.75=2' - 9 3/8"; UNIT_OD=2' - 10 3/4"; UNIT_RAD+((A/2)+.25")=3' - 3 5/8"; UNIT_RAD+((A/2)+.25")+4"=3' - 7 5/8"; UNIT_RADIUS=1' - 5 3/8"; UNIT_RADIUS*.6=1' - 3 5/8"; UNIT_RADIUS+4"=1' - 9 3/8"
- 245_QMXHPVP-24L-1X3_Mixing_Box: (A/2)+.25"=1' - 10 1/4"; (A/2)-2"=1' - 8"; (NOZZLE_HEIGHT-(NOZZLE_HEIGHT/8*2))/2=1' - 11 1/4"; (NOZZLE_WB_OD-NOZZLE_TOP_OD)/2=0' - 6 1/8"; -A=-3' - 8"; A=3' - 8"; A+.5=3' - 8 1/2"; A/2=1' - 10"; B=10' - 1"; B/2=5' - 0 1/2"; C=4' - 11"; C/2=2' - 5 1/2"; DUAL_F=9' - 0 1/4"; DUAL_F+1"=9' - 1 1/4"; DUAL_G=8' - 11 1/8"; E=3' - 6 15/16"; GA=0' - 0 3/32"; LONG_RO=13' - 9 1/16"; MB_A=4' - 9"; MB_HT=3' - 9 7/16"; MB_HT+.25"=3' - 9 11/16"; MB_HT-2.75"=3' - 6 11/16"; MB_HT/2=1' - 10 23/32"; Model=QMXHPVP-1X3_Mixing Box; NOZZLE_BOTTOM_ID=2' - 10 3/4"; NOZZLE_BOTTOM_RAD=1' - 5 3/8"; NOZZLE_HEIGHT=5' - 2"; NOZZLE_HEIGHT/7*2=1' - 3 1/2"; NOZZLE_SIZE=24' - 0"; NOZZLE_TOP_OD=3' - 0 1/2"; NOZZLE_TOP_RAD=1' - 6 1/4"; NOZZLE_WB/4=1' - 0 3/16"; NOZZLE_WB_OD=5' - 1"; NOZZLE_WB_RAD=2' - 6 1/2"; NOZZLE_WB_RAD-2"=2' - 4 1/2"; RO=3' - 0 3/4"; RO/2=1' - 6 3/8"; RO2/2=1' - 6 3/8"; TRANSITION_TOP=4' - 9 3/4"; TRIPLE_F+1"=14' - 5"; TRIP_F=14' - 4"; TRIP_G=14' - 3 5/16"; TYPE=1' - 0"; Type Comments=Vari-Plume Laboratory Exhaust Mixed-Flow High Pressure Inline Belt Drive With 1X3 Mixing Box; UNIT_HEIGHT=3' - 8 1/2"; UNIT_HEIGHT*.75=2' - 9 3/8"; UNIT_OD=2' - 10 3/4"; UNIT_RAD+((A/2)+.25")=3' - 3 5/8"; UNIT_RAD+((A/2)+.25")+4"=3' - 7 5/8"; UNIT_RADIUS=1' - 5 3/8"; UNIT_RADIUS*.6=1' - 3 5/8"; UNIT_RADIUS+4"=1' - 9 3/8"
- 270_QMXHPVP-15H-1X3_Mixing_Box: (A/2)+.25"=2' - 0 1/4"; (A/2)-2"=1' - 10"; (NOZZLE_HEIGHT-(NOZZLE_HEIGHT/8*2))/2=1' - 4 1/8"; (NOZZLE_WB_OD-NOZZLE_TOP_OD)/2=0' - 3 1/4"; -A=-4' - 0"; A=4' - 0"; A+.5=4' - 0 1/2"; A/2=2' - 0"; B=10' - 8"; B/2=5' - 4"; C=5' - 3"; C/2=2' - 7 1/2"; DUAL_F=9' - 4 1/4"; DUAL_F+1"=9' - 5 1/4"; DUAL_G=9' - 3 1/8"; E=3' - 10 15/16"; GA=0' - 0 3/32"; LONG_RO=14' - 1 1/16"; MB_A=5' - 2"; MB_HT=3' - 11 3/16"; MB_HT+.25"=3' - 11 7/16"; MB_HT-2.75"=3' - 8 7/16"; MB_HT/2=1' - 11 19/32"; Model=QMXHPVP-1X3_Mixing Box; NOZZLE_BOTTOM_ID=1' - 9 3/8"; NOZZLE_BOTTOM_RAD=0' - 10 11/16"; NOZZLE_HEIGHT=3' - 7"; NOZZLE_HEIGHT/7*2=0' - 10 3/4"; NOZZLE_SIZE=15' - 0"; NOZZLE_TOP_OD=1' - 11"; NOZZLE_TOP_RAD=0' - 11 1/2"; NOZZLE_WB/4=0' - 7 3/16"; NOZZLE_WB_OD=3' - 0"; NOZZLE_WB_RAD=1' - 6"; NOZZLE_WB_RAD-2"=1' - 4"; RO=3' - 4 3/4"; RO/2=1' - 8 3/8"; RO2/2=1' - 8 3/8"; TRANSITION_TOP=7' - 2 3/16"; TRIPLE_F+1"=14' - 9"; TRIP_F=14' - 8"; TRIP_G=14' - 7 5/16"; TYPE=1' - 0"; Type Comments=Vari-Plume Laboratory Exhaust Mixed-Flow High Pressure Inline Belt Drive With 1X3 Mixing Box; UNIT_HEIGHT=3' - 11"; UNIT_HEIGHT*.75=2' - 11 1/4"; UNIT_OD=3' - 2 5/16"; UNIT_RAD+((A/2)+.25")=3' - 7 13/32"; UNIT_RAD+((A/2)+.25")+4"=3' - 11 13/32"; UNIT_RADIUS=1' - 7 5/32"; UNIT_RADIUS*.6=1' - 5 1/4"; UNIT_RADIUS+4"=1' - 11 5/32"
- 270_QMXHPVP-15L-1X3_Mixing_Box: (A/2)+.25"=2' - 0 1/4"; (A/2)-2"=1' - 10"; (NOZZLE_HEIGHT-(NOZZLE_HEIGHT/8*2))/2=1' - 4 1/8"; (NOZZLE_WB_OD-NOZZLE_TOP_OD)/2=0' - 3 1/4"; -A=-4' - 0"; A=4' - 0"; A+.5=4' - 0 1/2"; A/2=2' - 0"; B=10' - 8"; B/2=5' - 4"; C=5' - 3"; C/2=2' - 7 1/2"; DUAL_F=9' - 4 1/4"; DUAL_F+1"=9' - 5 1/4"; DUAL_G=9' - 3 1/8"; E=3' - 10 15/16"; GA=0' - 0 3/32"; LONG_RO=14' - 1 1/16"; MB_A=5' - 2"; MB_HT=3' - 11 3/16"; MB_HT+.25"=3' - 11 7/16"; MB_HT-2.75"=3' - 8 7/16"; MB_HT/2=1' - 11 19/32"; Model=QMXHPVP-1X3_Mixing Box; NOZZLE_BOTTOM_ID=1' - 9 3/8"; NOZZLE_BOTTOM_RAD=0' - 10 11/16"; NOZZLE_HEIGHT=3' - 7"; NOZZLE_HEIGHT/7*2=0' - 10 3/4"; NOZZLE_SIZE=15' - 0"; NOZZLE_TOP_OD=1' - 11"; NOZZLE_TOP_RAD=0' - 11 1/2"; NOZZLE_WB/4=0' - 7 3/16"; NOZZLE_WB_OD=3' - 0"; NOZZLE_WB_RAD=1' - 6"; NOZZLE_WB_RAD-2"=1' - 4"; RO=3' - 4 3/4"; RO/2=1' - 8 3/8"; RO2/2=1' - 8 3/8"; TRANSITION_TOP=7' - 2 3/16"; TRIPLE_F+1"=14' - 9"; TRIP_F=14' - 8"; TRIP_G=14' - 7 5/16"; TYPE=1' - 0"; Type Comments=Vari-Plume Laboratory Exhaust Mixed-Flow High Pressure Inline Belt Drive With 1X3 Mixing Box; UNIT_HEIGHT=3' - 11"; UNIT_HEIGHT*.75=2' - 11 1/4"; UNIT_OD=3' - 2 5/16"; UNIT_RAD+((A/2)+.25")=3' - 7 13/32"; UNIT_RAD+((A/2)+.25")+4"=3' - 11 13/32"; UNIT_RADIUS=1' - 7 5/32"; UNIT_RADIUS*.6=1' - 5 1/4"; UNIT_RADIUS+4"=1' - 11 5/32"
- 270_QMXHPVP-18H-1X3_Mixing_Box: (A/2)+.25"=2' - 0 1/4"; (A/2)-2"=1' - 10"; (NOZZLE_HEIGHT-(NOZZLE_HEIGHT/8*2))/2=1' - 6"; (NOZZLE_WB_OD-NOZZLE_TOP_OD)/2=0' - 3 7/8"; -A=-4' - 0"; A=4' - 0"; A+.5=4' - 0 1/2"; A/2=2' - 0"; B=10' - 8"; B/2=5' - 4"; C=5' - 3"; C/2=2' - 7 1/2"; DUAL_F=9' - 4 1/4"; DUAL_F+1"=9' - 5 1/4"; DUAL_G=9' - 3 1/8"; E=3' - 10 15/16"; GA=0' - 0 3/32"; LONG_RO=14' - 1 1/16"; MB_A=5' - 2"; MB_HT=3' - 11 3/16"; MB_HT+.25"=3' - 11 7/16"; MB_HT-2.75"=3' - 8 7/16"; MB_HT/2=1' - 11 19/32"; Model=QMXHPVP-1X3_Mixing Box; NOZZLE_BOTTOM_ID=2' - 1 5/8"; NOZZLE_BOTTOM_RAD=1' - 0 13/16"; NOZZLE_HEIGHT=4' - 0"; NOZZLE_HEIGHT/7*2=1' - 0"; NOZZLE_SIZE=18' - 0"; NOZZLE_TOP_OD=2' - 3 1/2"; NOZZLE_TOP_RAD=1' - 1 3/4"; NOZZLE_WB/4=0' - 8 19/32"; NOZZLE_WB_OD=3' - 7"; NOZZLE_WB_RAD=1' - 9 1/2"; NOZZLE_WB_RAD-2"=1' - 7 1/2"; RO=3' - 4 3/4"; RO/2=1' - 8 3/8"; RO2/2=1' - 8 3/8"; TRANSITION_TOP=6' - 7 3/16"; TRIPLE_F+1"=14' - 9"; TRIP_F=14' - 8"; TRIP_G=14' - 7 5/16"; TYPE=1' - 0"; Type Comments=Vari-Plume Laboratory Exhaust Mixed-Flow High Pressure Inline Belt Drive With 1X3 Mixing Box; UNIT_HEIGHT=3' - 11"; UNIT_HEIGHT*.75=2' - 11 1/4"; UNIT_OD=3' - 2 5/16"; UNIT_RAD+((A/2)+.25")=3' - 7 13/32"; UNIT_RAD+((A/2)+.25")+4"=3' - 11 13/32"; UNIT_RADIUS=1' - 7 5/32"; UNIT_RADIUS*.6=1' - 5 1/4"; UNIT_RADIUS+4"=1' - 11 5/32"
- 270_QMXHPVP-18L-1X3_Mixing_Box: (A/2)+.25"=2' - 0 1/4"; (A/2)-2"=1' - 10"; (NOZZLE_HEIGHT-(NOZZLE_HEIGHT/8*2))/2=1' - 6"; (NOZZLE_WB_OD-NOZZLE_TOP_OD)/2=0' - 3 7/8"; -A=-4' - 0"; A=4' - 0"; A+.5=4' - 0 1/2"; A/2=2' - 0"; B=10' - 8"; B/2=5' - 4"; C=5' - 3"; C/2=2' - 7 1/2"; DUAL_F=9' - 4 1/4"; DUAL_F+1"=9' - 5 1/4"; DUAL_G=9' - 3 1/8"; E=3' - 10 15/16"; GA=0' - 0 3/32"; LONG_RO=14' - 1 1/16"; MB_A=5' - 2"; MB_HT=3' - 11 3/16"; MB_HT+.25"=3' - 11 7/16"; MB_HT-2.75"=3' - 8 7/16"; MB_HT/2=1' - 11 19/32"; Model=QMXHPVP-1X3_Mixing Box; NOZZLE_BOTTOM_ID=2' - 1 5/8"; NOZZLE_BOTTOM_RAD=1' - 0 13/16"; NOZZLE_HEIGHT=4' - 0"; NOZZLE_HEIGHT/7*2=1' - 0"; NOZZLE_SIZE=18' - 0"; NOZZLE_TOP_OD=2' - 3 1/2"; NOZZLE_TOP_RAD=1' - 1 3/4"; NOZZLE_WB/4=0' - 8 19/32"; NOZZLE_WB_OD=3' - 7"; NOZZLE_WB_RAD=1' - 9 1/2"; NOZZLE_WB_RAD-2"=1' - 7 1/2"; RO=3' - 4 3/4"; RO/2=1' - 8 3/8"; RO2/2=1' - 8 3/8"; TRANSITION_TOP=6' - 7 3/16"; TRIPLE_F+1"=14' - 9"; TRIP_F=14' - 8"; TRIP_G=14' - 7 5/16"; TYPE=1' - 0"; Type Comments=Vari-Plume Laboratory Exhaust Mixed-Flow High Pressure Inline Belt Drive With 1X3 Mixing Box; UNIT_HEIGHT=3' - 11"; UNIT_HEIGHT*.75=2' - 11 1/4"; UNIT_OD=3' - 2 5/16"; UNIT_RAD+((A/2)+.25")=3' - 7 13/32"; UNIT_RAD+((A/2)+.25")+4"=3' - 11 13/32"; UNIT_RADIUS=1' - 7 5/32"; UNIT_RADIUS*.6=1' - 5 1/4"; UNIT_RADIUS+4"=1' - 11 5/32"
- 270_QMXHPVP-24H-1X3_Mixing_Box: (A/2)+.25"=2' - 0 1/4"; (A/2)-2"=1' - 10"; (NOZZLE_HEIGHT-(NOZZLE_HEIGHT/8*2))/2=1' - 11 1/4"; (NOZZLE_WB_OD-NOZZLE_TOP_OD)/2=0' - 6 1/8"; -A=-4' - 0"; A=4' - 0"; A+.5=4' - 0 1/2"; A/2=2' - 0"; B=10' - 8"; B/2=5' - 4"; C=5' - 3"; C/2=2' - 7 1/2"; DUAL_F=9' - 4 1/4"; DUAL_F+1"=9' - 5 1/4"; DUAL_G=9' - 3 1/8"; E=3' - 10 15/16"; GA=0' - 0 3/32"; LONG_RO=14' - 1 1/16"; MB_A=5' - 2"; MB_HT=3' - 11 3/16"; MB_HT+.25"=3' - 11 7/16"; MB_HT-2.75"=3' - 8 7/16"; MB_HT/2=1' - 11 19/32"; Model=QMXHPVP-1X3_Mixing Box; NOZZLE_BOTTOM_ID=2' - 10 3/4"; NOZZLE_BOTTOM_RAD=1' - 5 3/8"; NOZZLE_HEIGHT=5' - 2"; NOZZLE_HEIGHT/7*2=1' - 3 1/2"; NOZZLE_SIZE=24' - 0"; NOZZLE_TOP_OD=3' - 0 1/2"; NOZZLE_TOP_RAD=1' - 6 1/4"; NOZZLE_WB/4=1' - 0 3/16"; NOZZLE_WB_OD=5' - 1"; NOZZLE_WB_RAD=2' - 6 1/2"; NOZZLE_WB_RAD-2"=2' - 4 1/2"; RO=3' - 4 3/4"; RO/2=1' - 8 3/8"; RO2/2=1' - 8 3/8"; TRANSITION_TOP=5' - 2 1/4"; TRIPLE_F+1"=14' - 9"; TRIP_F=14' - 8"; TRIP_G=14' - 7 5/16"; TYPE=1' - 0"; Type Comments=Vari-Plume Laboratory Exhaust Mixed-Flow High Pressure Inline Belt Drive With 1X3 Mixing Box; UNIT_HEIGHT=3' - 11"; UNIT_HEIGHT*.75=2' - 11 1/4"; UNIT_OD=3' - 2 5/16"; UNIT_RAD+((A/2)+.25")=3' - 7 13/32"; UNIT_RAD+((A/2)+.25")+4"=3' - 11 13/32"; UNIT_RADIUS=1' - 7 5/32"; UNIT_RADIUS*.6=1' - 5 1/4"; UNIT_RADIUS+4"=1' - 11 5/32"
- 270_QMXHPVP-24L-1X3_Mixing_Box: (A/2)+.25"=2' - 0 1/4"; (A/2)-2"=1' - 10"; (NOZZLE_HEIGHT-(NOZZLE_HEIGHT/8*2))/2=1' - 11 1/4"; (NOZZLE_WB_OD-NOZZLE_TOP_OD)/2=0' - 6 1/8"; -A=-4' - 0"; A=4' - 0"; A+.5=4' - 0 1/2"; A/2=2' - 0"; B=10' - 8"; B/2=5' - 4"; C=5' - 3"; C/2=2' - 7 1/2"; DUAL_F=9' - 4 1/4"; DUAL_F+1"=9' - 5 1/4"; DUAL_G=9' - 3 1/8"; E=3' - 10 15/16"; GA=0' - 0 3/32"; LONG_RO=14' - 1 1/16"; MB_A=5' - 2"; MB_HT=3' - 11 3/16"; MB_HT+.25"=3' - 11 7/16"; MB_HT-2.75"=3' - 8 7/16"; MB_HT/2=1' - 11 19/32"; Model=QMXHPVP-1X3_Mixing Box; NOZZLE_BOTTOM_ID=2' - 10 3/4"; NOZZLE_BOTTOM_RAD=1' - 5 3/8"; NOZZLE_HEIGHT=5' - 2"; NOZZLE_HEIGHT/7*2=1' - 3 1/2"; NOZZLE_SIZE=24' - 0"; NOZZLE_TOP_OD=3' - 0 1/2"; NOZZLE_TOP_RAD=1' - 6 1/4"; NOZZLE_WB/4=1' - 0 3/16"; NOZZLE_WB_OD=5' - 1"; NOZZLE_WB_RAD=2' - 6 1/2"; NOZZLE_WB_RAD-2"=2' - 4 1/2"; RO=3' - 4 3/4"; RO/2=1' - 8 3/8"; RO2/2=1' - 8 3/8"; TRANSITION_TOP=5' - 2 1/4"; TRIPLE_F+1"=14' - 9"; TRIP_F=14' - 8"; TRIP_G=14' - 7 5/16"; TYPE=1' - 0"; Type Comments=Vari-Plume Laboratory Exhaust Mixed-Flow High Pressure Inline Belt Drive With 1X3 Mixing Box; UNIT_HEIGHT=3' - 11"; UNIT_HEIGHT*.75=2' - 11 1/4"; UNIT_OD=3' - 2 5/16"; UNIT_RAD+((A/2)+.25")=3' - 7 13/32"; UNIT_RAD+((A/2)+.25")+4"=3' - 11 13/32"; UNIT_RADIUS=1' - 7 5/32"; UNIT_RADIUS*.6=1' - 5 1/4"; UNIT_RADIUS+4"=1' - 11 5/32"
- 300_QMXHPVP-18H-1X3_Mixing_Box: (A/2)+.25"=2' - 2 1/4"; (A/2)-2"=2' - 0"; (NOZZLE_HEIGHT-(NOZZLE_HEIGHT/8*2))/2=1' - 6"; (NOZZLE_WB_OD-NOZZLE_TOP_OD)/2=0' - 3 7/8"; -A=-4' - 4"; A=4' - 4"; A+.5=4' - 4 1/2"; A/2=2' - 2"; B=12' - 4"; B/2=6' - 2"; C=5' - 7"; C/2=2' - 9 1/2"; DUAL_F=11' - 0 1/4"; DUAL_F+1"=11' - 1 1/4"; DUAL_G=10' - 11 1/8"; E=4' - 2 15/16"; GA=0' - 0 3/32"; LONG_RO=17' - 1 1/16"; MB_A=5' - 8"; MB_HT=4' - 2 7/16"; MB_HT+.25"=4' - 2 11/16"; MB_HT-2.75"=3' - 11 11/16"; MB_HT/2=2' - 1 7/32"; Model=QMXHPVP-1X3_Mixing Box; NOZZLE_BOTTOM_ID=2' - 1 5/8"; NOZZLE_BOTTOM_RAD=1' - 0 13/16"; NOZZLE_HEIGHT=4' - 0"; NOZZLE_HEIGHT/7*2=1' - 0"; NOZZLE_SIZE=18' - 0"; NOZZLE_TOP_OD=2' - 3 1/2"; NOZZLE_TOP_RAD=1' - 1 3/4"; NOZZLE_WB/4=0' - 8 19/32"; NOZZLE_WB_OD=3' - 7"; NOZZLE_WB_RAD=1' - 9 1/2"; NOZZLE_WB_RAD-2"=1' - 7 1/2"; RO=3' - 8 3/4"; RO/2=1' - 10 3/8"; RO2/2=1' - 10 3/8"; TRANSITION_TOP=7' - 10 3/16"; TRIPLE_F+1"=17' - 9"; TRIP_F=17' - 8"; TRIP_G=17' - 7 5/16"; TYPE=1' - 0"; Type Comments=Vari-Plume Laboratory Exhaust Mixed-Flow High Pressure Inline Belt Drive With 1X3 Mixing Box; UNIT_HEIGHT=4' - 6"; UNIT_HEIGHT*.75=3' - 4 1/2"; UNIT_OD=3' - 6 1/2"; UNIT_RAD+((A/2)+.25")=3' - 11 1/2"; UNIT_RAD+((A/2)+.25")+4"=4' - 3 1/2"; UNIT_RADIUS=1' - 9 1/4"; UNIT_RADIUS*.6=1' - 7 1/8"; UNIT_RADIUS+4"=2' - 1 1/4"
- 300_QMXHPVP-18L-1X3_Mixing_Box: (A/2)+.25"=2' - 2 1/4"; (A/2)-2"=2' - 0"; (NOZZLE_HEIGHT-(NOZZLE_HEIGHT/8*2))/2=1' - 6"; (NOZZLE_WB_OD-NOZZLE_TOP_OD)/2=0' - 3 7/8"; -A=-4' - 4"; A=4' - 4"; A+.5=4' - 4 1/2"; A/2=2' - 2"; B=12' - 4"; B/2=6' - 2"; C=5' - 7"; C/2=2' - 9 1/2"; DUAL_F=11' - 0 1/4"; DUAL_F+1"=11' - 1 1/4"; DUAL_G=10' - 11 1/8"; E=4' - 2 15/16"; GA=0' - 0 3/32"; LONG_RO=17' - 1 1/16"; MB_A=5' - 8"; MB_HT=4' - 2 7/16"; MB_HT+.25"=4' - 2 11/16"; MB_HT-2.75"=3' - 11 11/16"; MB_HT/2=2' - 1 7/32"; Model=QMXHPVP-1X3_Mixing Box; NOZZLE_BOTTOM_ID=2' - 1 5/8"; NOZZLE_BOTTOM_RAD=1' - 0 13/16"; NOZZLE_HEIGHT=4' - 0"; NOZZLE_HEIGHT/7*2=1' - 0"; NOZZLE_SIZE=18' - 0"; NOZZLE_TOP_OD=2' - 3 1/2"; NOZZLE_TOP_RAD=1' - 1 3/4"; NOZZLE_WB/4=0' - 8 19/32"; NOZZLE_WB_OD=3' - 7"; NOZZLE_WB_RAD=1' - 9 1/2"; NOZZLE_WB_RAD-2"=1' - 7 1/2"; RO=3' - 8 3/4"; RO/2=1' - 10 3/8"; RO2/2=1' - 10 3/8"; TRANSITION_TOP=7' - 10 3/16"; TRIPLE_F+1"=17' - 9"; TRIP_F=17' - 8"; TRIP_G=17' - 7 5/16"; TYPE=1' - 0"; Type Comments=Vari-Plume Laboratory Exhaust Mixed-Flow High Pressure Inline Belt Drive With 1X3 Mixing Box; UNIT_HEIGHT=4' - 6"; UNIT_HEIGHT*.75=3' - 4 1/2"; UNIT_OD=3' - 6 1/2"; UNIT_RAD+((A/2)+.25")=3' - 11 1/2"; UNIT_RAD+((A/2)+.25")+4"=4' - 3 1/2"; UNIT_RADIUS=1' - 9 1/4"; UNIT_RADIUS*.6=1' - 7 1/8"; UNIT_RADIUS+4"=2' - 1 1/4"
- 300_QMXHPVP-24H-1X3_Mixing_Box: (A/2)+.25"=2' - 2 1/4"; (A/2)-2"=2' - 0"; (NOZZLE_HEIGHT-(NOZZLE_HEIGHT/8*2))/2=1' - 11 1/4"; (NOZZLE_WB_OD-NOZZLE_TOP_OD)/2=0' - 6 1/8"; -A=-4' - 4"; A=4' - 4"; A+.5=4' - 4 1/2"; A/2=2' - 2"; B=12' - 4"; B/2=6' - 2"; C=5' - 7"; C/2=2' - 9 1/2"; DUAL_F=11' - 0 1/4"; DUAL_F+1"=11' - 1 1/4"; DUAL_G=10' - 11 1/8"; E=4' - 2 15/16"; GA=0' - 0 3/32"; LONG_RO=17' - 1 1/16"; MB_A=5' - 8"; MB_HT=4' - 2 7/16"; MB_HT+.25"=4' - 2 11/16"; MB_HT-2.75"=3' - 11 11/16"; MB_HT/2=2' - 1 7/32"; Model=QMXHPVP-1X3_Mixing Box; NOZZLE_BOTTOM_ID=2' - 10 3/4"; NOZZLE_BOTTOM_RAD=1' - 5 3/8"; NOZZLE_HEIGHT=5' - 2"; NOZZLE_HEIGHT/7*2=1' - 3 1/2"; NOZZLE_SIZE=24' - 0"; NOZZLE_TOP_OD=3' - 0 1/2"; NOZZLE_TOP_RAD=1' - 6 1/4"; NOZZLE_WB/4=1' - 0 3/16"; NOZZLE_WB_OD=5' - 1"; NOZZLE_WB_RAD=2' - 6 1/2"; NOZZLE_WB_RAD-2"=2' - 4 1/2"; RO=3' - 8 3/4"; RO/2=1' - 10 3/8"; RO2/2=1' - 10 3/8"; TRANSITION_TOP=6' - 5 1/4"; TRIPLE_F+1"=17' - 9"; TRIP_F=17' - 8"; TRIP_G=17' - 7 5/16"; TYPE=1' - 0"; Type Comments=Vari-Plume Laboratory Exhaust Mixed-Flow High Pressure Inline Belt Drive With 1X3 Mixing Box; UNIT_HEIGHT=4' - 6"; UNIT_HEIGHT*.75=3' - 4 1/2"; UNIT_OD=3' - 6 1/2"; UNIT_RAD+((A/2)+.25")=3' - 11 1/2"; UNIT_RAD+((A/2)+.25")+4"=4' - 3 1/2"; UNIT_RADIUS=1' - 9 1/4"; UNIT_RADIUS*.6=1' - 7 1/8"; UNIT_RADIUS+4"=2' - 1 1/4"
- 300_QMXHPVP-24L-1X3_Mixing_Box: (A/2)+.25"=2' - 2 1/4"; (A/2)-2"=2' - 0"; (NOZZLE_HEIGHT-(NOZZLE_HEIGHT/8*2))/2=1' - 11 1/4"; (NOZZLE_WB_OD-NOZZLE_TOP_OD)/2=0' - 6 1/8"; -A=-4' - 4"; A=4' - 4"; A+.5=4' - 4 1/2"; A/2=2' - 2"; B=12' - 4"; B/2=6' - 2"; C=5' - 7"; C/2=2' - 9 1/2"; DUAL_F=11' - 0 1/4"; DUAL_F+1"=11' - 1 1/4"; DUAL_G=10' - 11 1/8"; E=4' - 2 15/16"; GA=0' - 0 3/32"; LONG_RO=17' - 1 1/16"; MB_A=5' - 8"; MB_HT=4' - 2 7/16"; MB_HT+.25"=4' - 2 11/16"; MB_HT-2.75"=3' - 11 11/16"; MB_HT/2=2' - 1 7/32"; Model=QMXHPVP-1X3_Mixing Box; NOZZLE_BOTTOM_ID=2' - 10 3/4"; NOZZLE_BOTTOM_RAD=1' - 5 3/8"; NOZZLE_HEIGHT=5' - 2"; NOZZLE_HEIGHT/7*2=1' - 3 1/2"; NOZZLE_SIZE=24' - 0"; NOZZLE_TOP_OD=3' - 0 1/2"; NOZZLE_TOP_RAD=1' - 6 1/4"; NOZZLE_WB/4=1' - 0 3/16"; NOZZLE_WB_OD=5' - 1"; NOZZLE_WB_RAD=2' - 6 1/2"; NOZZLE_WB_RAD-2"=2' - 4 1/2"; RO=3' - 8 3/4"; RO/2=1' - 10 3/8"; RO2/2=1' - 10 3/8"; TRANSITION_TOP=6' - 5 1/4"; TRIPLE_F+1"=17' - 9"; TRIP_F=17' - 8"; TRIP_G=17' - 7 5/16"; TYPE=1' - 0"; Type Comments=Vari-Plume Laboratory Exhaust Mixed-Flow High Pressure Inline Belt Drive With 1X3 Mixing Box; UNIT_HEIGHT=4' - 6"; UNIT_HEIGHT*.75=3' - 4 1/2"; UNIT_OD=3' - 6 1/2"; UNIT_RAD+((A/2)+.25")=3' - 11 1/2"; UNIT_RAD+((A/2)+.25")+4"=4' - 3 1/2"; UNIT_RADIUS=1' - 9 1/4"; UNIT_RADIUS*.6=1' - 7 1/8"; UNIT_RADIUS+4"=2' - 1 1/4"
- 300_QMXHPVP-30H-1X3_Mixing_Box: (A/2)+.25"=2' - 2 1/4"; (A/2)-2"=2' - 0"; (NOZZLE_HEIGHT-(NOZZLE_HEIGHT/8*2))/2=2' - 5 1/4"; (NOZZLE_WB_OD-NOZZLE_TOP_OD)/2=0' - 7 1/8"; -A=-4' - 4"; A=4' - 4"; A+.5=4' - 4 1/2"; A/2=2' - 2"; B=12' - 4"; B/2=6' - 2"; C=5' - 7"; C/2=2' - 9 1/2"; DUAL_F=11' - 0 1/4"; DUAL_F+1"=11' - 1 1/4"; DUAL_G=10' - 11 1/8"; E=4' - 2 15/16"; GA=0' - 0 3/32"; LONG_RO=17' - 1 1/16"; MB_A=5' - 8"; MB_HT=4' - 2 7/16"; MB_HT+.25"=4' - 2 11/16"; MB_HT-2.75"=3' - 11 11/16"; MB_HT/2=2' - 1 7/32"; Model=QMXHPVP-1X3_Mixing Box; NOZZLE_BOTTOM_ID=3' - 6 1/2"; NOZZLE_BOTTOM_RAD=1' - 9 1/4"; NOZZLE_HEIGHT=6' - 6"; NOZZLE_HEIGHT/7*2=1' - 7 1/2"; NOZZLE_SIZE=30' - 0"; NOZZLE_TOP_OD=3' - 9 1/2"; NOZZLE_TOP_RAD=1' - 10 3/4"; NOZZLE_WB/4=1' - 2 13/16"; NOZZLE_WB_OD=6' - 2"; NOZZLE_WB_RAD=3' - 1"; NOZZLE_WB_RAD-2"=2' - 11"; RO=3' - 8 3/4"; RO/2=1' - 10 3/8"; RO2/2=1' - 10 3/8"; TRANSITION_TOP=5' - 8 1/4"; TRIPLE_F+1"=17' - 9"; TRIP_F=17' - 8"; TRIP_G=17' - 7 5/16"; TYPE=1' - 0"; Type Comments=Vari-Plume Laboratory Exhaust Mixed-Flow High Pressure Inline Belt Drive With 1X3 Mixing Box; UNIT_HEIGHT=4' - 6"; UNIT_HEIGHT*.75=3' - 4 1/2"; UNIT_OD=3' - 6 1/2"; UNIT_RAD+((A/2)+.25")=3' - 11 1/2"; UNIT_RAD+((A/2)+.25")+4"=4' - 3 1/2"; UNIT_RADIUS=1' - 9 1/4"; UNIT_RADIUS*.6=1' - 7 1/8"; UNIT_RADIUS+4"=2' - 1 1/4"
- 300_QMXHPVP-30L-1X3_Mixing_Box: (A/2)+.25"=2' - 2 1/4"; (A/2)-2"=2' - 0"; (NOZZLE_HEIGHT-(NOZZLE_HEIGHT/8*2))/2=2' - 5 1/4"; (NOZZLE_WB_OD-NOZZLE_TOP_OD)/2=0' - 7 1/8"; -A=-4' - 4"; A=4' - 4"; A+.5=4' - 4 1/2"; A/2=2' - 2"; B=12' - 4"; B/2=6' - 2"; C=5' - 7"; C/2=2' - 9 1/2"; DUAL_F=11' - 0 1/4"; DUAL_F+1"=11' - 1 1/4"; DUAL_G=10' - 11 1/8"; E=4' - 2 15/16"; GA=0' - 0 3/32"; LONG_RO=17' - 1 1/16"; MB_A=5' - 8"; MB_HT=4' - 2 7/16"; MB_HT+.25"=4' - 2 11/16"; MB_HT-2.75"=3' - 11 11/16"; MB_HT/2=2' - 1 7/32"; Model=QMXHPVP-1X3_Mixing Box; NOZZLE_BOTTOM_ID=3' - 6 1/2"; NOZZLE_BOTTOM_RAD=1' - 9 1/4"; NOZZLE_HEIGHT=6' - 6"; NOZZLE_HEIGHT/7*2=1' - 7 1/2"; NOZZLE_SIZE=30' - 0"; NOZZLE_TOP_OD=3' - 9 1/2"; NOZZLE_TOP_RAD=1' - 10 3/4"; NOZZLE_WB/4=1' - 2 13/16"; NOZZLE_WB_OD=6' - 2"; NOZZLE_WB_RAD=3' - 1"; NOZZLE_WB_RAD-2"=2' - 11"; RO=3' - 8 3/4"; RO/2=1' - 10 3/8"; RO2/2=1' - 10 3/8"; TRANSITION_TOP=5' - 8 1/4"; TRIPLE_F+1"=17' - 9"; TRIP_F=17' - 8"; TRIP_G=17' - 7 5/16"; TYPE=1' - 0"; Type Comments=Vari-Plume Laboratory Exhaust Mixed-Flow High Pressure Inline Belt Drive With 1X3 Mixing Box; UNIT_HEIGHT=4' - 6"; UNIT_HEIGHT*.75=3' - 4 1/2"; UNIT_OD=3' - 6 1/2"; UNIT_RAD+((A/2)+.25")=3' - 11 1/2"; UNIT_RAD+((A/2)+.25")+4"=4' - 3 1/2"; UNIT_RADIUS=1' - 9 1/4"; UNIT_RADIUS*.6=1' - 7 1/8"; UNIT_RADIUS+4"=2' - 1 1/4"
- 330_QMXHPVP-24H-1X3_Mixing_Box: (A/2)+.25"=2' - 4 1/4"; (A/2)-2"=2' - 2"; (NOZZLE_HEIGHT-(NOZZLE_HEIGHT/8*2))/2=1' - 11 1/4"; (NOZZLE_WB_OD-NOZZLE_TOP_OD)/2=0' - 6 1/8"; -A=-4' - 8"; A=4' - 8"; A+.5=4' - 8 1/2"; A/2=2' - 4"; B=12' - 10"; B/2=6' - 5"; C=6' - 1"; C/2=3' - 0 1/2"; DUAL_F=11' - 4 1/4"; DUAL_F+1"=11' - 5 1/4"; DUAL_G=11' - 3 1/8"; E=4' - 6 13/16"; GA=0' - 0 3/32"; LONG_RO=17' - 5 1/16"; MB_A=6' - 1"; MB_HT=4' - 5 11/16"; MB_HT+.25"=4' - 5 15/16"; MB_HT-2.75"=4' - 2 15/16"; MB_HT/2=2' - 2 27/32"; Model=QMXHPVP-1X3_Mixing Box; NOZZLE_BOTTOM_ID=2' - 10 3/4"; NOZZLE_BOTTOM_RAD=1' - 5 3/8"; NOZZLE_HEIGHT=5' - 2"; NOZZLE_HEIGHT/7*2=1' - 3 1/2"; NOZZLE_SIZE=24' - 0"; NOZZLE_TOP_OD=3' - 0 1/2"; NOZZLE_TOP_RAD=1' - 6 1/4"; NOZZLE_WB/4=1' - 0 3/16"; NOZZLE_WB_OD=5' - 1"; NOZZLE_WB_RAD=2' - 6 1/2"; NOZZLE_WB_RAD-2"=2' - 4 1/2"; RO=4' - 0 5/8"; RO/2=2' - 0 5/16"; RO2/2=2' - 0 5/16"; TRANSITION_TOP=7' - 5 3/4"; TRIPLE_F+1"=18' - 1"; TRIP_F=18' - 0"; TRIP_G=17' - 11 5/16"; TYPE=1' - 0"; Type Comments=Vari-Plume Laboratory Exhaust Mixed-Flow High Pressure Inline Belt Drive With 1X3 Mixing Box; UNIT_HEIGHT=4' - 10 1/2"; UNIT_HEIGHT*.75=3' - 7 7/8"; UNIT_OD=3' - 10 3/4"; UNIT_RAD+((A/2)+.25")=4' - 3 5/8"; UNIT_RAD+((A/2)+.25")+4"=4' - 7 5/8"; UNIT_RADIUS=1' - 11 3/8"; UNIT_RADIUS*.6=1' - 9 1/32"; UNIT_RADIUS+4"=2' - 3 3/8"
- 330_QMXHPVP-24L-1X3_Mixing_Box: (A/2)+.25"=2' - 4 1/4"; (A/2)-2"=2' - 2"; (NOZZLE_HEIGHT-(NOZZLE_HEIGHT/8*2))/2=1' - 11 1/4"; (NOZZLE_WB_OD-NOZZLE_TOP_OD)/2=0' - 6 1/8"; -A=-4' - 8"; A=4' - 8"; A+.5=4' - 8 1/2"; A/2=2' - 4"; B=12' - 10"; B/2=6' - 5"; C=6' - 1"; C/2=3' - 0 1/2"; DUAL_F=11' - 4 1/4"; DUAL_F+1"=11' - 5 1/4"; DUAL_G=11' - 3 1/8"; E=4' - 6 13/16"; GA=0' - 0 3/32"; LONG_RO=17' - 5 1/16"; MB_A=6' - 1"; MB_HT=4' - 5 11/16"; MB_HT+.25"=4' - 5 15/16"; MB_HT-2.75"=4' - 2 15/16"; MB_HT/2=2' - 2 27/32"; Model=QMXHPVP-1X3_Mixing Box; NOZZLE_BOTTOM_ID=2' - 10 3/4"; NOZZLE_BOTTOM_RAD=1' - 5 3/8"; NOZZLE_HEIGHT=5' - 2"; NOZZLE_HEIGHT/7*2=1' - 3 1/2"; NOZZLE_SIZE=24' - 0"; NOZZLE_TOP_OD=3' - 0 1/2"; NOZZLE_TOP_RAD=1' - 6 1/4"; NOZZLE_WB/4=1' - 0 3/16"; NOZZLE_WB_OD=5' - 1"; NOZZLE_WB_RAD=2' - 6 1/2"; NOZZLE_WB_RAD-2"=2' - 4 1/2"; RO=4' - 0 5/8"; RO/2=2' - 0 5/16"; RO2/2=2' - 0 5/16"; TRANSITION_TOP=7' - 5 3/4"; TRIPLE_F+1"=18' - 1"; TRIP_F=18' - 0"; TRIP_G=17' - 11 5/16"; TYPE=1' - 0"; Type Comments=Vari-Plume Laboratory Exhaust Mixed-Flow High Pressure Inline Belt Drive With 1X3 Mixing Box; UNIT_HEIGHT=4' - 10 1/2"; UNIT_HEIGHT*.75=3' - 7 7/8"; UNIT_OD=3' - 10 3/4"; UNIT_RAD+((A/2)+.25")=4' - 3 5/8"; UNIT_RAD+((A/2)+.25")+4"=4' - 7 5/8"; UNIT_RADIUS=1' - 11 3/8"; UNIT_RADIUS*.6=1' - 9 1/32"; UNIT_RADIUS+4"=2' - 3 3/8"
- 330_QMXHPVP-30H-1X3_Mixing_Box: (A/2)+.25"=2' - 4 1/4"; (A/2)-2"=2' - 2"; (NOZZLE_HEIGHT-(NOZZLE_HEIGHT/8*2))/2=2' - 5 1/4"; (NOZZLE_WB_OD-NOZZLE_TOP_OD)/2=0' - 7 1/8"; -A=-4' - 8"; A=4' - 8"; A+.5=4' - 8 1/2"; A/2=2' - 4"; B=12' - 10"; B/2=6' - 5"; C=6' - 1"; C/2=3' - 0 1/2"; DUAL_F=11' - 4 1/4"; DUAL_F+1"=11' - 5 1/4"; DUAL_G=11' - 3 1/8"; E=4' - 6 13/16"; GA=0' - 0 3/32"; LONG_RO=17' - 5 1/16"; MB_A=6' - 1"; MB_HT=4' - 5 11/16"; MB_HT+.25"=4' - 5 15/16"; MB_HT-2.75"=4' - 2 15/16"; MB_HT/2=2' - 2 27/32"; Model=QMXHPVP-1X3_Mixing Box; NOZZLE_BOTTOM_ID=3' - 6 1/2"; NOZZLE_BOTTOM_RAD=1' - 9 1/4"; NOZZLE_HEIGHT=6' - 6"; NOZZLE_HEIGHT/7*2=1' - 7 1/2"; NOZZLE_SIZE=30' - 0"; NOZZLE_TOP_OD=3' - 9 1/2"; NOZZLE_TOP_RAD=1' - 10 3/4"; NOZZLE_WB/4=1' - 2 13/16"; NOZZLE_WB_OD=6' - 2"; NOZZLE_WB_RAD=3' - 1"; NOZZLE_WB_RAD-2"=2' - 11"; RO=4' - 0 5/8"; RO/2=2' - 0 5/16"; RO2/2=2' - 0 5/16"; TRANSITION_TOP=6' - 2 3/4"; TRIPLE_F+1"=18' - 1"; TRIP_F=18' - 0"; TRIP_G=17' - 11 5/16"; TYPE=1' - 0"; Type Comments=Vari-Plume Laboratory Exhaust Mixed-Flow High Pressure Inline Belt Drive With 1X3 Mixing Box; UNIT_HEIGHT=4' - 10 1/2"; UNIT_HEIGHT*.75=3' - 7 7/8"; UNIT_OD=3' - 10 3/4"; UNIT_RAD+((A/2)+.25")=4' - 3 5/8"; UNIT_RAD+((A/2)+.25")+4"=4' - 7 5/8"; UNIT_RADIUS=1' - 11 3/8"; UNIT_RADIUS*.6=1' - 9 1/32"; UNIT_RADIUS+4"=2' - 3 3/8"
- 330_QMXHPVP-30L-1X3_Mixing_Box: (A/2)+.25"=2' - 4 1/4"; (A/2)-2"=2' - 2"; (NOZZLE_HEIGHT-(NOZZLE_HEIGHT/8*2))/2=2' - 5 1/4"; (NOZZLE_WB_OD-NOZZLE_TOP_OD)/2=0' - 7 1/8"; -A=-4' - 8"; A=4' - 8"; A+.5=4' - 8 1/2"; A/2=2' - 4"; B=12' - 10"; B/2=6' - 5"; C=6' - 1"; C/2=3' - 0 1/2"; DUAL_F=11' - 4 1/4"; DUAL_F+1"=11' - 5 1/4"; DUAL_G=11' - 3 1/8"; E=4' - 6 13/16"; GA=0' - 0 3/32"; LONG_RO=17' - 5 1/16"; MB_A=6' - 1"; MB_HT=4' - 5 11/16"; MB_HT+.25"=4' - 5 15/16"; MB_HT-2.75"=4' - 2 15/16"; MB_HT/2=2' - 2 27/32"; Model=QMXHPVP-1X3_Mixing Box; NOZZLE_BOTTOM_ID=3' - 6 1/2"; NOZZLE_BOTTOM_RAD=1' - 9 1/4"; NOZZLE_HEIGHT=6' - 6"; NOZZLE_HEIGHT/7*2=1' - 7 1/2"; NOZZLE_SIZE=30' - 0"; NOZZLE_TOP_OD=3' - 9 1/2"; NOZZLE_TOP_RAD=1' - 10 3/4"; NOZZLE_WB/4=1' - 2 13/16"; NOZZLE_WB_OD=6' - 2"; NOZZLE_WB_RAD=3' - 1"; NOZZLE_WB_RAD-2"=2' - 11"; RO=4' - 0 5/8"; RO/2=2' - 0 5/16"; RO2/2=2' - 0 5/16"; TRANSITION_TOP=6' - 2 3/4"; TRIPLE_F+1"=18' - 1"; TRIP_F=18' - 0"; TRIP_G=17' - 11 5/16"; TYPE=1' - 0"; Type Comments=Vari-Plume Laboratory Exhaust Mixed-Flow High Pressure Inline Belt Drive With 1X3 Mixing Box; UNIT_HEIGHT=4' - 10 1/2"; UNIT_HEIGHT*.75=3' - 7 7/8"; UNIT_OD=3' - 10 3/4"; UNIT_RAD+((A/2)+.25")=4' - 3 5/8"; UNIT_RAD+((A/2)+.25")+4"=4' - 7 5/8"; UNIT_RADIUS=1' - 11 3/8"; UNIT_RADIUS*.6=1' - 9 1/32"; UNIT_RADIUS+4"=2' - 3 3/8"
- 365_QMXHPVP-24H-1X3_Mixing_Box: (A/2)+.25"=2' - 7 1/4"; (A/2)-2"=2' - 5"; (NOZZLE_HEIGHT-(NOZZLE_HEIGHT/8*2))/2=1' - 11 1/4"; (NOZZLE_WB_OD-NOZZLE_TOP_OD)/2=0' - 6 1/8"; -A=-5' - 2"; A=5' - 2"; A+.5=5' - 2 1/2"; A/2=2' - 7"; B=14' - 7"; B/2=7' - 3 1/2"; C=6' - 7"; C/2=3' - 3 1/2"; DUAL_F=13' - 3 3/4"; DUAL_F+1"=13' - 4 3/4"; DUAL_G=13' - 2"; E=5' - 0 3/4"; GA=0' - 0 3/32"; LONG_RO=20' - 9"; MB_A=6' - 10"; MB_HT=4' - 11 11/16"; MB_HT+.25"=4' - 11 15/16"; MB_HT-2.75"=4' - 8 15/16"; MB_HT/2=2' - 5 27/32"; Model=QMXHPVP-1X3_Mixing Box; NOZZLE_BOTTOM_ID=2' - 10 3/4"; NOZZLE_BOTTOM_RAD=1' - 5 3/8"; NOZZLE_HEIGHT=5' - 2"; NOZZLE_HEIGHT/7*2=1' - 3 1/2"; NOZZLE_SIZE=24' - 0"; NOZZLE_TOP_OD=3' - 0 1/2"; NOZZLE_TOP_RAD=1' - 6 1/4"; NOZZLE_WB/4=1' - 0 3/16"; NOZZLE_WB_OD=5' - 1"; NOZZLE_WB_RAD=2' - 6 1/2"; NOZZLE_WB_RAD-2"=2' - 4 1/2"; RO=4' - 6 1/2"; RO/2=2' - 3 1/4"; RO2/2=2' - 3 1/4"; TRANSITION_TOP=8' - 8 1/4"; TRIPLE_F+1"=21' - 6"; TRIP_F=21' - 5"; TRIP_G=21' - 3 1/4"; TYPE=1' - 0"; Type Comments=Vari-Plume Laboratory Exhaust Mixed-Flow High Pressure Inline Belt Drive With 1X3 Mixing Box; UNIT_HEIGHT=5' - 4"; UNIT_HEIGHT*.75=4' - 0"; UNIT_OD=4' - 3 3/4"; UNIT_RAD+((A/2)+.25")=4' - 9 1/8"; UNIT_RAD+((A/2)+.25")+4"=5' - 1 1/8"; UNIT_RADIUS=2' - 1 7/8"; UNIT_RADIUS*.6=1' - 11 9/32"; UNIT_RADIUS+4"=2' - 5 7/8"
- 365_QMXHPVP-24L-1X3_Mixing_Box: (A/2)+.25"=2' - 7 1/4"; (A/2)-2"=2' - 5"; (NOZZLE_HEIGHT-(NOZZLE_HEIGHT/8*2))/2=1' - 11 1/4"; (NOZZLE_WB_OD-NOZZLE_TOP_OD)/2=0' - 6 1/8"; -A=-5' - 2"; A=5' - 2"; A+.5=5' - 2 1/2"; A/2=2' - 7"; B=14' - 7"; B/2=7' - 3 1/2"; C=6' - 7"; C/2=3' - 3 1/2"; DUAL_F=13' - 3 3/4"; DUAL_F+1"=13' - 4 3/4"; DUAL_G=13' - 2"; E=5' - 0 3/4"; GA=0' - 0 3/32"; LONG_RO=20' - 9"; MB_A=6' - 10"; MB_HT=4' - 11 11/16"; MB_HT+.25"=4' - 11 15/16"; MB_HT-2.75"=4' - 8 15/16"; MB_HT/2=2' - 5 27/32"; Model=QMXHPVP-1X3_Mixing Box; NOZZLE_BOTTOM_ID=2' - 10 3/4"; NOZZLE_BOTTOM_RAD=1' - 5 3/8"; NOZZLE_HEIGHT=5' - 2"; NOZZLE_HEIGHT/7*2=1' - 3 1/2"; NOZZLE_SIZE=24' - 0"; NOZZLE_TOP_OD=3' - 0 1/2"; NOZZLE_TOP_RAD=1' - 6 1/4"; NOZZLE_WB/4=1' - 0 3/16"; NOZZLE_WB_OD=5' - 1"; NOZZLE_WB_RAD=2' - 6 1/2"; NOZZLE_WB_RAD-2"=2' - 4 1/2"; RO=4' - 6 1/2"; RO/2=2' - 3 1/4"; RO2/2=2' - 3 1/4"; TRANSITION_TOP=8' - 8 1/4"; TRIPLE_F+1"=21' - 6"; TRIP_F=21' - 5"; TRIP_G=21' - 3 1/4"; TYPE=1' - 0"; Type Comments=Vari-Plume Laboratory Exhaust Mixed-Flow High Pressure Inline Belt Drive With 1X3 Mixing Box; UNIT_HEIGHT=5' - 4"; UNIT_HEIGHT*.75=4' - 0"; UNIT_OD=4' - 3 3/4"; UNIT_RAD+((A/2)+.25")=4' - 9 1/8"; UNIT_RAD+((A/2)+.25")+4"=5' - 1 1/8"; UNIT_RADIUS=2' - 1 7/8"; UNIT_RADIUS*.6=1' - 11 9/32"; UNIT_RADIUS+4"=2' - 5 7/8"
- 365_QMXHPVP-30H-1X3_Mixing_Box: (A/2)+.25"=2' - 7 1/4"; (A/2)-2"=2' - 5"; (NOZZLE_HEIGHT-(NOZZLE_HEIGHT/8*2))/2=2' - 5 1/4"; (NOZZLE_WB_OD-NOZZLE_TOP_OD)/2=0' - 7 1/8"; -A=-5' - 2"; A=5' - 2"; A+.5=5' - 2 1/2"; A/2=2' - 7"; B=14' - 7"; B/2=7' - 3 1/2"; C=6' - 7"; C/2=3' - 3 1/2"; DUAL_F=13' - 3 3/4"; DUAL_F+1"=13' - 4 3/4"; DUAL_G=13' - 2"; E=5' - 0 3/4"; GA=0' - 0 3/32"; LONG_RO=20' - 9"; MB_A=6' - 10"; MB_HT=4' - 11 11/16"; MB_HT+.25"=4' - 11 15/16"; MB_HT-2.75"=4' - 8 15/16"; MB_HT/2=2' - 5 27/32"; Model=QMXHPVP-1X3_Mixing Box; NOZZLE_BOTTOM_ID=3' - 6 1/2"; NOZZLE_BOTTOM_RAD=1' - 9 1/4"; NOZZLE_HEIGHT=6' - 6"; NOZZLE_HEIGHT/7*2=1' - 7 1/2"; NOZZLE_SIZE=30' - 0"; NOZZLE_TOP_OD=3' - 9 1/2"; NOZZLE_TOP_RAD=1' - 10 3/4"; NOZZLE_WB/4=1' - 2 13/16"; NOZZLE_WB_OD=6' - 2"; NOZZLE_WB_RAD=3' - 1"; NOZZLE_WB_RAD-2"=2' - 11"; RO=4' - 6 1/2"; RO/2=2' - 3 1/4"; RO2/2=2' - 3 1/4"; TRANSITION_TOP=7' - 5 1/2"; TRIPLE_F+1"=21' - 6"; TRIP_F=21' - 5"; TRIP_G=21' - 3 1/4"; TYPE=1' - 0"; Type Comments=Vari-Plume Laboratory Exhaust Mixed-Flow High Pressure Inline Belt Drive With 1X3 Mixing Box; UNIT_HEIGHT=5' - 4"; UNIT_HEIGHT*.75=4' - 0"; UNIT_OD=4' - 3 3/4"; UNIT_RAD+((A/2)+.25")=4' - 9 1/8"; UNIT_RAD+((A/2)+.25")+4"=5' - 1 1/8"; UNIT_RADIUS=2' - 1 7/8"; UNIT_RADIUS*.6=1' - 11 9/32"; UNIT_RADIUS+4"=2' - 5 7/8"
- 365_QMXHPVP-30L-1X3_Mixing_Box: (A/2)+.25"=2' - 7 1/4"; (A/2)-2"=2' - 5"; (NOZZLE_HEIGHT-(NOZZLE_HEIGHT/8*2))/2=2' - 5 1/4"; (NOZZLE_WB_OD-NOZZLE_TOP_OD)/2=0' - 7 1/8"; -A=-5' - 2"; A=5' - 2"; A+.5=5' - 2 1/2"; A/2=2' - 7"; B=14' - 7"; B/2=7' - 3 1/2"; C=6' - 7"; C/2=3' - 3 1/2"; DUAL_F=13' - 3 3/4"; DUAL_F+1"=13' - 4 3/4"; DUAL_G=13' - 2"; E=5' - 0 3/4"; GA=0' - 0 3/32"; LONG_RO=20' - 9"; MB_A=6' - 10"; MB_HT=4' - 11 11/16"; MB_HT+.25"=4' - 11 15/16"; MB_HT-2.75"=4' - 8 15/16"; MB_HT/2=2' - 5 27/32"; Model=QMXHPVP-1X3_Mixing Box; NOZZLE_BOTTOM_ID=3' - 6 1/2"; NOZZLE_BOTTOM_RAD=1' - 9 1/4"; NOZZLE_HEIGHT=6' - 6"; NOZZLE_HEIGHT/7*2=1' - 7 1/2"; NOZZLE_SIZE=30' - 0"; NOZZLE_TOP_OD=3' - 9 1/2"; NOZZLE_TOP_RAD=1' - 10 3/4"; NOZZLE_WB/4=1' - 2 13/16"; NOZZLE_WB_OD=6' - 2"; NOZZLE_WB_RAD=3' - 1"; NOZZLE_WB_RAD-2"=2' - 11"; RO=4' - 6 1/2"; RO/2=2' - 3 1/4"; RO2/2=2' - 3 1/4"; TRANSITION_TOP=7' - 5 1/2"; TRIPLE_F+1"=21' - 6"; TRIP_F=21' - 5"; TRIP_G=21' - 3 1/4"; TYPE=1' - 0"; Type Comments=Vari-Plume Laboratory Exhaust Mixed-Flow High Pressure Inline Belt Drive With 1X3 Mixing Box; UNIT_HEIGHT=5' - 4"; UNIT_HEIGHT*.75=4' - 0"; UNIT_OD=4' - 3 3/4"; UNIT_RAD+((A/2)+.25")=4' - 9 1/8"; UNIT_RAD+((A/2)+.25")+4"=5' - 1 1/8"; UNIT_RADIUS=2' - 1 7/8"; UNIT_RADIUS*.6=1' - 11 9/32"; UNIT_RADIUS+4"=2' - 5 7/8"
- 365_QMXVP-36H-1X3_Mixing_Box: (A/2)+.25"=2' - 7 1/4"; (A/2)-2"=2' - 5"; (NOZZLE_HEIGHT-(NOZZLE_HEIGHT/8*2))/2=2' - 11 5/8"; (NOZZLE_WB_OD-NOZZLE_TOP_OD)/2=0' - 8"; -A=-5' - 2"; A=5' - 2"; A+.5=5' - 2 1/2"; A/2=2' - 7"; B=14' - 7"; B/2=7' - 3 1/2"; C=6' - 7"; C/2=3' - 3 1/2"; DUAL_F=13' - 3 3/4"; DUAL_F+1"=13' - 4 3/4"; DUAL_G=13' - 2"; E=5' - 0 3/4"; GA=0' - 0 3/32"; LONG_RO=20' - 9"; MB_A=6' - 10"; MB_HT=4' - 11 11/16"; MB_HT+.25"=4' - 11 15/16"; MB_HT-2.75"=4' - 8 15/16"; MB_HT/2=2' - 5 27/32"; Model=QMXVP-1X3_Mixing Box; NOZZLE_BOTTOM_ID=4' - 3 3/4"; NOZZLE_BOTTOM_RAD=2' - 1 7/8"; NOZZLE_HEIGHT=7' - 11"; NOZZLE_HEIGHT/7*2=1' - 11 3/4"; NOZZLE_SIZE=36' - 0"; NOZZLE_TOP_OD=4' - 10"; NOZZLE_TOP_RAD=2' - 5"; NOZZLE_WB/4=1' - 6"; NOZZLE_WB_OD=7' - 6"; NOZZLE_WB_RAD=3' - 9"; NOZZLE_WB_RAD-2"=3' - 7"; RO=4' - 6 1/2"; RO/2=2' - 3 1/4"; RO2/2=2' - 3 1/4"; TRANSITION_TOP=6' - 6 1/4"; TRIPLE_F+1"=21' - 6"; TRIP_F=21' - 5"; TRIP_G=21' - 3 1/4"; TYPE=0' - 0"; Type Comments=Vari-Plume Laboratory Exhaust Mixed-Flow Inline Belt Drive With 1X3 Mixing Box; UNIT_HEIGHT=5' - 4"; UNIT_HEIGHT*.75=4' - 0"; UNIT_OD=4' - 3 3/4"; UNIT_RAD+((A/2)+.25")=4' - 9 1/8"; UNIT_RAD+((A/2)+.25")+4"=5' - 1 1/8"; UNIT_RADIUS=2' - 1 7/8"; UNIT_RADIUS*.6=1' - 11 9/32"; UNIT_RADIUS+4"=2' - 5 7/8"
- 365_QMXHPVP-36L-1X3_Mixing_Box: (A/2)+.25"=2' - 7 1/4"; (A/2)-2"=2' - 5"; (NOZZLE_HEIGHT-(NOZZLE_HEIGHT/8*2))/2=2' - 11 5/8"; (NOZZLE_WB_OD-NOZZLE_TOP_OD)/2=0' - 8"; -A=-5' - 2"; A=5' - 2"; A+.5=5' - 2 1/2"; A/2=2' - 7"; B=14' - 7"; B/2=7' - 3 1/2"; C=6' - 7"; C/2=3' - 3 1/2"; DUAL_F=13' - 3 3/4"; DUAL_F+1"=13' - 4 3/4"; DUAL_G=13' - 2"; E=5' - 0 3/4"; GA=0' - 0 3/32"; LONG_RO=20' - 9"; MB_A=6' - 10"; MB_HT=4' - 11 11/16"; MB_HT+.25"=4' - 11 15/16"; MB_HT-2.75"=4' - 8 15/16"; MB_HT/2=2' - 5 27/32"; Model=QMXHPVP-1X3_Mixing Box; NOZZLE_BOTTOM_ID=4' - 3 3/4"; NOZZLE_BOTTOM_RAD=2' - 1 7/8"; NOZZLE_HEIGHT=7' - 11"; NOZZLE_HEIGHT/7*2=1' - 11 3/4"; NOZZLE_SIZE=36' - 0"; NOZZLE_TOP_OD=4' - 10"; NOZZLE_TOP_RAD=2' - 5"; NOZZLE_WB/4=1' - 6"; NOZZLE_WB_OD=7' - 6"; NOZZLE_WB_RAD=3' - 9"; NOZZLE_WB_RAD-2"=3' - 7"; RO=4' - 6 1/2"; RO/2=2' - 3 1/4"; RO2/2=2' - 3 1/4"; TRANSITION_TOP=6' - 6 1/4"; TRIPLE_F+1"=21' - 6"; TRIP_F=21' - 5"; TRIP_G=21' - 3 1/4"; TYPE=1' - 0"; Type Comments=Vari-Plume Laboratory Exhaust Mixed-Flow High Pressure Inline Belt Drive With 1X3 Mixing Box; UNIT_HEIGHT=5' - 4"; UNIT_HEIGHT*.75=4' - 0"; UNIT_OD=4' - 3 3/4"; UNIT_RAD+((A/2)+.25")=4' - 9 1/8"; UNIT_RAD+((A/2)+.25")+4"=5' - 1 1/8"; UNIT_RADIUS=2' - 1 7/8"; UNIT_RADIUS*.6=1' - 11 9/32"; UNIT_RADIUS+4"=2' - 5 7/8"
- 365_QMXHPVP-36H-1X3_Mixing_Box: (A/2)+.25"=2' - 7 1/4"; (A/2)-2"=2' - 5"; (NOZZLE_HEIGHT-(NOZZLE_HEIGHT/8*2))/2=2' - 11 5/8"; (NOZZLE_WB_OD-NOZZLE_TOP_OD)/2=0' - 8"; -A=-5' - 2"; A=5' - 2"; A+.5=5' - 2 1/2"; A/2=2' - 7"; B=14' - 7"; B/2=7' - 3 1/2"; C=6' - 7"; C/2=3' - 3 1/2"; DUAL_F=13' - 3 3/4"; DUAL_F+1"=13' - 4 3/4"; DUAL_G=13' - 2"; E=5' - 0 3/4"; GA=0' - 0 3/32"; LONG_RO=20' - 9"; MB_A=6' - 10"; MB_HT=4' - 11 11/16"; MB_HT+.25"=4' - 11 15/16"; MB_HT-2.75"=4' - 8 15/16"; MB_HT/2=2' - 5 27/32"; Model=QMXHPVP-1X3_Mixing Box; NOZZLE_BOTTOM_ID=4' - 3 3/4"; NOZZLE_BOTTOM_RAD=2' - 1 7/8"; NOZZLE_HEIGHT=7' - 11"; NOZZLE_HEIGHT/7*2=1' - 11 3/4"; NOZZLE_SIZE=36' - 0"; NOZZLE_TOP_OD=4' - 10"; NOZZLE_TOP_RAD=2' - 5"; NOZZLE_WB/4=1' - 6"; NOZZLE_WB_OD=7' - 6"; NOZZLE_WB_RAD=3' - 9"; NOZZLE_WB_RAD-2"=3' - 7"; RO=4' - 6 1/2"; RO/2=2' - 3 1/4"; RO2/2=2' - 3 1/4"; TRANSITION_TOP=6' - 6 1/4"; TRIPLE_F+1"=21' - 6"; TRIP_F=21' - 5"; TRIP_G=21' - 3 1/4"; TYPE=1' - 0"; Type Comments=Vari-Plume Laboratory Exhaust Mixed-Flow High Pressure Inline Belt Drive With 1X3 Mixing Box; UNIT_HEIGHT=5' - 4"; UNIT_HEIGHT*.75=4' - 0"; UNIT_OD=4' - 3 3/4"; UNIT_RAD+((A/2)+.25")=4' - 9 1/8"; UNIT_RAD+((A/2)+.25")+4"=5' - 1 1/8"; UNIT_RADIUS=2' - 1 7/8"; UNIT_RADIUS*.6=1' - 11 9/32"; UNIT_RADIUS+4"=2' - 5 7/8"
- 402_QMXHPVP-24H-1X3_Mixing_Box: (A/2)+.25"=2' - 9 3/4"; (A/2)-2"=2' - 7 1/2"; (NOZZLE_HEIGHT-(NOZZLE_HEIGHT/8*2))/2=1' - 11 1/4"; (NOZZLE_WB_OD-NOZZLE_TOP_OD)/2=0' - 6 1/8"; -A=-5' - 7"; A=5' - 7"; A+.5=5' - 7 1/2"; A/2=2' - 9 1/2"; B=15' - 3"; B/2=7' - 7 1/2"; C=7' - 4"; C/2=3' - 8"; DUAL_F=13' - 8 3/4"; DUAL_F+1"=13' - 9 3/4"; DUAL_G=13' - 7"; E=5' - 5 3/4"; GA=0' - 0 3/32"; LONG_RO=21' - 2 1/8"; MB_A=7' - 6"; MB_HT=5' - 5 15/16"; MB_HT+.25"=5' - 6 3/16"; MB_HT-2.75"=5' - 3 3/16"; MB_HT/2=2' - 8 31/32"; Model=QMXHPVP-1X3_Mixing Box; NOZZLE_BOTTOM_ID=2' - 10 3/4"; NOZZLE_BOTTOM_RAD=1' - 5 3/8"; NOZZLE_HEIGHT=5' - 2"; NOZZLE_HEIGHT/7*2=1' - 3 1/2"; NOZZLE_SIZE=24' - 0"; NOZZLE_TOP_OD=3' - 0 1/2"; NOZZLE_TOP_RAD=1' - 6 1/4"; NOZZLE_WB/4=1' - 0 3/16"; NOZZLE_WB_OD=5' - 1"; NOZZLE_WB_RAD=2' - 6 1/2"; NOZZLE_WB_RAD-2"=2' - 4 1/2"; RO=4' - 11 7/16"; RO/2=2' - 5 23/32"; RO2/2=2' - 5 23/32"; TRANSITION_TOP=9' - 10 3/4"; TRIPLE_F+1"=21' - 11"; TRIP_F=21' - 10"; TRIP_G=21' - 8 3/8"; TYPE=1' - 0"; Type Comments=Vari-Plume Laboratory Exhaust Mixed-Flow High Pressure Inline Belt Drive With 1X3 Mixing Box; UNIT_HEIGHT=5' - 8 1/2"; UNIT_HEIGHT*.75=4' - 3 3/8"; UNIT_OD=4' - 8 15/16"; UNIT_RAD+((A/2)+.25")=5' - 2 7/32"; UNIT_RAD+((A/2)+.25")+4"=5' - 6 7/32"; UNIT_RADIUS=2' - 4 15/32"; UNIT_RADIUS*.6=2' - 1 5/8"; UNIT_RADIUS+4"=2' - 8 15/32"
- 402_QMXHPVP-24L-1X3_Mixing_Box: (A/2)+.25"=2' - 9 3/4"; (A/2)-2"=2' - 7 1/2"; (NOZZLE_HEIGHT-(NOZZLE_HEIGHT/8*2))/2=1' - 11 1/4"; (NOZZLE_WB_OD-NOZZLE_TOP_OD)/2=0' - 6 1/8"; -A=-5' - 7"; A=5' - 7"; A+.5=5' - 7 1/2"; A/2=2' - 9 1/2"; B=15' - 3"; B/2=7' - 7 1/2"; C=7' - 4"; C/2=3' - 8"; DUAL_F=13' - 8 3/4"; DUAL_F+1"=13' - 9 3/4"; DUAL_G=13' - 7"; E=5' - 5 3/4"; GA=0' - 0 3/32"; LONG_RO=21' - 2 1/8"; MB_A=7' - 6"; MB_HT=5' - 5 15/16"; MB_HT+.25"=5' - 6 3/16"; MB_HT-2.75"=5' - 3 3/16"; MB_HT/2=2' - 8 31/32"; Model=QMXHPVP-1X3_Mixing Box; NOZZLE_BOTTOM_ID=2' - 10 3/4"; NOZZLE_BOTTOM_RAD=1' - 5 3/8"; NOZZLE_HEIGHT=5' - 2"; NOZZLE_HEIGHT/7*2=1' - 3 1/2"; NOZZLE_SIZE=24' - 0"; NOZZLE_TOP_OD=3' - 0 1/2"; NOZZLE_TOP_RAD=1' - 6 1/4"; NOZZLE_WB/4=1' - 0 3/16"; NOZZLE_WB_OD=5' - 1"; NOZZLE_WB_RAD=2' - 6 1/2"; NOZZLE_WB_RAD-2"=2' - 4 1/2"; RO=4' - 11 7/16"; RO/2=2' - 5 23/32"; RO2/2=2' - 5 23/32"; TRANSITION_TOP=9' - 10 3/4"; TRIPLE_F+1"=21' - 11"; TRIP_F=21' - 10"; TRIP_G=21' - 8 3/8"; TYPE=1' - 0"; Type Comments=Vari-Plume Laboratory Exhaust Mixed-Flow High Pressure Inline Belt Drive With 1X3 Mixing Box; UNIT_HEIGHT=5' - 8 1/2"; UNIT_HEIGHT*.75=4' - 3 3/8"; UNIT_OD=4' - 8 15/16"; UNIT_RAD+((A/2)+.25")=5' - 2 7/32"; UNIT_RAD+((A/2)+.25")+4"=5' - 6 7/32"; UNIT_RADIUS=2' - 4 15/32"; UNIT_RADIUS*.6=2' - 1 5/8"; UNIT_RADIUS+4"=2' - 8 15/32"
- 402_QMXHPVP-30H-1X3_Mixing_Box: (A/2)+.25"=2' - 9 3/4"; (A/2)-2"=2' - 7 1/2"; (NOZZLE_HEIGHT-(NOZZLE_HEIGHT/8*2))/2=2' - 5 1/4"; (NOZZLE_WB_OD-NOZZLE_TOP_OD)/2=0' - 7 1/8"; -A=-5' - 7"; A=5' - 7"; A+.5=5' - 7 1/2"; A/2=2' - 9 1/2"; B=15' - 3"; B/2=7' - 7 1/2"; C=7' - 4"; C/2=3' - 8"; DUAL_F=13' - 8 3/4"; DUAL_F+1"=13' - 9 3/4"; DUAL_G=13' - 7"; E=5' - 5 3/4"; GA=0' - 0 3/32"; LONG_RO=21' - 2 1/8"; MB_A=7' - 6"; MB_HT=5' - 5 15/16"; MB_HT+.25"=5' - 6 3/16"; MB_HT-2.75"=5' - 3 3/16"; MB_HT/2=2' - 8 31/32"; Model=QMXHPVP-1X3_Mixing Box; NOZZLE_BOTTOM_ID=3' - 6 1/2"; NOZZLE_BOTTOM_RAD=1' - 9 1/4"; NOZZLE_HEIGHT=6' - 6"; NOZZLE_HEIGHT/7*2=1' - 7 1/2"; NOZZLE_SIZE=30' - 0"; NOZZLE_TOP_OD=3' - 9 1/2"; NOZZLE_TOP_RAD=1' - 10 3/4"; NOZZLE_WB/4=1' - 2 13/16"; NOZZLE_WB_OD=6' - 2"; NOZZLE_WB_RAD=3' - 1"; NOZZLE_WB_RAD-2"=2' - 11"; RO=4' - 11 7/16"; RO/2=2' - 5 23/32"; RO2/2=2' - 5 23/32"; TRANSITION_TOP=8' - 7 3/4"; TRIPLE_F+1"=21' - 11"; TRIP_F=21' - 10"; TRIP_G=21' - 8 3/8"; TYPE=1' - 0"; Type Comments=Vari-Plume Laboratory Exhaust Mixed-Flow High Pressure Inline Belt Drive With 1X3 Mixing Box; UNIT_HEIGHT=5' - 8 1/2"; UNIT_HEIGHT*.75=4' - 3 3/8"; UNIT_OD=4' - 8 15/16"; UNIT_RAD+((A/2)+.25")=5' - 2 7/32"; UNIT_RAD+((A/2)+.25")+4"=5' - 6 7/32"; UNIT_RADIUS=2' - 4 15/32"; UNIT_RADIUS*.6=2' - 1 5/8"; UNIT_RADIUS+4"=2' - 8 15/32"
- 402_QMXHPVP-30L-1X3_Mixing_Box: (A/2)+.25"=2' - 9 3/4"; (A/2)-2"=2' - 7 1/2"; (NOZZLE_HEIGHT-(NOZZLE_HEIGHT/8*2))/2=2' - 5 1/4"; (NOZZLE_WB_OD-NOZZLE_TOP_OD)/2=0' - 7 1/8"; -A=-5' - 7"; A=5' - 7"; A+.5=5' - 7 1/2"; A/2=2' - 9 1/2"; B=15' - 3"; B/2=7' - 7 1/2"; C=7' - 4"; C/2=3' - 8"; DUAL_F=13' - 8 3/4"; DUAL_F+1"=13' - 9 3/4"; DUAL_G=13' - 7"; E=5' - 5 3/4"; GA=0' - 0 3/32"; LONG_RO=21' - 2 1/8"; MB_A=7' - 6"; MB_HT=5' - 5 15/16"; MB_HT+.25"=5' - 6 3/16"; MB_HT-2.75"=5' - 3 3/16"; MB_HT/2=2' - 8 31/32"; Model=QMXHPVP-1X3_Mixing Box; NOZZLE_BOTTOM_ID=3' - 6 1/2"; NOZZLE_BOTTOM_RAD=1' - 9 1/4"; NOZZLE_HEIGHT=6' - 6"; NOZZLE_HEIGHT/7*2=1' - 7 1/2"; NOZZLE_SIZE=30' - 0"; NOZZLE_TOP_OD=3' - 9 1/2"; NOZZLE_TOP_RAD=1' - 10 3/4"; NOZZLE_WB/4=1' - 2 13/16"; NOZZLE_WB_OD=6' - 2"; NOZZLE_WB_RAD=3' - 1"; NOZZLE_WB_RAD-2"=2' - 11"; RO=4' - 11 7/16"; RO/2=2' - 5 23/32"; RO2/2=2' - 5 23/32"; TRANSITION_TOP=8' - 7 3/4"; TRIPLE_F+1"=21' - 11"; TRIP_F=21' - 10"; TRIP_G=21' - 8 3/8"; TYPE=1' - 0"; Type Comments=Vari-Plume Laboratory Exhaust Mixed-Flow High Pressure Inline Belt Drive With 1X3 Mixing Box; UNIT_HEIGHT=5' - 8 1/2"; UNIT_HEIGHT*.75=4' - 3 3/8"; UNIT_OD=4' - 8 15/16"; UNIT_RAD+((A/2)+.25")=5' - 2 7/32"; UNIT_RAD+((A/2)+.25")+4"=5' - 6 7/32"; UNIT_RADIUS=2' - 4 15/32"; UNIT_RADIUS*.6=2' - 1 5/8"; UNIT_RADIUS+4"=2' - 8 15/32"
- 402_QMXHPVP-36H-1X3_Mixing_Box: (A/2)+.25"=2' - 9 3/4"; (A/2)-2"=2' - 7 1/2"; (NOZZLE_HEIGHT-(NOZZLE_HEIGHT/8*2))/2=2' - 11 5/8"; (NOZZLE_WB_OD-NOZZLE_TOP_OD)/2=0' - 8"; -A=-5' - 7"; A=5' - 7"; A+.5=5' - 7 1/2"; A/2=2' - 9 1/2"; B=15' - 3"; B/2=7' - 7 1/2"; C=7' - 4"; C/2=3' - 8"; DUAL_F=13' - 8 3/4"; DUAL_F+1"=13' - 9 3/4"; DUAL_G=13' - 7"; E=5' - 5 3/4"; GA=0' - 0 3/32"; LONG_RO=21' - 2 1/8"; MB_A=7' - 6"; MB_HT=5' - 5 15/16"; MB_HT+.25"=5' - 6 3/16"; MB_HT-2.75"=5' - 3 3/16"; MB_HT/2=2' - 8 31/32"; Model=QMXHPVP-1X3_Mixing Box; NOZZLE_BOTTOM_ID=4' - 3 3/4"; NOZZLE_BOTTOM_RAD=2' - 1 7/8"; NOZZLE_HEIGHT=7' - 11"; NOZZLE_HEIGHT/7*2=1' - 11 3/4"; NOZZLE_SIZE=36' - 0"; NOZZLE_TOP_OD=4' - 10"; NOZZLE_TOP_RAD=2' - 5"; NOZZLE_WB/4=1' - 6"; NOZZLE_WB_OD=7' - 6"; NOZZLE_WB_RAD=3' - 9"; NOZZLE_WB_RAD-2"=3' - 7"; RO=4' - 11 7/16"; RO/2=2' - 5 23/32"; RO2/2=2' - 5 23/32"; TRANSITION_TOP=7' - 2 3/4"; TRIPLE_F+1"=21' - 11"; TRIP_F=21' - 10"; TRIP_G=21' - 8 3/8"; TYPE=1' - 0"; Type Comments=Vari-Plume Laboratory Exhaust Mixed-Flow High Pressure Inline Belt Drive With 1X3 Mixing Box; UNIT_HEIGHT=5' - 8 1/2"; UNIT_HEIGHT*.75=4' - 3 3/8"; UNIT_OD=4' - 8 15/16"; UNIT_RAD+((A/2)+.25")=5' - 2 7/32"; UNIT_RAD+((A/2)+.25")+4"=5' - 6 7/32"; UNIT_RADIUS=2' - 4 15/32"; UNIT_RADIUS*.6=2' - 1 5/8"; UNIT_RADIUS+4"=2' - 8 15/32"
- 402_QMXHPVP-36L-1X3_Mixing_Box: (A/2)+.25"=2' - 9 3/4"; (A/2)-2"=2' - 7 1/2"; (NOZZLE_HEIGHT-(NOZZLE_HEIGHT/8*2))/2=2' - 11 5/8"; (NOZZLE_WB_OD-NOZZLE_TOP_OD)/2=0' - 8"; -A=-5' - 7"; A=5' - 7"; A+.5=5' - 7 1/2"; A/2=2' - 9 1/2"; B=15' - 3"; B/2=7' - 7 1/2"; C=7' - 4"; C/2=3' - 8"; DUAL_F=13' - 8 3/4"; DUAL_F+1"=13' - 9 3/4"; DUAL_G=13' - 7"; E=5' - 5 3/4"; GA=0' - 0 3/32"; LONG_RO=21' - 2 1/8"; MB_A=7' - 6"; MB_HT=5' - 5 15/16"; MB_HT+.25"=5' - 6 3/16"; MB_HT-2.75"=5' - 3 3/16"; MB_HT/2=2' - 8 31/32"; Model=QMXHPVP-1X3_Mixing Box; NOZZLE_BOTTOM_ID=4' - 3 3/4"; NOZZLE_BOTTOM_RAD=2' - 1 7/8"; NOZZLE_HEIGHT=7' - 11"; NOZZLE_HEIGHT/7*2=1' - 11 3/4"; NOZZLE_SIZE=36' - 0"; NOZZLE_TOP_OD=4' - 10"; NOZZLE_TOP_RAD=2' - 5"; NOZZLE_WB/4=1' - 6"; NOZZLE_WB_OD=7' - 6"; NOZZLE_WB_RAD=3' - 9"; NOZZLE_WB_RAD-2"=3' - 7"; RO=4' - 11 7/16"; RO/2=2' - 5 23/32"; RO2/2=2' - 5 23/32"; TRANSITION_TOP=7' - 2 3/4"; TRIPLE_F+1"=21' - 11"; TRIP_F=21' - 10"; TRIP_G=21' - 8 3/8"; TYPE=1' - 0"; Type Comments=Vari-Plume Laboratory Exhaust Mixed-Flow High Pressure Inline Belt Drive With 1X3 Mixing Box; UNIT_HEIGHT=5' - 8 1/2"; UNIT_HEIGHT*.75=4' - 3 3/8"; UNIT_OD=4' - 8 15/16"; UNIT_RAD+((A/2)+.25")=5' - 2 7/32"; UNIT_RAD+((A/2)+.25")+4"=5' - 6 7/32"; UNIT_RADIUS=2' - 4 15/32"; UNIT_RADIUS*.6=2' - 1 5/8"; UNIT_RADIUS+4"=2' - 8 15/32"
- 445_QMXHPVP-30H-1X3_Mixing_Box: (A/2)+.25"=3' - 1 1/4"; (A/2)-2"=2' - 11"; (NOZZLE_HEIGHT-(NOZZLE_HEIGHT/8*2))/2=2' - 5 1/4"; (NOZZLE_WB_OD-NOZZLE_TOP_OD)/2=0' - 7 1/8"; -A=-6' - 2"; A=6' - 2"; A+.5=6' - 2 1/2"; A/2=3' - 1"; B=16' - 9"; B/2=8' - 4 1/2"; C=7' - 11"; C/2=3' - 11 1/2"; DUAL_F=14' - 3 3/4"; DUAL_F+1"=14' - 4 3/4"; DUAL_G=14' - 2"; E=6' - 0 5/8"; GA=0' - 0 3/32"; LONG_RO=21' - 9 1/8"; MB_A=8' - 6"; MB_HT=6' - 3 11/16"; MB_HT+.25"=6' - 3 15/16"; MB_HT-2.75"=6' - 0 15/16"; MB_HT/2=3' - 1 27/32"; Model=QMXHPVP-1X3_Mixing Box; NOZZLE_BOTTOM_ID=3' - 6 1/2"; NOZZLE_BOTTOM_RAD=1' - 9 1/4"; NOZZLE_HEIGHT=6' - 6"; NOZZLE_HEIGHT/7*2=1' - 7 1/2"; NOZZLE_SIZE=30' - 0"; NOZZLE_TOP_OD=3' - 9 1/2"; NOZZLE_TOP_RAD=1' - 10 3/4"; NOZZLE_WB/4=1' - 2 13/16"; NOZZLE_WB_OD=6' - 2"; NOZZLE_WB_RAD=3' - 1"; NOZZLE_WB_RAD-2"=2' - 11"; RO=5' - 6 7/16"; RO/2=2' - 9 7/32"; RO2/2=2' - 9 7/32"; TRANSITION_TOP=10' - 1 1/4"; TRIPLE_F+1"=22' - 6"; TRIP_F=22' - 5"; TRIP_G=22' - 3 3/8"; TYPE=1' - 0"; Type Comments=Vari-Plume Laboratory Exhaust Mixed-Flow High Pressure Inline Belt Drive With 1X3 Mixing Box; UNIT_HEIGHT=6' - 2"; UNIT_HEIGHT*.75=4' - 7 1/2"; UNIT_OD=5' - 3 1/16"; UNIT_RAD+((A/2)+.25")=5' - 8 25/32"; UNIT_RAD+((A/2)+.25")+4"=6' - 0 25/32"; UNIT_RADIUS=2' - 7 17/32"; UNIT_RADIUS*.6=2' - 4 3/8"; UNIT_RADIUS+4"=2' - 11 17/32"
- 445_QMXHPVP-30L-1X3_Mixing_Box: (A/2)+.25"=3' - 1 1/4"; (A/2)-2"=2' - 11"; (NOZZLE_HEIGHT-(NOZZLE_HEIGHT/8*2))/2=2' - 5 1/4"; (NOZZLE_WB_OD-NOZZLE_TOP_OD)/2=0' - 7 1/8"; -A=-6' - 2"; A=6' - 2"; A+.5=6' - 2 1/2"; A/2=3' - 1"; B=16' - 9"; B/2=8' - 4 1/2"; C=7' - 11"; C/2=3' - 11 1/2"; DUAL_F=14' - 3 3/4"; DUAL_F+1"=14' - 4 3/4"; DUAL_G=14' - 2"; E=6' - 0 5/8"; GA=0' - 0 3/32"; LONG_RO=21' - 9 1/8"; MB_A=8' - 6"; MB_HT=6' - 3 11/16"; MB_HT+.25"=6' - 3 15/16"; MB_HT-2.75"=6' - 0 15/16"; MB_HT/2=3' - 1 27/32"; Model=QMXHPVP-1X3_Mixing Box; NOZZLE_BOTTOM_ID=3' - 6 1/2"; NOZZLE_BOTTOM_RAD=1' - 9 1/4"; NOZZLE_HEIGHT=6' - 6"; NOZZLE_HEIGHT/7*2=1' - 7 1/2"; NOZZLE_SIZE=30' - 0"; NOZZLE_TOP_OD=3' - 9 1/2"; NOZZLE_TOP_RAD=1' - 10 3/4"; NOZZLE_WB/4=1' - 2 13/16"; NOZZLE_WB_OD=6' - 2"; NOZZLE_WB_RAD=3' - 1"; NOZZLE_WB_RAD-2"=2' - 11"; RO=5' - 6 7/16"; RO/2=2' - 9 7/32"; RO2/2=2' - 9 7/32"; TRANSITION_TOP=10' - 1 1/4"; TRIPLE_F+1"=22' - 6"; TRIP_F=22' - 5"; TRIP_G=22' - 3 3/8"; TYPE=1' - 0"; Type Comments=Vari-Plume Laboratory Exhaust Mixed-Flow High Pressure Inline Belt Drive With 1X3 Mixing Box; UNIT_HEIGHT=6' - 2"; UNIT_HEIGHT*.75=4' - 7 1/2"; UNIT_OD=5' - 3 1/16"; UNIT_RAD+((A/2)+.25")=5' - 8 25/32"; UNIT_RAD+((A/2)+.25")+4"=6' - 0 25/32"; UNIT_RADIUS=2' - 7 17/32"; UNIT_RADIUS*.6=2' - 4 3/8"; UNIT_RADIUS+4"=2' - 11 17/32"
- 445_QMXHPVP-36H-1X3_Mixing_Box: (A/2)+.25"=3' - 1 1/4"; (A/2)-2"=2' - 11"; (NOZZLE_HEIGHT-(NOZZLE_HEIGHT/8*2))/2=2' - 11 5/8"; (NOZZLE_WB_OD-NOZZLE_TOP_OD)/2=0' - 8"; -A=-6' - 2"; A=6' - 2"; A+.5=6' - 2 1/2"; A/2=3' - 1"; B=16' - 9"; B/2=8' - 4 1/2"; C=7' - 11"; C/2=3' - 11 1/2"; DUAL_F=14' - 3 3/4"; DUAL_F+1"=14' - 4 3/4"; DUAL_G=14' - 2"; E=6' - 0 5/8"; GA=0' - 0 3/32"; LONG_RO=21' - 9 1/8"; MB_A=8' - 6"; MB_HT=6' - 3 11/16"; MB_HT+.25"=6' - 3 15/16"; MB_HT-2.75"=6' - 0 15/16"; MB_HT/2=3' - 1 27/32"; Model=QMXHPVP-1X3_Mixing Box; NOZZLE_BOTTOM_ID=4' - 3 3/4"; NOZZLE_BOTTOM_RAD=2' - 1 7/8"; NOZZLE_HEIGHT=7' - 11"; NOZZLE_HEIGHT/7*2=1' - 11 3/4"; NOZZLE_SIZE=36' - 0"; NOZZLE_TOP_OD=4' - 10"; NOZZLE_TOP_RAD=2' - 5"; NOZZLE_WB/4=1' - 6"; NOZZLE_WB_OD=7' - 6"; NOZZLE_WB_RAD=3' - 9"; NOZZLE_WB_RAD-2"=3' - 7"; RO=5' - 6 7/16"; RO/2=2' - 9 7/32"; RO2/2=2' - 9 7/32"; TRANSITION_TOP=8' - 7 1/4"; TRIPLE_F+1"=22' - 6"; TRIP_F=22' - 5"; TRIP_G=22' - 3 3/8"; TYPE=1' - 0"; Type Comments=Vari-Plume Laboratory Exhaust Mixed-Flow High Pressure Inline Belt Drive With 1X3 Mixing Box; UNIT_HEIGHT=6' - 2"; UNIT_HEIGHT*.75=4' - 7 1/2"; UNIT_OD=5' - 3 1/16"; UNIT_RAD+((A/2)+.25")=5' - 8 25/32"; UNIT_RAD+((A/2)+.25")+4"=6' - 0 25/32"; UNIT_RADIUS=2' - 7 17/32"; UNIT_RADIUS*.6=2' - 4 3/8"; UNIT_RADIUS+4"=2' - 11 17/32"
- 445_QMXHPVP-36L-1X3_Mixing_Box: (A/2)+.25"=3' - 1 1/4"; (A/2)-2"=2' - 11"; (NOZZLE_HEIGHT-(NOZZLE_HEIGHT/8*2))/2=2' - 11 5/8"; (NOZZLE_WB_OD-NOZZLE_TOP_OD)/2=0' - 8"; -A=-6' - 2"; A=6' - 2"; A+.5=6' - 2 1/2"; A/2=3' - 1"; B=16' - 9"; B/2=8' - 4 1/2"; C=7' - 11"; C/2=3' - 11 1/2"; DUAL_F=14' - 3 3/4"; DUAL_F+1"=14' - 4 3/4"; DUAL_G=14' - 2"; E=6' - 0 5/8"; GA=0' - 0 3/32"; LONG_RO=21' - 9 1/8"; MB_A=8' - 6"; MB_HT=6' - 3 11/16"; MB_HT+.25"=6' - 3 15/16"; MB_HT-2.75"=6' - 0 15/16"; MB_HT/2=3' - 1 27/32"; Model=QMXHPVP-1X3_Mixing Box; NOZZLE_BOTTOM_ID=4' - 3 3/4"; NOZZLE_BOTTOM_RAD=2' - 1 7/8"; NOZZLE_HEIGHT=7' - 11"; NOZZLE_HEIGHT/7*2=1' - 11 3/4"; NOZZLE_SIZE=36' - 0"; NOZZLE_TOP_OD=4' - 10"; NOZZLE_TOP_RAD=2' - 5"; NOZZLE_WB/4=1' - 6"; NOZZLE_WB_OD=7' - 6"; NOZZLE_WB_RAD=3' - 9"; NOZZLE_WB_RAD-2"=3' - 7"; RO=5' - 6 7/16"; RO/2=2' - 9 7/32"; RO2/2=2' - 9 7/32"; TRANSITION_TOP=8' - 7 1/4"; TRIPLE_F+1"=22' - 6"; TRIP_F=22' - 5"; TRIP_G=22' - 3 3/8"; TYPE=1' - 0"; Type Comments=Vari-Plume Laboratory Exhaust Mixed-Flow High Pressure Inline Belt Drive With 1X3 Mixing Box; UNIT_HEIGHT=6' - 2"; UNIT_HEIGHT*.75=4' - 7 1/2"; UNIT_OD=5' - 3 1/16"; UNIT_RAD+((A/2)+.25")=5' - 8 25/32"; UNIT_RAD+((A/2)+.25")+4"=6' - 0 25/32"; UNIT_RADIUS=2' - 7 17/32"; UNIT_RADIUS*.6=2' - 4 3/8"; UNIT_RADIUS+4"=2' - 11 17/32"
- 490_QMXHPVP-30H-1X3_Mixing_Box: (A/2)+.25"=3' - 4 1/4"; (A/2)-2"=3' - 2"; (NOZZLE_HEIGHT-(NOZZLE_HEIGHT/8*2))/2=2' - 5 1/4"; (NOZZLE_WB_OD-NOZZLE_TOP_OD)/2=0' - 7 1/8"; -A=-6' - 8"; A=6' - 8"; A+.5=6' - 8 1/2"; A/2=3' - 4"; B=18' - 3"; B/2=9' - 1 1/2"; C=8' - 7"; C/2=4' - 3 1/2"; DUAL_F=16' - 0 3/4"; DUAL_F+1"=16' - 1 3/4"; DUAL_G=15' - 11"; E=6' - 6 1/2"; GA=0' - 0 1/8"; LONG_RO=24' - 9 1/4"; MB_A=9' - 5"; MB_HT=7' - 2 15/16"; MB_HT+.25"=7' - 3 3/16"; MB_HT-2.75"=7' - 0 3/16"; MB_HT/2=3' - 7 15/32"; Model=QMXHPVP-1X3_Mixing Box; NOZZLE_BOTTOM_ID=3' - 6 1/2"; NOZZLE_BOTTOM_RAD=1' - 9 1/4"; NOZZLE_HEIGHT=6' - 6"; NOZZLE_HEIGHT/7*2=1' - 7 1/2"; NOZZLE_SIZE=30' - 0"; NOZZLE_TOP_OD=3' - 9 1/2"; NOZZLE_TOP_RAD=1' - 10 3/4"; NOZZLE_WB/4=1' - 2 13/16"; NOZZLE_WB_OD=6' - 2"; NOZZLE_WB_RAD=3' - 1"; NOZZLE_WB_RAD-2"=2' - 11"; RO=6' - 0 1/4"; RO/2=3' - 0 1/8"; RO2/2=3' - 0 1/8"; TRANSITION_TOP=11' - 7 3/4"; TRIPLE_F+1"=25' - 6"; TRIP_F=25' - 5"; TRIP_G=25' - 3 1/2"; TYPE=1' - 0"; Type Comments=Vari-Plume Laboratory Exhaust Mixed-Flow High Pressure Inline Belt Drive With 1X3 Mixing Box; UNIT_HEIGHT=6' - 8 1/2"; UNIT_HEIGHT*.75=5' - 0 3/8"; UNIT_OD=5' - 9 3/8"; UNIT_RAD+((A/2)+.25")=6' - 2 15/16"; UNIT_RAD+((A/2)+.25")+4"=6' - 6 15/16"; UNIT_RADIUS=2' - 10 11/16"; UNIT_RADIUS*.6=2' - 7 7/32"; UNIT_RADIUS+4"=3' - 2 11/16"
- 490_QMXHPVP-30L-1X3_Mixing_Box: (A/2)+.25"=3' - 4 1/4"; (A/2)-2"=3' - 2"; (NOZZLE_HEIGHT-(NOZZLE_HEIGHT/8*2))/2=2' - 5 1/4"; (NOZZLE_WB_OD-NOZZLE_TOP_OD)/2=0' - 7 1/8"; -A=-6' - 8"; A=6' - 8"; A+.5=6' - 8 1/2"; A/2=3' - 4"; B=18' - 3"; B/2=9' - 1 1/2"; C=8' - 7"; C/2=4' - 3 1/2"; DUAL_F=16' - 0 3/4"; DUAL_F+1"=16' - 1 3/4"; DUAL_G=15' - 11"; E=6' - 6 1/2"; GA=0' - 0 1/8"; LONG_RO=24' - 9 1/4"; MB_A=9' - 5"; MB_HT=7' - 2 15/16"; MB_HT+.25"=7' - 3 3/16"; MB_HT-2.75"=7' - 0 3/16"; MB_HT/2=3' - 7 15/32"; Model=QMXHPVP-1X3_Mixing Box; NOZZLE_BOTTOM_ID=3' - 6 1/2"; NOZZLE_BOTTOM_RAD=1' - 9 1/4"; NOZZLE_HEIGHT=6' - 6"; NOZZLE_HEIGHT/7*2=1' - 7 1/2"; NOZZLE_SIZE=30' - 0"; NOZZLE_TOP_OD=3' - 9 1/2"; NOZZLE_TOP_RAD=1' - 10 3/4"; NOZZLE_WB/4=1' - 2 13/16"; NOZZLE_WB_OD=6' - 2"; NOZZLE_WB_RAD=3' - 1"; NOZZLE_WB_RAD-2"=2' - 11"; RO=6' - 0 1/4"; RO/2=3' - 0 1/8"; RO2/2=3' - 0 1/8"; TRANSITION_TOP=11' - 7 3/4"; TRIPLE_F+1"=25' - 6"; TRIP_F=25' - 5"; TRIP_G=25' - 3 1/2"; TYPE=1' - 0"; Type Comments=Vari-Plume Laboratory Exhaust Mixed-Flow High Pressure Inline Belt Drive With 1X3 Mixing Box; UNIT_HEIGHT=6' - 8 1/2"; UNIT_HEIGHT*.75=5' - 0 3/8"; UNIT_OD=5' - 9 3/8"; UNIT_RAD+((A/2)+.25")=6' - 2 15/16"; UNIT_RAD+((A/2)+.25")+4"=6' - 6 15/16"; UNIT_RADIUS=2' - 10 11/16"; UNIT_RADIUS*.6=2' - 7 7/32"; UNIT_RADIUS+4"=3' - 2 11/16"
- 490_QMXHPVP-36H-1X3_Mixing_Box: (A/2)+.25"=3' - 4 1/4"; (A/2)-2"=3' - 2"; (NOZZLE_HEIGHT-(NOZZLE_HEIGHT/8*2))/2=2' - 11 5/8"; (NOZZLE_WB_OD-NOZZLE_TOP_OD)/2=0' - 8"; -A=-6' - 8"; A=6' - 8"; A+.5=6' - 8 1/2"; A/2=3' - 4"; B=18' - 3"; B/2=9' - 1 1/2"; C=8' - 7"; C/2=4' - 3 1/2"; DUAL_F=16' - 0 3/4"; DUAL_F+1"=16' - 1 3/4"; DUAL_G=15' - 11"; E=6' - 6 1/2"; GA=0' - 0 1/8"; LONG_RO=24' - 9 1/4"; MB_A=9' - 5"; MB_HT=7' - 2 15/16"; MB_HT+.25"=7' - 3 3/16"; MB_HT-2.75"=7' - 0 3/16"; MB_HT/2=3' - 7 15/32"; Model=QMXHPVP-1X3_Mixing Box; NOZZLE_BOTTOM_ID=4' - 3 3/4"; NOZZLE_BOTTOM_RAD=2' - 1 7/8"; NOZZLE_HEIGHT=7' - 11"; NOZZLE_HEIGHT/7*2=1' - 11 3/4"; NOZZLE_SIZE=36' - 0"; NOZZLE_TOP_OD=4' - 10"; NOZZLE_TOP_RAD=2' - 5"; NOZZLE_WB/4=1' - 6"; NOZZLE_WB_OD=7' - 6"; NOZZLE_WB_RAD=3' - 9"; NOZZLE_WB_RAD-2"=3' - 7"; RO=6' - 0 1/4"; RO/2=3' - 0 1/8"; RO2/2=3' - 0 1/8"; TRANSITION_TOP=10' - 2 3/4"; TRIPLE_F+1"=25' - 6"; TRIP_F=25' - 5"; TRIP_G=25' - 3 1/2"; TYPE=1' - 0"; Type Comments=Vari-Plume Laboratory Exhaust Mixed-Flow High Pressure Inline Belt Drive With 1X3 Mixing Box; UNIT_HEIGHT=6' - 8 1/2"; UNIT_HEIGHT*.75=5' - 0 3/8"; UNIT_OD=5' - 9 3/8"; UNIT_RAD+((A/2)+.25")=6' - 2 15/16"; UNIT_RAD+((A/2)+.25")+4"=6' - 6 15/16"; UNIT_RADIUS=2' - 10 11/16"; UNIT_RADIUS*.6=2' - 7 7/32"; UNIT_RADIUS+4"=3' - 2 11/16"
- 490_QMXHPVP-36L-1X3_Mixing_Box: (A/2)+.25"=3' - 4 1/4"; (A/2)-2"=3' - 2"; (NOZZLE_HEIGHT-(NOZZLE_HEIGHT/8*2))/2=2' - 11 5/8"; (NOZZLE_WB_OD-NOZZLE_TOP_OD)/2=0' - 8"; -A=-6' - 8"; A=6' - 8"; A+.5=6' - 8 1/2"; A/2=3' - 4"; B=18' - 3"; B/2=9' - 1 1/2"; C=8' - 7"; C/2=4' - 3 1/2"; DUAL_F=16' - 0 3/4"; DUAL_F+1"=16' - 1 3/4"; DUAL_G=15' - 11"; E=6' - 6 1/2"; GA=0' - 0 1/8"; LONG_RO=24' - 9 1/4"; MB_A=9' - 5"; MB_HT=7' - 2 15/16"; MB_HT+.25"=7' - 3 3/16"; MB_HT-2.75"=7' - 0 3/16"; MB_HT/2=3' - 7 15/32"; Model=QMXHPVP-1X3_Mixing Box; NOZZLE_BOTTOM_ID=4' - 3 3/4"; NOZZLE_BOTTOM_RAD=2' - 1 7/8"; NOZZLE_HEIGHT=7' - 11"; NOZZLE_HEIGHT/7*2=1' - 11 3/4"; NOZZLE_SIZE=36' - 0"; NOZZLE_TOP_OD=4' - 10"; NOZZLE_TOP_RAD=2' - 5"; NOZZLE_WB/4=1' - 6"; NOZZLE_WB_OD=7' - 6"; NOZZLE_WB_RAD=3' - 9"; NOZZLE_WB_RAD-2"=3' - 7"; RO=6' - 0 1/4"; RO/2=3' - 0 1/8"; RO2/2=3' - 0 1/8"; TRANSITION_TOP=10' - 2 3/4"; TRIPLE_F+1"=25' - 6"; TRIP_F=25' - 5"; TRIP_G=25' - 3 1/2"; TYPE=1' - 0"; Type Comments=Vari-Plume Laboratory Exhaust Mixed-Flow High Pressure Inline Belt Drive With 1X3 Mixing Box; UNIT_HEIGHT=6' - 8 1/2"; UNIT_HEIGHT*.75=5' - 0 3/8"; UNIT_OD=5' - 9 3/8"; UNIT_RAD+((A/2)+.25")=6' - 2 15/16"; UNIT_RAD+((A/2)+.25")+4"=6' - 6 15/16"; UNIT_RADIUS=2' - 10 11/16"; UNIT_RADIUS*.6=2' - 7 7/32"; UNIT_RADIUS+4"=3' - 2 11/16"
- 540_QMXHPVP-36H-1X3_Mixing_Box: (A/2)+.25"=3' - 9 1/4"; (A/2)-2"=3' - 7"; (NOZZLE_HEIGHT-(NOZZLE_HEIGHT/8*2))/2=2' - 11 5/8"; (NOZZLE_WB_OD-NOZZLE_TOP_OD)/2=0' - 8"; -A=-7' - 6"; A=7' - 6"; A+.5=7' - 6 1/2"; A/2=3' - 9"; B=19' - 11"; B/2=9' - 11 1/2"; C=9' - 3"; C/2=4' - 7 1/2"; DUAL_F=17' - 0 1/4"; DUAL_F+1"=17' - 1 1/4"; DUAL_G=16' - 8 7/8"; E=7' - 1 3/8"; GA=0' - 0 1/8"; LONG_RO=25' - 10 1/8"; MB_A=10' - 6"; MB_HT=8' - 3 11/16"; MB_HT+.25"=8' - 3 15/16"; MB_HT-2.75"=8' - 0 15/16"; MB_HT/2=4' - 1 27/32"; Model=QMXHPVP-1X3_Mixing Box; NOZZLE_BOTTOM_ID=4' - 3 3/4"; NOZZLE_BOTTOM_RAD=2' - 1 7/8"; NOZZLE_HEIGHT=7' - 11"; NOZZLE_HEIGHT/7*2=1' - 11 3/4"; NOZZLE_SIZE=36' - 0"; NOZZLE_TOP_OD=4' - 10"; NOZZLE_TOP_RAD=2' - 5"; NOZZLE_WB/4=1' - 6"; NOZZLE_WB_OD=7' - 6"; NOZZLE_WB_RAD=3' - 9"; NOZZLE_WB_RAD-2"=3' - 7"; RO=6' - 7 1/8"; RO/2=3' - 3 9/16"; RO2/2=3' - 4 9/16"; TRANSITION_TOP=11' - 10 1/4"; TRIPLE_F+1"=26' - 7"; TRIP_F=26' - 6"; TRIP_G=26' - 4 3/8"; TYPE=1' - 0"; Type Comments=Vari-Plume Laboratory Exhaust Mixed-Flow High Pressure Inline Belt Drive With 1X3 Mixing Box; UNIT_HEIGHT=7' - 3"; UNIT_HEIGHT*.75=5' - 5 1/4"; UNIT_OD=6' - 4 7/16"; UNIT_RAD+((A/2)+.25")=6' - 11 15/32"; UNIT_RAD+((A/2)+.25")+4"=7' - 3 15/32"; UNIT_RADIUS=3' - 2 7/32"; UNIT_RADIUS*.6=2' - 10 13/32"; UNIT_RADIUS+4"=3' - 6 7/32"
- 540_QMXHPVP-36L-1X3_Mixing_Box: (A/2)+.25"=3' - 9 1/4"; (A/2)-2"=3' - 7"; (NOZZLE_HEIGHT-(NOZZLE_HEIGHT/8*2))/2=2' - 11 5/8"; (NOZZLE_WB_OD-NOZZLE_TOP_OD)/2=0' - 8"; -A=-7' - 6"; A=7' - 6"; A+.5=7' - 6 1/2"; A/2=3' - 9"; B=19' - 11"; B/2=9' - 11 1/2"; C=9' - 3"; C/2=4' - 7 1/2"; DUAL_F=17' - 0 1/4"; DUAL_F+1"=17' - 1 1/4"; DUAL_G=16' - 8 7/8"; E=7' - 1 3/8"; GA=0' - 0 1/8"; LONG_RO=25' - 10 1/8"; MB_A=10' - 6"; MB_HT=8' - 3 11/16"; MB_HT+.25"=8' - 3 15/16"; MB_HT-2.75"=8' - 0 15/16"; MB_HT/2=4' - 1 27/32"; Model=QMXHPVP-1X3_Mixing Box; NOZZLE_BOTTOM_ID=4' - 3 3/4"; NOZZLE_BOTTOM_RAD=2' - 1 7/8"; NOZZLE_HEIGHT=7' - 11"; NOZZLE_HEIGHT/7*2=1' - 11 3/4"; NOZZLE_SIZE=36' - 0"; NOZZLE_TOP_OD=4' - 10"; NOZZLE_TOP_RAD=2' - 5"; NOZZLE_WB/4=1' - 6"; NOZZLE_WB_OD=7' - 6"; NOZZLE_WB_RAD=3' - 9"; NOZZLE_WB_RAD-2"=3' - 7"; RO=6' - 7 1/8"; RO/2=3' - 3 9/16"; RO2/2=3' - 4 9/16"; TRANSITION_TOP=11' - 10 1/4"; TRIPLE_F+1"=26' - 7"; TRIP_F=26' - 6"; TRIP_G=26' - 4 3/8"; TYPE=1' - 0"; Type Comments=Vari-Plume Laboratory Exhaust Mixed-Flow High Pressure Inline Belt Drive With 1X3 Mixing Box; UNIT_HEIGHT=7' - 3"; UNIT_HEIGHT*.75=5' - 5 1/4"; UNIT_OD=6' - 4 7/16"; UNIT_RAD+((A/2)+.25")=6' - 11 15/32"; UNIT_RAD+((A/2)+.25")+4"=7' - 3 15/32"; UNIT_RADIUS=3' - 2 7/32"; UNIT_RADIUS*.6=2' - 10 13/32"; UNIT_RADIUS+4"=3' - 6 7/32"
- 540_QMXHPVP-49H-1X3_Mixing_Box: (A/2)+.25"=3' - 9 1/4"; (A/2)-2"=3' - 7"; (NOZZLE_HEIGHT-(NOZZLE_HEIGHT/8*2))/2=3' - 5 1/4"; (NOZZLE_WB_OD-NOZZLE_TOP_OD)/2=0' - 6 1/4"; -A=-7' - 6"; A=7' - 6"; A+.5=7' - 6 1/2"; A/2=3' - 9"; B=19' - 11"; B/2=9' - 11 1/2"; C=9' - 3"; C/2=4' - 7 1/2"; DUAL_F=17' - 0 1/4"; DUAL_F+1"=17' - 1 1/4"; DUAL_G=16' - 8 7/8"; E=7' - 1 3/8"; GA=0' - 0 1/8"; LONG_RO=25' - 10 1/8"; MB_A=10' - 6"; MB_HT=8' - 3 11/16"; MB_HT+.25"=8' - 3 15/16"; MB_HT-2.75"=8' - 0 15/16"; MB_HT/2=4' - 1 27/32"; Model=QMXHPVP-1X3_Mixing Box; NOZZLE_BOTTOM_ID=5' - 9 3/8"; NOZZLE_BOTTOM_RAD=2' - 10 11/16"; NOZZLE_HEIGHT=9' - 2"; NOZZLE_HEIGHT/7*2=2' - 3 1/2"; NOZZLE_SIZE=49' - 0"; NOZZLE_TOP_OD=6' - 4"; NOZZLE_TOP_RAD=3' - 2"; NOZZLE_WB/4=1' - 8 3/16"; NOZZLE_WB_OD=8' - 5"; NOZZLE_WB_RAD=4' - 2 1/2"; NOZZLE_WB_RAD-2"=4' - 0 1/2"; RO=6' - 7 1/8"; RO/2=3' - 3 9/16"; RO2/2=3' - 4 9/16"; TRANSITION_TOP=10' - 1 1/4"; TRIPLE_F+1"=26' - 7"; TRIP_F=26' - 6"; TRIP_G=26' - 4 3/8"; TYPE=1' - 0"; Type Comments=Vari-Plume Laboratory Exhaust Mixed-Flow High Pressure Inline Belt Drive With 1X3 Mixing Box; UNIT_HEIGHT=7' - 3"; UNIT_HEIGHT*.75=5' - 5 1/4"; UNIT_OD=6' - 4 7/16"; UNIT_RAD+((A/2)+.25")=6' - 11 15/32"; UNIT_RAD+((A/2)+.25")+4"=7' - 3 15/32"; UNIT_RADIUS=3' - 2 7/32"; UNIT_RADIUS*.6=2' - 10 13/32"; UNIT_RADIUS+4"=3' - 6 7/32"
- 540_QMXHPVP-49L-1X3_Mixing_Box: (A/2)+.25"=3' - 9 1/4"; (A/2)-2"=3' - 7"; (NOZZLE_HEIGHT-(NOZZLE_HEIGHT/8*2))/2=3' - 5 1/4"; (NOZZLE_WB_OD-NOZZLE_TOP_OD)/2=0' - 6 1/4"; -A=-7' - 6"; A=7' - 6"; A+.5=7' - 6 1/2"; A/2=3' - 9"; B=19' - 11"; B/2=9' - 11 1/2"; C=9' - 3"; C/2=4' - 7 1/2"; DUAL_F=17' - 0 1/4"; DUAL_F+1"=17' - 1 1/4"; DUAL_G=16' - 8 7/8"; E=7' - 1 3/8"; GA=0' - 0 1/8"; LONG_RO=25' - 10 1/8"; MB_A=10' - 6"; MB_HT=8' - 3 11/16"; MB_HT+.25"=8' - 3 15/16"; MB_HT-2.75"=8' - 0 15/16"; MB_HT/2=4' - 1 27/32"; Model=QMXHPVP-1X3_Mixing Box; NOZZLE_BOTTOM_ID=5' - 9 3/8"; NOZZLE_BOTTOM_RAD=2' - 10 11/16"; NOZZLE_HEIGHT=9' - 2"; NOZZLE_HEIGHT/7*2=2' - 3 1/2"; NOZZLE_SIZE=49' - 0"; NOZZLE_TOP_OD=6' - 4"; NOZZLE_TOP_RAD=3' - 2"; NOZZLE_WB/4=1' - 8 3/16"; NOZZLE_WB_OD=8' - 5"; NOZZLE_WB_RAD=4' - 2 1/2"; NOZZLE_WB_RAD-2"=4' - 0 1/2"; RO=6' - 7 1/8"; RO/2=3' - 3 9/16"; RO2/2=3' - 4 9/16"; TRANSITION_TOP=10' - 1 1/4"; TRIPLE_F+1"=26' - 7"; TRIP_F=26' - 6"; TRIP_G=26' - 4 3/8"; TYPE=1' - 0"; Type Comments=Vari-Plume Laboratory Exhaust Mixed-Flow High Pressure Inline Belt Drive With 1X3 Mixing Box; UNIT_HEIGHT=7' - 3"; UNIT_HEIGHT*.75=5' - 5 1/4"; UNIT_OD=6' - 4 7/16"; UNIT_RAD+((A/2)+.25")=6' - 11 15/32"; UNIT_RAD+((A/2)+.25")+4"=7' - 3 15/32"; UNIT_RADIUS=3' - 2 7/32"; UNIT_RADIUS*.6=2' - 10 13/32"; UNIT_RADIUS+4"=3' - 6 7/32"
- 600_QMXHPVP-36H-1X3_Mixing_Box: (A/2)+.25"=4' - 2 3/4"; (A/2)-2"=4' - 0 1/2"; (NOZZLE_HEIGHT-(NOZZLE_HEIGHT/8*2))/2=2' - 11 5/8"; (NOZZLE_WB_OD-NOZZLE_TOP_OD)/2=0' - 8"; -A=-8' - 5"; A=8' - 5"; A+.5=8' - 5 1/2"; A/2=4' - 2 1/2"; B=21' - 11"; B/2=10' - 11 1/2"; C=10' - 2"; C/2=5' - 1"; DUAL_F=18' - 0 1/4"; DUAL_F+1"=18' - 1 1/4"; DUAL_G=17' - 7 7/8"; E=7' - 10 3/8"; GA=0' - 0 3/16"; LONG_RO=26' - 11 1/8"; MB_A=12' - 0"; MB_HT=9' - 9 3/16"; MB_HT+.25"=9' - 9 7/16"; MB_HT-2.75"=9' - 6 7/16"; MB_HT/2=4' - 10 19/32"; Model=QMXHPVP-1X3_Mixing Box; NOZZLE_BOTTOM_ID=4' - 3 3/4"; NOZZLE_BOTTOM_RAD=2' - 1 7/8"; NOZZLE_HEIGHT=7' - 11"; NOZZLE_HEIGHT/7*2=1' - 11 3/4"; NOZZLE_SIZE=36' - 0"; NOZZLE_TOP_OD=4' - 10"; NOZZLE_TOP_RAD=2' - 5"; NOZZLE_WB/4=1' - 6"; NOZZLE_WB_OD=7' - 6"; NOZZLE_WB_RAD=3' - 9"; NOZZLE_WB_RAD-2"=3' - 7"; RO=7' - 4 1/16"; RO/2=3' - 8 1/32"; RO2/2=3' - 10 1/2"; TRANSITION_TOP=14' - 2 3/4"; TRIPLE_F+1"=27' - 8"; TRIP_F=27' - 7"; TRIP_G=27' - 5 3/8"; TYPE=1' - 0"; Type Comments=Vari-Plume Laboratory Exhaust Mixed-Flow High Pressure Inline Belt Drive With 1X3 Mixing Box; UNIT_HEIGHT=7' - 11 1/2"; UNIT_HEIGHT*.75=5' - 11 5/8"; UNIT_OD=7' - 0 7/8"; UNIT_RAD+((A/2)+.25")=7' - 9 3/16"; UNIT_RAD+((A/2)+.25")+4"=8' - 1 3/16"; UNIT_RADIUS=3' - 6 7/16"; UNIT_RADIUS*.6=3' - 2 3/16"; UNIT_RADIUS+4"=3' - 10 7/16"
- 600_QMXHPVP-36L-1X3_Mixing_Box: (A/2)+.25"=4' - 2 3/4"; (A/2)-2"=4' - 0 1/2"; (NOZZLE_HEIGHT-(NOZZLE_HEIGHT/8*2))/2=2' - 11 5/8"; (NOZZLE_WB_OD-NOZZLE_TOP_OD)/2=0' - 8"; -A=-8' - 5"; A=8' - 5"; A+.5=8' - 5 1/2"; A/2=4' - 2 1/2"; B=21' - 11"; B/2=10' - 11 1/2"; C=10' - 2"; C/2=5' - 1"; DUAL_F=18' - 0 1/4"; DUAL_F+1"=18' - 1 1/4"; DUAL_G=17' - 7 7/8"; E=7' - 10 3/8"; GA=0' - 0 3/16"; LONG_RO=26' - 11 1/8"; MB_A=12' - 0"; MB_HT=9' - 9 3/16"; MB_HT+.25"=9' - 9 7/16"; MB_HT-2.75"=9' - 6 7/16"; MB_HT/2=4' - 10 19/32"; Model=QMXHPVP-1X3_Mixing Box; NOZZLE_BOTTOM_ID=4' - 3 3/4"; NOZZLE_BOTTOM_RAD=2' - 1 7/8"; NOZZLE_HEIGHT=7' - 11"; NOZZLE_HEIGHT/7*2=1' - 11 3/4"; NOZZLE_SIZE=36' - 0"; NOZZLE_TOP_OD=4' - 10"; NOZZLE_TOP_RAD=2' - 5"; NOZZLE_WB/4=1' - 6"; NOZZLE_WB_OD=7' - 6"; NOZZLE_WB_RAD=3' - 9"; NOZZLE_WB_RAD-2"=3' - 7"; RO=7' - 4 1/16"; RO/2=3' - 8 1/32"; RO2/2=3' - 10 1/2"; TRANSITION_TOP=14' - 2 3/4"; TRIPLE_F+1"=27' - 8"; TRIP_F=27' - 7"; TRIP_G=27' - 5 3/8"; TYPE=1' - 0"; Type Comments=Vari-Plume Laboratory Exhaust Mixed-Flow High Pressure Inline Belt Drive With 1X3 Mixing Box; UNIT_HEIGHT=7' - 11 1/2"; UNIT_HEIGHT*.75=5' - 11 5/8"; UNIT_OD=7' - 0 7/8"; UNIT_RAD+((A/2)+.25")=7' - 9 3/16"; UNIT_RAD+((A/2)+.25")+4"=8' - 1 3/16"; UNIT_RADIUS=3' - 6 7/16"; UNIT_RADIUS*.6=3' - 2 3/16"; UNIT_RADIUS+4"=3' - 10 7/16"
- 600_QMXHPVP-49H-1X3_Mixing_Box: (A/2)+.25"=4' - 2 3/4"; (A/2)-2"=4' - 0 1/2"; (NOZZLE_HEIGHT-(NOZZLE_HEIGHT/8*2))/2=3' - 5 1/4"; (NOZZLE_WB_OD-NOZZLE_TOP_OD)/2=0' - 6 1/4"; -A=-8' - 5"; A=8' - 5"; A+.5=8' - 5 1/2"; A/2=4' - 2 1/2"; B=21' - 11"; B/2=10' - 11 1/2"; C=10' - 2"; C/2=5' - 1"; DUAL_F=18' - 0 1/4"; DUAL_F+1"=18' - 1 1/4"; DUAL_G=17' - 7 7/8"; E=7' - 10 3/8"; GA=0' - 0 3/16"; LONG_RO=26' - 11 1/8"; MB_A=12' - 0"; MB_HT=9' - 9 3/16"; MB_HT+.25"=9' - 9 7/16"; MB_HT-2.75"=9' - 6 7/16"; MB_HT/2=4' - 10 19/32"; Model=QMXHPVP-1X3_Mixing Box; NOZZLE_BOTTOM_ID=5' - 9 3/8"; NOZZLE_BOTTOM_RAD=2' - 10 11/16"; NOZZLE_HEIGHT=9' - 2"; NOZZLE_HEIGHT/7*2=2' - 3 1/2"; NOZZLE_SIZE=49' - 0"; NOZZLE_TOP_OD=6' - 4"; NOZZLE_TOP_RAD=3' - 2"; NOZZLE_WB/4=1' - 8 3/16"; NOZZLE_WB_OD=8' - 5"; NOZZLE_WB_RAD=4' - 2 1/2"; NOZZLE_WB_RAD-2"=4' - 0 1/2"; RO=7' - 4 1/16"; RO/2=3' - 8 1/32"; RO2/2=3' - 10 1/2"; TRANSITION_TOP=12' - 4 3/4"; TRIPLE_F+1"=27' - 8"; TRIP_F=27' - 7"; TRIP_G=27' - 5 3/8"; TYPE=1' - 0"; Type Comments=Vari-Plume Laboratory Exhaust Mixed-Flow High Pressure Inline Belt Drive With 1X3 Mixing Box; UNIT_HEIGHT=7' - 11 1/2"; UNIT_HEIGHT*.75=5' - 11 5/8"; UNIT_OD=7' - 0 7/8"; UNIT_RAD+((A/2)+.25")=7' - 9 3/16"; UNIT_RAD+((A/2)+.25")+4"=8' - 1 3/16"; UNIT_RADIUS=3' - 6 7/16"; UNIT_RADIUS*.6=3' - 2 3/16"; UNIT_RADIUS+4"=3' - 10 7/16"
- 600_QMXHPVP-49L-1X3_Mixing_Box: (A/2)+.25"=4' - 2 3/4"; (A/2)-2"=4' - 0 1/2"; (NOZZLE_HEIGHT-(NOZZLE_HEIGHT/8*2))/2=3' - 5 1/4"; (NOZZLE_WB_OD-NOZZLE_TOP_OD)/2=0' - 6 1/4"; -A=-8' - 5"; A=8' - 5"; A+.5=8' - 5 1/2"; A/2=4' - 2 1/2"; B=21' - 11"; B/2=10' - 11 1/2"; C=10' - 2"; C/2=5' - 1"; DUAL_F=18' - 0 1/4"; DUAL_F+1"=18' - 1 1/4"; DUAL_G=17' - 7 7/8"; E=7' - 10 3/8"; GA=0' - 0 3/16"; LONG_RO=26' - 11 1/8"; MB_A=12' - 0"; MB_HT=9' - 9 3/16"; MB_HT+.25"=9' - 9 7/16"; MB_HT-2.75"=9' - 6 7/16"; MB_HT/2=4' - 10 19/32"; Model=QMXHPVP-1X3_Mixing Box; NOZZLE_BOTTOM_ID=5' - 9 3/8"; NOZZLE_BOTTOM_RAD=2' - 10 11/16"; NOZZLE_HEIGHT=9' - 2"; NOZZLE_HEIGHT/7*2=2' - 3 1/2"; NOZZLE_SIZE=49' - 0"; NOZZLE_TOP_OD=6' - 4"; NOZZLE_TOP_RAD=3' - 2"; NOZZLE_WB/4=1' - 8 3/16"; NOZZLE_WB_OD=8' - 5"; NOZZLE_WB_RAD=4' - 2 1/2"; NOZZLE_WB_RAD-2"=4' - 0 1/2"; RO=7' - 4 1/16"; RO/2=3' - 8 1/32"; RO2/2=3' - 10 1/2"; TRANSITION_TOP=12' - 4 3/4"; TRIPLE_F+1"=27' - 8"; TRIP_F=27' - 7"; TRIP_G=27' - 5 3/8"; TYPE=1' - 0"; Type Comments=Vari-Plume Laboratory Exhaust Mixed-Flow High Pressure Inline Belt Drive With 1X3 Mixing Box; UNIT_HEIGHT=7' - 11 1/2"; UNIT_HEIGHT*.75=5' - 11 5/8"; UNIT_OD=7' - 0 7/8"; UNIT_RAD+((A/2)+.25")=7' - 9 3/16"; UNIT_RAD+((A/2)+.25")+4"=8' - 1 3/16"; UNIT_RADIUS=3' - 6 7/16"; UNIT_RADIUS*.6=3' - 2 3/16"; UNIT_RADIUS+4"=3' - 10 7/16"
- 90_QMXHPVP-9H-1X3_Mixing_Box: (A/2)+.25"=1' - 2 1/4"; (A/2)-2"=1' - 0"; (NOZZLE_HEIGHT-(NOZZLE_HEIGHT/8*2))/2=0' - 10 1/2"; (NOZZLE_WB_OD-NOZZLE_TOP_OD)/2=0' - 2 3/8"; -A=-2' - 4"; A=2' - 4"; A+.5=2' - 4 1/2"; A/2=1' - 2"; B=5' - 5"; B/2=2' - 8 1/2"; C=2' - 6"; C/2=1' - 3"; DUAL_F=5' - 4 1/4"; DUAL_F+1"=5' - 5 1/4"; DUAL_G=5' - 3 5/16"; E=2' - 3 3/16"; GA=0' - 0 3/32"; LONG_RO=7' - 9 1/4"; MB_A=2' - 10"; MB_HT=2' - 5 3/16"; MB_HT+.25"=2' - 5 7/16"; MB_HT-2.75"=2' - 2 7/16"; MB_HT/2=1' - 2 19/32"; Model=QMXHPVP-1X3_Mixing Box; NOZZLE_BOTTOM_ID=1' - 0 13/16"; NOZZLE_BOTTOM_RAD=0' - 6 13/32"; NOZZLE_HEIGHT=2' - 4"; NOZZLE_HEIGHT/7*2=0' - 7"; NOZZLE_SIZE=9' - 0"; NOZZLE_TOP_OD=1' - 1 1/2"; NOZZLE_TOP_RAD=0' - 6 3/4"; NOZZLE_WB/4=0' - 4 19/32"; NOZZLE_WB_OD=1' - 11"; NOZZLE_WB_RAD=0' - 11 1/2"; NOZZLE_WB_RAD-2"=0' - 9 1/2"; RO=1' - 9"; RO/2=0' - 10 1/2"; RO2/2=0' - 10 1/2"; TRANSITION_TOP=3' - 1 1/16"; TRIPLE_F+1"=8' - 5"; TRIP_F=8' - 4"; TRIP_G=8' - 3 1/2"; TYPE=1' - 0"; Type Comments=Vari-Plume Laboratory Exhaust Mixed-Flow High Pressure Inline Belt Drive With 1X3 Mixing Box; UNIT_HEIGHT=1' - 7 7/8"; UNIT_HEIGHT*.75=1' - 2 29/32"; UNIT_OD=1' - 0 13/16"; UNIT_RAD+((A/2)+.25")=1' - 8 21/32"; UNIT_RAD+((A/2)+.25")+4"=2' - 0 21/32"; UNIT_RADIUS=0' - 6 13/32"; UNIT_RADIUS*.6=0' - 5 25/32"; UNIT_RADIUS+4"=0' - 10 13/32"
- 90_QMXHPVP-9L-1X3_Mixing_Box: (A/2)+.25"=1' - 2 1/4"; (A/2)-2"=1' - 0"; (NOZZLE_HEIGHT-(NOZZLE_HEIGHT/8*2))/2=0' - 10 1/2"; (NOZZLE_WB_OD-NOZZLE_TOP_OD)/2=0' - 2 3/8"; -A=-2' - 4"; A=2' - 4"; A+.5=2' - 4 1/2"; A/2=1' - 2"; B=5' - 5"; B/2=2' - 8 1/2"; C=2' - 6"; C/2=1' - 3"; DUAL_F=5' - 4 1/4"; DUAL_F+1"=5' - 5 1/4"; DUAL_G=5' - 3 5/16"; E=2' - 3 3/16"; GA=0' - 0 3/32"; LONG_RO=7' - 9 1/4"; MB_A=2' - 10"; MB_HT=2' - 5 3/16"; MB_HT+.25"=2' - 5 7/16"; MB_HT-2.75"=2' - 2 7/16"; MB_HT/2=1' - 2 19/32"; Model=QMXHPVP-1X3_Mixing Box; NOZZLE_BOTTOM_ID=1' - 0 13/16"; NOZZLE_BOTTOM_RAD=0' - 6 13/32"; NOZZLE_HEIGHT=2' - 4"; NOZZLE_HEIGHT/7*2=0' - 7"; NOZZLE_SIZE=9' - 0"; NOZZLE_TOP_OD=1' - 1 1/2"; NOZZLE_TOP_RAD=0' - 6 3/4"; NOZZLE_WB/4=0' - 4 19/32"; NOZZLE_WB_OD=1' - 11"; NOZZLE_WB_RAD=0' - 11 1/2"; NOZZLE_WB_RAD-2"=0' - 9 1/2"; RO=1' - 9"; RO/2=0' - 10 1/2"; RO2/2=0' - 10 1/2"; TRANSITION_TOP=3' - 1 1/16"; TRIPLE_F+1"=8' - 5"; TRIP_F=8' - 4"; TRIP_G=8' - 3 1/2"; TYPE=1' - 0"; Type Comments=Vari-Plume Laboratory Exhaust Mixed-Flow High Pressure Inline Belt Drive With 1X3 Mixing Box; UNIT_HEIGHT=1' - 7 7/8"; UNIT_HEIGHT*.75=1' - 2 29/32"; UNIT_OD=1' - 0 13/16"; UNIT_RAD+((A/2)+.25")=1' - 8 21/32"; UNIT_RAD+((A/2)+.25")+4"=2' - 0 21/32"; UNIT_RADIUS=0' - 6 13/32"; UNIT_RADIUS*.6=0' - 5 25/32"; UNIT_RADIUS+4"=0' - 10 13/32"
- 490_QMXVP-49L-1X3_Mixing_Box: (A/2)+.25"=3' - 4 1/4"; (A/2)-2"=3' - 2"; (NOZZLE_HEIGHT-(NOZZLE_HEIGHT/8*2))/2=3' - 5 1/4"; (NOZZLE_WB_OD-NOZZLE_TOP_OD)/2=0' - 6 1/4"; -A=-6' - 8"; A=6' - 8"; A+.5=6' - 8 1/2"; A/2=3' - 4"; B=18' - 3"; B/2=9' - 1 1/2"; C=8' - 7"; C/2=4' - 3 1/2"; DUAL_F=16' - 0 3/4"; DUAL_F+1"=16' - 1 3/4"; DUAL_G=15' - 11"; E=6' - 6 1/2"; GA=0' - 0 1/8"; LONG_RO=24' - 9 1/4"; MB_A=9' - 5"; MB_HT=7' - 2 15/16"; MB_HT+.25"=7' - 3 3/16"; MB_HT-2.75"=7' - 0 3/16"; MB_HT/2=3' - 7 15/32"; Model=QMXVP-1X3_Mixing Box; NOZZLE_BOTTOM_ID=5' - 9 3/8"; NOZZLE_BOTTOM_RAD=2' - 10 11/16"; NOZZLE_HEIGHT=9' - 2"; NOZZLE_HEIGHT/7*2=2' - 3 1/2"; NOZZLE_SIZE=49' - 0"; NOZZLE_TOP_OD=6' - 4"; NOZZLE_TOP_RAD=3' - 2"; NOZZLE_WB/4=1' - 8 3/16"; NOZZLE_WB_OD=8' - 5"; NOZZLE_WB_RAD=4' - 2 1/2"; NOZZLE_WB_RAD-2"=4' - 0 1/2"; RO=6' - 0 1/4"; RO/2=3' - 0 1/8"; RO2/2=3' - 0 1/8"; TRANSITION_TOP=8' - 0 3/4"; TRIPLE_F+1"=25' - 6"; TRIP_F=25' - 5"; TRIP_G=25' - 3 1/2"; TYPE=0' - 0"; Type Comments=Vari-Plume Laboratory Exhaust Mixed-Flow Inline Belt Drive With 1X3 Mixing Box; UNIT_HEIGHT=6' - 8 1/2"; UNIT_HEIGHT*.75=5' - 0 3/8"; UNIT_OD=5' - 9 3/8"; UNIT_RAD+((A/2)+.25")=6' - 2 15/16"; UNIT_RAD+((A/2)+.25")+4"=6' - 6 15/16"; UNIT_RADIUS=2' - 10 11/16"; UNIT_RADIUS*.6=2' - 7 7/32"; UNIT_RADIUS+4"=3' - 2 11/16"
- 490_QMXHPVP-49H-1X3_Mixing_Box: (A/2)+.25"=3' - 4 1/4"; (A/2)-2"=3' - 2"; (NOZZLE_HEIGHT-(NOZZLE_HEIGHT/8*2))/2=3' - 5 1/4"; (NOZZLE_WB_OD-NOZZLE_TOP_OD)/2=0' - 6 1/4"; -A=-6' - 8"; A=6' - 8"; A+.5=6' - 8 1/2"; A/2=3' - 4"; B=18' - 3"; B/2=9' - 1 1/2"; C=8' - 7"; C/2=4' - 3 1/2"; DUAL_F=16' - 0 3/4"; DUAL_F+1"=16' - 1 3/4"; DUAL_G=15' - 11"; E=6' - 6 1/2"; GA=0' - 0 1/8"; LONG_RO=24' - 9 1/4"; MB_A=9' - 5"; MB_HT=7' - 2 15/16"; MB_HT+.25"=7' - 3 3/16"; MB_HT-2.75"=7' - 0 3/16"; MB_HT/2=3' - 7 15/32"; Model=QMXHPVP-1X3_Mixing Box; NOZZLE_BOTTOM_ID=5' - 9 3/8"; NOZZLE_BOTTOM_RAD=2' - 10 11/16"; NOZZLE_HEIGHT=9' - 2"; NOZZLE_HEIGHT/7*2=2' - 3 1/2"; NOZZLE_SIZE=49' - 0"; NOZZLE_TOP_OD=6' - 4"; NOZZLE_TOP_RAD=3' - 2"; NOZZLE_WB/4=1' - 8 3/16"; NOZZLE_WB_OD=8' - 5"; NOZZLE_WB_RAD=4' - 2 1/2"; NOZZLE_WB_RAD-2"=4' - 0 1/2"; RO=6' - 0 1/4"; RO/2=3' - 0 1/8"; RO2/2=3' - 0 1/8"; TRANSITION_TOP=8' - 0 3/4"; TRIPLE_F+1"=25' - 6"; TRIP_F=25' - 5"; TRIP_G=25' - 3 1/2"; TYPE=1' - 0"; Type Comments=Vari-Plume Laboratory Exhaust Mixed-Flow High Pressure Inline Belt Drive With 1X3 Mixing Box; UNIT_HEIGHT=6' - 8 1/2"; UNIT_HEIGHT*.75=5' - 0 3/8"; UNIT_OD=5' - 9 3/8"; UNIT_RAD+((A/2)+.25")=6' - 2 15/16"; UNIT_RAD+((A/2)+.25")+4"=6' - 6 15/16"; UNIT_RADIUS=2' - 10 11/16"; UNIT_RADIUS*.6=2' - 7 7/32"; UNIT_RADIUS+4"=3' - 2 11/16"
- 490_QMXHPVP-49L-1X3_Mixing_Box: (A/2)+.25"=3' - 4 1/4"; (A/2)-2"=3' - 2"; (NOZZLE_HEIGHT-(NOZZLE_HEIGHT/8*2))/2=3' - 5 1/4"; (NOZZLE_WB_OD-NOZZLE_TOP_OD)/2=0' - 6 1/4"; -A=-6' - 8"; A=6' - 8"; A+.5=6' - 8 1/2"; A/2=3' - 4"; B=18' - 3"; B/2=9' - 1 1/2"; C=8' - 7"; C/2=4' - 3 1/2"; DUAL_F=16' - 0 3/4"; DUAL_F+1"=16' - 1 3/4"; DUAL_G=15' - 11"; E=6' - 6 1/2"; GA=0' - 0 1/8"; LONG_RO=24' - 9 1/4"; MB_A=9' - 5"; MB_HT=7' - 2 15/16"; MB_HT+.25"=7' - 3 3/16"; MB_HT-2.75"=7' - 0 3/16"; MB_HT/2=3' - 7 15/32"; Model=QMXHPVP-1X3_Mixing Box; NOZZLE_BOTTOM_ID=5' - 9 3/8"; NOZZLE_BOTTOM_RAD=2' - 10 11/16"; NOZZLE_HEIGHT=9' - 2"; NOZZLE_HEIGHT/7*2=2' - 3 1/2"; NOZZLE_SIZE=49' - 0"; NOZZLE_TOP_OD=6' - 4"; NOZZLE_TOP_RAD=3' - 2"; NOZZLE_WB/4=1' - 8 3/16"; NOZZLE_WB_OD=8' - 5"; NOZZLE_WB_RAD=4' - 2 1/2"; NOZZLE_WB_RAD-2"=4' - 0 1/2"; RO=6' - 0 1/4"; RO/2=3' - 0 1/8"; RO2/2=3' - 0 1/8"; TRANSITION_TOP=8' - 0 3/4"; TRIPLE_F+1"=25' - 6"; TRIP_F=25' - 5"; TRIP_G=25' - 3 1/2"; TYPE=1' - 0"; Type Comments=Vari-Plume Laboratory Exhaust Mixed-Flow High Pressure Inline Belt Drive With 1X3 Mixing Box; UNIT_HEIGHT=6' - 8 1/2"; UNIT_HEIGHT*.75=5' - 0 3/8"; UNIT_OD=5' - 9 3/8"; UNIT_RAD+((A/2)+.25")=6' - 2 15/16"; UNIT_RAD+((A/2)+.25")+4"=6' - 6 15/16"; UNIT_RADIUS=2' - 10 11/16"; UNIT_RADIUS*.6=2' - 7 7/32"; UNIT_RADIUS+4"=3' - 2 11/16"
- 202_QMXHPVP-21H-1X3_Mixing_Box: (A/2)+.25"=1' - 7 1/4"; (A/2)-2"=1' - 5"; (NOZZLE_HEIGHT-(NOZZLE_HEIGHT/8*2))/2=1' - 7 25/32"; (NOZZLE_WB_OD-NOZZLE_TOP_OD)/2=0' - 4 9/16"; -A=-3' - 2"; A=3' - 2"; A+.5=3' - 2 1/2"; A/2=1' - 7"; B=8' - 8"; B/2=4' - 4"; C=4' - 2"; C/2=2' - 1"; DUAL_F=7' - 6 1/4"; DUAL_F+1"=7' - 7 1/4"; DUAL_G=7' - 5 1/8"; E=3' - 0 15/16"; GA=0' - 0 3/32"; LONG_RO=11' - 3"; MB_A=4' - 1"; MB_HT=3' - 5 3/16"; MB_HT+.25"=3' - 5 7/16"; MB_HT-2.75"=3' - 2 7/16"; MB_HT/2=1' - 8 19/32"; Model=QMXHPVP-1X3_Mixing Box; NOZZLE_BOTTOM_ID=2' - 4 3/4"; NOZZLE_BOTTOM_RAD=1' - 2 3/8"; NOZZLE_HEIGHT=4' - 4 3/4"; NOZZLE_HEIGHT/7*2=1' - 1 3/16"; NOZZLE_SIZE=21' - 0"; NOZZLE_TOP_OD=2' - 6 3/4"; NOZZLE_TOP_RAD=1' - 3 3/8"; NOZZLE_WB/4=0' - 9 13/16"; NOZZLE_WB_OD=4' - 1"; NOZZLE_WB_RAD=2' - 0 1/2"; NOZZLE_WB_RAD-2"=1' - 10 1/2"; RO=2' - 6 3/4"; RO/2=1' - 3 3/8"; RO2/2=1' - 3 3/8"; TRANSITION_TOP=4' - 3 5/8"; TRIPLE_F+1"=11' - 11"; TRIP_F=11' - 10"; TRIP_G=11' - 9 1/4"; TYPE=1' - 0"; Type Comments=Vari-Plume Laboratory Exhaust Mixed-Flow High Pressure Inline Belt Drive With 1X3 Mixing Box; UNIT_HEIGHT=3' - 1 1/2"; UNIT_HEIGHT*.75=2' - 4 1/8"; UNIT_OD=2' - 4 3/4"; UNIT_RAD+((A/2)+.25")=2' - 9 5/8"; UNIT_RAD+((A/2)+.25")+4"=3' - 1 5/8"; UNIT_RADIUS=1' - 2 3/8"; UNIT_RADIUS*.6=1' - 0 15/16"; UNIT_RADIUS+4"=1' - 6 3/8"
- 202_QMXHPVP-21L-1X3_Mixing_Box: (A/2)+.25"=1' - 7 1/4"; (A/2)-2"=1' - 5"; (NOZZLE_HEIGHT-(NOZZLE_HEIGHT/8*2))/2=1' - 7 25/32"; (NOZZLE_WB_OD-NOZZLE_TOP_OD)/2=0' - 4 9/16"; -A=-3' - 2"; A=3' - 2"; A+.5=3' - 2 1/2"; A/2=1' - 7"; B=8' - 8"; B/2=4' - 4"; C=4' - 2"; C/2=2' - 1"; DUAL_F=7' - 6 1/4"; DUAL_F+1"=7' - 7 1/4"; DUAL_G=7' - 5 1/8"; E=3' - 0 15/16"; GA=0' - 0 3/32"; LONG_RO=11' - 3"; MB_A=4' - 1"; MB_HT=3' - 5 3/16"; MB_HT+.25"=3' - 5 7/16"; MB_HT-2.75"=3' - 2 7/16"; MB_HT/2=1' - 8 19/32"; Model=QMXHPVP-1X3_Mixing Box; NOZZLE_BOTTOM_ID=2' - 4 3/4"; NOZZLE_BOTTOM_RAD=1' - 2 3/8"; NOZZLE_HEIGHT=4' - 4 3/4"; NOZZLE_HEIGHT/7*2=1' - 1 3/16"; NOZZLE_SIZE=21' - 0"; NOZZLE_TOP_OD=2' - 6 3/4"; NOZZLE_TOP_RAD=1' - 3 3/8"; NOZZLE_WB/4=0' - 9 13/16"; NOZZLE_WB_OD=4' - 1"; NOZZLE_WB_RAD=2' - 0 1/2"; NOZZLE_WB_RAD-2"=1' - 10 1/2"; RO=2' - 6 3/4"; RO/2=1' - 3 3/8"; RO2/2=1' - 3 3/8"; TRANSITION_TOP=4' - 3 5/8"; TRIPLE_F+1"=11' - 11"; TRIP_F=11' - 10"; TRIP_G=11' - 9 1/4"; TYPE=1' - 0"; Type Comments=Vari-Plume Laboratory Exhaust Mixed-Flow High Pressure Inline Belt Drive With 1X3 Mixing Box; UNIT_HEIGHT=3' - 1 1/2"; UNIT_HEIGHT*.75=2' - 4 1/8"; UNIT_OD=2' - 4 3/4"; UNIT_RAD+((A/2)+.25")=2' - 9 5/8"; UNIT_RAD+((A/2)+.25")+4"=3' - 1 5/8"; UNIT_RADIUS=1' - 2 3/8"; UNIT_RADIUS*.6=1' - 0 15/16"; UNIT_RADIUS+4"=1' - 6 3/8"
- 202_QMXVP-21H-1X3_Mixing_Box: (A/2)+.25"=1' - 7 1/4"; (A/2)-2"=1' - 5"; (NOZZLE_HEIGHT-(NOZZLE_HEIGHT/8*2))/2=1' - 7 25/32"; (NOZZLE_WB_OD-NOZZLE_TOP_OD)/2=0' - 4 9/16"; -A=-3' - 2"; A=3' - 2"; A+.5=3' - 2 1/2"; A/2=1' - 7"; B=8' - 8"; B/2=4' - 4"; C=4' - 2"; C/2=2' - 1"; DUAL_F=7' - 6 1/4"; DUAL_F+1"=7' - 7 1/4"; DUAL_G=7' - 5 1/8"; E=3' - 0 15/16"; GA=0' - 0 3/32"; LONG_RO=11' - 3"; MB_A=4' - 1"; MB_HT=3' - 5 3/16"; MB_HT+.25"=3' - 5 7/16"; MB_HT-2.75"=3' - 2 7/16"; MB_HT/2=1' - 8 19/32"; Model=QMXVP-1X3_Mixing Box; NOZZLE_BOTTOM_ID=2' - 4 3/4"; NOZZLE_BOTTOM_RAD=1' - 2 3/8"; NOZZLE_HEIGHT=4' - 4 3/4"; NOZZLE_HEIGHT/7*2=1' - 1 3/16"; NOZZLE_SIZE=21' - 0"; NOZZLE_TOP_OD=2' - 6 3/4"; NOZZLE_TOP_RAD=1' - 3 3/8"; NOZZLE_WB/4=0' - 9 13/16"; NOZZLE_WB_OD=4' - 1"; NOZZLE_WB_RAD=2' - 0 1/2"; NOZZLE_WB_RAD-2"=1' - 10 1/2"; RO=2' - 6 3/4"; RO/2=1' - 3 3/8"; RO2/2=1' - 3 3/8"; TRANSITION_TOP=4' - 3 5/8"; TRIPLE_F+1"=11' - 11"; TRIP_F=11' - 10"; TRIP_G=11' - 9 1/4"; TYPE=0' - 0"; Type Comments=Vari-Plume Laboratory Exhaust Mixed-Flow Inline Belt Drive With 1X3 Mixing Box; UNIT_HEIGHT=3' - 1 1/2"; UNIT_HEIGHT*.75=2' - 4 1/8"; UNIT_OD=2' - 4 3/4"; UNIT_RAD+((A/2)+.25")=2' - 9 5/8"; UNIT_RAD+((A/2)+.25")+4"=3' - 1 5/8"; UNIT_RADIUS=1' - 2 3/8"; UNIT_RADIUS*.6=1' - 0 15/16"; UNIT_RADIUS+4"=1' - 6 3/8"
- 202_QMXVP-21L-1X3_Mixing_Box: (A/2)+.25"=1' - 7 1/4"; (A/2)-2"=1' - 5"; (NOZZLE_HEIGHT-(NOZZLE_HEIGHT/8*2))/2=1' - 7 25/32"; (NOZZLE_WB_OD-NOZZLE_TOP_OD)/2=0' - 4 9/16"; -A=-3' - 2"; A=3' - 2"; A+.5=3' - 2 1/2"; A/2=1' - 7"; B=8' - 8"; B/2=4' - 4"; C=4' - 2"; C/2=2' - 1"; DUAL_F=7' - 6 1/4"; DUAL_F+1"=7' - 7 1/4"; DUAL_G=7' - 5 1/8"; E=3' - 0 15/16"; GA=0' - 0 3/32"; LONG_RO=11' - 3"; MB_A=4' - 1"; MB_HT=3' - 5 3/16"; MB_HT+.25"=3' - 5 7/16"; MB_HT-2.75"=3' - 2 7/16"; MB_HT/2=1' - 8 19/32"; Model=QMXVP-1X3_Mixing Box; NOZZLE_BOTTOM_ID=2' - 4 3/4"; NOZZLE_BOTTOM_RAD=1' - 2 3/8"; NOZZLE_HEIGHT=4' - 4 3/4"; NOZZLE_HEIGHT/7*2=1' - 1 3/16"; NOZZLE_SIZE=21' - 0"; NOZZLE_TOP_OD=2' - 6 3/4"; NOZZLE_TOP_RAD=1' - 3 3/8"; NOZZLE_WB/4=0' - 9 13/16"; NOZZLE_WB_OD=4' - 1"; NOZZLE_WB_RAD=2' - 0 1/2"; NOZZLE_WB_RAD-2"=1' - 10 1/2"; RO=2' - 6 3/4"; RO/2=1' - 3 3/8"; RO2/2=1' - 3 3/8"; TRANSITION_TOP=4' - 3 5/8"; TRIPLE_F+1"=11' - 11"; TRIP_F=11' - 10"; TRIP_G=11' - 9 1/4"; TYPE=0' - 0"; Type Comments=Vari-Plume Laboratory Exhaust Mixed-Flow Inline Belt Drive With 1X3 Mixing Box; UNIT_HEIGHT=3' - 1 1/2"; UNIT_HEIGHT*.75=2' - 4 1/8"; UNIT_OD=2' - 4 3/4"; UNIT_RAD+((A/2)+.25")=2' - 9 5/8"; UNIT_RAD+((A/2)+.25")+4"=3' - 1 5/8"; UNIT_RADIUS=1' - 2 3/8"; UNIT_RADIUS*.6=1' - 0 15/16"; UNIT_RADIUS+4"=1' - 6 3/8"
- 225_QMXHPVP-21H-1X3_Mixing_Box: (A/2)+.25"=1' - 9 1/4"; (A/2)-2"=1' - 7"; (NOZZLE_HEIGHT-(NOZZLE_HEIGHT/8*2))/2=1' - 7 25/32"; (NOZZLE_WB_OD-NOZZLE_TOP_OD)/2=0' - 4 9/16"; -A=-3' - 6"; A=3' - 6"; A+.5=3' - 6 1/2"; A/2=1' - 9"; B=9' - 5"; B/2=4' - 8 1/2"; C=4' - 8"; C/2=2' - 4"; DUAL_F=7' - 9 1/4"; DUAL_F+1"=7' - 10 1/4"; DUAL_G=7' - 8 1/8"; E=3' - 4 15/16"; GA=0' - 0 3/32"; LONG_RO=11' - 5"; MB_A=4' - 6"; MB_HT=3' - 7 3/16"; MB_HT+.25"=3' - 7 7/16"; MB_HT-2.75"=3' - 4 7/16"; MB_HT/2=1' - 9 19/32"; Model=QMXHPVP-1X3_Mixing Box; NOZZLE_BOTTOM_ID=2' - 4 3/4"; NOZZLE_BOTTOM_RAD=1' - 2 3/8"; NOZZLE_HEIGHT=4' - 4 3/4"; NOZZLE_HEIGHT/7*2=1' - 1 3/16"; NOZZLE_SIZE=21' - 0"; NOZZLE_TOP_OD=2' - 6 3/4"; NOZZLE_TOP_RAD=1' - 3 3/8"; NOZZLE_WB/4=0' - 9 13/16"; NOZZLE_WB_OD=4' - 1"; NOZZLE_WB_RAD=2' - 0 1/2"; NOZZLE_WB_RAD-2"=1' - 10 1/2"; RO=2' - 10 3/4"; RO/2=1' - 5 3/8"; RO2/2=1' - 5 3/8"; TRANSITION_TOP=5' - 1 1/8"; TRIPLE_F+1"=12' - 1"; TRIP_F=12' - 0"; TRIP_G=11' - 11 1/4"; TYPE=1' - 0"; Type Comments=Vari-Plume Laboratory Exhaust Mixed-Flow High Pressure Inline Belt Drive With 1X3 Mixing Box; UNIT_HEIGHT=3' - 5"; UNIT_HEIGHT*.75=2' - 6 3/4"; UNIT_OD=2' - 7 15/16"; UNIT_RAD+((A/2)+.25")=3' - 1 7/32"; UNIT_RAD+((A/2)+.25")+4"=3' - 5 7/32"; UNIT_RADIUS=1' - 3 31/32"; UNIT_RADIUS*.6=1' - 2 3/8"; UNIT_RADIUS+4"=1' - 7 31/32"
- 225_QMXHPVP-21L-1X3_Mixing_Box: (A/2)+.25"=1' - 9 1/4"; (A/2)-2"=1' - 7"; (NOZZLE_HEIGHT-(NOZZLE_HEIGHT/8*2))/2=1' - 7 25/32"; (NOZZLE_WB_OD-NOZZLE_TOP_OD)/2=0' - 4 9/16"; -A=-3' - 6"; A=3' - 6"; A+.5=3' - 6 1/2"; A/2=1' - 9"; B=9' - 5"; B/2=4' - 8 1/2"; C=4' - 8"; C/2=2' - 4"; DUAL_F=7' - 9 1/4"; DUAL_F+1"=7' - 10 1/4"; DUAL_G=7' - 8 1/8"; E=3' - 4 15/16"; GA=0' - 0 3/32"; LONG_RO=11' - 5"; MB_A=4' - 6"; MB_HT=3' - 7 3/16"; MB_HT+.25"=3' - 7 7/16"; MB_HT-2.75"=3' - 4 7/16"; MB_HT/2=1' - 9 19/32"; Model=QMXHPVP-1X3_Mixing Box; NOZZLE_BOTTOM_ID=2' - 4 3/4"; NOZZLE_BOTTOM_RAD=1' - 2 3/8"; NOZZLE_HEIGHT=4' - 4 3/4"; NOZZLE_HEIGHT/7*2=1' - 1 3/16"; NOZZLE_SIZE=21' - 0"; NOZZLE_TOP_OD=2' - 6 3/4"; NOZZLE_TOP_RAD=1' - 3 3/8"; NOZZLE_WB/4=0' - 9 13/16"; NOZZLE_WB_OD=4' - 1"; NOZZLE_WB_RAD=2' - 0 1/2"; NOZZLE_WB_RAD-2"=1' - 10 1/2"; RO=2' - 10 3/4"; RO/2=1' - 5 3/8"; RO2/2=1' - 5 3/8"; TRANSITION_TOP=5' - 1 1/8"; TRIPLE_F+1"=12' - 1"; TRIP_F=12' - 0"; TRIP_G=11' - 11 1/4"; TYPE=1' - 0"; Type Comments=Vari-Plume Laboratory Exhaust Mixed-Flow High Pressure Inline Belt Drive With 1X3 Mixing Box; UNIT_HEIGHT=3' - 5"; UNIT_HEIGHT*.75=2' - 6 3/4"; UNIT_OD=2' - 7 15/16"; UNIT_RAD+((A/2)+.25")=3' - 1 7/32"; UNIT_RAD+((A/2)+.25")+4"=3' - 5 7/32"; UNIT_RADIUS=1' - 3 31/32"; UNIT_RADIUS*.6=1' - 2 3/8"; UNIT_RADIUS+4"=1' - 7 31/32"
- 225_QMXVP-21H-1X3_Mixing_Box: (A/2)+.25"=1' - 9 1/4"; (A/2)-2"=1' - 7"; (NOZZLE_HEIGHT-(NOZZLE_HEIGHT/8*2))/2=1' - 7 25/32"; (NOZZLE_WB_OD-NOZZLE_TOP_OD)/2=0' - 4 9/16"; -A=-3' - 6"; A=3' - 6"; A+.5=3' - 6 1/2"; A/2=1' - 9"; B=9' - 5"; B/2=4' - 8 1/2"; C=4' - 8"; C/2=2' - 4"; DUAL_F=7' - 9 1/4"; DUAL_F+1"=7' - 10 1/4"; DUAL_G=7' - 8 1/8"; E=3' - 4 15/16"; GA=0' - 0 3/32"; LONG_RO=11' - 5"; MB_A=4' - 6"; MB_HT=3' - 7 3/16"; MB_HT+.25"=3' - 7 7/16"; MB_HT-2.75"=3' - 4 7/16"; MB_HT/2=1' - 9 19/32"; Model=QMXVP-1X3_Mixing Box; NOZZLE_BOTTOM_ID=2' - 4 3/4"; NOZZLE_BOTTOM_RAD=1' - 2 3/8"; NOZZLE_HEIGHT=4' - 4 3/4"; NOZZLE_HEIGHT/7*2=1' - 1 3/16"; NOZZLE_SIZE=21' - 0"; NOZZLE_TOP_OD=2' - 6 3/4"; NOZZLE_TOP_RAD=1' - 3 3/8"; NOZZLE_WB/4=0' - 9 13/16"; NOZZLE_WB_OD=4' - 1"; NOZZLE_WB_RAD=2' - 0 1/2"; NOZZLE_WB_RAD-2"=1' - 10 1/2"; RO=2' - 10 3/4"; RO/2=1' - 5 3/8"; RO2/2=1' - 5 3/8"; TRANSITION_TOP=5' - 1 1/8"; TRIPLE_F+1"=12' - 1"; TRIP_F=12' - 0"; TRIP_G=11' - 11 1/4"; TYPE=0' - 0"; Type Comments=Vari-Plume Laboratory Exhaust Mixed-Flow Inline Belt Drive With 1X3 Mixing Box; UNIT_HEIGHT=3' - 5"; UNIT_HEIGHT*.75=2' - 6 3/4"; UNIT_OD=2' - 7 15/16"; UNIT_RAD+((A/2)+.25")=3' - 1 7/32"; UNIT_RAD+((A/2)+.25")+4"=3' - 5 7/32"; UNIT_RADIUS=1' - 3 31/32"; UNIT_RADIUS*.6=1' - 2 3/8"; UNIT_RADIUS+4"=1' - 7 31/32"
- 225_QMXVP-21L-1X3_Mixing_Box: (A/2)+.25"=1' - 9 1/4"; (A/2)-2"=1' - 7"; (NOZZLE_HEIGHT-(NOZZLE_HEIGHT/8*2))/2=1' - 7 25/32"; (NOZZLE_WB_OD-NOZZLE_TOP_OD)/2=0' - 4 9/16"; -A=-3' - 6"; A=3' - 6"; A+.5=3' - 6 1/2"; A/2=1' - 9"; B=9' - 5"; B/2=4' - 8 1/2"; C=4' - 8"; C/2=2' - 4"; DUAL_F=7' - 9 1/4"; DUAL_F+1"=7' - 10 1/4"; DUAL_G=7' - 8 1/8"; E=3' - 4 15/16"; GA=0' - 0 3/32"; LONG_RO=11' - 5"; MB_A=4' - 6"; MB_HT=3' - 7 3/16"; MB_HT+.25"=3' - 7 7/16"; MB_HT-2.75"=3' - 4 7/16"; MB_HT/2=1' - 9 19/32"; Model=QMXVP-1X3_Mixing Box; NOZZLE_BOTTOM_ID=2' - 4 3/4"; NOZZLE_BOTTOM_RAD=1' - 2 3/8"; NOZZLE_HEIGHT=4' - 4 3/4"; NOZZLE_HEIGHT/7*2=1' - 1 3/16"; NOZZLE_SIZE=21' - 0"; NOZZLE_TOP_OD=2' - 6 3/4"; NOZZLE_TOP_RAD=1' - 3 3/8"; NOZZLE_WB/4=0' - 9 13/16"; NOZZLE_WB_OD=4' - 1"; NOZZLE_WB_RAD=2' - 0 1/2"; NOZZLE_WB_RAD-2"=1' - 10 1/2"; RO=2' - 10 3/4"; RO/2=1' - 5 3/8"; RO2/2=1' - 5 3/8"; TRANSITION_TOP=5' - 1 1/8"; TRIPLE_F+1"=12' - 1"; TRIP_F=12' - 0"; TRIP_G=11' - 11 1/4"; TYPE=0' - 0"; Type Comments=Vari-Plume Laboratory Exhaust Mixed-Flow Inline Belt Drive With 1X3 Mixing Box; UNIT_HEIGHT=3' - 5"; UNIT_HEIGHT*.75=2' - 6 3/4"; UNIT_OD=2' - 7 15/16"; UNIT_RAD+((A/2)+.25")=3' - 1 7/32"; UNIT_RAD+((A/2)+.25")+4"=3' - 5 7/32"; UNIT_RADIUS=1' - 3 31/32"; UNIT_RADIUS*.6=1' - 2 3/8"; UNIT_RADIUS+4"=1' - 7 31/32"
- 245_QMXHPVP-21H-1X3_Mixing_Box: (A/2)+.25"=1' - 10 1/4"; (A/2)-2"=1' - 8"; (NOZZLE_HEIGHT-(NOZZLE_HEIGHT/8*2))/2=1' - 7 25/32"; (NOZZLE_WB_OD-NOZZLE_TOP_OD)/2=0' - 4 9/16"; -A=-3' - 8"; A=3' - 8"; A+.5=3' - 8 1/2"; A/2=1' - 10"; B=10' - 1"; B/2=5' - 0 1/2"; C=4' - 11"; C/2=2' - 5 1/2"; DUAL_F=9' - 0 1/4"; DUAL_F+1"=9' - 1 1/4"; DUAL_G=8' - 11 1/8"; E=3' - 6 15/16"; GA=0' - 0 3/32"; LONG_RO=13' - 9 1/16"; MB_A=4' - 9"; MB_HT=3' - 9 7/16"; MB_HT+.25"=3' - 9 11/16"; MB_HT-2.75"=3' - 6 11/16"; MB_HT/2=1' - 10 23/32"; Model=QMXHPVP-1X3_Mixing Box; NOZZLE_BOTTOM_ID=2' - 4 3/4"; NOZZLE_BOTTOM_RAD=1' - 2 3/8"; NOZZLE_HEIGHT=4' - 4 3/4"; NOZZLE_HEIGHT/7*2=1' - 1 3/16"; NOZZLE_SIZE=21' - 0"; NOZZLE_TOP_OD=2' - 6 3/4"; NOZZLE_TOP_RAD=1' - 3 3/8"; NOZZLE_WB/4=0' - 9 13/16"; NOZZLE_WB_OD=4' - 1"; NOZZLE_WB_RAD=2' - 0 1/2"; NOZZLE_WB_RAD-2"=1' - 10 1/2"; RO=3' - 0 3/4"; RO/2=1' - 6 3/8"; RO2/2=1' - 6 3/8"; TRANSITION_TOP=5' - 9 11/16"; TRIPLE_F+1"=14' - 5"; TRIP_F=14' - 4"; TRIP_G=14' - 3 5/16"; TYPE=1' - 0"; Type Comments=Vari-Plume Laboratory Exhaust Mixed-Flow High Pressure Inline Belt Drive With 1X3 Mixing Box; UNIT_HEIGHT=3' - 8 1/2"; UNIT_HEIGHT*.75=2' - 9 3/8"; UNIT_OD=2' - 10 3/4"; UNIT_RAD+((A/2)+.25")=3' - 3 5/8"; UNIT_RAD+((A/2)+.25")+4"=3' - 7 5/8"; UNIT_RADIUS=1' - 5 3/8"; UNIT_RADIUS*.6=1' - 3 5/8"; UNIT_RADIUS+4"=1' - 9 3/8"
- 245_QMXHPVP-21L-1X3_Mixing_Box: (A/2)+.25"=1' - 10 1/4"; (A/2)-2"=1' - 8"; (NOZZLE_HEIGHT-(NOZZLE_HEIGHT/8*2))/2=1' - 7 25/32"; (NOZZLE_WB_OD-NOZZLE_TOP_OD)/2=0' - 4 9/16"; -A=-3' - 8"; A=3' - 8"; A+.5=3' - 8 1/2"; A/2=1' - 10"; B=10' - 1"; B/2=5' - 0 1/2"; C=4' - 11"; C/2=2' - 5 1/2"; DUAL_F=9' - 0 1/4"; DUAL_F+1"=9' - 1 1/4"; DUAL_G=8' - 11 1/8"; E=3' - 6 15/16"; GA=0' - 0 3/32"; LONG_RO=13' - 9 1/16"; MB_A=4' - 9"; MB_HT=3' - 9 7/16"; MB_HT+.25"=3' - 9 11/16"; MB_HT-2.75"=3' - 6 11/16"; MB_HT/2=1' - 10 23/32"; Model=QMXHPVP-1X3_Mixing Box; NOZZLE_BOTTOM_ID=2' - 4 3/4"; NOZZLE_BOTTOM_RAD=1' - 2 3/8"; NOZZLE_HEIGHT=4' - 4 3/4"; NOZZLE_HEIGHT/7*2=1' - 1 3/16"; NOZZLE_SIZE=21' - 0"; NOZZLE_TOP_OD=2' - 6 3/4"; NOZZLE_TOP_RAD=1' - 3 3/8"; NOZZLE_WB/4=0' - 9 13/16"; NOZZLE_WB_OD=4' - 1"; NOZZLE_WB_RAD=2' - 0 1/2"; NOZZLE_WB_RAD-2"=1' - 10 1/2"; RO=3' - 0 3/4"; RO/2=1' - 6 3/8"; RO2/2=1' - 6 3/8"; TRANSITION_TOP=5' - 9 11/16"; TRIPLE_F+1"=14' - 5"; TRIP_F=14' - 4"; TRIP_G=14' - 3 5/16"; TYPE=1' - 0"; Type Comments=Vari-Plume Laboratory Exhaust Mixed-Flow High Pressure Inline Belt Drive With 1X3 Mixing Box; UNIT_HEIGHT=3' - 8 1/2"; UNIT_HEIGHT*.75=2' - 9 3/8"; UNIT_OD=2' - 10 3/4"; UNIT_RAD+((A/2)+.25")=3' - 3 5/8"; UNIT_RAD+((A/2)+.25")+4"=3' - 7 5/8"; UNIT_RADIUS=1' - 5 3/8"; UNIT_RADIUS*.6=1' - 3 5/8"; UNIT_RADIUS+4"=1' - 9 3/8"
- 245_QMXVP-21H-1X3_Mixing_Box: (A/2)+.25"=1' - 10 1/4"; (A/2)-2"=1' - 8"; (NOZZLE_HEIGHT-(NOZZLE_HEIGHT/8*2))/2=1' - 7 25/32"; (NOZZLE_WB_OD-NOZZLE_TOP_OD)/2=0' - 4 9/16"; -A=-3' - 8"; A=3' - 8"; A+.5=3' - 8 1/2"; A/2=1' - 10"; B=10' - 1"; B/2=5' - 0 1/2"; C=4' - 11"; C/2=2' - 5 1/2"; DUAL_F=9' - 0 1/4"; DUAL_F+1"=9' - 1 1/4"; DUAL_G=8' - 11 1/8"; E=3' - 6 15/16"; GA=0' - 0 3/32"; LONG_RO=13' - 9 1/16"; MB_A=4' - 9"; MB_HT=3' - 9 7/16"; MB_HT+.25"=3' - 9 11/16"; MB_HT-2.75"=3' - 6 11/16"; MB_HT/2=1' - 10 23/32"; Model=QMXVP-1X3_Mixing Box; NOZZLE_BOTTOM_ID=2' - 4 3/4"; NOZZLE_BOTTOM_RAD=1' - 2 3/8"; NOZZLE_HEIGHT=4' - 4 3/4"; NOZZLE_HEIGHT/7*2=1' - 1 3/16"; NOZZLE_SIZE=21' - 0"; NOZZLE_TOP_OD=2' - 6 3/4"; NOZZLE_TOP_RAD=1' - 3 3/8"; NOZZLE_WB/4=0' - 9 13/16"; NOZZLE_WB_OD=4' - 1"; NOZZLE_WB_RAD=2' - 0 1/2"; NOZZLE_WB_RAD-2"=1' - 10 1/2"; RO=3' - 0 3/4"; RO/2=1' - 6 3/8"; RO2/2=1' - 6 3/8"; TRANSITION_TOP=5' - 9 11/16"; TRIPLE_F+1"=14' - 5"; TRIP_F=14' - 4"; TRIP_G=14' - 3 5/16"; TYPE=0' - 0"; Type Comments=Vari-Plume Laboratory Exhaust Mixed-Flow Inline Belt Drive With 1X3 Mixing Box; UNIT_HEIGHT=3' - 8 1/2"; UNIT_HEIGHT*.75=2' - 9 3/8"; UNIT_OD=2' - 10 3/4"; UNIT_RAD+((A/2)+.25")=3' - 3 5/8"; UNIT_RAD+((A/2)+.25")+4"=3' - 7 5/8"; UNIT_RADIUS=1' - 5 3/8"; UNIT_RADIUS*.6=1' - 3 5/8"; UNIT_RADIUS+4"=1' - 9 3/8"
- 245_QMXVP-21L-1X3_Mixing_Box: (A/2)+.25"=1' - 10 1/4"; (A/2)-2"=1' - 8"; (NOZZLE_HEIGHT-(NOZZLE_HEIGHT/8*2))/2=1' - 7 25/32"; (NOZZLE_WB_OD-NOZZLE_TOP_OD)/2=0' - 4 9/16"; -A=-3' - 8"; A=3' - 8"; A+.5=3' - 8 1/2"; A/2=1' - 10"; B=10' - 1"; B/2=5' - 0 1/2"; C=4' - 11"; C/2=2' - 5 1/2"; DUAL_F=9' - 0 1/4"; DUAL_F+1"=9' - 1 1/4"; DUAL_G=8' - 11 1/8"; E=3' - 6 15/16"; GA=0' - 0 3/32"; LONG_RO=13' - 9 1/16"; MB_A=4' - 9"; MB_HT=3' - 9 7/16"; MB_HT+.25"=3' - 9 11/16"; MB_HT-2.75"=3' - 6 11/16"; MB_HT/2=1' - 10 23/32"; Model=QMXVP-1X3_Mixing Box; NOZZLE_BOTTOM_ID=2' - 4 3/4"; NOZZLE_BOTTOM_RAD=1' - 2 3/8"; NOZZLE_HEIGHT=4' - 4 3/4"; NOZZLE_HEIGHT/7*2=1' - 1 3/16"; NOZZLE_SIZE=21' - 0"; NOZZLE_TOP_OD=2' - 6 3/4"; NOZZLE_TOP_RAD=1' - 3 3/8"; NOZZLE_WB/4=0' - 9 13/16"; NOZZLE_WB_OD=4' - 1"; NOZZLE_WB_RAD=2' - 0 1/2"; NOZZLE_WB_RAD-2"=1' - 10 1/2"; RO=3' - 0 3/4"; RO/2=1' - 6 3/8"; RO2/2=1' - 6 3/8"; TRANSITION_TOP=5' - 9 11/16"; TRIPLE_F+1"=14' - 5"; TRIP_F=14' - 4"; TRIP_G=14' - 3 5/16"; TYPE=0' - 0"; Type Comments=Vari-Plume Laboratory Exhaust Mixed-Flow Inline Belt Drive With 1X3 Mixing Box; UNIT_HEIGHT=3' - 8 1/2"; UNIT_HEIGHT*.75=2' - 9 3/8"; UNIT_OD=2' - 10 3/4"; UNIT_RAD+((A/2)+.25")=3' - 3 5/8"; UNIT_RAD+((A/2)+.25")+4"=3' - 7 5/8"; UNIT_RADIUS=1' - 5 3/8"; UNIT_RADIUS*.6=1' - 3 5/8"; UNIT_RADIUS+4"=1' - 9 3/8"
- 270_QMXHPVP-21H-1X3_Mixing_Box: (A/2)+.25"=2' - 0 1/4"; (A/2)-2"=1' - 10"; (NOZZLE_HEIGHT-(NOZZLE_HEIGHT/8*2))/2=1' - 7 25/32"; (NOZZLE_WB_OD-NOZZLE_TOP_OD)/2=0' - 4 9/16"; -A=-4' - 0"; A=4' - 0"; A+.5=4' - 0 1/2"; A/2=2' - 0"; B=10' - 8"; B/2=5' - 4"; C=5' - 3"; C/2=2' - 7 1/2"; DUAL_F=9' - 4 1/4"; DUAL_F+1"=9' - 5 1/4"; DUAL_G=9' - 3 1/8"; E=3' - 10 15/16"; GA=0' - 0 3/32"; LONG_RO=14' - 1 1/16"; MB_A=5' - 2"; MB_HT=3' - 11 3/16"; MB_HT+.25"=3' - 11 7/16"; MB_HT-2.75"=3' - 8 7/16"; MB_HT/2=1' - 11 19/32"; Model=QMXHPVP-1X3_Mixing Box; NOZZLE_BOTTOM_ID=2' - 4 3/4"; NOZZLE_BOTTOM_RAD=1' - 2 3/8"; NOZZLE_HEIGHT=4' - 4 3/4"; NOZZLE_HEIGHT/7*2=1' - 1 3/16"; NOZZLE_SIZE=21' - 0"; NOZZLE_TOP_OD=2' - 6 3/4"; NOZZLE_TOP_RAD=1' - 3 3/8"; NOZZLE_WB/4=0' - 9 13/16"; NOZZLE_WB_OD=4' - 1"; NOZZLE_WB_RAD=2' - 0 1/2"; NOZZLE_WB_RAD-2"=1' - 10 1/2"; RO=3' - 4 3/4"; RO/2=1' - 8 3/8"; RO2/2=1' - 8 3/8"; TRANSITION_TOP=6' - 7 3/16"; TRIPLE_F+1"=14' - 9"; TRIP_F=14' - 8"; TRIP_G=14' - 7 5/16"; TYPE=1' - 0"; Type Comments=Vari-Plume Laboratory Exhaust Mixed-Flow High Pressure Inline Belt Drive With 1X3 Mixing Box; UNIT_HEIGHT=3' - 11"; UNIT_HEIGHT*.75=2' - 11 1/4"; UNIT_OD=3' - 2 5/16"; UNIT_RAD+((A/2)+.25")=3' - 7 13/32"; UNIT_RAD+((A/2)+.25")+4"=3' - 11 13/32"; UNIT_RADIUS=1' - 7 5/32"; UNIT_RADIUS*.6=1' - 5 1/4"; UNIT_RADIUS+4"=1' - 11 5/32"
- 270_QMXHPVP-21L-1X3_Mixing_Box: (A/2)+.25"=2' - 0 1/4"; (A/2)-2"=1' - 10"; (NOZZLE_HEIGHT-(NOZZLE_HEIGHT/8*2))/2=1' - 7 25/32"; (NOZZLE_WB_OD-NOZZLE_TOP_OD)/2=0' - 4 9/16"; -A=-4' - 0"; A=4' - 0"; A+.5=4' - 0 1/2"; A/2=2' - 0"; B=10' - 8"; B/2=5' - 4"; C=5' - 3"; C/2=2' - 7 1/2"; DUAL_F=9' - 4 1/4"; DUAL_F+1"=9' - 5 1/4"; DUAL_G=9' - 3 1/8"; E=3' - 10 15/16"; GA=0' - 0 3/32"; LONG_RO=14' - 1 1/16"; MB_A=5' - 2"; MB_HT=3' - 11 3/16"; MB_HT+.25"=3' - 11 7/16"; MB_HT-2.75"=3' - 8 7/16"; MB_HT/2=1' - 11 19/32"; Model=QMXHPVP-1X3_Mixing Box; NOZZLE_BOTTOM_ID=2' - 4 3/4"; NOZZLE_BOTTOM_RAD=1' - 2 3/8"; NOZZLE_HEIGHT=4' - 4 3/4"; NOZZLE_HEIGHT/7*2=1' - 1 3/16"; NOZZLE_SIZE=21' - 0"; NOZZLE_TOP_OD=2' - 6 3/4"; NOZZLE_TOP_RAD=1' - 3 3/8"; NOZZLE_WB/4=0' - 9 13/16"; NOZZLE_WB_OD=4' - 1"; NOZZLE_WB_RAD=2' - 0 1/2"; NOZZLE_WB_RAD-2"=1' - 10 1/2"; RO=3' - 4 3/4"; RO/2=1' - 8 3/8"; RO2/2=1' - 8 3/8"; TRANSITION_TOP=6' - 7 3/16"; TRIPLE_F+1"=14' - 9"; TRIP_F=14' - 8"; TRIP_G=14' - 7 5/16"; TYPE=1' - 0"; Type Comments=Vari-Plume Laboratory Exhaust Mixed-Flow High Pressure Inline Belt Drive With 1X3 Mixing Box; UNIT_HEIGHT=3' - 11"; UNIT_HEIGHT*.75=2' - 11 1/4"; UNIT_OD=3' - 2 5/16"; UNIT_RAD+((A/2)+.25")=3' - 7 13/32"; UNIT_RAD+((A/2)+.25")+4"=3' - 11 13/32"; UNIT_RADIUS=1' - 7 5/32"; UNIT_RADIUS*.6=1' - 5 1/4"; UNIT_RADIUS+4"=1' - 11 5/32"
- 270_QMXVP-21H-1X3_Mixing_Box: (A/2)+.25"=2' - 0 1/4"; (A/2)-2"=1' - 10"; (NOZZLE_HEIGHT-(NOZZLE_HEIGHT/8*2))/2=1' - 7 25/32"; (NOZZLE_WB_OD-NOZZLE_TOP_OD)/2=0' - 4 9/16"; -A=-4' - 0"; A=4' - 0"; A+.5=4' - 0 1/2"; A/2=2' - 0"; B=10' - 8"; B/2=5' - 4"; C=5' - 3"; C/2=2' - 7 1/2"; DUAL_F=9' - 4 1/4"; DUAL_F+1"=9' - 5 1/4"; DUAL_G=9' - 3 1/8"; E=3' - 10 15/16"; GA=0' - 0 3/32"; LONG_RO=14' - 1 1/16"; MB_A=5' - 2"; MB_HT=3' - 11 3/16"; MB_HT+.25"=3' - 11 7/16"; MB_HT-2.75"=3' - 8 7/16"; MB_HT/2=1' - 11 19/32"; Model=QMXVP-1X3_Mixing Box; NOZZLE_BOTTOM_ID=2' - 4 3/4"; NOZZLE_BOTTOM_RAD=1' - 2 3/8"; NOZZLE_HEIGHT=4' - 4 3/4"; NOZZLE_HEIGHT/7*2=1' - 1 3/16"; NOZZLE_SIZE=21' - 0"; NOZZLE_TOP_OD=2' - 6 3/4"; NOZZLE_TOP_RAD=1' - 3 3/8"; NOZZLE_WB/4=0' - 9 13/16"; NOZZLE_WB_OD=4' - 1"; NOZZLE_WB_RAD=2' - 0 1/2"; NOZZLE_WB_RAD-2"=1' - 10 1/2"; RO=3' - 4 3/4"; RO/2=1' - 8 3/8"; RO2/2=1' - 8 3/8"; TRANSITION_TOP=6' - 7 3/16"; TRIPLE_F+1"=14' - 9"; TRIP_F=14' - 8"; TRIP_G=14' - 7 5/16"; TYPE=0' - 0"; Type Comments=Vari-Plume Laboratory Exhaust Mixed-Flow Inline Belt Drive With 1X3 Mixing Box; UNIT_HEIGHT=3' - 11"; UNIT_HEIGHT*.75=2' - 11 1/4"; UNIT_OD=3' - 2 5/16"; UNIT_RAD+((A/2)+.25")=3' - 7 13/32"; UNIT_RAD+((A/2)+.25")+4"=3' - 11 13/32"; UNIT_RADIUS=1' - 7 5/32"; UNIT_RADIUS*.6=1' - 5 1/4"; UNIT_RADIUS+4"=1' - 11 5/32"
- 270_QMXVP-21L-1X3_Mixing_Box: (A/2)+.25"=2' - 0 1/4"; (A/2)-2"=1' - 10"; (NOZZLE_HEIGHT-(NOZZLE_HEIGHT/8*2))/2=1' - 7 25/32"; (NOZZLE_WB_OD-NOZZLE_TOP_OD)/2=0' - 4 9/16"; -A=-4' - 0"; A=4' - 0"; A+.5=4' - 0 1/2"; A/2=2' - 0"; B=10' - 8"; B/2=5' - 4"; C=5' - 3"; C/2=2' - 7 1/2"; DUAL_F=9' - 4 1/4"; DUAL_F+1"=9' - 5 1/4"; DUAL_G=9' - 3 1/8"; E=3' - 10 15/16"; GA=0' - 0 3/32"; LONG_RO=14' - 1 1/16"; MB_A=5' - 2"; MB_HT=3' - 11 3/16"; MB_HT+.25"=3' - 11 7/16"; MB_HT-2.75"=3' - 8 7/16"; MB_HT/2=1' - 11 19/32"; Model=QMXVP-1X3_Mixing Box; NOZZLE_BOTTOM_ID=2' - 4 3/4"; NOZZLE_BOTTOM_RAD=1' - 2 3/8"; NOZZLE_HEIGHT=4' - 4 3/4"; NOZZLE_HEIGHT/7*2=1' - 1 3/16"; NOZZLE_SIZE=21' - 0"; NOZZLE_TOP_OD=2' - 6 3/4"; NOZZLE_TOP_RAD=1' - 3 3/8"; NOZZLE_WB/4=0' - 9 13/16"; NOZZLE_WB_OD=4' - 1"; NOZZLE_WB_RAD=2' - 0 1/2"; NOZZLE_WB_RAD-2"=1' - 10 1/2"; RO=3' - 4 3/4"; RO/2=1' - 8 3/8"; RO2/2=1' - 8 3/8"; TRANSITION_TOP=6' - 7 3/16"; TRIPLE_F+1"=14' - 9"; TRIP_F=14' - 8"; TRIP_G=14' - 7 5/16"; TYPE=0' - 0"; Type Comments=Vari-Plume Laboratory Exhaust Mixed-Flow Inline Belt Drive With 1X3 Mixing Box; UNIT_HEIGHT=3' - 11"; UNIT_HEIGHT*.75=2' - 11 1/4"; UNIT_OD=3' - 2 5/16"; UNIT_RAD+((A/2)+.25")=3' - 7 13/32"; UNIT_RAD+((A/2)+.25")+4"=3' - 11 13/32"; UNIT_RADIUS=1' - 7 5/32"; UNIT_RADIUS*.6=1' - 5 1/4"; UNIT_RADIUS+4"=1' - 11 5/32"
- 300_QMXHPVP-21H-1X3_Mixing_Box: (A/2)+.25"=2' - 2 1/4"; (A/2)-2"=2' - 0"; (NOZZLE_HEIGHT-(NOZZLE_HEIGHT/8*2))/2=1' - 7 25/32"; (NOZZLE_WB_OD-NOZZLE_TOP_OD)/2=0' - 4 9/16"; -A=-4' - 4"; A=4' - 4"; A+.5=4' - 4 1/2"; A/2=2' - 2"; B=12' - 4"; B/2=6' - 2"; C=5' - 7"; C/2=2' - 9 1/2"; DUAL_F=11' - 0 1/4"; DUAL_F+1"=11' - 1 1/4"; DUAL_G=10' - 11 1/8"; E=4' - 2 15/16"; GA=0' - 0 3/32"; LONG_RO=17' - 1 1/16"; MB_A=5' - 8"; MB_HT=4' - 2 7/16"; MB_HT+.25"=4' - 2 11/16"; MB_HT-2.75"=3' - 11 11/16"; MB_HT/2=2' - 1 7/32"; Model=QMXHPVP-1X3_Mixing Box; NOZZLE_BOTTOM_ID=2' - 4 3/4"; NOZZLE_BOTTOM_RAD=1' - 2 3/8"; NOZZLE_HEIGHT=4' - 4 3/4"; NOZZLE_HEIGHT/7*2=1' - 1 3/16"; NOZZLE_SIZE=21' - 0"; NOZZLE_TOP_OD=2' - 6 3/4"; NOZZLE_TOP_RAD=1' - 3 3/8"; NOZZLE_WB/4=0' - 9 13/16"; NOZZLE_WB_OD=4' - 1"; NOZZLE_WB_RAD=2' - 0 1/2"; NOZZLE_WB_RAD-2"=1' - 10 1/2"; RO=3' - 8 3/4"; RO/2=1' - 10 3/8"; RO2/2=1' - 10 3/8"; TRANSITION_TOP=7' - 10 3/16"; TRIPLE_F+1"=17' - 9"; TRIP_F=17' - 8"; TRIP_G=17' - 7 5/16"; TYPE=1' - 0"; Type Comments=Vari-Plume Laboratory Exhaust Mixed-Flow High Pressure Inline Belt Drive With 1X3 Mixing Box; UNIT_HEIGHT=4' - 6"; UNIT_HEIGHT*.75=3' - 4 1/2"; UNIT_OD=3' - 6 1/2"; UNIT_RAD+((A/2)+.25")=3' - 11 1/2"; UNIT_RAD+((A/2)+.25")+4"=4' - 3 1/2"; UNIT_RADIUS=1' - 9 1/4"; UNIT_RADIUS*.6=1' - 7 1/8"; UNIT_RADIUS+4"=2' - 1 1/4"
- 300_QMXHPVP-21L-1X3_Mixing_Box: (A/2)+.25"=2' - 2 1/4"; (A/2)-2"=2' - 0"; (NOZZLE_HEIGHT-(NOZZLE_HEIGHT/8*2))/2=1' - 7 25/32"; (NOZZLE_WB_OD-NOZZLE_TOP_OD)/2=0' - 4 9/16"; -A=-4' - 4"; A=4' - 4"; A+.5=4' - 4 1/2"; A/2=2' - 2"; B=12' - 4"; B/2=6' - 2"; C=5' - 7"; C/2=2' - 9 1/2"; DUAL_F=11' - 0 1/4"; DUAL_F+1"=11' - 1 1/4"; DUAL_G=10' - 11 1/8"; E=4' - 2 15/16"; GA=0' - 0 3/32"; LONG_RO=17' - 1 1/16"; MB_A=5' - 8"; MB_HT=4' - 2 7/16"; MB_HT+.25"=4' - 2 11/16"; MB_HT-2.75"=3' - 11 11/16"; MB_HT/2=2' - 1 7/32"; Model=QMXHPVP-1X3_Mixing Box; NOZZLE_BOTTOM_ID=2' - 4 3/4"; NOZZLE_BOTTOM_RAD=1' - 2 3/8"; NOZZLE_HEIGHT=4' - 4 3/4"; NOZZLE_HEIGHT/7*2=1' - 1 3/16"; NOZZLE_SIZE=21' - 0"; NOZZLE_TOP_OD=2' - 6 3/4"; NOZZLE_TOP_RAD=1' - 3 3/8"; NOZZLE_WB/4=0' - 9 13/16"; NOZZLE_WB_OD=4' - 1"; NOZZLE_WB_RAD=2' - 0 1/2"; NOZZLE_WB_RAD-2"=1' - 10 1/2"; RO=3' - 8 3/4"; RO/2=1' - 10 3/8"; RO2/2=1' - 10 3/8"; TRANSITION_TOP=7' - 10 3/16"; TRIPLE_F+1"=17' - 9"; TRIP_F=17' - 8"; TRIP_G=17' - 7 5/16"; TYPE=1' - 0"; Type Comments=Vari-Plume Laboratory Exhaust Mixed-Flow High Pressure Inline Belt Drive With 1X3 Mixing Box; UNIT_HEIGHT=4' - 6"; UNIT_HEIGHT*.75=3' - 4 1/2"; UNIT_OD=3' - 6 1/2"; UNIT_RAD+((A/2)+.25")=3' - 11 1/2"; UNIT_RAD+((A/2)+.25")+4"=4' - 3 1/2"; UNIT_RADIUS=1' - 9 1/4"; UNIT_RADIUS*.6=1' - 7 1/8"; UNIT_RADIUS+4"=2' - 1 1/4"
- 300_QMXVP-21H-1X3_Mixing_Box: (A/2)+.25"=2' - 2 1/4"; (A/2)-2"=2' - 0"; (NOZZLE_HEIGHT-(NOZZLE_HEIGHT/8*2))/2=1' - 7 25/32"; (NOZZLE_WB_OD-NOZZLE_TOP_OD)/2=0' - 4 9/16"; -A=-4' - 4"; A=4' - 4"; A+.5=4' - 4 1/2"; A/2=2' - 2"; B=12' - 4"; B/2=6' - 2"; C=5' - 7"; C/2=2' - 9 1/2"; DUAL_F=11' - 0 1/4"; DUAL_F+1"=11' - 1 1/4"; DUAL_G=10' - 11 1/8"; E=4' - 2 15/16"; GA=0' - 0 3/32"; LONG_RO=17' - 1 1/16"; MB_A=5' - 8"; MB_HT=4' - 2 7/16"; MB_HT+.25"=4' - 2 11/16"; MB_HT-2.75"=3' - 11 11/16"; MB_HT/2=2' - 1 7/32"; Model=QMXVP-1X3_Mixing Box; NOZZLE_BOTTOM_ID=2' - 4 3/4"; NOZZLE_BOTTOM_RAD=1' - 2 3/8"; NOZZLE_HEIGHT=4' - 4 3/4"; NOZZLE_HEIGHT/7*2=1' - 1 3/16"; NOZZLE_SIZE=21' - 0"; NOZZLE_TOP_OD=2' - 6 3/4"; NOZZLE_TOP_RAD=1' - 3 3/8"; NOZZLE_WB/4=0' - 9 13/16"; NOZZLE_WB_OD=4' - 1"; NOZZLE_WB_RAD=2' - 0 1/2"; NOZZLE_WB_RAD-2"=1' - 10 1/2"; RO=3' - 8 3/4"; RO/2=1' - 10 3/8"; RO2/2=1' - 10 3/8"; TRANSITION_TOP=7' - 10 3/16"; TRIPLE_F+1"=17' - 9"; TRIP_F=17' - 8"; TRIP_G=17' - 7 5/16"; TYPE=0' - 0"; Type Comments=Vari-Plume Laboratory Exhaust Mixed-Flow Inline Belt Drive With 1X3 Mixing Box; UNIT_HEIGHT=4' - 6"; UNIT_HEIGHT*.75=3' - 4 1/2"; UNIT_OD=3' - 6 1/2"; UNIT_RAD+((A/2)+.25")=3' - 11 1/2"; UNIT_RAD+((A/2)+.25")+4"=4' - 3 1/2"; UNIT_RADIUS=1' - 9 1/4"; UNIT_RADIUS*.6=1' - 7 1/8"; UNIT_RADIUS+4"=2' - 1 1/4"
- 300_QMXVP-21L-1X3_Mixing_Box: (A/2)+.25"=2' - 2 1/4"; (A/2)-2"=2' - 0"; (NOZZLE_HEIGHT-(NOZZLE_HEIGHT/8*2))/2=1' - 7 25/32"; (NOZZLE_WB_OD-NOZZLE_TOP_OD)/2=0' - 4 9/16"; -A=-4' - 4"; A=4' - 4"; A+.5=4' - 4 1/2"; A/2=2' - 2"; B=12' - 4"; B/2=6' - 2"; C=5' - 7"; C/2=2' - 9 1/2"; DUAL_F=11' - 0 1/4"; DUAL_F+1"=11' - 1 1/4"; DUAL_G=10' - 11 1/8"; E=4' - 2 15/16"; GA=0' - 0 3/32"; LONG_RO=17' - 1 1/16"; MB_A=5' - 8"; MB_HT=4' - 2 7/16"; MB_HT+.25"=4' - 2 11/16"; MB_HT-2.75"=3' - 11 11/16"; MB_HT/2=2' - 1 7/32"; Model=QMXVP-1X3_Mixing Box; NOZZLE_BOTTOM_ID=2' - 4 3/4"; NOZZLE_BOTTOM_RAD=1' - 2 3/8"; NOZZLE_HEIGHT=4' - 4 3/4"; NOZZLE_HEIGHT/7*2=1' - 1 3/16"; NOZZLE_SIZE=21' - 0"; NOZZLE_TOP_OD=2' - 6 3/4"; NOZZLE_TOP_RAD=1' - 3 3/8"; NOZZLE_WB/4=0' - 9 13/16"; NOZZLE_WB_OD=4' - 1"; NOZZLE_WB_RAD=2' - 0 1/2"; NOZZLE_WB_RAD-2"=1' - 10 1/2"; RO=3' - 8 3/4"; RO/2=1' - 10 3/8"; RO2/2=1' - 10 3/8"; TRANSITION_TOP=7' - 10 3/16"; TRIPLE_F+1"=17' - 9"; TRIP_F=17' - 8"; TRIP_G=17' - 7 5/16"; TYPE=0' - 0"; Type Comments=Vari-Plume Laboratory Exhaust Mixed-Flow Inline Belt Drive With 1X3 Mixing Box; UNIT_HEIGHT=4' - 6"; UNIT_HEIGHT*.75=3' - 4 1/2"; UNIT_OD=3' - 6 1/2"; UNIT_RAD+((A/2)+.25")=3' - 11 1/2"; UNIT_RAD+((A/2)+.25")+4"=4' - 3 1/2"; UNIT_RADIUS=1' - 9 1/4"; UNIT_RADIUS*.6=1' - 7 1/8"; UNIT_RADIUS+4"=2' - 1 1/4"
- 270_QMXHPVP-27H-1X3_Mixing_Box: (A/2)+.25"=2' - 0 1/4"; (A/2)-2"=1' - 10"; (NOZZLE_HEIGHT-(NOZZLE_HEIGHT/8*2))/2=1' - 10 3/4"; (NOZZLE_WB_OD-NOZZLE_TOP_OD)/2=0' - 5 11/32"; -A=-4' - 0"; A=4' - 0"; A+.5=4' - 0 1/2"; A/2=2' - 0"; B=10' - 8"; B/2=5' - 4"; C=5' - 3"; C/2=2' - 7 1/2"; DUAL_F=9' - 4 1/4"; DUAL_F+1"=9' - 5 1/4"; DUAL_G=9' - 3 1/8"; E=3' - 10 15/16"; GA=0' - 0 3/32"; LONG_RO=14' - 1 1/16"; MB_A=5' - 2"; MB_HT=3' - 11 3/16"; MB_HT+.25"=3' - 11 7/16"; MB_HT-2.75"=3' - 8 7/16"; MB_HT/2=1' - 11 19/32"; Model=QMXHPVP-1X3_Mixing Box; NOZZLE_BOTTOM_ID=3' - 2 5/16"; NOZZLE_BOTTOM_RAD=1' - 7 5/32"; NOZZLE_HEIGHT=5' - 0 5/8"; NOZZLE_HEIGHT/7*2=1' - 3 5/32"; NOZZLE_SIZE=27' - 0"; NOZZLE_TOP_OD=3' - 3 11/16"; NOZZLE_TOP_RAD=1' - 7 27/32"; NOZZLE_WB/4=1' - 0 3/16"; NOZZLE_WB_OD=5' - 1"; NOZZLE_WB_RAD=2' - 6 1/2"; NOZZLE_WB_RAD-2"=2' - 4 1/2"; RO=3' - 4 3/4"; RO/2=1' - 8 3/8"; RO2/2=1' - 8 3/8"; TRANSITION_TOP=5' - 2 1/4"; TRIPLE_F+1"=14' - 9"; TRIP_F=14' - 8"; TRIP_G=14' - 7 5/16"; TYPE=1' - 0"; Type Comments=Vari-Plume Laboratory Exhaust Mixed-Flow High Pressure Inline Belt Drive With 1X3 Mixing Box; UNIT_HEIGHT=3' - 11"; UNIT_HEIGHT*.75=2' - 11 1/4"; UNIT_OD=3' - 2 5/16"; UNIT_RAD+((A/2)+.25")=3' - 7 13/32"; UNIT_RAD+((A/2)+.25")+4"=3' - 11 13/32"; UNIT_RADIUS=1' - 7 5/32"; UNIT_RADIUS*.6=1' - 5 1/4"; UNIT_RADIUS+4"=1' - 11 5/32"
- 270_QMXHPVP-27L-1X3_Mixing_Box: (A/2)+.25"=2' - 0 1/4"; (A/2)-2"=1' - 10"; (NOZZLE_HEIGHT-(NOZZLE_HEIGHT/8*2))/2=1' - 10 3/4"; (NOZZLE_WB_OD-NOZZLE_TOP_OD)/2=0' - 5 11/32"; -A=-4' - 0"; A=4' - 0"; A+.5=4' - 0 1/2"; A/2=2' - 0"; B=10' - 8"; B/2=5' - 4"; C=5' - 3"; C/2=2' - 7 1/2"; DUAL_F=9' - 4 1/4"; DUAL_F+1"=9' - 5 1/4"; DUAL_G=9' - 3 1/8"; E=3' - 10 15/16"; GA=0' - 0 3/32"; LONG_RO=14' - 1 1/16"; MB_A=5' - 2"; MB_HT=3' - 11 3/16"; MB_HT+.25"=3' - 11 7/16"; MB_HT-2.75"=3' - 8 7/16"; MB_HT/2=1' - 11 19/32"; Model=QMXHPVP-1X3_Mixing Box; NOZZLE_BOTTOM_ID=3' - 2 5/16"; NOZZLE_BOTTOM_RAD=1' - 7 5/32"; NOZZLE_HEIGHT=5' - 0 5/8"; NOZZLE_HEIGHT/7*2=1' - 3 5/32"; NOZZLE_SIZE=27' - 0"; NOZZLE_TOP_OD=3' - 3 11/16"; NOZZLE_TOP_RAD=1' - 7 27/32"; NOZZLE_WB/4=1' - 0 3/16"; NOZZLE_WB_OD=5' - 1"; NOZZLE_WB_RAD=2' - 6 1/2"; NOZZLE_WB_RAD-2"=2' - 4 1/2"; RO=3' - 4 3/4"; RO/2=1' - 8 3/8"; RO2/2=1' - 8 3/8"; TRANSITION_TOP=5' - 2 1/4"; TRIPLE_F+1"=14' - 9"; TRIP_F=14' - 8"; TRIP_G=14' - 7 5/16"; TYPE=1' - 0"; Type Comments=Vari-Plume Laboratory Exhaust Mixed-Flow High Pressure Inline Belt Drive With 1X3 Mixing Box; UNIT_HEIGHT=3' - 11"; UNIT_HEIGHT*.75=2' - 11 1/4"; UNIT_OD=3' - 2 5/16"; UNIT_RAD+((A/2)+.25")=3' - 7 13/32"; UNIT_RAD+((A/2)+.25")+4"=3' - 11 13/32"; UNIT_RADIUS=1' - 7 5/32"; UNIT_RADIUS*.6=1' - 5 1/4"; UNIT_RADIUS+4"=1' - 11 5/32"
- 270_QMXVP-27H-1X3_Mixing_Box: (A/2)+.25"=2' - 0 1/4"; (A/2)-2"=1' - 10"; (NOZZLE_HEIGHT-(NOZZLE_HEIGHT/8*2))/2=1' - 10 3/4"; (NOZZLE_WB_OD-NOZZLE_TOP_OD)/2=0' - 5 11/32"; -A=-4' - 0"; A=4' - 0"; A+.5=4' - 0 1/2"; A/2=2' - 0"; B=10' - 8"; B/2=5' - 4"; C=5' - 3"; C/2=2' - 7 1/2"; DUAL_F=9' - 4 1/4"; DUAL_F+1"=9' - 5 1/4"; DUAL_G=9' - 3 1/8"; E=3' - 10 15/16"; GA=0' - 0 3/32"; LONG_RO=14' - 1 1/16"; MB_A=5' - 2"; MB_HT=3' - 11 3/16"; MB_HT+.25"=3' - 11 7/16"; MB_HT-2.75"=3' - 8 7/16"; MB_HT/2=1' - 11 19/32"; Model=QMXVP-1X3_Mixing Box; NOZZLE_BOTTOM_ID=3' - 2 5/16"; NOZZLE_BOTTOM_RAD=1' - 7 5/32"; NOZZLE_HEIGHT=5' - 0 5/8"; NOZZLE_HEIGHT/7*2=1' - 3 5/32"; NOZZLE_SIZE=27' - 0"; NOZZLE_TOP_OD=3' - 3 11/16"; NOZZLE_TOP_RAD=1' - 7 27/32"; NOZZLE_WB/4=1' - 0 3/16"; NOZZLE_WB_OD=5' - 1"; NOZZLE_WB_RAD=2' - 6 1/2"; NOZZLE_WB_RAD-2"=2' - 4 1/2"; RO=3' - 4 3/4"; RO/2=1' - 8 3/8"; RO2/2=1' - 8 3/8"; TRANSITION_TOP=5' - 2 1/4"; TRIPLE_F+1"=14' - 9"; TRIP_F=14' - 8"; TRIP_G=14' - 7 5/16"; TYPE=0' - 0"; Type Comments=Vari-Plume Laboratory Exhaust Mixed-Flow Inline Belt Drive With 1X3 Mixing Box; UNIT_HEIGHT=3' - 11"; UNIT_HEIGHT*.75=2' - 11 1/4"; UNIT_OD=3' - 2 5/16"; UNIT_RAD+((A/2)+.25")=3' - 7 13/32"; UNIT_RAD+((A/2)+.25")+4"=3' - 11 13/32"; UNIT_RADIUS=1' - 7 5/32"; UNIT_RADIUS*.6=1' - 5 1/4"; UNIT_RADIUS+4"=1' - 11 5/32"
- 270_QMXVP-27L-1X3_Mixing_Box: (A/2)+.25"=2' - 0 1/4"; (A/2)-2"=1' - 10"; (NOZZLE_HEIGHT-(NOZZLE_HEIGHT/8*2))/2=1' - 10 3/4"; (NOZZLE_WB_OD-NOZZLE_TOP_OD)/2=0' - 5 11/32"; -A=-4' - 0"; A=4' - 0"; A+.5=4' - 0 1/2"; A/2=2' - 0"; B=10' - 8"; B/2=5' - 4"; C=5' - 3"; C/2=2' - 7 1/2"; DUAL_F=9' - 4 1/4"; DUAL_F+1"=9' - 5 1/4"; DUAL_G=9' - 3 1/8"; E=3' - 10 15/16"; GA=0' - 0 3/32"; LONG_RO=14' - 1 1/16"; MB_A=5' - 2"; MB_HT=3' - 11 3/16"; MB_HT+.25"=3' - 11 7/16"; MB_HT-2.75"=3' - 8 7/16"; MB_HT/2=1' - 11 19/32"; Model=QMXVP-1X3_Mixing Box; NOZZLE_BOTTOM_ID=3' - 2 5/16"; NOZZLE_BOTTOM_RAD=1' - 7 5/32"; NOZZLE_HEIGHT=5' - 0 5/8"; NOZZLE_HEIGHT/7*2=1' - 3 5/32"; NOZZLE_SIZE=27' - 0"; NOZZLE_TOP_OD=3' - 3 11/16"; NOZZLE_TOP_RAD=1' - 7 27/32"; NOZZLE_WB/4=1' - 0 3/16"; NOZZLE_WB_OD=5' - 1"; NOZZLE_WB_RAD=2' - 6 1/2"; NOZZLE_WB_RAD-2"=2' - 4 1/2"; RO=3' - 4 3/4"; RO/2=1' - 8 3/8"; RO2/2=1' - 8 3/8"; TRANSITION_TOP=5' - 2 1/4"; TRIPLE_F+1"=14' - 9"; TRIP_F=14' - 8"; TRIP_G=14' - 7 5/16"; TYPE=0' - 0"; Type Comments=Vari-Plume Laboratory Exhaust Mixed-Flow Inline Belt Drive With 1X3 Mixing Box; UNIT_HEIGHT=3' - 11"; UNIT_HEIGHT*.75=2' - 11 1/4"; UNIT_OD=3' - 2 5/16"; UNIT_RAD+((A/2)+.25")=3' - 7 13/32"; UNIT_RAD+((A/2)+.25")+4"=3' - 11 13/32"; UNIT_RADIUS=1' - 7 5/32"; UNIT_RADIUS*.6=1' - 5 1/4"; UNIT_RADIUS+4"=1' - 11 5/32"
- 300_QMXHPVP-27H-1X3_Mixing_Box: (A/2)+.25"=2' - 2 1/4"; (A/2)-2"=2' - 0"; (NOZZLE_HEIGHT-(NOZZLE_HEIGHT/8*2))/2=1' - 10 3/4"; (NOZZLE_WB_OD-NOZZLE_TOP_OD)/2=0' - 5 11/32"; -A=-4' - 4"; A=4' - 4"; A+.5=4' - 4 1/2"; A/2=2' - 2"; B=12' - 4"; B/2=6' - 2"; C=5' - 7"; C/2=2' - 9 1/2"; DUAL_F=11' - 0 1/4"; DUAL_F+1"=11' - 1 1/4"; DUAL_G=10' - 11 1/8"; E=4' - 2 15/16"; GA=0' - 0 3/32"; LONG_RO=17' - 1 1/16"; MB_A=5' - 8"; MB_HT=4' - 2 7/16"; MB_HT+.25"=4' - 2 11/16"; MB_HT-2.75"=3' - 11 11/16"; MB_HT/2=2' - 1 7/32"; Model=QMXHPVP-1X3_Mixing Box; NOZZLE_BOTTOM_ID=3' - 2 5/16"; NOZZLE_BOTTOM_RAD=1' - 7 5/32"; NOZZLE_HEIGHT=5' - 0 5/8"; NOZZLE_HEIGHT/7*2=1' - 3 5/32"; NOZZLE_SIZE=27' - 0"; NOZZLE_TOP_OD=3' - 3 11/16"; NOZZLE_TOP_RAD=1' - 7 27/32"; NOZZLE_WB/4=1' - 0 3/16"; NOZZLE_WB_OD=5' - 1"; NOZZLE_WB_RAD=2' - 6 1/2"; NOZZLE_WB_RAD-2"=2' - 4 1/2"; RO=3' - 8 3/4"; RO/2=1' - 10 3/8"; RO2/2=1' - 10 3/8"; TRANSITION_TOP=6' - 5 1/4"; TRIPLE_F+1"=17' - 9"; TRIP_F=17' - 8"; TRIP_G=17' - 7 5/16"; TYPE=1' - 0"; Type Comments=Vari-Plume Laboratory Exhaust Mixed-Flow High Pressure Inline Belt Drive With 1X3 Mixing Box; UNIT_HEIGHT=4' - 6"; UNIT_HEIGHT*.75=3' - 4 1/2"; UNIT_OD=3' - 6 1/2"; UNIT_RAD+((A/2)+.25")=3' - 11 1/2"; UNIT_RAD+((A/2)+.25")+4"=4' - 3 1/2"; UNIT_RADIUS=1' - 9 1/4"; UNIT_RADIUS*.6=1' - 7 1/8"; UNIT_RADIUS+4"=2' - 1 1/4"
- 300_QMXHPVP-27L-1X3_Mixing_Box: (A/2)+.25"=2' - 2 1/4"; (A/2)-2"=2' - 0"; (NOZZLE_HEIGHT-(NOZZLE_HEIGHT/8*2))/2=1' - 10 3/4"; (NOZZLE_WB_OD-NOZZLE_TOP_OD)/2=0' - 5 11/32"; -A=-4' - 4"; A=4' - 4"; A+.5=4' - 4 1/2"; A/2=2' - 2"; B=12' - 4"; B/2=6' - 2"; C=5' - 7"; C/2=2' - 9 1/2"; DUAL_F=11' - 0 1/4"; DUAL_F+1"=11' - 1 1/4"; DUAL_G=10' - 11 1/8"; E=4' - 2 15/16"; GA=0' - 0 3/32"; LONG_RO=17' - 1 1/16"; MB_A=5' - 8"; MB_HT=4' - 2 7/16"; MB_HT+.25"=4' - 2 11/16"; MB_HT-2.75"=3' - 11 11/16"; MB_HT/2=2' - 1 7/32"; Model=QMXHPVP-1X3_Mixing Box; NOZZLE_BOTTOM_ID=3' - 2 5/16"; NOZZLE_BOTTOM_RAD=1' - 7 5/32"; NOZZLE_HEIGHT=5' - 0 5/8"; NOZZLE_HEIGHT/7*2=1' - 3 5/32"; NOZZLE_SIZE=27' - 0"; NOZZLE_TOP_OD=3' - 3 11/16"; NOZZLE_TOP_RAD=1' - 7 27/32"; NOZZLE_WB/4=1' - 0 3/16"; NOZZLE_WB_OD=5' - 1"; NOZZLE_WB_RAD=2' - 6 1/2"; NOZZLE_WB_RAD-2"=2' - 4 1/2"; RO=3' - 8 3/4"; RO/2=1' - 10 3/8"; RO2/2=1' - 10 3/8"; TRANSITION_TOP=6' - 5 1/4"; TRIPLE_F+1"=17' - 9"; TRIP_F=17' - 8"; TRIP_G=17' - 7 5/16"; TYPE=1' - 0"; Type Comments=Vari-Plume Laboratory Exhaust Mixed-Flow High Pressure Inline Belt Drive With 1X3 Mixing Box; UNIT_HEIGHT=4' - 6"; UNIT_HEIGHT*.75=3' - 4 1/2"; UNIT_OD=3' - 6 1/2"; UNIT_RAD+((A/2)+.25")=3' - 11 1/2"; UNIT_RAD+((A/2)+.25")+4"=4' - 3 1/2"; UNIT_RADIUS=1' - 9 1/4"; UNIT_RADIUS*.6=1' - 7 1/8"; UNIT_RADIUS+4"=2' - 1 1/4"
- 300_QMXVP-27H-1X3_Mixing_Box: (A/2)+.25"=2' - 2 1/4"; (A/2)-2"=2' - 0"; (NOZZLE_HEIGHT-(NOZZLE_HEIGHT/8*2))/2=1' - 10 3/4"; (NOZZLE_WB_OD-NOZZLE_TOP_OD)/2=0' - 5 11/32"; -A=-4' - 4"; A=4' - 4"; A+.5=4' - 4 1/2"; A/2=2' - 2"; B=12' - 4"; B/2=6' - 2"; C=5' - 7"; C/2=2' - 9 1/2"; DUAL_F=11' - 0 1/4"; DUAL_F+1"=11' - 1 1/4"; DUAL_G=10' - 11 1/8"; E=4' - 2 15/16"; GA=0' - 0 3/32"; LONG_RO=17' - 1 1/16"; MB_A=5' - 8"; MB_HT=4' - 2 7/16"; MB_HT+.25"=4' - 2 11/16"; MB_HT-2.75"=3' - 11 11/16"; MB_HT/2=2' - 1 7/32"; Model=QMXVP-1X3_Mixing Box; NOZZLE_BOTTOM_ID=3' - 2 5/16"; NOZZLE_BOTTOM_RAD=1' - 7 5/32"; NOZZLE_HEIGHT=5' - 0 5/8"; NOZZLE_HEIGHT/7*2=1' - 3 5/32"; NOZZLE_SIZE=27' - 0"; NOZZLE_TOP_OD=3' - 3 11/16"; NOZZLE_TOP_RAD=1' - 7 27/32"; NOZZLE_WB/4=1' - 0 3/16"; NOZZLE_WB_OD=5' - 1"; NOZZLE_WB_RAD=2' - 6 1/2"; NOZZLE_WB_RAD-2"=2' - 4 1/2"; RO=3' - 8 3/4"; RO/2=1' - 10 3/8"; RO2/2=1' - 10 3/8"; TRANSITION_TOP=6' - 5 1/4"; TRIPLE_F+1"=17' - 9"; TRIP_F=17' - 8"; TRIP_G=17' - 7 5/16"; TYPE=0' - 0"; Type Comments=Vari-Plume Laboratory Exhaust Mixed-Flow Inline Belt Drive With 1X3 Mixing Box; UNIT_HEIGHT=4' - 6"; UNIT_HEIGHT*.75=3' - 4 1/2"; UNIT_OD=3' - 6 1/2"; UNIT_RAD+((A/2)+.25")=3' - 11 1/2"; UNIT_RAD+((A/2)+.25")+4"=4' - 3 1/2"; UNIT_RADIUS=1' - 9 1/4"; UNIT_RADIUS*.6=1' - 7 1/8"; UNIT_RADIUS+4"=2' - 1 1/4"
- 300_QMXVP-27L-1X3_Mixing_Box: (A/2)+.25"=2' - 2 1/4"; (A/2)-2"=2' - 0"; (NOZZLE_HEIGHT-(NOZZLE_HEIGHT/8*2))/2=1' - 10 3/4"; (NOZZLE_WB_OD-NOZZLE_TOP_OD)/2=0' - 5 11/32"; -A=-4' - 4"; A=4' - 4"; A+.5=4' - 4 1/2"; A/2=2' - 2"; B=12' - 4"; B/2=6' - 2"; C=5' - 7"; C/2=2' - 9 1/2"; DUAL_F=11' - 0 1/4"; DUAL_F+1"=11' - 1 1/4"; DUAL_G=10' - 11 1/8"; E=4' - 2 15/16"; GA=0' - 0 3/32"; LONG_RO=17' - 1 1/16"; MB_A=5' - 8"; MB_HT=4' - 2 7/16"; MB_HT+.25"=4' - 2 11/16"; MB_HT-2.75"=3' - 11 11/16"; MB_HT/2=2' - 1 7/32"; Model=QMXVP-1X3_Mixing Box; NOZZLE_BOTTOM_ID=3' - 2 5/16"; NOZZLE_BOTTOM_RAD=1' - 7 5/32"; NOZZLE_HEIGHT=5' - 0 5/8"; NOZZLE_HEIGHT/7*2=1' - 3 5/32"; NOZZLE_SIZE=27' - 0"; NOZZLE_TOP_OD=3' - 3 11/16"; NOZZLE_TOP_RAD=1' - 7 27/32"; NOZZLE_WB/4=1' - 0 3/16"; NOZZLE_WB_OD=5' - 1"; NOZZLE_WB_RAD=2' - 6 1/2"; NOZZLE_WB_RAD-2"=2' - 4 1/2"; RO=3' - 8 3/4"; RO/2=1' - 10 3/8"; RO2/2=1' - 10 3/8"; TRANSITION_TOP=6' - 5 1/4"; TRIPLE_F+1"=17' - 9"; TRIP_F=17' - 8"; TRIP_G=17' - 7 5/16"; TYPE=0' - 0"; Type Comments=Vari-Plume Laboratory Exhaust Mixed-Flow Inline Belt Drive With 1X3 Mixing Box; UNIT_HEIGHT=4' - 6"; UNIT_HEIGHT*.75=3' - 4 1/2"; UNIT_OD=3' - 6 1/2"; UNIT_RAD+((A/2)+.25")=3' - 11 1/2"; UNIT_RAD+((A/2)+.25")+4"=4' - 3 1/2"; UNIT_RADIUS=1' - 9 1/4"; UNIT_RADIUS*.6=1' - 7 1/8"; UNIT_RADIUS+4"=2' - 1 1/4"
- 330_QMXHPVP-27H-1X3_Mixing_Box: (A/2)+.25"=2' - 4 1/4"; (A/2)-2"=2' - 2"; (NOZZLE_HEIGHT-(NOZZLE_HEIGHT/8*2))/2=1' - 10 3/4"; (NOZZLE_WB_OD-NOZZLE_TOP_OD)/2=0' - 5 11/32"; -A=-4' - 8"; A=4' - 8"; A+.5=4' - 8 1/2"; A/2=2' - 4"; B=12' - 10"; B/2=6' - 5"; C=6' - 1"; C/2=3' - 0 1/2"; DUAL_F=11' - 4 1/4"; DUAL_F+1"=11' - 5 1/4"; DUAL_G=11' - 3 1/8"; E=4' - 6 13/16"; GA=0' - 0 3/32"; LONG_RO=17' - 5 1/16"; MB_A=6' - 1"; MB_HT=4' - 5 11/16"; MB_HT+.25"=4' - 5 15/16"; MB_HT-2.75"=4' - 2 15/16"; MB_HT/2=2' - 2 27/32"; Model=QMXHPVP-1X3_Mixing Box; NOZZLE_BOTTOM_ID=3' - 2 5/16"; NOZZLE_BOTTOM_RAD=1' - 7 5/32"; NOZZLE_HEIGHT=5' - 0 5/8"; NOZZLE_HEIGHT/7*2=1' - 3 5/32"; NOZZLE_SIZE=27' - 0"; NOZZLE_TOP_OD=3' - 3 11/16"; NOZZLE_TOP_RAD=1' - 7 27/32"; NOZZLE_WB/4=1' - 0 3/16"; NOZZLE_WB_OD=5' - 1"; NOZZLE_WB_RAD=2' - 6 1/2"; NOZZLE_WB_RAD-2"=2' - 4 1/2"; RO=4' - 0 5/8"; RO/2=2' - 0 5/16"; RO2/2=2' - 0 5/16"; TRANSITION_TOP=7' - 5 3/4"; TRIPLE_F+1"=18' - 1"; TRIP_F=18' - 0"; TRIP_G=17' - 11 5/16"; TYPE=1' - 0"; Type Comments=Vari-Plume Laboratory Exhaust Mixed-Flow High Pressure Inline Belt Drive With 1X3 Mixing Box; UNIT_HEIGHT=4' - 10 1/2"; UNIT_HEIGHT*.75=3' - 7 7/8"; UNIT_OD=3' - 10 3/4"; UNIT_RAD+((A/2)+.25")=4' - 3 5/8"; UNIT_RAD+((A/2)+.25")+4"=4' - 7 5/8"; UNIT_RADIUS=1' - 11 3/8"; UNIT_RADIUS*.6=1' - 9 1/32"; UNIT_RADIUS+4"=2' - 3 3/8"
- 330_QMXHPVP-27L-1X3_Mixing_Box: (A/2)+.25"=2' - 4 1/4"; (A/2)-2"=2' - 2"; (NOZZLE_HEIGHT-(NOZZLE_HEIGHT/8*2))/2=1' - 10 3/4"; (NOZZLE_WB_OD-NOZZLE_TOP_OD)/2=0' - 5 11/32"; -A=-4' - 8"; A=4' - 8"; A+.5=4' - 8 1/2"; A/2=2' - 4"; B=12' - 10"; B/2=6' - 5"; C=6' - 1"; C/2=3' - 0 1/2"; DUAL_F=11' - 4 1/4"; DUAL_F+1"=11' - 5 1/4"; DUAL_G=11' - 3 1/8"; E=4' - 6 13/16"; GA=0' - 0 3/32"; LONG_RO=17' - 5 1/16"; MB_A=6' - 1"; MB_HT=4' - 5 11/16"; MB_HT+.25"=4' - 5 15/16"; MB_HT-2.75"=4' - 2 15/16"; MB_HT/2=2' - 2 27/32"; Model=QMXHPVP-1X3_Mixing Box; NOZZLE_BOTTOM_ID=3' - 2 5/16"; NOZZLE_BOTTOM_RAD=1' - 7 5/32"; NOZZLE_HEIGHT=5' - 0 5/8"; NOZZLE_HEIGHT/7*2=1' - 3 5/32"; NOZZLE_SIZE=27' - 0"; NOZZLE_TOP_OD=3' - 3 11/16"; NOZZLE_TOP_RAD=1' - 7 27/32"; NOZZLE_WB/4=1' - 0 3/16"; NOZZLE_WB_OD=5' - 1"; NOZZLE_WB_RAD=2' - 6 1/2"; NOZZLE_WB_RAD-2"=2' - 4 1/2"; RO=4' - 0 5/8"; RO/2=2' - 0 5/16"; RO2/2=2' - 0 5/16"; TRANSITION_TOP=7' - 5 3/4"; TRIPLE_F+1"=18' - 1"; TRIP_F=18' - 0"; TRIP_G=17' - 11 5/16"; TYPE=1' - 0"; Type Comments=Vari-Plume Laboratory Exhaust Mixed-Flow High Pressure Inline Belt Drive With 1X3 Mixing Box; UNIT_HEIGHT=4' - 10 1/2"; UNIT_HEIGHT*.75=3' - 7 7/8"; UNIT_OD=3' - 10 3/4"; UNIT_RAD+((A/2)+.25")=4' - 3 5/8"; UNIT_RAD+((A/2)+.25")+4"=4' - 7 5/8"; UNIT_RADIUS=1' - 11 3/8"; UNIT_RADIUS*.6=1' - 9 1/32"; UNIT_RADIUS+4"=2' - 3 3/8"
- 330_QMXVP-27H-1X3_Mixing_Box: (A/2)+.25"=2' - 4 1/4"; (A/2)-2"=2' - 2"; (NOZZLE_HEIGHT-(NOZZLE_HEIGHT/8*2))/2=1' - 10 3/4"; (NOZZLE_WB_OD-NOZZLE_TOP_OD)/2=0' - 5 11/32"; -A=-4' - 8"; A=4' - 8"; A+.5=4' - 8 1/2"; A/2=2' - 4"; B=12' - 10"; B/2=6' - 5"; C=6' - 1"; C/2=3' - 0 1/2"; DUAL_F=11' - 4 1/4"; DUAL_F+1"=11' - 5 1/4"; DUAL_G=11' - 3 1/8"; E=4' - 6 13/16"; GA=0' - 0 3/32"; LONG_RO=17' - 5 1/16"; MB_A=6' - 1"; MB_HT=4' - 5 11/16"; MB_HT+.25"=4' - 5 15/16"; MB_HT-2.75"=4' - 2 15/16"; MB_HT/2=2' - 2 27/32"; Model=QMXVP-1X3_Mixing Box; NOZZLE_BOTTOM_ID=3' - 2 5/16"; NOZZLE_BOTTOM_RAD=1' - 7 5/32"; NOZZLE_HEIGHT=5' - 0 5/8"; NOZZLE_HEIGHT/7*2=1' - 3 5/32"; NOZZLE_SIZE=27' - 0"; NOZZLE_TOP_OD=3' - 3 11/16"; NOZZLE_TOP_RAD=1' - 7 27/32"; NOZZLE_WB/4=1' - 0 3/16"; NOZZLE_WB_OD=5' - 1"; NOZZLE_WB_RAD=2' - 6 1/2"; NOZZLE_WB_RAD-2"=2' - 4 1/2"; RO=4' - 0 5/8"; RO/2=2' - 0 5/16"; RO2/2=2' - 0 5/16"; TRANSITION_TOP=7' - 5 3/4"; TRIPLE_F+1"=18' - 1"; TRIP_F=18' - 0"; TRIP_G=17' - 11 5/16"; TYPE=0' - 0"; Type Comments=Vari-Plume Laboratory Exhaust Mixed-Flow Inline Belt Drive With 1X3 Mixing Box; UNIT_HEIGHT=4' - 10 1/2"; UNIT_HEIGHT*.75=3' - 7 7/8"; UNIT_OD=3' - 10 3/4"; UNIT_RAD+((A/2)+.25")=4' - 3 5/8"; UNIT_RAD+((A/2)+.25")+4"=4' - 7 5/8"; UNIT_RADIUS=1' - 11 3/8"; UNIT_RADIUS*.6=1' - 9 1/32"; UNIT_RADIUS+4"=2' - 3 3/8"
- 330_QMXVP-27L-1X3_Mixing_Box: (A/2)+.25"=2' - 4 1/4"; (A/2)-2"=2' - 2"; (NOZZLE_HEIGHT-(NOZZLE_HEIGHT/8*2))/2=1' - 10 3/4"; (NOZZLE_WB_OD-NOZZLE_TOP_OD)/2=0' - 5 11/32"; -A=-4' - 8"; A=4' - 8"; A+.5=4' - 8 1/2"; A/2=2' - 4"; B=12' - 10"; B/2=6' - 5"; C=6' - 1"; C/2=3' - 0 1/2"; DUAL_F=11' - 4 1/4"; DUAL_F+1"=11' - 5 1/4"; DUAL_G=11' - 3 1/8"; E=4' - 6 13/16"; GA=0' - 0 3/32"; LONG_RO=17' - 5 1/16"; MB_A=6' - 1"; MB_HT=4' - 5 11/16"; MB_HT+.25"=4' - 5 15/16"; MB_HT-2.75"=4' - 2 15/16"; MB_HT/2=2' - 2 27/32"; Model=QMXVP-1X3_Mixing Box; NOZZLE_BOTTOM_ID=3' - 2 5/16"; NOZZLE_BOTTOM_RAD=1' - 7 5/32"; NOZZLE_HEIGHT=5' - 0 5/8"; NOZZLE_HEIGHT/7*2=1' - 3 5/32"; NOZZLE_SIZE=27' - 0"; NOZZLE_TOP_OD=3' - 3 11/16"; NOZZLE_TOP_RAD=1' - 7 27/32"; NOZZLE_WB/4=1' - 0 3/16"; NOZZLE_WB_OD=5' - 1"; NOZZLE_WB_RAD=2' - 6 1/2"; NOZZLE_WB_RAD-2"=2' - 4 1/2"; RO=4' - 0 5/8"; RO/2=2' - 0 5/16"; RO2/2=2' - 0 5/16"; TRANSITION_TOP=7' - 5 3/4"; TRIPLE_F+1"=18' - 1"; TRIP_F=18' - 0"; TRIP_G=17' - 11 5/16"; TYPE=0' - 0"; Type Comments=Vari-Plume Laboratory Exhaust Mixed-Flow Inline Belt Drive With 1X3 Mixing Box; UNIT_HEIGHT=4' - 10 1/2"; UNIT_HEIGHT*.75=3' - 7 7/8"; UNIT_OD=3' - 10 3/4"; UNIT_RAD+((A/2)+.25")=4' - 3 5/8"; UNIT_RAD+((A/2)+.25")+4"=4' - 7 5/8"; UNIT_RADIUS=1' - 11 3/8"; UNIT_RADIUS*.6=1' - 9 1/32"; UNIT_RADIUS+4"=2' - 3 3/8"
- 365_QMXHPVP-27H-1X3_Mixing_Box: (A/2)+.25"=2' - 7 1/4"; (A/2)-2"=2' - 5"; (NOZZLE_HEIGHT-(NOZZLE_HEIGHT/8*2))/2=1' - 10 3/4"; (NOZZLE_WB_OD-NOZZLE_TOP_OD)/2=0' - 5 11/32"; -A=-5' - 2"; A=5' - 2"; A+.5=5' - 2 1/2"; A/2=2' - 7"; B=14' - 7"; B/2=7' - 3 1/2"; C=6' - 7"; C/2=3' - 3 1/2"; DUAL_F=13' - 3 3/4"; DUAL_F+1"=13' - 4 3/4"; DUAL_G=13' - 2"; E=5' - 0 3/4"; GA=0' - 0 3/32"; LONG_RO=20' - 9"; MB_A=6' - 10"; MB_HT=4' - 11 11/16"; MB_HT+.25"=4' - 11 15/16"; MB_HT-2.75"=4' - 8 15/16"; MB_HT/2=2' - 5 27/32"; Model=QMXHPVP-1X3_Mixing Box; NOZZLE_BOTTOM_ID=3' - 2 5/16"; NOZZLE_BOTTOM_RAD=1' - 7 5/32"; NOZZLE_HEIGHT=5' - 0 5/8"; NOZZLE_HEIGHT/7*2=1' - 3 5/32"; NOZZLE_SIZE=27' - 0"; NOZZLE_TOP_OD=3' - 3 11/16"; NOZZLE_TOP_RAD=1' - 7 27/32"; NOZZLE_WB/4=1' - 0 3/16"; NOZZLE_WB_OD=5' - 1"; NOZZLE_WB_RAD=2' - 6 1/2"; NOZZLE_WB_RAD-2"=2' - 4 1/2"; RO=4' - 6 1/2"; RO/2=2' - 3 1/4"; RO2/2=2' - 3 1/4"; TRANSITION_TOP=8' - 8 1/4"; TRIPLE_F+1"=21' - 6"; TRIP_F=21' - 5"; TRIP_G=21' - 3 1/4"; TYPE=1' - 0"; Type Comments=Vari-Plume Laboratory Exhaust Mixed-Flow High Pressure Inline Belt Drive With 1X3 Mixing Box; UNIT_HEIGHT=5' - 4"; UNIT_HEIGHT*.75=4' - 0"; UNIT_OD=4' - 3 3/4"; UNIT_RAD+((A/2)+.25")=4' - 9 1/8"; UNIT_RAD+((A/2)+.25")+4"=5' - 1 1/8"; UNIT_RADIUS=2' - 1 7/8"; UNIT_RADIUS*.6=1' - 11 9/32"; UNIT_RADIUS+4"=2' - 5 7/8"
- 365_QMXHPVP-27L-1X3_Mixing_Box: (A/2)+.25"=2' - 7 1/4"; (A/2)-2"=2' - 5"; (NOZZLE_HEIGHT-(NOZZLE_HEIGHT/8*2))/2=1' - 10 3/4"; (NOZZLE_WB_OD-NOZZLE_TOP_OD)/2=0' - 5 11/32"; -A=-5' - 2"; A=5' - 2"; A+.5=5' - 2 1/2"; A/2=2' - 7"; B=14' - 7"; B/2=7' - 3 1/2"; C=6' - 7"; C/2=3' - 3 1/2"; DUAL_F=13' - 3 3/4"; DUAL_F+1"=13' - 4 3/4"; DUAL_G=13' - 2"; E=5' - 0 3/4"; GA=0' - 0 3/32"; LONG_RO=20' - 9"; MB_A=6' - 10"; MB_HT=4' - 11 11/16"; MB_HT+.25"=4' - 11 15/16"; MB_HT-2.75"=4' - 8 15/16"; MB_HT/2=2' - 5 27/32"; Model=QMXHPVP-1X3_Mixing Box; NOZZLE_BOTTOM_ID=3' - 2 5/16"; NOZZLE_BOTTOM_RAD=1' - 7 5/32"; NOZZLE_HEIGHT=5' - 0 5/8"; NOZZLE_HEIGHT/7*2=1' - 3 5/32"; NOZZLE_SIZE=27' - 0"; NOZZLE_TOP_OD=3' - 3 11/16"; NOZZLE_TOP_RAD=1' - 7 27/32"; NOZZLE_WB/4=1' - 0 3/16"; NOZZLE_WB_OD=5' - 1"; NOZZLE_WB_RAD=2' - 6 1/2"; NOZZLE_WB_RAD-2"=2' - 4 1/2"; RO=4' - 6 1/2"; RO/2=2' - 3 1/4"; RO2/2=2' - 3 1/4"; TRANSITION_TOP=8' - 8 1/4"; TRIPLE_F+1"=21' - 6"; TRIP_F=21' - 5"; TRIP_G=21' - 3 1/4"; TYPE=1' - 0"; Type Comments=Vari-Plume Laboratory Exhaust Mixed-Flow High Pressure Inline Belt Drive With 1X3 Mixing Box; UNIT_HEIGHT=5' - 4"; UNIT_HEIGHT*.75=4' - 0"; UNIT_OD=4' - 3 3/4"; UNIT_RAD+((A/2)+.25")=4' - 9 1/8"; UNIT_RAD+((A/2)+.25")+4"=5' - 1 1/8"; UNIT_RADIUS=2' - 1 7/8"; UNIT_RADIUS*.6=1' - 11 9/32"; UNIT_RADIUS+4"=2' - 5 7/8"
- 365_QMXVP-27H-1X3_Mixing_Box: (A/2)+.25"=2' - 7 1/4"; (A/2)-2"=2' - 5"; (NOZZLE_HEIGHT-(NOZZLE_HEIGHT/8*2))/2=1' - 10 3/4"; (NOZZLE_WB_OD-NOZZLE_TOP_OD)/2=0' - 5 11/32"; -A=-5' - 2"; A=5' - 2"; A+.5=5' - 2 1/2"; A/2=2' - 7"; B=14' - 7"; B/2=7' - 3 1/2"; C=6' - 7"; C/2=3' - 3 1/2"; DUAL_F=13' - 3 3/4"; DUAL_F+1"=13' - 4 3/4"; DUAL_G=13' - 2"; E=5' - 0 3/4"; GA=0' - 0 3/32"; LONG_RO=20' - 9"; MB_A=6' - 10"; MB_HT=4' - 11 11/16"; MB_HT+.25"=4' - 11 15/16"; MB_HT-2.75"=4' - 8 15/16"; MB_HT/2=2' - 5 27/32"; Model=QMXVP-1X3_Mixing Box; NOZZLE_BOTTOM_ID=3' - 2 5/16"; NOZZLE_BOTTOM_RAD=1' - 7 5/32"; NOZZLE_HEIGHT=5' - 0 5/8"; NOZZLE_HEIGHT/7*2=1' - 3 5/32"; NOZZLE_SIZE=27' - 0"; NOZZLE_TOP_OD=3' - 3 11/16"; NOZZLE_TOP_RAD=1' - 7 27/32"; NOZZLE_WB/4=1' - 0 3/16"; NOZZLE_WB_OD=5' - 1"; NOZZLE_WB_RAD=2' - 6 1/2"; NOZZLE_WB_RAD-2"=2' - 4 1/2"; RO=4' - 6 1/2"; RO/2=2' - 3 1/4"; RO2/2=2' - 3 1/4"; TRANSITION_TOP=8' - 8 1/4"; TRIPLE_F+1"=21' - 6"; TRIP_F=21' - 5"; TRIP_G=21' - 3 1/4"; TYPE=0' - 0"; Type Comments=Vari-Plume Laboratory Exhaust Mixed-Flow Inline Belt Drive With 1X3 Mixing Box; UNIT_HEIGHT=5' - 4"; UNIT_HEIGHT*.75=4' - 0"; UNIT_OD=4' - 3 3/4"; UNIT_RAD+((A/2)+.25")=4' - 9 1/8"; UNIT_RAD+((A/2)+.25")+4"=5' - 1 1/8"; UNIT_RADIUS=2' - 1 7/8"; UNIT_RADIUS*.6=1' - 11 9/32"; UNIT_RADIUS+4"=2' - 5 7/8"
- 365_QMXVP-27L-1X3_Mixing_Box: (A/2)+.25"=2' - 7 1/4"; (A/2)-2"=2' - 5"; (NOZZLE_HEIGHT-(NOZZLE_HEIGHT/8*2))/2=1' - 10 3/4"; (NOZZLE_WB_OD-NOZZLE_TOP_OD)/2=0' - 5 11/32"; -A=-5' - 2"; A=5' - 2"; A+.5=5' - 2 1/2"; A/2=2' - 7"; B=14' - 7"; B/2=7' - 3 1/2"; C=6' - 7"; C/2=3' - 3 1/2"; DUAL_F=13' - 3 3/4"; DUAL_F+1"=13' - 4 3/4"; DUAL_G=13' - 2"; E=5' - 0 3/4"; GA=0' - 0 3/32"; LONG_RO=20' - 9"; MB_A=6' - 10"; MB_HT=4' - 11 11/16"; MB_HT+.25"=4' - 11 15/16"; MB_HT-2.75"=4' - 8 15/16"; MB_HT/2=2' - 5 27/32"; Model=QMXVP-1X3_Mixing Box; NOZZLE_BOTTOM_ID=3' - 2 5/16"; NOZZLE_BOTTOM_RAD=1' - 7 5/32"; NOZZLE_HEIGHT=5' - 0 5/8"; NOZZLE_HEIGHT/7*2=1' - 3 5/32"; NOZZLE_SIZE=27' - 0"; NOZZLE_TOP_OD=3' - 3 11/16"; NOZZLE_TOP_RAD=1' - 7 27/32"; NOZZLE_WB/4=1' - 0 3/16"; NOZZLE_WB_OD=5' - 1"; NOZZLE_WB_RAD=2' - 6 1/2"; NOZZLE_WB_RAD-2"=2' - 4 1/2"; RO=4' - 6 1/2"; RO/2=2' - 3 1/4"; RO2/2=2' - 3 1/4"; TRANSITION_TOP=8' - 8 1/4"; TRIPLE_F+1"=21' - 6"; TRIP_F=21' - 5"; TRIP_G=21' - 3 1/4"; TYPE=0' - 0"; Type Comments=Vari-Plume Laboratory Exhaust Mixed-Flow Inline Belt Drive With 1X3 Mixing Box; UNIT_HEIGHT=5' - 4"; UNIT_HEIGHT*.75=4' - 0"; UNIT_OD=4' - 3 3/4"; UNIT_RAD+((A/2)+.25")=4' - 9 1/8"; UNIT_RAD+((A/2)+.25")+4"=5' - 1 1/8"; UNIT_RADIUS=2' - 1 7/8"; UNIT_RADIUS*.6=1' - 11 9/32"; UNIT_RADIUS+4"=2' - 5 7/8"
- 402_QMXHPVP-27H-1X3_Mixing_Box: (A/2)+.25"=2' - 9 3/4"; (A/2)-2"=2' - 7 1/2"; (NOZZLE_HEIGHT-(NOZZLE_HEIGHT/8*2))/2=1' - 10 3/4"; (NOZZLE_WB_OD-NOZZLE_TOP_OD)/2=0' - 5 11/32"; -A=-5' - 7"; A=5' - 7"; A+.5=5' - 7 1/2"; A/2=2' - 9 1/2"; B=15' - 3"; B/2=7' - 7 1/2"; C=7' - 4"; C/2=3' - 8"; DUAL_F=13' - 8 3/4"; DUAL_F+1"=13' - 9 3/4"; DUAL_G=13' - 7"; E=5' - 5 3/4"; GA=0' - 0 3/32"; LONG_RO=21' - 2 1/8"; MB_A=7' - 6"; MB_HT=5' - 5 15/16"; MB_HT+.25"=5' - 6 3/16"; MB_HT-2.75"=5' - 3 3/16"; MB_HT/2=2' - 8 31/32"; Model=QMXHPVP-1X3_Mixing Box; NOZZLE_BOTTOM_ID=3' - 2 5/16"; NOZZLE_BOTTOM_RAD=1' - 7 5/32"; NOZZLE_HEIGHT=5' - 0 5/8"; NOZZLE_HEIGHT/7*2=1' - 3 5/32"; NOZZLE_SIZE=27' - 0"; NOZZLE_TOP_OD=3' - 3 11/16"; NOZZLE_TOP_RAD=1' - 7 27/32"; NOZZLE_WB/4=1' - 0 3/16"; NOZZLE_WB_OD=5' - 1"; NOZZLE_WB_RAD=2' - 6 1/2"; NOZZLE_WB_RAD-2"=2' - 4 1/2"; RO=4' - 11 7/16"; RO/2=2' - 5 23/32"; RO2/2=2' - 5 23/32"; TRANSITION_TOP=9' - 10 3/4"; TRIPLE_F+1"=21' - 11"; TRIP_F=21' - 10"; TRIP_G=21' - 8 3/8"; TYPE=1' - 0"; Type Comments=Vari-Plume Laboratory Exhaust Mixed-Flow High Pressure Inline Belt Drive With 1X3 Mixing Box; UNIT_HEIGHT=5' - 8 1/2"; UNIT_HEIGHT*.75=4' - 3 3/8"; UNIT_OD=4' - 8 15/16"; UNIT_RAD+((A/2)+.25")=5' - 2 7/32"; UNIT_RAD+((A/2)+.25")+4"=5' - 6 7/32"; UNIT_RADIUS=2' - 4 15/32"; UNIT_RADIUS*.6=2' - 1 5/8"; UNIT_RADIUS+4"=2' - 8 15/32"
- 402_QMXHPVP-27L-1X3_Mixing_Box: (A/2)+.25"=2' - 9 3/4"; (A/2)-2"=2' - 7 1/2"; (NOZZLE_HEIGHT-(NOZZLE_HEIGHT/8*2))/2=1' - 10 3/4"; (NOZZLE_WB_OD-NOZZLE_TOP_OD)/2=0' - 5 11/32"; -A=-5' - 7"; A=5' - 7"; A+.5=5' - 7 1/2"; A/2=2' - 9 1/2"; B=15' - 3"; B/2=7' - 7 1/2"; C=7' - 4"; C/2=3' - 8"; DUAL_F=13' - 8 3/4"; DUAL_F+1"=13' - 9 3/4"; DUAL_G=13' - 7"; E=5' - 5 3/4"; GA=0' - 0 3/32"; LONG_RO=21' - 2 1/8"; MB_A=7' - 6"; MB_HT=5' - 5 15/16"; MB_HT+.25"=5' - 6 3/16"; MB_HT-2.75"=5' - 3 3/16"; MB_HT/2=2' - 8 31/32"; Model=QMXHPVP-1X3_Mixing Box; NOZZLE_BOTTOM_ID=3' - 2 5/16"; NOZZLE_BOTTOM_RAD=1' - 7 5/32"; NOZZLE_HEIGHT=5' - 0 5/8"; NOZZLE_HEIGHT/7*2=1' - 3 5/32"; NOZZLE_SIZE=27' - 0"; NOZZLE_TOP_OD=3' - 3 11/16"; NOZZLE_TOP_RAD=1' - 7 27/32"; NOZZLE_WB/4=1' - 0 3/16"; NOZZLE_WB_OD=5' - 1"; NOZZLE_WB_RAD=2' - 6 1/2"; NOZZLE_WB_RAD-2"=2' - 4 1/2"; RO=4' - 11 7/16"; RO/2=2' - 5 23/32"; RO2/2=2' - 5 23/32"; TRANSITION_TOP=9' - 10 3/4"; TRIPLE_F+1"=21' - 11"; TRIP_F=21' - 10"; TRIP_G=21' - 8 3/8"; TYPE=1' - 0"; Type Comments=Vari-Plume Laboratory Exhaust Mixed-Flow High Pressure Inline Belt Drive With 1X3 Mixing Box; UNIT_HEIGHT=5' - 8 1/2"; UNIT_HEIGHT*.75=4' - 3 3/8"; UNIT_OD=4' - 8 15/16"; UNIT_RAD+((A/2)+.25")=5' - 2 7/32"; UNIT_RAD+((A/2)+.25")+4"=5' - 6 7/32"; UNIT_RADIUS=2' - 4 15/32"; UNIT_RADIUS*.6=2' - 1 5/8"; UNIT_RADIUS+4"=2' - 8 15/32"
- 402_QMXVP-27H-1X3_Mixing_Box: (A/2)+.25"=2' - 9 3/4"; (A/2)-2"=2' - 7 1/2"; (NOZZLE_HEIGHT-(NOZZLE_HEIGHT/8*2))/2=1' - 10 3/4"; (NOZZLE_WB_OD-NOZZLE_TOP_OD)/2=0' - 5 11/32"; -A=-5' - 7"; A=5' - 7"; A+.5=5' - 7 1/2"; A/2=2' - 9 1/2"; B=15' - 3"; B/2=7' - 7 1/2"; C=7' - 4"; C/2=3' - 8"; DUAL_F=13' - 8 3/4"; DUAL_F+1"=13' - 9 3/4"; DUAL_G=13' - 7"; E=5' - 5 3/4"; GA=0' - 0 3/32"; LONG_RO=21' - 2 1/8"; MB_A=7' - 6"; MB_HT=5' - 5 15/16"; MB_HT+.25"=5' - 6 3/16"; MB_HT-2.75"=5' - 3 3/16"; MB_HT/2=2' - 8 31/32"; Model=QMXVP-1X3_Mixing Box; NOZZLE_BOTTOM_ID=3' - 2 5/16"; NOZZLE_BOTTOM_RAD=1' - 7 5/32"; NOZZLE_HEIGHT=5' - 0 5/8"; NOZZLE_HEIGHT/7*2=1' - 3 5/32"; NOZZLE_SIZE=27' - 0"; NOZZLE_TOP_OD=3' - 3 11/16"; NOZZLE_TOP_RAD=1' - 7 27/32"; NOZZLE_WB/4=1' - 0 3/16"; NOZZLE_WB_OD=5' - 1"; NOZZLE_WB_RAD=2' - 6 1/2"; NOZZLE_WB_RAD-2"=2' - 4 1/2"; RO=4' - 11 7/16"; RO/2=2' - 5 23/32"; RO2/2=2' - 5 23/32"; TRANSITION_TOP=9' - 10 3/4"; TRIPLE_F+1"=21' - 11"; TRIP_F=21' - 10"; TRIP_G=21' - 8 3/8"; TYPE=0' - 0"; Type Comments=Vari-Plume Laboratory Exhaust Mixed-Flow Inline Belt Drive With 1X3 Mixing Box; UNIT_HEIGHT=5' - 8 1/2"; UNIT_HEIGHT*.75=4' - 3 3/8"; UNIT_OD=4' - 8 15/16"; UNIT_RAD+((A/2)+.25")=5' - 2 7/32"; UNIT_RAD+((A/2)+.25")+4"=5' - 6 7/32"; UNIT_RADIUS=2' - 4 15/32"; UNIT_RADIUS*.6=2' - 1 5/8"; UNIT_RADIUS+4"=2' - 8 15/32"
- 402_QMXVP-27L-1X3_Mixing_Box: (A/2)+.25"=2' - 9 3/4"; (A/2)-2"=2' - 7 1/2"; (NOZZLE_HEIGHT-(NOZZLE_HEIGHT/8*2))/2=1' - 10 3/4"; (NOZZLE_WB_OD-NOZZLE_TOP_OD)/2=0' - 5 11/32"; -A=-5' - 7"; A=5' - 7"; A+.5=5' - 7 1/2"; A/2=2' - 9 1/2"; B=15' - 3"; B/2=7' - 7 1/2"; C=7' - 4"; C/2=3' - 8"; DUAL_F=13' - 8 3/4"; DUAL_F+1"=13' - 9 3/4"; DUAL_G=13' - 7"; E=5' - 5 3/4"; GA=0' - 0 3/32"; LONG_RO=21' - 2 1/8"; MB_A=7' - 6"; MB_HT=5' - 5 15/16"; MB_HT+.25"=5' - 6 3/16"; MB_HT-2.75"=5' - 3 3/16"; MB_HT/2=2' - 8 31/32"; Model=QMXVP-1X3_Mixing Box; NOZZLE_BOTTOM_ID=3' - 2 5/16"; NOZZLE_BOTTOM_RAD=1' - 7 5/32"; NOZZLE_HEIGHT=5' - 0 5/8"; NOZZLE_HEIGHT/7*2=1' - 3 5/32"; NOZZLE_SIZE=27' - 0"; NOZZLE_TOP_OD=3' - 3 11/16"; NOZZLE_TOP_RAD=1' - 7 27/32"; NOZZLE_WB/4=1' - 0 3/16"; NOZZLE_WB_OD=5' - 1"; NOZZLE_WB_RAD=2' - 6 1/2"; NOZZLE_WB_RAD-2"=2' - 4 1/2"; RO=4' - 11 7/16"; RO/2=2' - 5 23/32"; RO2/2=2' - 5 23/32"; TRANSITION_TOP=9' - 10 3/4"; TRIPLE_F+1"=21' - 11"; TRIP_F=21' - 10"; TRIP_G=21' - 8 3/8"; TYPE=0' - 0"; Type Comments=Vari-Plume Laboratory Exhaust Mixed-Flow Inline Belt Drive With 1X3 Mixing Box; UNIT_HEIGHT=5' - 8 1/2"; UNIT_HEIGHT*.75=4' - 3 3/8"; UNIT_OD=4' - 8 15/16"; UNIT_RAD+((A/2)+.25")=5' - 2 7/32"; UNIT_RAD+((A/2)+.25")+4"=5' - 6 7/32"; UNIT_RADIUS=2' - 4 15/32"; UNIT_RADIUS*.6=2' - 1 5/8"; UNIT_RADIUS+4"=2' - 8 15/32"

## geometry (parser evidence)
native form markers: Sweep x2
no freeform markers — native parametric forms only
